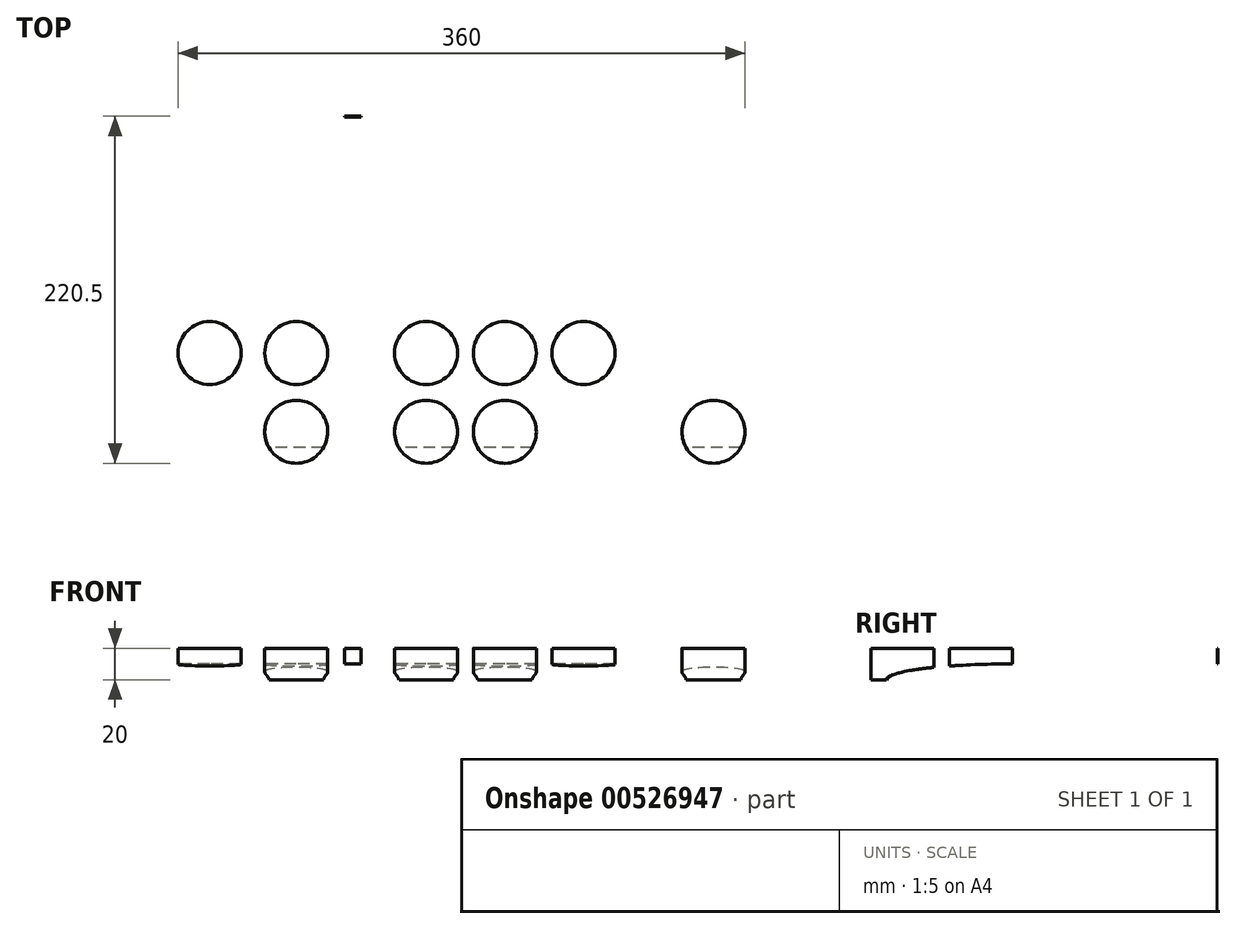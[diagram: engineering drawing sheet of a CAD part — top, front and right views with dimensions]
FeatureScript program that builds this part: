
annotation { "Feature Type Name" : "Feature", "Feature Type Description" : "" }
export const myFeature = defineFeature(function(context is Context, id is Id, definition is map)
    precondition{}
    {
        {
            var Q0;
            Q0=qCreatedBy(makeId("Top.planeOp"),FACE);
            var sketch = newSketch(context, id + "F0", { "sketchPlane" : qUnion([Q0])});
            skLineSegment(sketch, "E0.bottom", {"start": v(-365, 200) * mm, "end": v(365, 200) * mm});
            skLineSegment(sketch, "E0.top", {"start": v(-365, -200) * mm, "end": v(365, -200) * mm});
            skLineSegment(sketch, "E0.left", {"start": v(-365, 200) * mm, "end": v(-365, -200) * mm});
            skLineSegment(sketch, "E0.right", {"start": v(365, 200) * mm, "end": v(365, -200) * mm});
            skPoint(sketch, "E0.middle", {"position": v(0, 0) * mm});
            skEllipticalArc(sketch, "E1", {});
            skEllipticalArc(sketch, "E2.MirrorCS", {});
            skEllipticalArc(sketch, "E3.MirrorCS", {});
            skEllipticalArc(sketch, "E4.MirrorCS", {});
            skLineSegment(sketch, "E5", {"start": v(-365, 200) * mm, "end": v(-105, 200) * mm});
            skLineSegment(sketch, "E6", {"start": v(-365, 200) * mm, "end": v(-365, 50) * mm});
            skLineSegment(sketch, "E7", {"start": v(-365, -200) * mm, "end": v(-365, -50) * mm});
            skLineSegment(sketch, "E8", {"start": v(-365, -200) * mm, "end": v(-182.5, -200) * mm});
            skLineSegment(sketch, "E9", {"start": v(365, 200) * mm, "end": v(105, 200) * mm});
            skLineSegment(sketch, "E10", {"start": v(182.5, -200.11) * mm, "end": v(365, -200) * mm});
            skPoint(sketch, "E11", {"position": v(0, 200) * mm});
            skLineSegment(sketch, "E12", {"start": v(0, 200) * mm, "end": v(-130, 200) * mm});
            skLineSegment(sketch, "E13.MirrorCS", {"start": v(0, -200) * mm, "end": v(-130, -200) * mm});
            skLineSegment(sketch, "E14.MirrorCS", {"start": v(5, 200) * mm, "end": v(130, 200) * mm});
            skLineSegment(sketch, "E15.MirrorCS", {"start": v(-72.5, -200) * mm, "end": v(52.5, -200) * mm});
            skCircle(sketch, "E16", {"center": v(-278.75, 100) * mm, "radius": 20 * mm});
            skCircle(sketch, "E17", {"center": v(-223.75, 150) * mm, "radius": 20 * mm});
            skCircle(sketch, "E18", {"center": v(-223.75, 100) * mm, "radius": 20 * mm});
            skCircle(sketch, "E19", {"center": v(-141.25, 100) * mm, "radius": 20 * mm});
            skCircle(sketch, "E20", {"center": v(-141.25, 150) * mm, "radius": 20 * mm});
            skCircle(sketch, "E21", {"center": v(-91.25, 100) * mm, "radius": 20 * mm});
            skCircle(sketch, "E22", {"center": v(-91.25, 150) * mm, "radius": 20 * mm});
            skCircle(sketch, "E23", {"center": v(-41.25, 100) * mm, "radius": 20 * mm});
            skCircle(sketch, "E24.MirrorC", {"center": v(-41.25, 150) * mm, "radius": 20 * mm});
            skCircle(sketch, "E25.MirrorC", {"center": v(-278.75, -100) * mm, "radius": 20 * mm});
            skCircle(sketch, "E26.MirrorC", {"center": v(-223.75, -150) * mm, "radius": 20 * mm});
            skCircle(sketch, "E27.MirrorC", {"center": v(-223.75, -100) * mm, "radius": 20 * mm});
            skCircle(sketch, "E28.MirrorC", {"center": v(-141.25, -100) * mm, "radius": 20 * mm});
            skCircle(sketch, "E29.MirrorC", {"center": v(-141.25, -150) * mm, "radius": 20 * mm});
            skCircle(sketch, "E30.MirrorC", {"center": v(-91.25, -100) * mm, "radius": 20 * mm});
            skCircle(sketch, "E31.MirrorC", {"center": v(-41.25, -100) * mm, "radius": 20 * mm});
            skCircle(sketch, "E32.MirrorC", {"center": v(-91.25, -150) * mm, "radius": 20 * mm});
            skCircle(sketch, "E33.MirrorC", {"center": v(-41.25, -150) * mm, "radius": 20 * mm});
            skCircle(sketch, "E34.MirrorC", {"center": v(-222.5, -10) * mm, "radius": 20 * mm});
            skLineSegment(sketch, "E35.bottom", {"start": v(210, 15) * mm, "end": v(-210, 15) * mm});
            skLineSegment(sketch, "E35.top", {"start": v(210, -15) * mm, "end": v(-210, -15) * mm});
            skLineSegment(sketch, "E35.left", {"start": v(210, 15) * mm, "end": v(210, -15) * mm});
            skLineSegment(sketch, "E35.right", {"start": v(-210, 15) * mm, "end": v(-210, -15) * mm});
            skLineSegment(sketch, "E36", {"start": v(-365, -50) * mm, "end": v(365, -50) * mm});
            skLineSegment(sketch, "E37", {"start": v(-365, 50) * mm, "end": v(365, 50) * mm});
            skLineSegment(sketch, "E38", {"start": v(-182.5, -200) * mm, "end": v(-182.5, -40.61) * mm});
            skLineSegment(sketch, "E39", {"start": v(0, -200) * mm, "end": v(0, -50) * mm});
            skLineSegment(sketch, "E40", {"start": v(182.5, -200.11) * mm, "end": v(182.4, -40.7) * mm});
            skLineSegment(sketch, "E41.trimOffspring", {"start": v(-182.5, 40.61) * mm, "end": v(-182.5, 200) * mm});
            skLineSegment(sketch, "E42.trimOffspring", {"start": v(-182.5, -15) * mm, "end": v(-182.5, 15) * mm});
            skLineSegment(sketch, "E43.trimOffspring", {"start": v(182.39, -15) * mm, "end": v(182.37, 15) * mm});
            skLineSegment(sketch, "E44.trimOffspring", {"start": v(182.35, 40.73) * mm, "end": v(182.25, 200) * mm});
            skCircle(sketch, "E45", {"center": v(-272.5, 10) * mm, "radius": 20 * mm});
            skCircle(sketch, "E46.MirrorC", {"center": v(-322.5, -8.74) * mm, "radius": 20 * mm});
            skCircle(sketch, "E47.MirrorC", {"center": v(-142.5, -10) * mm, "radius": 20 * mm});
            skCircle(sketch, "E48.MirrorC", {"center": v(-92.5, 10) * mm, "radius": 20 * mm});
            skCircle(sketch, "E49.MirrorC", {"center": v(-42.5, -8.74) * mm, "radius": 20 * mm});
            skCircle(sketch, "E50.MirrorC", {"center": v(42.5, -8.74) * mm, "radius": 20 * mm});
            skCircle(sketch, "E51.MirrorC", {"center": v(142.5, -10) * mm, "radius": 20 * mm});
            skCircle(sketch, "E52.MirrorC", {"center": v(92.5, 10) * mm, "radius": 20 * mm});
            skCircle(sketch, "E53.MirrorC", {"center": v(222.5, -10) * mm, "radius": 20 * mm});
            skCircle(sketch, "E54.MirrorC", {"center": v(272.5, 10) * mm, "radius": 20 * mm});
            skCircle(sketch, "E55.MirrorC", {"center": v(322.5, -8.74) * mm, "radius": 20 * mm});
            skCircle(sketch, "E56.MirrorC", {"center": v(223.75, -100) * mm, "radius": 20 * mm});
            skCircle(sketch, "E57.MirrorC", {"center": v(223.75, -150) * mm, "radius": 20 * mm});
            skCircle(sketch, "E58.MirrorC", {"center": v(278.75, -100) * mm, "radius": 20 * mm});
            skCircle(sketch, "E59.MirrorC", {"center": v(141.25, -100) * mm, "radius": 20 * mm});
            skCircle(sketch, "E60.MirrorC", {"center": v(141.25, -150) * mm, "radius": 20 * mm});
            skCircle(sketch, "E61.MirrorC", {"center": v(91.25, -150) * mm, "radius": 20 * mm});
            skCircle(sketch, "E62.MirrorC", {"center": v(91.25, -100) * mm, "radius": 20 * mm});
            skCircle(sketch, "E63.MirrorC", {"center": v(41.25, -100) * mm, "radius": 20 * mm});
            skCircle(sketch, "E64.MirrorC", {"center": v(41.25, -150) * mm, "radius": 20 * mm});
            skCircle(sketch, "E65.MirrorC", {"center": v(41.25, 100) * mm, "radius": 20 * mm});
            skCircle(sketch, "E66.MirrorC", {"center": v(91.25, 100) * mm, "radius": 20 * mm});
            skCircle(sketch, "E67.MirrorC", {"center": v(141.25, 100) * mm, "radius": 20 * mm});
            skCircle(sketch, "E68.MirrorC", {"center": v(223.75, 100) * mm, "radius": 20 * mm});
            skCircle(sketch, "E69.MirrorC", {"center": v(278.75, 100) * mm, "radius": 20 * mm});
            skCircle(sketch, "E70.MirrorC", {"center": v(223.75, 150) * mm, "radius": 20 * mm});
            skCircle(sketch, "E71.MirrorC", {"center": v(141.25, 150) * mm, "radius": 20 * mm});
            skCircle(sketch, "E72.MirrorC", {"center": v(91.25, 150) * mm, "radius": 20 * mm});
            skCircle(sketch, "E73.MirrorC", {"center": v(41.25, 150) * mm, "radius": 20 * mm});
            const initialGuessF0  = {"E1": [0.215000023161019, -0.00011114199246731203, 0, -1, 0.20000000103052606, 0.15, 6.249845643425636, 1.5707963267948966], "E2.MirrorCS": [-0.215, -0.00011114199246737072, 0, -1, 0.2, 0.15, 4.711833270393751, 0.03333950926130193], "E3.MirrorCS": [-0.215, 0.00011114199246727815, 0, 1, 0.2, 0.15, 6.249845797918284, 1.5707963267948966], "E4.MirrorCS": [0.215, 0.00011114199246735796, 0, 1, 0.2, 0.15, 4.711277560231201, 0.03333950926130226]};
            skSetInitialGuess(sketch, initialGuessF0);
            skSolve(sketch);
        }
        {
            var Q0;
            Q0=qCreatedBy(makeId("Top.planeOp"),FACE);
            cPlane(context, id + "F1", {"entities" : qUnion([Q0]), "cplaneType" : CPlaneType.OFFSET, "offset" : 20 * mm, "width" : 150 * mm, "height" : 150 * mm});
        }
        {
            var Q0;
            Q0=qCreatedBy(id+"F1.planeOp",FACE);
            var sketch = newSketch(context, id + "F2", { "sketchPlane" : qUnion([Q0])});
            skLineSegment(sketch, "E74.bottom", {"start": v(0, 0) * mm, "end": v(365, 0) * mm});
            skLineSegment(sketch, "E74.top", {"start": v(0, -200) * mm, "end": v(210, -200) * mm});
            skLineSegment(sketch, "E74.left", {"start": v(0, 0) * mm, "end": v(0, -200) * mm});
            skLineSegment(sketch, "E75", {"start": v(0, -15) * mm, "end": v(364.58, -15) * mm});
            skLineSegment(sketch, "E76", {"start": v(0, -170) * mm, "end": v(294.02, -170) * mm});
            skLineSegment(sketch, "E77", {"start": v(330, 0) * mm, "end": v(330, -128.4) * mm});
            skLineSegment(sketch, "E78", {"start": v(215, 0) * mm, "end": v(215, -200) * mm});
            skPoint(sketch, "E79", {"position": v(215, -200) * mm});
            skPoint(sketch, "E80", {"position": v(365, 0) * mm});
            skLineSegment(sketch, "E81", {"start": v(275, 0) * mm, "end": v(275, -183.3) * mm});
            skLineSegment(sketch, "E82", {"start": v(275, -140) * mm, "end": v(322.12, -140) * mm});
            skPoint(sketch, "E83", {"position": v(215, -170) * mm});
            skPoint(sketch, "E84", {"position": v(330, 0) * mm});
            skPoint(sketch, "E85", {"position": v(275, -140) * mm});
            skPoint(sketch, "E86", {"position": v(330, -140) * mm});
            skPoint(sketch, "E87", {"position": v(275, -185) * mm});
            skLineSegment(sketch, "E88", {"start": v(315, -149.07) * mm, "end": v(315, 0) * mm});
            skLineSegment(sketch, "E89", {"start": v(210, 0) * mm, "end": v(210, -200) * mm});
            skEllipticalArc(sketch, "E90.trimOffspring", {});
            skEllipticalArc(sketch, "E91", {});
            skPoint(sketch, "E92.orphan", {"position": v(365, -170) * mm});
            skPoint(sketch, "E93.trimOffspring.end.orphan", {"position": v(330, -200) * mm});
            skPoint(sketch, "E94.orphan", {"position": v(365, -200) * mm});
            skPoint(sketch, "E95.orphan", {"position": v(365, -15) * mm});
            skLineSegment(sketch, "E96.MirrorCS", {"start": v(0, 0) * mm, "end": v(-365, 0) * mm});
            skLineSegment(sketch, "E97.MirrorCS", {"start": v(0, -15) * mm, "end": v(-364.58, -15) * mm});
            skLineSegment(sketch, "E98.MirrorCS", {"start": v(0, -170) * mm, "end": v(-294.02, -170) * mm});
            skLineSegment(sketch, "E99.MirrorCS", {"start": v(0, -200) * mm, "end": v(-210, -200) * mm});
            skLineSegment(sketch, "E100.MirrorCS", {"start": v(-210, 0) * mm, "end": v(-210, -200) * mm});
            skLineSegment(sketch, "E101.MirrorCS", {"start": v(-215, 0) * mm, "end": v(-215, -200) * mm});
            skEllipticalArc(sketch, "E102.MirrorCS", {});
            skEllipticalArc(sketch, "E103.MirrorCS", {});
            skLineSegment(sketch, "E104.MirrorCS", {"start": v(-275, 0) * mm, "end": v(-275, -183.3) * mm});
            skLineSegment(sketch, "E105.MirrorCS", {"start": v(-275, -140) * mm, "end": v(-322.12, -140) * mm});
            skLineSegment(sketch, "E106.MirrorCS", {"start": v(-315, -149.07) * mm, "end": v(-315, 0) * mm});
            skLineSegment(sketch, "E107.MirrorCS", {"start": v(-330, 0) * mm, "end": v(-330, -128.4) * mm});
            skLineSegment(sketch, "E108.MirrorCS", {"start": v(0, 15) * mm, "end": v(-364.58, 15) * mm});
            skLineSegment(sketch, "E109.MirrorCS", {"start": v(0, 15) * mm, "end": v(364.58, 15) * mm});
            skEllipticalArc(sketch, "E110.MirrorCS", {});
            skLineSegment(sketch, "E111.MirrorCS", {"start": v(-330, 0) * mm, "end": v(-330, 128.4) * mm});
            skLineSegment(sketch, "E112.MirrorCS", {"start": v(-315, 149.07) * mm, "end": v(-315, 0) * mm});
            skLineSegment(sketch, "E113.MirrorCS", {"start": v(-275, 0) * mm, "end": v(-275, 183.3) * mm});
            skLineSegment(sketch, "E114.MirrorCS", {"start": v(-215, 0) * mm, "end": v(-215, 200) * mm});
            skLineSegment(sketch, "E115.MirrorCS", {"start": v(-210, 0) * mm, "end": v(-210, 200) * mm});
            skLineSegment(sketch, "E116.MirrorCS", {"start": v(0, 0) * mm, "end": v(0, 200) * mm});
            skLineSegment(sketch, "E117.MirrorCS", {"start": v(210, 0) * mm, "end": v(210, 200) * mm});
            skLineSegment(sketch, "E118.MirrorCS", {"start": v(215, 0) * mm, "end": v(215, 200) * mm});
            skLineSegment(sketch, "E119.MirrorCS", {"start": v(275, 0) * mm, "end": v(275, 183.3) * mm});
            skLineSegment(sketch, "E120.MirrorCS", {"start": v(315, 149.07) * mm, "end": v(315, 0) * mm});
            skLineSegment(sketch, "E121.MirrorCS", {"start": v(330, 0) * mm, "end": v(330, 128.4) * mm});
            skEllipticalArc(sketch, "E122.MirrorCS", {});
            skEllipticalArc(sketch, "E123.MirrorCS", {});
            skEllipticalArc(sketch, "E124.MirrorCS", {});
            skLineSegment(sketch, "E125.MirrorCS", {"start": v(-275, 140) * mm, "end": v(-322.12, 140) * mm});
            skLineSegment(sketch, "E126.MirrorCS", {"start": v(0, 170) * mm, "end": v(-294.02, 170) * mm});
            skLineSegment(sketch, "E127.MirrorCS", {"start": v(0, 170) * mm, "end": v(294.02, 170) * mm});
            skLineSegment(sketch, "E128.MirrorCS", {"start": v(0, 200) * mm, "end": v(210, 200) * mm});
            skLineSegment(sketch, "E129.MirrorCS", {"start": v(0, 200) * mm, "end": v(-210, 200) * mm});
            skLineSegment(sketch, "E130.MirrorCS", {"start": v(275, 140) * mm, "end": v(322.12, 140) * mm});
            const initialGuessF2  = {"E90.trimOffspring": [0.215, 0, 1, 0, 0.115, 0.17, 4.71238898038469, 6.283185307179586], "E91": [0.215, 0, 0, -1, 0.2, 0.15, 6.249845797918284, 1.5707963267948966], "E102.MirrorCS": [-0.215, 0, -1, 0, 0.115, 0.17, 6.283185307179586, 1.5707963267948966], "E103.MirrorCS": [-0.215, 0, 0, -1, 0.2, 0.15, 4.71238898038469, 0.03333950926130225], "E110.MirrorCS": [-0.215, 0, 0, 1, 0.2, 0.15, 6.249845797918284, 1.5707963267948966], "E122.MirrorCS": [0.215, 0, 0, 1, 0.2, 0.15, 4.71238898038469, 0.03333950926130225], "E123.MirrorCS": [0.215, 0, 1, 0, 0.115, 0.17, 6.283185307179586, 1.5707963267948966], "E124.MirrorCS": [-0.215, 0, -1, 0, 0.115, 0.17, 4.71238898038469, 6.283185307179586]};
            skSetInitialGuess(sketch, initialGuessF2);
            skSolve(sketch);
        }
        {
            var Q0;
            Q0=qCreatedBy(makeId("Right.planeOp"),FACE);
            var sketch = newSketch(context, id + "F3", { "sketchPlane" : qUnion([Q0])});
            skPoint(sketch, "E131.middle", {"position": v(0, 20) * mm});
            skPoint(sketch, "E132", {"position": v(170, 0) * mm});
            skPoint(sketch, "E133", {"position": v(160, 0) * mm});
            skLineSegment(sketch, "E134.bottom", {"start": v(15, 10.07) * mm, "end": v(80, 10.07) * mm});
            skPoint(sketch, "E135", {"position": v(80, 10.07) * mm});
            skEllipticalArc(sketch, "E136", {});
            skEllipticalArc(sketch, "E137", {});
            skLineSegment(sketch, "E138", {"start": v(0, 20) * mm, "end": v(0, 10.04) * mm});
            skLineSegment(sketch, "E139", {"start": v(0, 20) * mm, "end": v(200, 20) * mm});
            skLineSegment(sketch, "E140", {"start": v(200, 20) * mm, "end": v(0, 20) * mm});
            skLineSegment(sketch, "E141", {"start": v(160, 0) * mm, "end": v(170, 0) * mm});
            skPoint(sketch, "E142.orphan", {"position": v(-200, 20) * mm});
            skLineSegment(sketch, "E143.MirrorCS", {"start": v(-200, 20) * mm, "end": v(0, 20) * mm});
            skLineSegment(sketch, "E144.MirrorCS", {"start": v(-15, 10.07) * mm, "end": v(-80, 10.07) * mm});
            skEllipticalArc(sketch, "E145.MirrorCS", {});
            skLineSegment(sketch, "E146.MirrorCS", {"start": v(-160, 0) * mm, "end": v(-170, 0) * mm});
            skEllipticalArc(sketch, "E147.MirrorCS", {});
            skLineSegment(sketch, "E148.top", {"start": v(-15, 12) * mm, "end": v(15, 12) * mm});
            skLineSegment(sketch, "E148.left", {"start": v(-15, 10.07) * mm, "end": v(-15, 12) * mm});
            skLineSegment(sketch, "E148.right", {"start": v(15, 10.07) * mm, "end": v(15, 12) * mm});
            skLineSegment(sketch, "E149.bottom", {"start": v(15, 18) * mm, "end": v(-15, 18) * mm});
            skLineSegment(sketch, "E149.top", {"start": v(15, 12) * mm, "end": v(-15, 12) * mm});
            skLineSegment(sketch, "E149.left", {"start": v(15, 18) * mm, "end": v(15, 12) * mm});
            skLineSegment(sketch, "E149.right", {"start": v(-15, 18) * mm, "end": v(-15, 12) * mm});
            skLineSegment(sketch, "E150", {"start": v(170, 0) * mm, "end": v(170.12, 20) * mm});
            skLineSegment(sketch, "E151", {"start": v(-170, 0) * mm, "end": v(-170.12, 20) * mm});
            skLineSegment(sketch, "E152", {"start": v(-15, 12) * mm, "end": v(-15, 10.07) * mm});
            skLineSegment(sketch, "E153.bottom", {"start": v(-200, 20) * mm, "end": v(-170, 20) * mm});
            skLineSegment(sketch, "E153.top", {"start": v(-200, 0) * mm, "end": v(-170, 0) * mm});
            skLineSegment(sketch, "E153.left", {"start": v(-200, 20) * mm, "end": v(-200, 0) * mm});
            skLineSegment(sketch, "E153.right", {"start": v(-170, 20) * mm, "end": v(-170, 0) * mm});
            skLineSegment(sketch, "E154.MirrorCS", {"start": v(200, 0) * mm, "end": v(170, 0) * mm});
            skLineSegment(sketch, "E155.MirrorCS", {"start": v(200, 20) * mm, "end": v(200, 0) * mm});
            skLineSegment(sketch, "E156", {"start": v(80, 10.07) * mm, "end": v(80, 20) * mm});
            skLineSegment(sketch, "E157", {"start": v(160, 0) * mm, "end": v(160, 20) * mm});
            skLineSegment(sketch, "E158", {"start": v(149.2, 20) * mm, "end": v(149.2, 5.05) * mm});
            skLineSegment(sketch, "E159", {"start": v(140.08, 20) * mm, "end": v(140.08, 6.65) * mm});
            skLineSegment(sketch, "E160", {"start": v(128.23, 20) * mm, "end": v(128.23, 8.04) * mm});
            skLineSegment(sketch, "E161", {"start": v(102.69, 20) * mm, "end": v(102.69, 9.66) * mm});
            skLineSegment(sketch, "E162.MirrorCS", {"start": v(-80, 10.07) * mm, "end": v(-80, 20) * mm});
            skLineSegment(sketch, "E163.MirrorCS", {"start": v(-102.69, 20) * mm, "end": v(-102.69, 9.66) * mm});
            skLineSegment(sketch, "E164.MirrorCS", {"start": v(-128.23, 20) * mm, "end": v(-128.23, 8.04) * mm});
            skLineSegment(sketch, "E165.MirrorCS", {"start": v(-140.08, 20) * mm, "end": v(-140.08, 6.65) * mm});
            skLineSegment(sketch, "E166.MirrorCS", {"start": v(-149.2, 20) * mm, "end": v(-149.2, 5.05) * mm});
            skLineSegment(sketch, "E167.MirrorCS", {"start": v(-160, 0) * mm, "end": v(-160, 20) * mm});
            skLineSegment(sketch, "E168", {"start": v(45, 20) * mm, "end": v(45, 10.07) * mm});
            skLineSegment(sketch, "E169.MirrorCS", {"start": v(-45, 20) * mm, "end": v(-45, 10.07) * mm});
            const initialGuessF3  = {"E136": [0.17012490332126617, 0.02, -0.006245044279577429, -0.9999804995208388, 0.020000390017188747, 0.02987581400604767, 6.283185307179586, 1.580124845260153], "E137": [0.08, 0, 0, 1, 0.01007139225942586, 0.08, 4.71238898038469, 6.283185307179586], "E145.MirrorCS": [-0.08, 0, 0, 1, 0.01007139225942586, 0.08, 6.283185307179586, 1.5707963267948966], "E147.MirrorCS": [-0.17012490332126617, 0.02, 0.006245044279579518, -0.9999804995208388, 0.020000390017188747, 0.02987581400604767, 4.703060461919433, 6.283185307179586]};
            skSetInitialGuess(sketch, initialGuessF3);
            skSolve(sketch);
        }
        {
            var Q0;
            Q0=qCreatedBy(makeId("Front.planeOp"),FACE);
            var sketch = newSketch(context, id + "F4", { "sketchPlane" : qUnion([Q0])});
            skLineSegment(sketch, "E170", {"start": v(0, 20) * mm, "end": v(365, 20) * mm});
            skPoint(sketch, "E171", {"position": v(210, 20) * mm});
            skLineSegment(sketch, "E172", {"start": v(210, 18) * mm, "end": v(210, 12) * mm});
            skPoint(sketch, "E173", {"position": v(315, 20) * mm});
            skLineSegment(sketch, "E174", {"start": v(315, 18) * mm, "end": v(315, 0) * mm});
            skLineSegment(sketch, "E175", {"start": v(0, 12) * mm, "end": v(0, 20) * mm});
            skLineSegment(sketch, "E176", {"start": v(210, 12) * mm, "end": v(0, 12) * mm});
            skPoint(sketch, "E177", {"position": v(365.07, 0) * mm});
            skPoint(sketch, "E178", {"position": v(365, 20) * mm});
            skEllipticalArc(sketch, "E179", {});
            skLineSegment(sketch, "E180", {"start": v(315, 18) * mm, "end": v(210, 18) * mm});
            skLineSegment(sketch, "E181.MirrorCS", {"start": v(0, 20) * mm, "end": v(-365, 20) * mm});
            skLineSegment(sketch, "E182.MirrorCS", {"start": v(-210, 12) * mm, "end": v(0, 12) * mm});
            skLineSegment(sketch, "E183.MirrorCS", {"start": v(-210, 18) * mm, "end": v(-210, 12) * mm});
            skLineSegment(sketch, "E184.MirrorCS", {"start": v(-315, 18) * mm, "end": v(-210, 18) * mm});
            skLineSegment(sketch, "E185.MirrorCS", {"start": v(-315, 18) * mm, "end": v(-315, 0) * mm});
            skEllipticalArc(sketch, "E186.MirrorCS", {});
            skPoint(sketch, "E187", {"position": v(245, 20) * mm});
            skPoint(sketch, "E188", {"position": v(245, 10.07) * mm});
            skPoint(sketch, "E189", {"position": v(325, 20) * mm});
            skPoint(sketch, "E190", {"position": v(335, 20) * mm});
            skLineSegment(sketch, "E191", {"start": v(335, 20) * mm, "end": v(335, 10.07) * mm});
            skLineSegment(sketch, "E192", {"start": v(335, 10.07) * mm, "end": v(0, 10.07) * mm});
            skLineSegment(sketch, "E193.MirrorCS", {"start": v(-335, 10.07) * mm, "end": v(0, 10.07) * mm});
            skLineSegment(sketch, "E194.MirrorCS", {"start": v(-335, 20) * mm, "end": v(-335, 10.07) * mm});
            skLineSegment(sketch, "E195", {"start": v(365, 20) * mm, "end": v(365.07, 0) * mm});
            skLineSegment(sketch, "E196", {"start": v(315, 0) * mm, "end": v(365.07, 0) * mm});
            skLineSegment(sketch, "E197.MirrorCS", {"start": v(-365, 20) * mm, "end": v(-365.07, 0) * mm});
            skLineSegment(sketch, "E198.MirrorCS", {"start": v(-315, 0) * mm, "end": v(-365.07, 0) * mm});
            skLineSegment(sketch, "E199", {"start": v(335, 10.07) * mm, "end": v(335, 1.67) * mm});
            skLineSegment(sketch, "E200.MirrorCS", {"start": v(-335, 10.07) * mm, "end": v(-335, 1.67) * mm});
            skLineSegment(sketch, "E201", {"start": v(-315, 18) * mm, "end": v(-315, 20) * mm});
            skLineSegment(sketch, "E202", {"start": v(-210, 18) * mm, "end": v(-210, 20) * mm});
            skLineSegment(sketch, "E203.MirrorCS", {"start": v(210, 18) * mm, "end": v(210, 20) * mm});
            skLineSegment(sketch, "E204.MirrorCS", {"start": v(315, 18) * mm, "end": v(315, 20) * mm});
            skPoint(sketch, "E205", {"position": v(275, 20) * mm});
            skPoint(sketch, "E206.MirrorP", {"position": v(-275, 20) * mm});
            skLineSegment(sketch, "E207", {"start": v(275, 20) * mm, "end": v(275, 18) * mm});
            skLineSegment(sketch, "E208.MirrorCS", {"start": v(-275, 20) * mm, "end": v(-275, 18) * mm});
            skPoint(sketch, "E209", {"position": v(-333.25, 14.9) * mm});
            skPoint(sketch, "E210", {"position": v(-218.12, 14.9) * mm});
            skPoint(sketch, "E211", {"position": v(-78.75, 14.9) * mm});
            const initialGuessF4  = {"E179": [0.315, 0.02, 1, 0, 0.05, 0.02, 4.71238898038469, 0], "E186.MirrorCS": [-0.315, 0.02, -1, 0, 0.05, 0.02, 0, 1.5707963267948966]};
            skSetInitialGuess(sketch, initialGuessF4);
            skSolve(sketch);
        }
        {
            var Q0;
            Q0=qSketchRegion(id+"F2",true);
            var Q1;
            {var subQ0=sQuery(id+"F2.wireOp",EDGE,"E125.MirrorCS");var subQ1=sQuery(id+"F2.wireOp",EDGE,"E112.MirrorCS");var subQ2=makeQuery(id+"F2.imprint","INTERSECT",VERTEX,{"derivedFrom":[subQ1,subQ0]});Q1=makeQuery(id+"F2.imprint","IMPRINT",FACE,{"disambiguationData":[TD([[makeQuery(id+"F2.imprint","IMPRINT",EDGE,{"disambiguationData":[TD([[subQ2,-1.0]])],"derivedFrom":subQ1}),1.0]])]});}
            var Q2;
            {var subQ0=sQuery(id+"F2.wireOp",EDGE,"E124.MirrorCS");var subQ1=sQuery(id+"F2.wireOp",EDGE,"E113.MirrorCS");var subQ2=makeQuery(id+"F2.imprint","INTERSECT",VERTEX,{"derivedFrom":[subQ1,subQ0]});Q2=makeQuery(id+"F2.imprint","IMPRINT",FACE,{"disambiguationData":[TD([[makeQuery(id+"F2.imprint","IMPRINT",EDGE,{"disambiguationData":[TD([[subQ2,-1.0]])],"derivedFrom":subQ1}),-1.0]])]});}
            var Q3;
            {var subQ0=sQuery(id+"F2.wireOp",EDGE,"E123.MirrorCS");var subQ1=sQuery(id+"F2.wireOp",EDGE,"E119.MirrorCS");var subQ2=makeQuery(id+"F2.imprint","INTERSECT",VERTEX,{"derivedFrom":[subQ1,subQ0]});Q3=makeQuery(id+"F2.imprint","IMPRINT",FACE,{"disambiguationData":[TD([[makeQuery(id+"F2.imprint","IMPRINT",EDGE,{"disambiguationData":[TD([[subQ2,-1.0]])],"derivedFrom":subQ1}),1.0]])]});}
            var Q4;
            {var subQ0=sQuery(id+"F2.wireOp",EDGE,"E130.MirrorCS");var subQ1=sQuery(id+"F2.wireOp",EDGE,"E120.MirrorCS");var subQ2=makeQuery(id+"F2.imprint","INTERSECT",VERTEX,{"derivedFrom":[subQ1,subQ0]});Q4=makeQuery(id+"F2.imprint","IMPRINT",FACE,{"disambiguationData":[TD([[makeQuery(id+"F2.imprint","IMPRINT",EDGE,{"disambiguationData":[TD([[subQ2,-1.0]])],"derivedFrom":subQ1}),-1.0]])]});}
            var Q5;
            {var subQ0=sQuery(id+"F2.wireOp",EDGE,"E90.trimOffspring");var subQ1=sQuery(id+"F2.wireOp",EDGE,"E82");var subQ2=makeQuery(id+"F2.imprint","INTERSECT",VERTEX,{"derivedFrom":[subQ1,subQ0]});Q5=makeQuery(id+"F2.imprint","IMPRINT",FACE,{"disambiguationData":[TD([[makeQuery(id+"F2.imprint","IMPRINT",EDGE,{"disambiguationData":[TD([[subQ2,-1.0]])],"derivedFrom":subQ1}),1.0]])]});}
            var Q6;
            {var subQ1=sQuery(id+"F2.wireOp",EDGE,"E76");var subQ3=sQuery(id+"F2.wireOp",EDGE,"E81");var subQ4=makeQuery(id+"F2.imprint","INTERSECT",VERTEX,{"derivedFrom":[subQ1,subQ3]});Q6=makeQuery(id+"F2.imprint","IMPRINT",FACE,{"disambiguationData":[TD([[makeQuery(id+"F2.imprint","IMPRINT",EDGE,{"disambiguationData":[TD([[subQ4,1.0]])],"derivedFrom":subQ3}),-1.0]])]});}
            var Q7;
            {var subQ1=sQuery(id+"F2.wireOp",EDGE,"E98.MirrorCS");var subQ3=sQuery(id+"F2.wireOp",EDGE,"E104.MirrorCS");var subQ4=makeQuery(id+"F2.imprint","INTERSECT",VERTEX,{"derivedFrom":[subQ1,subQ3]});Q7=makeQuery(id+"F2.imprint","IMPRINT",FACE,{"disambiguationData":[TD([[makeQuery(id+"F2.imprint","IMPRINT",EDGE,{"disambiguationData":[TD([[subQ4,1.0]])],"derivedFrom":subQ3}),1.0]])]});}
            var Q8;
            {var subQ0=sQuery(id+"F2.wireOp",EDGE,"E106.MirrorCS");var subQ1=sQuery(id+"F2.wireOp",EDGE,"E102.MirrorCS");var subQ2=makeQuery(id+"F2.imprint","INTERSECT",VERTEX,{"derivedFrom":[subQ1,subQ0]});Q8=makeQuery(id+"F2.imprint","IMPRINT",FACE,{"disambiguationData":[TD([[makeQuery(id+"F2.imprint","IMPRINT",EDGE,{"disambiguationData":[TD([[subQ2,-1.0]])],"derivedFrom":subQ1}),-1.0]])]});}
            extrude(context, id + "F5", {"entities" : qUnion([Q0, Q1, Q2, Q3, Q4, Q5, Q6, Q7, Q8]), "oppositeDirection" : true, "depth" : 20 * mm, "offsetDistance" : 25 * mm});
        }
        {
            var Q0;
            {var subQ0=sQuery(id+"F3.wireOp",EDGE,"E149.right");Q0=makeQuery(id+"F3.imprint","IMPRINT",FACE,{"disambiguationData":[TD([[makeQuery(id+"F3.imprint","IMPRINT",EDGE,{"derivedFrom":subQ0}),-1.0]])]});}
            var Q1;
            {var subQ0=sQuery(id+"F3.wireOp",EDGE,"E149.left");Q1=makeQuery(id+"F3.imprint","IMPRINT",FACE,{"disambiguationData":[TD([[makeQuery(id+"F3.imprint","IMPRINT",EDGE,{"derivedFrom":subQ0}),1.0]])]});}
            extrude(context, id + "F6", {"entities" : qUnion([Q0, Q1]), "operationType" : NewBodyOperationType.ADD, "depth" : 420 * mm, "offsetDistance" : 25 * mm, "symmetric" : true});
        }
        {
            var Q0;
            {var subQ0=sQuery(id+"F3.wireOp",EDGE,"E156");Q0=makeQuery(id+"F3.imprint","IMPRINT",FACE,{"disambiguationData":[TD([[makeQuery(id+"F3.imprint","IMPRINT",EDGE,{"derivedFrom":subQ0}),-1.0]])]});}
            var Q1;
            {var subQ0=sQuery(id+"F3.wireOp",EDGE,"E160");Q1=makeQuery(id+"F3.imprint","IMPRINT",FACE,{"disambiguationData":[TD([[makeQuery(id+"F3.imprint","IMPRINT",EDGE,{"derivedFrom":subQ0}),-1.0]])]});}
            var Q2;
            {var subQ0=sQuery(id+"F3.wireOp",EDGE,"E159");Q2=makeQuery(id+"F3.imprint","IMPRINT",FACE,{"disambiguationData":[TD([[makeQuery(id+"F3.imprint","IMPRINT",EDGE,{"derivedFrom":subQ0}),-1.0]])]});}
            var Q3;
            {var subQ0=sQuery(id+"F3.wireOp",EDGE,"E158");Q3=makeQuery(id+"F3.imprint","IMPRINT",FACE,{"disambiguationData":[TD([[makeQuery(id+"F3.imprint","IMPRINT",EDGE,{"derivedFrom":subQ0}),-1.0]])]});}
            var Q4;
            {var subQ0=sQuery(id+"F3.wireOp",EDGE,"E157");Q4=makeQuery(id+"F3.imprint","IMPRINT",FACE,{"disambiguationData":[TD([[makeQuery(id+"F3.imprint","IMPRINT",EDGE,{"derivedFrom":subQ0}),1.0]])]});}
            var Q5;
            Q5=makeQuery(id+"F3.imprint","IMPRINT",FACE,{"disambiguationData":[TD([[makeQuery(id+"F3.imprint","IMPRINT",EDGE,{"derivedFrom":sQuery(id+"F3.wireOp",EDGE,"E141")}),1.0]])]});
            var Q6;
            {var subQ0=sQuery(id+"F3.wireOp",EDGE,"E162.MirrorCS");Q6=makeQuery(id+"F3.imprint","IMPRINT",FACE,{"disambiguationData":[TD([[makeQuery(id+"F3.imprint","IMPRINT",EDGE,{"derivedFrom":subQ0}),1.0]])]});}
            var Q7;
            {var subQ0=sQuery(id+"F3.wireOp",EDGE,"E163.MirrorCS");Q7=makeQuery(id+"F3.imprint","IMPRINT",FACE,{"disambiguationData":[TD([[makeQuery(id+"F3.imprint","IMPRINT",EDGE,{"derivedFrom":subQ0}),-1.0]])]});}
            var Q8;
            {var subQ0=sQuery(id+"F3.wireOp",EDGE,"E164.MirrorCS");Q8=makeQuery(id+"F3.imprint","IMPRINT",FACE,{"disambiguationData":[TD([[makeQuery(id+"F3.imprint","IMPRINT",EDGE,{"derivedFrom":subQ0}),-1.0]])]});}
            var Q9;
            {var subQ0=sQuery(id+"F3.wireOp",EDGE,"E165.MirrorCS");Q9=makeQuery(id+"F3.imprint","IMPRINT",FACE,{"disambiguationData":[TD([[makeQuery(id+"F3.imprint","IMPRINT",EDGE,{"derivedFrom":subQ0}),-1.0]])]});}
            var Q10;
            {var subQ0=sQuery(id+"F3.wireOp",EDGE,"E166.MirrorCS");Q10=makeQuery(id+"F3.imprint","IMPRINT",FACE,{"disambiguationData":[TD([[makeQuery(id+"F3.imprint","IMPRINT",EDGE,{"derivedFrom":subQ0}),-1.0]])]});}
            var Q11;
            Q11=makeQuery(id+"F3.imprint","IMPRINT",FACE,{"disambiguationData":[TD([[makeQuery(id+"F3.imprint","IMPRINT",EDGE,{"derivedFrom":sQuery(id+"F3.wireOp",EDGE,"E146.MirrorCS")}),-1.0]])]});
            var Q12;
            {var subQ0=sQuery(id+"F3.wireOp",EDGE,"E156");Q12=makeQuery(id+"F3.imprint","IMPRINT",FACE,{"disambiguationData":[TD([[makeQuery(id+"F3.imprint","IMPRINT",EDGE,{"derivedFrom":subQ0}),1.0]])]});}
            var Q13;
            {var subQ0=sQuery(id+"F3.wireOp",EDGE,"E162.MirrorCS");Q13=makeQuery(id+"F3.imprint","IMPRINT",FACE,{"disambiguationData":[TD([[makeQuery(id+"F3.imprint","IMPRINT",EDGE,{"derivedFrom":subQ0}),-1.0]])]});}
            extrude(context, id + "F7", {"entities" : qUnion([Q0, Q1, Q2, Q3, Q4, Q5, Q6, Q7, Q8, Q9, Q10, Q11, Q12, Q13]), "operationType" : NewBodyOperationType.ADD, "depth" : 520 * mm, "offsetDistance" : 25 * mm, "symmetric" : true});
        }
        {
            var Q0;
            Q0=makeQuery(id+"F4.imprint","IMPRINT",FACE,{"disambiguationData":[TD([[makeQuery(id+"F4.imprint","IMPRINT",EDGE,{"derivedFrom":sQuery(id+"F4.wireOp",EDGE,"E172")}),-1.0]])]});
            var Q1;
            {var subQ1=sQuery(id+"F4.wireOp",EDGE,"E179");Q1=makeQuery(id+"F4.imprint","IMPRINT",FACE,{"disambiguationData":[TD([[makeQuery(id+"F4.imprint","IMPRINT",EDGE,{"derivedFrom":subQ1}),1.0]])]});}
            var Q2;
            {var subQ2=sQuery(id+"F4.wireOp",EDGE,"E175");Q2=makeQuery(id+"F4.imprint","IMPRINT",FACE,{"disambiguationData":[TD([[makeQuery(id+"F4.imprint","IMPRINT",EDGE,{"derivedFrom":subQ2}),1.0]])]});}
            var Q3;
            {var subQ0=sQuery(id+"F4.wireOp",EDGE,"E186.MirrorCS");Q3=makeQuery(id+"F4.imprint","IMPRINT",FACE,{"disambiguationData":[TD([[makeQuery(id+"F4.imprint","IMPRINT",EDGE,{"derivedFrom":subQ0}),1.0]])]});}
            extrude(context, id + "F8", {"entities" : qUnion([Q0, Q1, Q2, Q3]), "operationType" : NewBodyOperationType.ADD, "depth" : 30 * mm, "offsetDistance" : 25 * mm, "symmetric" : true});
        }
        {
            var Q0;
            {var subQ0=sQuery(id+"F3.wireOp",EDGE,"E153.left");var subQ1=sQuery(id+"F3.wireOp",EDGE,"E147.MirrorCS");var subQ2=makeQuery(id+"F3.imprint","INTERSECT",VERTEX,{"derivedFrom":[subQ1,subQ0]});Q0=makeQuery(id+"F3.imprint","IMPRINT",FACE,{"disambiguationData":[TD([[makeQuery(id+"F3.imprint","IMPRINT",EDGE,{"disambiguationData":[TD([[subQ2,-1.0]])],"derivedFrom":subQ1}),-1.0]])]});}
            var Q1;
            {var subQ0=sQuery(id+"F3.wireOp",EDGE,"E155.MirrorCS");var subQ1=sQuery(id+"F3.wireOp",EDGE,"E136");var subQ2=makeQuery(id+"F3.imprint","INTERSECT",VERTEX,{"derivedFrom":[subQ1,subQ0]});Q1=makeQuery(id+"F3.imprint","IMPRINT",FACE,{"disambiguationData":[TD([[makeQuery(id+"F3.imprint","IMPRINT",EDGE,{"disambiguationData":[TD([[subQ2,1.0]])],"derivedFrom":subQ1}),-1.0]])]});}
            var Q2;
            Q2=sQuery(id+"F3.wireOp",EDGE,"E153.left");
            var Q3;
            Q3=sQuery(id+"F3.wireOp",EDGE,"E153.top");
            var Q4;
            Q4=sQuery(id+"F3.wireOp",EDGE,"E147.MirrorCS");
            extrude(context, id + "F9", {"entities" : qUnion([Q0, Q1]), "operationType" : NewBodyOperationType.REMOVE, "surfaceEntities" : qUnion([Q2, Q3, Q4]), "oppositeDirection" : true, "depth" : 730 * mm, "offsetDistance" : 25 * mm, "symmetric" : true});
        }
        {
            var Q0;
            Q0=makeQuery(id+"F4.imprint","IMPRINT",FACE,{"disambiguationData":[TD([[makeQuery(id+"F4.imprint","IMPRINT",EDGE,{"derivedFrom":sQuery(id+"F4.wireOp",EDGE,"E186.MirrorCS")}),-1.0]])]});
            var Q1;
            Q1=makeQuery(id+"F4.imprint","IMPRINT",FACE,{"disambiguationData":[TD([[makeQuery(id+"F4.imprint","IMPRINT",EDGE,{"derivedFrom":sQuery(id+"F4.wireOp",EDGE,"E179")}),-1.0]])]});
            extrude(context, id + "F10", {"entities" : qUnion([Q0, Q1]), "operationType" : NewBodyOperationType.REMOVE, "oppositeDirection" : true, "depth" : 400 * mm, "offsetDistance" : 25 * mm, "symmetric" : true});
        }
        {
            var Q0;
            Q0=makeQuery(id+"F4.imprint","IMPRINT",FACE,{"disambiguationData":[TD([[makeQuery(id+"F4.imprint","IMPRINT",EDGE,{"derivedFrom":sQuery(id+"F4.wireOp",EDGE,"E172")}),-1.0]])]});
            var Q1;
            {var subQ5=sQuery(id+"F4.wireOp",EDGE,"E199");Q1=makeQuery(id+"F4.imprint","IMPRINT",FACE,{"disambiguationData":[TD([[makeQuery(id+"F4.imprint","IMPRINT",EDGE,{"derivedFrom":subQ5}),-1.0]])]});}
            var Q2;
            {var subQ5=sQuery(id+"F4.wireOp",EDGE,"E200.MirrorCS");Q2=makeQuery(id+"F4.imprint","IMPRINT",FACE,{"disambiguationData":[TD([[makeQuery(id+"F4.imprint","IMPRINT",EDGE,{"derivedFrom":subQ5}),1.0]])]});}
            var Q3;
            {var subQ2=sQuery(id+"F4.wireOp",EDGE,"E175");Q3=makeQuery(id+"F4.imprint","IMPRINT",FACE,{"disambiguationData":[TD([[makeQuery(id+"F4.imprint","IMPRINT",EDGE,{"derivedFrom":subQ2}),1.0]])]});}
            var Q4;
            {var subQ0=sQuery(id+"F4.wireOp",EDGE,"E194.MirrorCS");Q4=makeQuery(id+"F4.imprint","IMPRINT",FACE,{"disambiguationData":[TD([[makeQuery(id+"F4.imprint","IMPRINT",EDGE,{"derivedFrom":subQ0}),1.0]])]});}
            var Q5;
            {var subQ1=sQuery(id+"F4.wireOp",EDGE,"E191");Q5=makeQuery(id+"F4.imprint","IMPRINT",FACE,{"disambiguationData":[TD([[makeQuery(id+"F4.imprint","IMPRINT",EDGE,{"derivedFrom":subQ1}),-1.0]])]});}
            extrude(context, id + "F11", {"entities" : qUnion([Q0, Q1, Q2, Q3, Q4, Q5]), "operationType" : NewBodyOperationType.ADD, "depth" : 169 * mm, "offsetDistance" : 25 * mm, "symmetric" : true});
        }
        {
            var Q0;
            Q0=makeQuery(id+"F4.imprint","IMPRINT",FACE,{"disambiguationData":[TD([[makeQuery(id+"F4.imprint","IMPRINT",EDGE,{"derivedFrom":sQuery(id+"F4.wireOp",EDGE,"E180")}),-1.0]])]});
            var Q1;
            Q1=makeQuery(id+"F4.imprint","IMPRINT",FACE,{"disambiguationData":[TD([[makeQuery(id+"F4.imprint","IMPRINT",EDGE,{"derivedFrom":sQuery(id+"F4.wireOp",EDGE,"E184.MirrorCS")}),1.0]])]});
            extrude(context, id + "F12", {"entities" : qUnion([Q0, Q1]), "operationType" : NewBodyOperationType.ADD, "depth" : 295 * mm, "offsetDistance" : 25 * mm, "symmetric" : true});
        }
        {
            var Q0;
            {var subQ0=sQuery(id+"F4.wireOp",EDGE,"E203.MirrorCS");Q0=makeQuery(id+"F4.imprint","IMPRINT",FACE,{"disambiguationData":[TD([[makeQuery(id+"F4.imprint","IMPRINT",EDGE,{"derivedFrom":subQ0}),-1.0]])]});}
            var Q1;
            {var subQ0=sQuery(id+"F4.wireOp",EDGE,"E202");Q1=makeQuery(id+"F4.imprint","IMPRINT",FACE,{"disambiguationData":[TD([[makeQuery(id+"F4.imprint","IMPRINT",EDGE,{"derivedFrom":subQ0}),1.0]])]});}
            extrude(context, id + "F13", {"entities" : qUnion([Q0, Q1]), "operationType" : NewBodyOperationType.ADD, "depth" : 350 * mm, "offsetDistance" : 25 * mm, "symmetric" : true});
        }
        {
            var Q0;
            {var subQ0=sQuery(id+"F2.wireOp",EDGE,"E122.MirrorCS");var subQ1=sQuery(id+"F2.wireOp",EDGE,"E91");Q0=makeQuery(id+"F10.boolean.opBoolean","SPLIT",EDGE,{"disambiguationData":[TD([makeQuery(id+"F9.boolean.opBoolean","COPY",FACE,{"derivedFrom":makeQuery(id+"F9.opExtrude","SWEPT_FACE",FACE,{"disambiguationData":[OSD([sQuery(id+"F3.wireOp",EDGE,"E136")])]})})])],"derivedFrom":makeQuery(id+"F5.opExtrude","CAP_EDGE",EDGE,{"disambiguationData":[OSD([subQ1,subQ0])],"isStart":false})});}
            var Q1;
            {var subQ0=sQuery(id+"F2.wireOp",EDGE,"E122.MirrorCS");var subQ1=sQuery(id+"F2.wireOp",EDGE,"E91");Q1=makeQuery(id+"F10.boolean.opBoolean","SPLIT",EDGE,{"disambiguationData":[TD([makeQuery(id+"F9.boolean.opBoolean","COPY",FACE,{"derivedFrom":makeQuery(id+"F9.opExtrude","SWEPT_FACE",FACE,{"disambiguationData":[OSD([sQuery(id+"F3.wireOp",EDGE,"E147.MirrorCS")])]})})])],"derivedFrom":makeQuery(id+"F5.opExtrude","CAP_EDGE",EDGE,{"disambiguationData":[OSD([subQ1,subQ0])],"isStart":false})});}
            var Q2;
            {var subQ0=sQuery(id+"F2.wireOp",EDGE,"E110.MirrorCS");var subQ1=sQuery(id+"F2.wireOp",EDGE,"E103.MirrorCS");Q2=makeQuery(id+"F10.boolean.opBoolean","SPLIT",EDGE,{"disambiguationData":[TD([makeQuery(id+"F9.boolean.opBoolean","COPY",FACE,{"derivedFrom":makeQuery(id+"F9.opExtrude","SWEPT_FACE",FACE,{"disambiguationData":[OSD([sQuery(id+"F3.wireOp",EDGE,"E147.MirrorCS")])]})})])],"derivedFrom":makeQuery(id+"F5.opExtrude","CAP_EDGE",EDGE,{"disambiguationData":[OSD([subQ1,subQ0])],"isStart":false})});}
            var Q3;
            {var subQ0=sQuery(id+"F2.wireOp",EDGE,"E110.MirrorCS");var subQ1=sQuery(id+"F2.wireOp",EDGE,"E103.MirrorCS");Q3=makeQuery(id+"F10.boolean.opBoolean","SPLIT",EDGE,{"disambiguationData":[TD([makeQuery(id+"F9.boolean.opBoolean","COPY",FACE,{"derivedFrom":makeQuery(id+"F9.opExtrude","SWEPT_FACE",FACE,{"disambiguationData":[OSD([sQuery(id+"F3.wireOp",EDGE,"E136")])]})})])],"derivedFrom":makeQuery(id+"F5.opExtrude","CAP_EDGE",EDGE,{"disambiguationData":[OSD([subQ1,subQ0])],"isStart":false})});}
            fillet(context, id + "F14", {"entities" : qUnion([Q0, Q1, Q2, Q3]), "radius" : 18 * mm, "tangentPropagation" : true, "allowEdgeOverflow" : false});
        }
        {
            var Q0;
            {var subQ0=sQuery(id+"F3.wireOp",EDGE,"E162.MirrorCS");Q0=makeQuery(id+"F3.imprint","IMPRINT",FACE,{"disambiguationData":[TD([[makeQuery(id+"F3.imprint","IMPRINT",EDGE,{"derivedFrom":subQ0}),-1.0]])]});}
            var Q1;
            {var subQ0=sQuery(id+"F3.wireOp",EDGE,"E156");Q1=makeQuery(id+"F3.imprint","IMPRINT",FACE,{"disambiguationData":[TD([[makeQuery(id+"F3.imprint","IMPRINT",EDGE,{"derivedFrom":subQ0}),1.0]])]});}
            extrude(context, id + "F15", {"entities" : qUnion([Q0, Q1]), "operationType" : NewBodyOperationType.ADD, "depth" : 670 * mm, "offsetDistance" : 25 * mm, "symmetric" : true});
        }
        {
            var Q0;
            {var subQ0=sQuery(id+"F3.wireOp",EDGE,"E156");Q0=makeQuery(id+"F3.imprint","IMPRINT",FACE,{"disambiguationData":[TD([[makeQuery(id+"F3.imprint","IMPRINT",EDGE,{"derivedFrom":subQ0}),-1.0]])]});}
            var Q1;
            {var subQ0=sQuery(id+"F3.wireOp",EDGE,"E162.MirrorCS");Q1=makeQuery(id+"F3.imprint","IMPRINT",FACE,{"disambiguationData":[TD([[makeQuery(id+"F3.imprint","IMPRINT",EDGE,{"derivedFrom":subQ0}),1.0]])]});}
            extrude(context, id + "F16", {"entities" : qUnion([Q0, Q1]), "operationType" : NewBodyOperationType.ADD, "depth" : 630 * mm, "offsetDistance" : 25 * mm, "symmetric" : true});
        }
        {
            var Q0;
            {var subQ0=sQuery(id+"F3.wireOp",EDGE,"E166.MirrorCS");Q0=makeQuery(id+"F3.imprint","IMPRINT",FACE,{"disambiguationData":[TD([[makeQuery(id+"F3.imprint","IMPRINT",EDGE,{"derivedFrom":subQ0}),-1.0]])]});}
            var Q1;
            {var subQ0=sQuery(id+"F3.wireOp",EDGE,"E157");Q1=makeQuery(id+"F3.imprint","IMPRINT",FACE,{"disambiguationData":[TD([[makeQuery(id+"F3.imprint","IMPRINT",EDGE,{"derivedFrom":subQ0}),1.0]])]});}
            extrude(context, id + "F17", {"entities" : qUnion([Q0, Q1]), "operationType" : NewBodyOperationType.ADD, "depth" : 550 * mm, "offsetDistance" : 25 * mm, "symmetric" : true});
        }
        {
            var Q0;
            {var subQ0=sQuery(id+"F3.wireOp",EDGE,"E158");Q0=makeQuery(id+"F3.imprint","IMPRINT",FACE,{"disambiguationData":[TD([[makeQuery(id+"F3.imprint","IMPRINT",EDGE,{"derivedFrom":subQ0}),-1.0]])]});}
            var Q1;
            {var subQ0=sQuery(id+"F3.wireOp",EDGE,"E165.MirrorCS");Q1=makeQuery(id+"F3.imprint","IMPRINT",FACE,{"disambiguationData":[TD([[makeQuery(id+"F3.imprint","IMPRINT",EDGE,{"derivedFrom":subQ0}),-1.0]])]});}
            extrude(context, id + "F18", {"entities" : qUnion([Q0, Q1]), "operationType" : NewBodyOperationType.ADD, "depth" : 600 * mm, "offsetDistance" : 25 * mm, "symmetric" : true});
        }
        {
            var Q0;
            {var subQ0=sQuery(id+"F3.wireOp",EDGE,"E159");Q0=makeQuery(id+"F3.imprint","IMPRINT",FACE,{"disambiguationData":[TD([[makeQuery(id+"F3.imprint","IMPRINT",EDGE,{"derivedFrom":subQ0}),-1.0]])]});}
            var Q1;
            {var subQ0=sQuery(id+"F3.wireOp",EDGE,"E164.MirrorCS");Q1=makeQuery(id+"F3.imprint","IMPRINT",FACE,{"disambiguationData":[TD([[makeQuery(id+"F3.imprint","IMPRINT",EDGE,{"derivedFrom":subQ0}),-1.0]])]});}
            extrude(context, id + "F19", {"entities" : qUnion([Q0, Q1]), "operationType" : NewBodyOperationType.ADD, "depth" : 620 * mm, "offsetDistance" : 25 * mm, "symmetric" : true});
        }
        {
            var Q0;
            {var subQ0=sQuery(id+"F3.wireOp",EDGE,"E163.MirrorCS");Q0=makeQuery(id+"F3.imprint","IMPRINT",FACE,{"disambiguationData":[TD([[makeQuery(id+"F3.imprint","IMPRINT",EDGE,{"derivedFrom":subQ0}),-1.0]])]});}
            var Q1;
            {var subQ0=sQuery(id+"F3.wireOp",EDGE,"E160");Q1=makeQuery(id+"F3.imprint","IMPRINT",FACE,{"disambiguationData":[TD([[makeQuery(id+"F3.imprint","IMPRINT",EDGE,{"derivedFrom":subQ0}),-1.0]])]});}
            extrude(context, id + "F20", {"entities" : qUnion([Q0, Q1]), "operationType" : NewBodyOperationType.ADD, "depth" : 620 * mm, "offsetDistance" : 25 * mm, "symmetric" : true});
        }
        {
            var Q0;
            Q0=makeQuery(id+"F5.opExtrude","CAP_EDGE",EDGE,{"disambiguationData":[OSD([sQuery(id+"F2.wireOp",EDGE,"E124.MirrorCS")])],"isStart":false});
            var Q1;
            Q1=makeQuery(id+"F5.opExtrude","CAP_EDGE",EDGE,{"disambiguationData":[OSD([sQuery(id+"F2.wireOp",EDGE,"E123.MirrorCS")])],"isStart":false});
            var Q2;
            Q2=makeQuery(id+"F5.opExtrude","CAP_EDGE",EDGE,{"disambiguationData":[OSD([sQuery(id+"F2.wireOp",EDGE,"E90.trimOffspring")])],"isStart":false});
            var Q3;
            Q3=makeQuery(id+"F5.opExtrude","CAP_EDGE",EDGE,{"disambiguationData":[OSD([sQuery(id+"F2.wireOp",EDGE,"E102.MirrorCS")])],"isStart":false});
            chamfer(context, id + "F21", {"entities" : qUnion([Q0, Q1, Q2, Q3]), "chamferType" : ChamferType.OFFSET_ANGLE, "width" : 15 * mm, "oppositeDirection" : false, "angle" : 35 * degree, "tangentPropagation" : true});
        }
        {
            var Q0;
            {var subQ0=sQuery(id+"F4.wireOp",EDGE,"E198.MirrorCS");var subQ1=sQuery(id+"F4.wireOp",EDGE,"E186.MirrorCS");var subQ2=sQuery(id+"F4.wireOp",EDGE,"E185.MirrorCS");Q0=makeQuery(id+"F11.boolean.opBoolean","MERGE",EDGE,{"derivedFrom":[makeQuery(id+"F8.opExtrude","SWEPT_EDGE",EDGE,{"disambiguationData":[OSD([subQ2,subQ1,subQ0])]}),makeQuery(id+"F11.opExtrude","SWEPT_EDGE",EDGE,{"disambiguationData":[OSD([subQ2,subQ1,subQ0])]})]});}
            chamfer(context, id + "F22", {"entities" : qUnion([Q0]), "chamferType" : ChamferType.OFFSET_ANGLE, "width" : 10 * mm, "oppositeDirection" : false, "angle" : 42 * degree, "tangentPropagation" : true});
        }
        {
            var Q0;
            {var subQ0=sQuery(id+"F4.wireOp",EDGE,"E196");var subQ1=sQuery(id+"F4.wireOp",EDGE,"E179");var subQ2=sQuery(id+"F4.wireOp",EDGE,"E174");Q0=makeQuery(id+"F11.boolean.opBoolean","MERGE",EDGE,{"derivedFrom":[makeQuery(id+"F8.opExtrude","SWEPT_EDGE",EDGE,{"disambiguationData":[OSD([subQ2,subQ1,subQ0])]}),makeQuery(id+"F11.opExtrude","SWEPT_EDGE",EDGE,{"disambiguationData":[OSD([subQ2,subQ1,subQ0])]})]});}
            chamfer(context, id + "F23", {"entities" : qUnion([Q0]), "chamferType" : ChamferType.OFFSET_ANGLE, "width" : 10 * mm, "oppositeDirection" : false, "angle" : 42 * degree, "tangentPropagation" : true});
        }
        {
            var Q0;
            {var subQ0=sQuery(id+"F0.wireOp",EDGE,"E35.top");var subQ1=sQuery(id+"F0.wireOp",EDGE,"E34.MirrorC");var subQ2=makeQuery(id+"F0.imprint","INTERSECT",VERTEX,{"derivedFrom":[subQ1,subQ0]});Q0=makeQuery(id+"F0.imprint","IMPRINT",FACE,{"disambiguationData":[TD([[makeQuery(id+"F0.imprint","IMPRINT",EDGE,{"disambiguationData":[TD([[subQ2,1.0]])],"derivedFrom":subQ1}),1.0]])]});}
            var Q1;
            {var subQ0=sQuery(id+"F0.wireOp",EDGE,"E10");var subQ3=sQuery(id+"F0.wireOp",EDGE,"E1");var subQ5=makeQuery(id+"F0.imprint","INTERSECT",VERTEX,{"disambiguationData":[OD(0.0)],"derivedFrom":[subQ3,subQ0]});Q1=makeQuery(id+"F0.imprint","IMPRINT",FACE,{"disambiguationData":[TD([[makeQuery(id+"F0.imprint","IMPRINT",EDGE,{"disambiguationData":[TD([[subQ5,-1.0]])],"derivedFrom":subQ3}),-1.0]])]});}
            var Q2;
            {var subQ0=sQuery(id+"F0.wireOp",EDGE,"E36");var subQ1=sQuery(id+"F0.wireOp",EDGE,"E0.right");var subQ2=makeQuery(id+"F0.imprint","INTERSECT",VERTEX,{"derivedFrom":[subQ1,subQ0]});Q2=makeQuery(id+"F0.imprint","IMPRINT",FACE,{"disambiguationData":[TD([[makeQuery(id+"F0.imprint","IMPRINT",EDGE,{"disambiguationData":[TD([[subQ2,1.0]])],"derivedFrom":subQ1}),-1.0]])]});}
            var Q3;
            {var subQ1=sQuery(id+"F0.wireOp",EDGE,"E0.left");var subQ3=sQuery(id+"F0.wireOp",EDGE,"E2.MirrorCS");var subQ4=makeQuery(id+"F0.imprint","INTERSECT",VERTEX,{"disambiguationData":[OD(1.0)],"derivedFrom":[subQ1,subQ3]});Q3=makeQuery(id+"F0.imprint","IMPRINT",FACE,{"disambiguationData":[TD([[makeQuery(id+"F0.imprint","IMPRINT",EDGE,{"disambiguationData":[TD([[subQ4,-1.0]])],"derivedFrom":subQ3}),-1.0]])]});}
            var Q4;
            {var subQ1=sQuery(id+"F0.wireOp",EDGE,"E0.left");var subQ3=sQuery(id+"F0.wireOp",EDGE,"E3.MirrorCS");var subQ4=makeQuery(id+"F0.imprint","INTERSECT",VERTEX,{"derivedFrom":[subQ1,subQ3]});Q4=makeQuery(id+"F0.imprint","IMPRINT",FACE,{"disambiguationData":[TD([[makeQuery(id+"F0.imprint","IMPRINT",EDGE,{"disambiguationData":[TD([[subQ4,1.0]])],"derivedFrom":subQ3}),-1.0]])]});}
            var Q5;
            {var subQ0=sQuery(id+"F0.wireOp",EDGE,"E9");var subQ1=sQuery(id+"F0.wireOp",EDGE,"E0.right");var subQ2=makeQuery(id+"F0.imprint","INTERSECT",VERTEX,{"derivedFrom":[subQ1,subQ0]});Q5=makeQuery(id+"F0.imprint","IMPRINT",FACE,{"disambiguationData":[TD([[makeQuery(id+"F0.imprint","IMPRINT",EDGE,{"disambiguationData":[TD([[subQ2,-1.0]])],"derivedFrom":subQ1}),-1.0]])]});}
            var Q6;
            Q6=makeQuery(id+"F0.imprint","IMPRINT",FACE,{"disambiguationData":[TD([[makeQuery(id+"F0.imprint","IMPRINT",EDGE,{"derivedFrom":sQuery(id+"F0.wireOp",EDGE,"E23")}),1.0]])]});
            var Q7;
            Q7=makeQuery(id+"F0.imprint","IMPRINT",FACE,{"disambiguationData":[TD([[makeQuery(id+"F0.imprint","IMPRINT",EDGE,{"derivedFrom":sQuery(id+"F0.wireOp",EDGE,"E21")}),1.0]])]});
            var Q8;
            Q8=makeQuery(id+"F0.imprint","IMPRINT",FACE,{"disambiguationData":[TD([[makeQuery(id+"F0.imprint","IMPRINT",EDGE,{"derivedFrom":sQuery(id+"F0.wireOp",EDGE,"E22")}),1.0]])]});
            var Q9;
            Q9=makeQuery(id+"F0.imprint","IMPRINT",FACE,{"disambiguationData":[TD([[makeQuery(id+"F0.imprint","IMPRINT",EDGE,{"derivedFrom":sQuery(id+"F0.wireOp",EDGE,"E24.MirrorC")}),-1.0]])]});
            var Q10;
            Q10=makeQuery(id+"F0.imprint","IMPRINT",FACE,{"disambiguationData":[TD([[makeQuery(id+"F0.imprint","IMPRINT",EDGE,{"derivedFrom":sQuery(id+"F0.wireOp",EDGE,"E30.MirrorC")}),-1.0]])]});
            var Q11;
            Q11=makeQuery(id+"F0.imprint","IMPRINT",FACE,{"disambiguationData":[TD([[makeQuery(id+"F0.imprint","IMPRINT",EDGE,{"derivedFrom":sQuery(id+"F0.wireOp",EDGE,"E31.MirrorC")}),-1.0]])]});
            var Q12;
            Q12=makeQuery(id+"F0.imprint","IMPRINT",FACE,{"disambiguationData":[TD([[makeQuery(id+"F0.imprint","IMPRINT",EDGE,{"derivedFrom":sQuery(id+"F0.wireOp",EDGE,"E33.MirrorC")}),1.0]])]});
            var Q13;
            Q13=makeQuery(id+"F0.imprint","IMPRINT",FACE,{"disambiguationData":[TD([[makeQuery(id+"F0.imprint","IMPRINT",EDGE,{"derivedFrom":sQuery(id+"F0.wireOp",EDGE,"E32.MirrorC")}),-1.0]])]});
            var Q14;
            Q14=makeQuery(id+"F0.imprint","IMPRINT",FACE,{"disambiguationData":[TD([[makeQuery(id+"F0.imprint","IMPRINT",EDGE,{"derivedFrom":sQuery(id+"F0.wireOp",EDGE,"E19")}),1.0]])]});
            var Q15;
            Q15=makeQuery(id+"F0.imprint","IMPRINT",FACE,{"disambiguationData":[TD([[makeQuery(id+"F0.imprint","IMPRINT",EDGE,{"derivedFrom":sQuery(id+"F0.wireOp",EDGE,"E20")}),1.0]])]});
            var Q16;
            Q16=makeQuery(id+"F0.imprint","IMPRINT",FACE,{"disambiguationData":[TD([[makeQuery(id+"F0.imprint","IMPRINT",EDGE,{"derivedFrom":sQuery(id+"F0.wireOp",EDGE,"E17")}),1.0]])]});
            var Q17;
            Q17=makeQuery(id+"F0.imprint","IMPRINT",FACE,{"disambiguationData":[TD([[makeQuery(id+"F0.imprint","IMPRINT",EDGE,{"derivedFrom":sQuery(id+"F0.wireOp",EDGE,"E18")}),1.0]])]});
            var Q18;
            Q18=makeQuery(id+"F0.imprint","IMPRINT",FACE,{"disambiguationData":[TD([[makeQuery(id+"F0.imprint","IMPRINT",EDGE,{"derivedFrom":sQuery(id+"F0.wireOp",EDGE,"E16")}),1.0]])]});
            var Q19;
            Q19=makeQuery(id+"F0.imprint","IMPRINT",FACE,{"disambiguationData":[TD([[makeQuery(id+"F0.imprint","IMPRINT",EDGE,{"derivedFrom":sQuery(id+"F0.wireOp",EDGE,"E28.MirrorC")}),-1.0]])]});
            var Q20;
            Q20=makeQuery(id+"F0.imprint","IMPRINT",FACE,{"disambiguationData":[TD([[makeQuery(id+"F0.imprint","IMPRINT",EDGE,{"derivedFrom":sQuery(id+"F0.wireOp",EDGE,"E27.MirrorC")}),-1.0]])]});
            var Q21;
            Q21=makeQuery(id+"F0.imprint","IMPRINT",FACE,{"disambiguationData":[TD([[makeQuery(id+"F0.imprint","IMPRINT",EDGE,{"derivedFrom":sQuery(id+"F0.wireOp",EDGE,"E25.MirrorC")}),-1.0]])]});
            var Q22;
            Q22=makeQuery(id+"F0.imprint","IMPRINT",FACE,{"disambiguationData":[TD([[makeQuery(id+"F0.imprint","IMPRINT",EDGE,{"derivedFrom":sQuery(id+"F0.wireOp",EDGE,"E26.MirrorC")}),-1.0]])]});
            var Q23;
            Q23=makeQuery(id+"F0.imprint","IMPRINT",FACE,{"disambiguationData":[TD([[makeQuery(id+"F0.imprint","IMPRINT",EDGE,{"derivedFrom":sQuery(id+"F0.wireOp",EDGE,"E29.MirrorC")}),-1.0]])]});
            var Q24;
            {var subQ5=sQuery(id+"F0.wireOp",EDGE,"E7");Q24=makeQuery(id+"F0.imprint","IMPRINT",FACE,{"disambiguationData":[TD([[makeQuery(id+"F0.imprint","IMPRINT",EDGE,{"derivedFrom":subQ5}),-1.0]])]});}
            var Q25;
            {var subQ0=sQuery(id+"F0.wireOp",EDGE,"E37");var subQ1=sQuery(id+"F0.wireOp",EDGE,"E0.right");var subQ2=makeQuery(id+"F0.imprint","INTERSECT",VERTEX,{"derivedFrom":[subQ1,subQ0]});Q25=makeQuery(id+"F0.imprint","IMPRINT",FACE,{"disambiguationData":[TD([[makeQuery(id+"F0.imprint","IMPRINT",EDGE,{"disambiguationData":[TD([[subQ2,-1.0]])],"derivedFrom":subQ1}),-1.0]])]});}
            var Q26;
            {var subQ5=sQuery(id+"F0.wireOp",EDGE,"E6");Q26=makeQuery(id+"F0.imprint","IMPRINT",FACE,{"disambiguationData":[TD([[makeQuery(id+"F0.imprint","IMPRINT",EDGE,{"derivedFrom":subQ5}),1.0]])]});}
            var Q27;
            Q27=makeQuery(id+"F0.imprint","IMPRINT",FACE,{"disambiguationData":[TD([[makeQuery(id+"F0.imprint","IMPRINT",EDGE,{"derivedFrom":sQuery(id+"F0.wireOp",EDGE,"E46.MirrorC")}),-1.0]])]});
            var Q28;
            Q28=makeQuery(id+"F0.imprint","IMPRINT",FACE,{"disambiguationData":[TD([[makeQuery(id+"F0.imprint","IMPRINT",EDGE,{"derivedFrom":sQuery(id+"F0.wireOp",EDGE,"E45")}),1.0]])]});
            var Q29;
            {var subQ0=sQuery(id+"F0.wireOp",EDGE,"E47.MirrorC");var subQ1=sQuery(id+"F0.wireOp",EDGE,"E35.top");var subQ2=makeQuery(id+"F0.imprint","INTERSECT",VERTEX,{"disambiguationData":[OD(0.0)],"derivedFrom":[subQ1,subQ0]});Q29=makeQuery(id+"F0.imprint","IMPRINT",FACE,{"disambiguationData":[TD([[makeQuery(id+"F0.imprint","IMPRINT",EDGE,{"disambiguationData":[TD([[subQ2,-1.0]])],"derivedFrom":subQ1}),1.0]])]});}
            var Q30;
            {var subQ0=sQuery(id+"F0.wireOp",EDGE,"E48.MirrorC");var subQ1=sQuery(id+"F0.wireOp",EDGE,"E35.bottom");var subQ2=makeQuery(id+"F0.imprint","INTERSECT",VERTEX,{"disambiguationData":[OD(0.0)],"derivedFrom":[subQ1,subQ0]});Q30=makeQuery(id+"F0.imprint","IMPRINT",FACE,{"disambiguationData":[TD([[makeQuery(id+"F0.imprint","IMPRINT",EDGE,{"disambiguationData":[TD([[subQ2,-1.0]])],"derivedFrom":subQ1}),-1.0]])]});}
            var Q31;
            {var subQ0=sQuery(id+"F0.wireOp",EDGE,"E49.MirrorC");var subQ1=sQuery(id+"F0.wireOp",EDGE,"E35.top");var subQ2=makeQuery(id+"F0.imprint","INTERSECT",VERTEX,{"disambiguationData":[OD(0.0)],"derivedFrom":[subQ1,subQ0]});Q31=makeQuery(id+"F0.imprint","IMPRINT",FACE,{"disambiguationData":[TD([[makeQuery(id+"F0.imprint","IMPRINT",EDGE,{"disambiguationData":[TD([[subQ2,-1.0]])],"derivedFrom":subQ1}),1.0]])]});}
            var Q32;
            {var subQ0=sQuery(id+"F0.wireOp",EDGE,"E50.MirrorC");var subQ1=sQuery(id+"F0.wireOp",EDGE,"E35.top");var subQ2=makeQuery(id+"F0.imprint","INTERSECT",VERTEX,{"disambiguationData":[OD(0.0)],"derivedFrom":[subQ1,subQ0]});Q32=makeQuery(id+"F0.imprint","IMPRINT",FACE,{"disambiguationData":[TD([[makeQuery(id+"F0.imprint","IMPRINT",EDGE,{"disambiguationData":[TD([[subQ2,-1.0]])],"derivedFrom":subQ1}),1.0]])]});}
            var Q33;
            {var subQ0=sQuery(id+"F0.wireOp",EDGE,"E52.MirrorC");var subQ1=sQuery(id+"F0.wireOp",EDGE,"E35.bottom");var subQ2=makeQuery(id+"F0.imprint","INTERSECT",VERTEX,{"disambiguationData":[OD(0.0)],"derivedFrom":[subQ1,subQ0]});Q33=makeQuery(id+"F0.imprint","IMPRINT",FACE,{"disambiguationData":[TD([[makeQuery(id+"F0.imprint","IMPRINT",EDGE,{"disambiguationData":[TD([[subQ2,-1.0]])],"derivedFrom":subQ1}),-1.0]])]});}
            var Q34;
            {var subQ0=sQuery(id+"F0.wireOp",EDGE,"E51.MirrorC");var subQ1=sQuery(id+"F0.wireOp",EDGE,"E35.top");var subQ2=makeQuery(id+"F0.imprint","INTERSECT",VERTEX,{"disambiguationData":[OD(0.0)],"derivedFrom":[subQ1,subQ0]});Q34=makeQuery(id+"F0.imprint","IMPRINT",FACE,{"disambiguationData":[TD([[makeQuery(id+"F0.imprint","IMPRINT",EDGE,{"disambiguationData":[TD([[subQ2,-1.0]])],"derivedFrom":subQ1}),1.0]])]});}
            var Q35;
            {var subQ0=sQuery(id+"F0.wireOp",EDGE,"E35.left");var subQ1=sQuery(id+"F0.wireOp",EDGE,"E35.top");var subQ2=makeQuery(id+"F0.imprint","INTERSECT",VERTEX,{"derivedFrom":[subQ1,subQ0]});Q35=makeQuery(id+"F0.imprint","IMPRINT",FACE,{"disambiguationData":[TD([[makeQuery(id+"F0.imprint","IMPRINT",EDGE,{"disambiguationData":[TD([[subQ2,-1.0]])],"derivedFrom":subQ1}),1.0]])]});}
            var Q36;
            Q36=makeQuery(id+"F0.imprint","IMPRINT",FACE,{"disambiguationData":[TD([[makeQuery(id+"F0.imprint","IMPRINT",EDGE,{"derivedFrom":sQuery(id+"F0.wireOp",EDGE,"E54.MirrorC")}),-1.0]])]});
            var Q37;
            Q37=makeQuery(id+"F0.imprint","IMPRINT",FACE,{"disambiguationData":[TD([[makeQuery(id+"F0.imprint","IMPRINT",EDGE,{"derivedFrom":sQuery(id+"F0.wireOp",EDGE,"E55.MirrorC")}),1.0]])]});
            var Q38;
            Q38=makeQuery(id+"F0.imprint","IMPRINT",FACE,{"disambiguationData":[TD([[makeQuery(id+"F0.imprint","IMPRINT",EDGE,{"derivedFrom":sQuery(id+"F0.wireOp",EDGE,"E64.MirrorC")}),-1.0]])]});
            var Q39;
            Q39=makeQuery(id+"F0.imprint","IMPRINT",FACE,{"disambiguationData":[TD([[makeQuery(id+"F0.imprint","IMPRINT",EDGE,{"derivedFrom":sQuery(id+"F0.wireOp",EDGE,"E63.MirrorC")}),1.0]])]});
            var Q40;
            Q40=makeQuery(id+"F0.imprint","IMPRINT",FACE,{"disambiguationData":[TD([[makeQuery(id+"F0.imprint","IMPRINT",EDGE,{"derivedFrom":sQuery(id+"F0.wireOp",EDGE,"E62.MirrorC")}),1.0]])]});
            var Q41;
            Q41=makeQuery(id+"F0.imprint","IMPRINT",FACE,{"disambiguationData":[TD([[makeQuery(id+"F0.imprint","IMPRINT",EDGE,{"derivedFrom":sQuery(id+"F0.wireOp",EDGE,"E61.MirrorC")}),1.0]])]});
            var Q42;
            Q42=makeQuery(id+"F0.imprint","IMPRINT",FACE,{"disambiguationData":[TD([[makeQuery(id+"F0.imprint","IMPRINT",EDGE,{"derivedFrom":sQuery(id+"F0.wireOp",EDGE,"E60.MirrorC")}),1.0]])]});
            var Q43;
            Q43=makeQuery(id+"F0.imprint","IMPRINT",FACE,{"disambiguationData":[TD([[makeQuery(id+"F0.imprint","IMPRINT",EDGE,{"derivedFrom":sQuery(id+"F0.wireOp",EDGE,"E59.MirrorC")}),1.0]])]});
            var Q44;
            Q44=makeQuery(id+"F0.imprint","IMPRINT",FACE,{"disambiguationData":[TD([[makeQuery(id+"F0.imprint","IMPRINT",EDGE,{"derivedFrom":sQuery(id+"F0.wireOp",EDGE,"E57.MirrorC")}),1.0]])]});
            var Q45;
            Q45=makeQuery(id+"F0.imprint","IMPRINT",FACE,{"disambiguationData":[TD([[makeQuery(id+"F0.imprint","IMPRINT",EDGE,{"derivedFrom":sQuery(id+"F0.wireOp",EDGE,"E56.MirrorC")}),1.0]])]});
            var Q46;
            Q46=makeQuery(id+"F0.imprint","IMPRINT",FACE,{"disambiguationData":[TD([[makeQuery(id+"F0.imprint","IMPRINT",EDGE,{"derivedFrom":sQuery(id+"F0.wireOp",EDGE,"E58.MirrorC")}),1.0]])]});
            var Q47;
            Q47=makeQuery(id+"F0.imprint","IMPRINT",FACE,{"disambiguationData":[TD([[makeQuery(id+"F0.imprint","IMPRINT",EDGE,{"derivedFrom":sQuery(id+"F0.wireOp",EDGE,"E69.MirrorC")}),-1.0]])]});
            var Q48;
            Q48=makeQuery(id+"F0.imprint","IMPRINT",FACE,{"disambiguationData":[TD([[makeQuery(id+"F0.imprint","IMPRINT",EDGE,{"derivedFrom":sQuery(id+"F0.wireOp",EDGE,"E68.MirrorC")}),-1.0]])]});
            var Q49;
            Q49=makeQuery(id+"F0.imprint","IMPRINT",FACE,{"disambiguationData":[TD([[makeQuery(id+"F0.imprint","IMPRINT",EDGE,{"derivedFrom":sQuery(id+"F0.wireOp",EDGE,"E70.MirrorC")}),-1.0]])]});
            var Q50;
            Q50=makeQuery(id+"F0.imprint","IMPRINT",FACE,{"disambiguationData":[TD([[makeQuery(id+"F0.imprint","IMPRINT",EDGE,{"derivedFrom":sQuery(id+"F0.wireOp",EDGE,"E67.MirrorC")}),-1.0]])]});
            var Q51;
            Q51=makeQuery(id+"F0.imprint","IMPRINT",FACE,{"disambiguationData":[TD([[makeQuery(id+"F0.imprint","IMPRINT",EDGE,{"derivedFrom":sQuery(id+"F0.wireOp",EDGE,"E71.MirrorC")}),-1.0]])]});
            var Q52;
            Q52=makeQuery(id+"F0.imprint","IMPRINT",FACE,{"disambiguationData":[TD([[makeQuery(id+"F0.imprint","IMPRINT",EDGE,{"derivedFrom":sQuery(id+"F0.wireOp",EDGE,"E72.MirrorC")}),-1.0]])]});
            var Q53;
            Q53=makeQuery(id+"F0.imprint","IMPRINT",FACE,{"disambiguationData":[TD([[makeQuery(id+"F0.imprint","IMPRINT",EDGE,{"derivedFrom":sQuery(id+"F0.wireOp",EDGE,"E66.MirrorC")}),-1.0]])]});
            var Q54;
            Q54=makeQuery(id+"F0.imprint","IMPRINT",FACE,{"disambiguationData":[TD([[makeQuery(id+"F0.imprint","IMPRINT",EDGE,{"derivedFrom":sQuery(id+"F0.wireOp",EDGE,"E65.MirrorC")}),-1.0]])]});
            var Q55;
            Q55=makeQuery(id+"F0.imprint","IMPRINT",FACE,{"disambiguationData":[TD([[makeQuery(id+"F0.imprint","IMPRINT",EDGE,{"derivedFrom":sQuery(id+"F0.wireOp",EDGE,"E73.MirrorC")}),1.0]])]});
            extrude(context, id + "F24", {"entities" : qUnion([Q0, Q1, Q2, Q3, Q4, Q5, Q6, Q7, Q8, Q9, Q10, Q11, Q12, Q13, Q14, Q15, Q16, Q17, Q18, Q19, Q20, Q21, Q22, Q23, Q24, Q25, Q26, Q27, Q28, Q29, Q30, Q31, Q32, Q33, Q34, Q35, Q36, Q37, Q38, Q39, Q40, Q41, Q42, Q43, Q44, Q45, Q46, Q47, Q48, Q49, Q50, Q51, Q52, Q53, Q54, Q55]), "operationType" : NewBodyOperationType.REMOVE, "depth" : 25 * mm, "offsetDistance" : 25 * mm});
        }
        {
            var Q0;
            Q0=qCreatedBy(makeId("Top.planeOp"),FACE);
            var sketch = newSketch(context, id + "F25", { "sketchPlane" : qUnion([Q0])});
            skLineSegment(sketch, "E212.bottom", {"start": v(-365, -200) * mm, "end": v(365, -200) * mm});
            skLineSegment(sketch, "E212.top", {"start": v(-365, 200) * mm, "end": v(365, 200) * mm});
            skLineSegment(sketch, "E212.left", {"start": v(-365, -200) * mm, "end": v(-365, 200) * mm});
            skLineSegment(sketch, "E212.right", {"start": v(365, -200) * mm, "end": v(365, 200) * mm});
            skPoint(sketch, "E213", {"position": v(0, -200) * mm});
            skPoint(sketch, "E214", {"position": v(-182.5, -200) * mm});
            skPoint(sketch, "E215", {"position": v(182.5, -200) * mm});
            skPoint(sketch, "E216", {"position": v(-365, -50) * mm});
            skPoint(sketch, "E217", {"position": v(-365, 50) * mm});
            skPoint(sketch, "E218", {"position": v(-365, 0) * mm});
            skPoint(sketch, "E219", {"position": v(-365, -125) * mm});
            skPoint(sketch, "E220", {"position": v(-365, -162.5) * mm});
            skPoint(sketch, "E221", {"position": v(-365, -87.5) * mm});
            skLineSegment(sketch, "E222.bottom", {"start": v(-193, 0) * mm, "end": v(-172, 0) * mm});
            skLineSegment(sketch, "E222.right", {"start": v(0, 0) * mm, "end": v(0, -0.5) * mm});
            skLineSegment(sketch, "E223.right", {"start": v(0, -20) * mm, "end": v(0, -20.5) * mm});
            skLineSegment(sketch, "E224.right", {"start": v(0, -20) * mm, "end": v(0, -19.5) * mm});
            skPoint(sketch, "E225", {"position": v(-192.5, -200) * mm});
            skPoint(sketch, "E226", {"position": v(-172.5, -200) * mm});
            skPoint(sketch, "E227", {"position": v(-10, -200) * mm});
            skPoint(sketch, "E228", {"position": v(-365, -60) * mm});
            skPoint(sketch, "E229", {"position": v(-365, -40) * mm});
            skPoint(sketch, "E230", {"position": v(-365, 40) * mm});
            skPoint(sketch, "E231", {"position": v(-365, 60) * mm});
            skLineSegment(sketch, "E232.bottom", {"start": v(-365, -40) * mm, "end": v(-274.25, -40) * mm});
            skLineSegment(sketch, "E232.top", {"start": v(-365, -39.5) * mm, "end": v(-318.88, -39.5) * mm});
            skLineSegment(sketch, "E232.left", {"start": v(-365, -40) * mm, "end": v(-365, -39.5) * mm});
            skLineSegment(sketch, "E232.right", {"start": v(0, -40) * mm, "end": v(0, -39.5) * mm});
            skLineSegment(sketch, "E233.bottom", {"start": v(-193, 0) * mm, "end": v(0, 0) * mm});
            skLineSegment(sketch, "E233.right", {"start": v(0, 0) * mm, "end": v(0, 0.5) * mm});
            skLineSegment(sketch, "E234.bottom", {"start": v(-365, -40) * mm, "end": v(-318.88, -40) * mm});
            skLineSegment(sketch, "E234.top", {"start": v(-365, -40.5) * mm, "end": v(-318.88, -40.5) * mm});
            skLineSegment(sketch, "E234.left", {"start": v(-365, -40) * mm, "end": v(-365, -40.5) * mm});
            skLineSegment(sketch, "E234.right", {"start": v(0, -40) * mm, "end": v(0, -40.5) * mm});
            skLineSegment(sketch, "E235.bottom", {"start": v(-319.87, -60) * mm, "end": v(-273.25, -60) * mm});
            skLineSegment(sketch, "E235.top", {"start": v(-319.87, -59.5) * mm, "end": v(-228.62, -59.5) * mm});
            skLineSegment(sketch, "E235.left", {"start": v(-365, -60) * mm, "end": v(-365, -59.5) * mm});
            skLineSegment(sketch, "E235.right", {"start": v(0, -60) * mm, "end": v(0, -59.5) * mm});
            skLineSegment(sketch, "E236.bottom", {"start": v(-319.87, -60) * mm, "end": v(-228.62, -60) * mm});
            skLineSegment(sketch, "E236.top", {"start": v(-319.87, -60.5) * mm, "end": v(-228.62, -60.5) * mm});
            skLineSegment(sketch, "E236.left", {"start": v(-365, -60) * mm, "end": v(-365, -60.5) * mm});
            skLineSegment(sketch, "E236.right", {"start": v(0, -60) * mm, "end": v(0, -60.5) * mm});
            skLineSegment(sketch, "E237.left", {"start": v(-365, -87.5) * mm, "end": v(-365, -87) * mm});
            skLineSegment(sketch, "E237.right", {"start": v(0, -87.5) * mm, "end": v(0, -87) * mm});
            skLineSegment(sketch, "E238.left", {"start": v(-365, -87.5) * mm, "end": v(-365, -88) * mm});
            skLineSegment(sketch, "E238.right", {"start": v(0, -87.5) * mm, "end": v(0, -88) * mm});
            skLineSegment(sketch, "E239.left", {"start": v(-365, -125) * mm, "end": v(-365, -124.5) * mm});
            skLineSegment(sketch, "E239.right", {"start": v(0, -125) * mm, "end": v(0, -124.5) * mm});
            skLineSegment(sketch, "E240.left", {"start": v(-365, -125) * mm, "end": v(-365, -125.5) * mm});
            skLineSegment(sketch, "E240.right", {"start": v(0, -125) * mm, "end": v(0, -125.5) * mm});
            skLineSegment(sketch, "E241.left", {"start": v(-365, -162.5) * mm, "end": v(-365, -162) * mm});
            skLineSegment(sketch, "E241.right", {"start": v(0, -162.5) * mm, "end": v(0, -162) * mm});
            skLineSegment(sketch, "E242.left", {"start": v(-365, -162.5) * mm, "end": v(-365, -163) * mm});
            skLineSegment(sketch, "E242.right", {"start": v(0, -162.5) * mm, "end": v(0, -163) * mm});
            skLineSegment(sketch, "E243.bottom", {"start": v(-192.5, -200) * mm, "end": v(-193, -200) * mm});
            skLineSegment(sketch, "E243.top", {"start": v(-192.5, 0) * mm, "end": v(-193, 0) * mm});
            skLineSegment(sketch, "E243.left", {"start": v(-192.5, -200) * mm, "end": v(-192.5, -87) * mm});
            skLineSegment(sketch, "E243.right", {"start": v(-193, -200) * mm, "end": v(-193, -87) * mm});
            skLineSegment(sketch, "E244.bottom", {"start": v(-192.5, -200) * mm, "end": v(-192, -200) * mm});
            skLineSegment(sketch, "E244.top", {"start": v(-192.5, 0) * mm, "end": v(-192, 0) * mm});
            skLineSegment(sketch, "E244.right", {"start": v(-192, -200) * mm, "end": v(-192, -87) * mm});
            skLineSegment(sketch, "E245.bottom", {"start": v(-182.5, -200) * mm, "end": v(-183, -200) * mm});
            skLineSegment(sketch, "E245.top", {"start": v(-182.5, 0) * mm, "end": v(-183, 0) * mm});
            skLineSegment(sketch, "E245.left", {"start": v(-182.5, -200) * mm, "end": v(-182.5, -87) * mm});
            skLineSegment(sketch, "E245.right", {"start": v(-183, -200) * mm, "end": v(-183, -87.5) * mm});
            skLineSegment(sketch, "E246.bottom", {"start": v(-182.5, -200) * mm, "end": v(-182, -200) * mm});
            skLineSegment(sketch, "E246.top", {"start": v(-182.5, 0) * mm, "end": v(-182, 0) * mm});
            skLineSegment(sketch, "E246.right", {"start": v(-182, -200) * mm, "end": v(-182, -87) * mm});
            skLineSegment(sketch, "E247.bottom", {"start": v(-172.5, -200) * mm, "end": v(-173, -200) * mm});
            skLineSegment(sketch, "E247.top", {"start": v(-172.5, 0) * mm, "end": v(-173, 0) * mm});
            skLineSegment(sketch, "E247.left", {"start": v(-172.5, -200) * mm, "end": v(-172.5, -59.5) * mm});
            skLineSegment(sketch, "E248.bottom", {"start": v(-172.5, -200) * mm, "end": v(-172, -200) * mm});
            skLineSegment(sketch, "E248.top", {"start": v(-172.5, 0) * mm, "end": v(-172, 0) * mm});
            skLineSegment(sketch, "E248.left", {"start": v(-172.5, -163.05) * mm, "end": v(-172.5, -60) * mm});
            skLineSegment(sketch, "E248.right", {"start": v(-172, -200) * mm, "end": v(-172, -59.5) * mm});
            skLineSegment(sketch, "E249.bottom", {"start": v(0, -200) * mm, "end": v(-0.5, -200) * mm});
            skLineSegment(sketch, "E249.top", {"start": v(0, 0) * mm, "end": v(-0.5, 0) * mm});
            skLineSegment(sketch, "E249.left", {"start": v(0, -200) * mm, "end": v(0, 0) * mm});
            skLineSegment(sketch, "E249.right", {"start": v(-0.5, -200) * mm, "end": v(-0.5, 0) * mm});
            skLineSegment(sketch, "E250.bottom", {"start": v(-10, -200) * mm, "end": v(-9.5, -200) * mm});
            skLineSegment(sketch, "E250.top", {"start": v(-10, 0) * mm, "end": v(-9.5, 0) * mm});
            skLineSegment(sketch, "E250.left", {"start": v(-10, -200) * mm, "end": v(-10, 0) * mm});
            skLineSegment(sketch, "E250.right", {"start": v(-9.5, -200) * mm, "end": v(-9.5, 0) * mm});
            skLineSegment(sketch, "E251.bottom", {"start": v(-10, -200) * mm, "end": v(-10.5, -200) * mm});
            skLineSegment(sketch, "E251.top", {"start": v(-10, 0) * mm, "end": v(-10.5, 0) * mm});
            skLineSegment(sketch, "E251.right", {"start": v(-10.5, -200) * mm, "end": v(-10.5, 0) * mm});
            skLineSegment(sketch, "E252.top", {"start": v(-319.87, -50.5) * mm, "end": v(-318.87, -50.5) * mm});
            skLineSegment(sketch, "E252.left", {"start": v(-365, -50) * mm, "end": v(-365, -50.5) * mm});
            skLineSegment(sketch, "E252.right", {"start": v(0, -50) * mm, "end": v(0, -50.5) * mm});
            skLineSegment(sketch, "E253.bottom", {"start": v(-319.87, -50) * mm, "end": v(-318.87, -50) * mm});
            skLineSegment(sketch, "E253.top", {"start": v(-319.87, -49.5) * mm, "end": v(-318.87, -49.5) * mm});
            skLineSegment(sketch, "E253.left", {"start": v(-365, -50) * mm, "end": v(-365, -49.5) * mm});
            skLineSegment(sketch, "E253.right", {"start": v(0, -50) * mm, "end": v(0, -49.5) * mm});
            skLineSegment(sketch, "E254.trimOffspring", {"start": v(-318.87, -60.5) * mm, "end": v(-318.88, -39.5) * mm});
            skLineSegment(sketch, "E255.trimOffspring", {"start": v(-319.87, -60.5) * mm, "end": v(-319.88, -39.5) * mm});
            skLineSegment(sketch, "E256.trimOffspring", {"start": v(-319.37, -60.5) * mm, "end": v(-319.37, -39.5) * mm});
            skLineSegment(sketch, "E257.trimOffspring", {"start": v(-274.25, -60.5) * mm, "end": v(-274.25, -39.5) * mm});
            skLineSegment(sketch, "E258.trimOffspring", {"start": v(-273.25, -60.5) * mm, "end": v(-273.25, -39.5) * mm});
            skLineSegment(sketch, "E259.trimOffspring", {"start": v(-273.75, -60.5) * mm, "end": v(-273.75, -39.5) * mm});
            skLineSegment(sketch, "E260.trimOffspring", {"start": v(-227.62, -60.5) * mm, "end": v(-227.62, -39.5) * mm});
            skLineSegment(sketch, "E261.trimOffspring", {"start": v(-228.12, -60.5) * mm, "end": v(-228.12, -39.5) * mm});
            skLineSegment(sketch, "E262.trimOffspring", {"start": v(-228.62, -60.5) * mm, "end": v(-228.62, -39.5) * mm});
            skLineSegment(sketch, "E263.trimOffspring", {"start": v(-193, -20.5) * mm, "end": v(-172.5, -20.5) * mm});
            skLineSegment(sketch, "E264.trimOffspring", {"start": v(-193, -19.5) * mm, "end": v(-172, -19.5) * mm});
            skLineSegment(sketch, "E265.trimOffspring", {"start": v(-193, -0.5) * mm, "end": v(-172, -0.5) * mm});
            skLineSegment(sketch, "E266.trimOffspring", {"start": v(-193, -20) * mm, "end": v(-172, -20) * mm});
            skLineSegment(sketch, "E267.trimOffspring", {"start": v(-193, -163) * mm, "end": v(-172, -163) * mm});
            skLineSegment(sketch, "E268.trimOffspring", {"start": v(-193, -162.5) * mm, "end": v(-172, -162.5) * mm});
            skLineSegment(sketch, "E269.trimOffspring", {"start": v(-193, -162) * mm, "end": v(-172, -162) * mm});
            skLineSegment(sketch, "E270.trimOffspring", {"start": v(-193, -125) * mm, "end": v(-172, -125) * mm});
            skLineSegment(sketch, "E271.trimOffspring", {"start": v(-193, -124.5) * mm, "end": v(-172, -124.5) * mm});
            skLineSegment(sketch, "E272.trimOffspring", {"start": v(-193, -88) * mm, "end": v(-172, -88) * mm});
            skLineSegment(sketch, "E273.trimOffspring", {"start": v(-193, -87.5) * mm, "end": v(-172, -87.5) * mm});
            skLineSegment(sketch, "E274.trimOffspring", {"start": v(-193, -125.5) * mm, "end": v(-172, -125.5) * mm});
            skLineSegment(sketch, "E275.trimOffspring", {"start": v(-193, -87) * mm, "end": v(-172, -87) * mm});
            skLineSegment(sketch, "E276.trimOffspring", {"start": v(-137.37, -60.5) * mm, "end": v(-137.37, -39.5) * mm});
            skLineSegment(sketch, "E277.trimOffspring", {"start": v(-136.87, -60.5) * mm, "end": v(-136.87, -39.5) * mm});
            skLineSegment(sketch, "E278.trimOffspring", {"start": v(-91.25, -60.5) * mm, "end": v(-91.25, -40) * mm});
            skLineSegment(sketch, "E279.trimOffspring", {"start": v(-90.75, -60.5) * mm, "end": v(-90.75, -39.5) * mm});
            skLineSegment(sketch, "E280.trimOffspring", {"start": v(-91.75, -60.5) * mm, "end": v(-91.75, -39.5) * mm});
            skLineSegment(sketch, "E281.trimOffspring", {"start": v(-136.38, -60.5) * mm, "end": v(-136.38, -39.5) * mm});
            skLineSegment(sketch, "E282.trimOffspring", {"start": v(-91.25, -60.5) * mm, "end": v(-91.25, -39.5) * mm});
            skLineSegment(sketch, "E283.trimOffspring", {"start": v(-10.5, -19.5) * mm, "end": v(0, -19.5) * mm});
            skLineSegment(sketch, "E284.trimOffspring", {"start": v(-10.5, -0.5) * mm, "end": v(0, -0.5) * mm});
            skLineSegment(sketch, "E285.trimOffspring", {"start": v(-10.5, -20.5) * mm, "end": v(0, -20.5) * mm});
            skLineSegment(sketch, "E286.trimOffspring", {"start": v(-10.5, -20) * mm, "end": v(0, -20) * mm});
            skLineSegment(sketch, "E287.trimOffspring", {"start": v(-46.12, -60.5) * mm, "end": v(-46.12, -39.5) * mm});
            skLineSegment(sketch, "E288.trimOffspring", {"start": v(-10.5, -163) * mm, "end": v(0, -163) * mm});
            skLineSegment(sketch, "E289.trimOffspring", {"start": v(-10.5, -162) * mm, "end": v(0, -162) * mm});
            skLineSegment(sketch, "E290.trimOffspring", {"start": v(-45.62, -60.5) * mm, "end": v(-45.62, -39.5) * mm});
            skLineSegment(sketch, "E291.trimOffspring", {"start": v(-45.13, -60.5) * mm, "end": v(-45.13, -39.5) * mm});
            skLineSegment(sketch, "E292.trimOffspring", {"start": v(-10.5, -162.5) * mm, "end": v(0, -162.5) * mm});
            skLineSegment(sketch, "E293.trimOffspring", {"start": v(-10.5, -125.5) * mm, "end": v(0, -125.5) * mm});
            skLineSegment(sketch, "E294.trimOffspring", {"start": v(-10.5, -124.5) * mm, "end": v(0, -124.5) * mm});
            skLineSegment(sketch, "E295.trimOffspring", {"start": v(-10.5, -88) * mm, "end": v(0, -88) * mm});
            skLineSegment(sketch, "E296.trimOffspring", {"start": v(-10.5, -87.5) * mm, "end": v(0, -87.5) * mm});
            skLineSegment(sketch, "E297.trimOffspring", {"start": v(-10.5, -125) * mm, "end": v(0, -125) * mm});
            skLineSegment(sketch, "E298.trimOffspring", {"start": v(-10.5, -87) * mm, "end": v(0, -87) * mm});
            skLineSegment(sketch, "E299.MirrorCS", {"start": v(172.5, -200) * mm, "end": v(173, -200) * mm});
            skLineSegment(sketch, "E300.MirrorCS", {"start": v(182.5, -200) * mm, "end": v(183, -200) * mm});
            skLineSegment(sketch, "E301.MirrorCS", {"start": v(365, -40) * mm, "end": v(365, -39.5) * mm});
            skLineSegment(sketch, "E302.MirrorCS", {"start": v(182.5, -200) * mm, "end": v(182, -200) * mm});
            skLineSegment(sketch, "E303.MirrorCS", {"start": v(192.5, -200) * mm, "end": v(192, -200) * mm});
            skLineSegment(sketch, "E304.MirrorCS", {"start": v(172.5, -200) * mm, "end": v(172, -200) * mm});
            skLineSegment(sketch, "E305.MirrorCS", {"start": v(192.5, -200) * mm, "end": v(193, -200) * mm});
            skLineSegment(sketch, "E306.MirrorCS", {"start": v(365, -40) * mm, "end": v(365, -40.5) * mm});
            skLineSegment(sketch, "E307.MirrorCS", {"start": v(365, -50) * mm, "end": v(365, -49.5) * mm});
            skLineSegment(sketch, "E308.MirrorCS", {"start": v(365, -50) * mm, "end": v(365, -50.5) * mm});
            skLineSegment(sketch, "E309.MirrorCS", {"start": v(10, -200) * mm, "end": v(10.5, -200) * mm});
            skLineSegment(sketch, "E310.MirrorCS", {"start": v(365, -60) * mm, "end": v(365, -60.5) * mm});
            skLineSegment(sketch, "E311.MirrorCS", {"start": v(0, 0) * mm, "end": v(0.5, 0) * mm});
            skLineSegment(sketch, "E312.MirrorCS", {"start": v(10, -200) * mm, "end": v(9.5, -200) * mm});
            skLineSegment(sketch, "E313.MirrorCS", {"start": v(365, -60) * mm, "end": v(365, -59.5) * mm});
            skLineSegment(sketch, "E314.MirrorCS", {"start": v(10.5, -0.5) * mm, "end": v(0, -0.5) * mm});
            skLineSegment(sketch, "E315.MirrorCS", {"start": v(10, 0) * mm, "end": v(9.5, 0) * mm});
            skLineSegment(sketch, "E316.MirrorCS", {"start": v(10, 0) * mm, "end": v(10.5, 0) * mm});
            skLineSegment(sketch, "E317.MirrorCS", {"start": v(365, -125) * mm, "end": v(365, -125.5) * mm});
            skLineSegment(sketch, "E318.MirrorCS", {"start": v(0, -200) * mm, "end": v(0.5, -200) * mm});
            skLineSegment(sketch, "E319.MirrorCS", {"start": v(365, -87.5) * mm, "end": v(365, -87) * mm});
            skLineSegment(sketch, "E320.MirrorCS", {"start": v(365, -162.5) * mm, "end": v(365, -162) * mm});
            skLineSegment(sketch, "E321.MirrorCS", {"start": v(365, -87.5) * mm, "end": v(365, -88) * mm});
            skLineSegment(sketch, "E322.MirrorCS", {"start": v(365, -125) * mm, "end": v(365, -124.5) * mm});
            skLineSegment(sketch, "E323.MirrorCS", {"start": v(365, -162.5) * mm, "end": v(365, -163) * mm});
            skLineSegment(sketch, "E324.MirrorCS", {"start": v(10.5, -19.5) * mm, "end": v(0, -19.5) * mm});
            skLineSegment(sketch, "E325.MirrorCS", {"start": v(365, -40) * mm, "end": v(0, -40) * mm});
            skLineSegment(sketch, "E326.MirrorCS", {"start": v(318.87, -60.5) * mm, "end": v(318.87, -39.5) * mm});
            skLineSegment(sketch, "E327.MirrorCS", {"start": v(172, -200) * mm, "end": v(172, -39.5) * mm});
            skLineSegment(sketch, "E328.MirrorCS", {"start": v(192, -200) * mm, "end": v(192, -39.5) * mm});
            skLineSegment(sketch, "E329.MirrorCS", {"start": v(193, -88) * mm, "end": v(172, -88) * mm});
            skLineSegment(sketch, "E330.MirrorCS", {"start": v(45.62, -60.5) * mm, "end": v(45.62, -39.5) * mm});
            skLineSegment(sketch, "E331.MirrorCS", {"start": v(193, -125) * mm, "end": v(172, -125) * mm});
            skLineSegment(sketch, "E332.MirrorCS", {"start": v(193, -163) * mm, "end": v(172, -163) * mm});
            skLineSegment(sketch, "E333.MirrorCS", {"start": v(182.5, -200) * mm, "end": v(182.5, -40.5) * mm});
            skLineSegment(sketch, "E334.MirrorCS", {"start": v(10, -200) * mm, "end": v(10, 0) * mm});
            skLineSegment(sketch, "E335.MirrorCS", {"start": v(365, -40.5) * mm, "end": v(0, -40.5) * mm});
            skLineSegment(sketch, "E336.MirrorCS", {"start": v(273.25, -60.5) * mm, "end": v(273.25, -39.5) * mm});
            skLineSegment(sketch, "E337.MirrorCS", {"start": v(192.5, -200) * mm, "end": v(192.5, -40) * mm});
            skLineSegment(sketch, "E338.MirrorCS", {"start": v(172.5, -200) * mm, "end": v(172.5, -40.5) * mm});
            skLineSegment(sketch, "E339.MirrorCS", {"start": v(10.5, -125.5) * mm, "end": v(0, -125.5) * mm});
            skLineSegment(sketch, "E340.MirrorCS", {"start": v(193, -162.5) * mm, "end": v(172, -162.5) * mm});
            skLineSegment(sketch, "E341.MirrorCS", {"start": v(10.5, -163) * mm, "end": v(0, -163) * mm});
            skLineSegment(sketch, "E342.MirrorCS", {"start": v(183, -200) * mm, "end": v(183, -39.5) * mm});
            skLineSegment(sketch, "E343.MirrorCS", {"start": v(136.87, -60.5) * mm, "end": v(136.87, -39.5) * mm});
            skLineSegment(sketch, "E344.MirrorCS", {"start": v(365, -60) * mm, "end": v(0, -60) * mm});
            skLineSegment(sketch, "E345.MirrorCS", {"start": v(193, -87.5) * mm, "end": v(172, -87.5) * mm});
            skLineSegment(sketch, "E346.MirrorCS", {"start": v(45.12, -60.5) * mm, "end": v(45.12, -39.5) * mm});
            skLineSegment(sketch, "E347.MirrorCS", {"start": v(10.5, -88) * mm, "end": v(0, -88) * mm});
            skLineSegment(sketch, "E348.MirrorCS", {"start": v(365, -50) * mm, "end": v(0, -50) * mm});
            skLineSegment(sketch, "E349.MirrorCS", {"start": v(10.5, -20.5) * mm, "end": v(0, -20.5) * mm});
            skLineSegment(sketch, "E350.MirrorCS", {"start": v(228.12, -60.5) * mm, "end": v(228.12, -39.5) * mm});
            skLineSegment(sketch, "E351.MirrorCS", {"start": v(319.87, -60.5) * mm, "end": v(319.87, -39.5) * mm});
            skLineSegment(sketch, "E352.MirrorCS", {"start": v(91.25, -60.5) * mm, "end": v(91.25, -40) * mm});
            skLineSegment(sketch, "E353.MirrorCS", {"start": v(91.75, -60.5) * mm, "end": v(91.75, -39.5) * mm});
            skLineSegment(sketch, "E354.MirrorCS", {"start": v(193, -87) * mm, "end": v(172, -87) * mm});
            skLineSegment(sketch, "E355.MirrorCS", {"start": v(193, -124.5) * mm, "end": v(172, -124.5) * mm});
            skLineSegment(sketch, "E356.MirrorCS", {"start": v(10.5, -162.5) * mm, "end": v(0, -162.5) * mm});
            skLineSegment(sketch, "E357.MirrorCS", {"start": v(319.37, -60.5) * mm, "end": v(319.37, -39.5) * mm});
            skLineSegment(sketch, "E358.MirrorCS", {"start": v(193, -200) * mm, "end": v(193, -39.5) * mm});
            skLineSegment(sketch, "E359.MirrorCS", {"start": v(182.5, -200) * mm, "end": v(182.5, -39.5) * mm});
            skLineSegment(sketch, "E360.MirrorCS", {"start": v(273.75, -60.5) * mm, "end": v(273.75, -39.5) * mm});
            skLineSegment(sketch, "E361.MirrorCS", {"start": v(10.5, -125) * mm, "end": v(0, -125) * mm});
            skLineSegment(sketch, "E362.MirrorCS", {"start": v(10.5, -20) * mm, "end": v(0, -20) * mm});
            skLineSegment(sketch, "E363.MirrorCS", {"start": v(193, -125.5) * mm, "end": v(172, -125.5) * mm});
            skLineSegment(sketch, "E364.MirrorCS", {"start": v(173, -200) * mm, "end": v(173, -39.5) * mm});
            skLineSegment(sketch, "E365.MirrorCS", {"start": v(9.5, -200) * mm, "end": v(9.5, 0) * mm});
            skLineSegment(sketch, "E366.MirrorCS", {"start": v(10.5, -87.5) * mm, "end": v(0, -87.5) * mm});
            skLineSegment(sketch, "E367.MirrorCS", {"start": v(193, -162) * mm, "end": v(172, -162) * mm});
            skLineSegment(sketch, "E368.MirrorCS", {"start": v(365, -39.5) * mm, "end": v(0, -39.5) * mm});
            skLineSegment(sketch, "E369.MirrorCS", {"start": v(365, -49.5) * mm, "end": v(0, -49.5) * mm});
            skLineSegment(sketch, "E370.MirrorCS", {"start": v(90.75, -60.5) * mm, "end": v(90.75, -39.5) * mm});
            skPoint(sketch, "E371.MirrorP", {"position": v(365, 0) * mm});
            skLineSegment(sketch, "E372.MirrorCS", {"start": v(10.5, -124.5) * mm, "end": v(0, -124.5) * mm});
            skLineSegment(sketch, "E373.MirrorCS", {"start": v(365, -59.5) * mm, "end": v(0, -59.5) * mm});
            skLineSegment(sketch, "E374.MirrorCS", {"start": v(10.5, -162) * mm, "end": v(0, -162) * mm});
            skPoint(sketch, "E375.MirrorP", {"position": v(365, -60) * mm});
            skPoint(sketch, "E376.MirrorP", {"position": v(172.5, -200) * mm});
            skPoint(sketch, "E377.MirrorP", {"position": v(365, -50) * mm});
            skLineSegment(sketch, "E378.MirrorCS", {"start": v(365, -50.5) * mm, "end": v(0, -50.5) * mm});
            skPoint(sketch, "E379.MirrorP", {"position": v(365, -40) * mm});
            skLineSegment(sketch, "E380.MirrorCS", {"start": v(137.37, -60.5) * mm, "end": v(137.37, -39.5) * mm});
            skPoint(sketch, "E381.MirrorP", {"position": v(192.5, -200) * mm});
            skPoint(sketch, "E382.MirrorP", {"position": v(365, -87.5) * mm});
            skLineSegment(sketch, "E383.MirrorCS", {"start": v(228.62, -60.5) * mm, "end": v(228.62, -39.5) * mm});
            skLineSegment(sketch, "E384.MirrorCS", {"start": v(365, -60.5) * mm, "end": v(0, -60.5) * mm});
            skLineSegment(sketch, "E385.MirrorCS", {"start": v(46.12, -60.5) * mm, "end": v(46.12, -39.5) * mm});
            skLineSegment(sketch, "E386.MirrorCS", {"start": v(10.5, -200) * mm, "end": v(10.5, 0) * mm});
            skLineSegment(sketch, "E387.MirrorCS", {"start": v(0.5, -200) * mm, "end": v(0.5, 0) * mm});
            skLineSegment(sketch, "E388.MirrorCS", {"start": v(182, -200) * mm, "end": v(182, -39.5) * mm});
            skLineSegment(sketch, "E389.MirrorCS", {"start": v(91.25, -60.5) * mm, "end": v(91.25, -39.5) * mm});
            skLineSegment(sketch, "E390.MirrorCS", {"start": v(136.38, -60.5) * mm, "end": v(136.38, -39.5) * mm});
            skLineSegment(sketch, "E391.MirrorCS", {"start": v(192.5, -200) * mm, "end": v(192.5, -39.5) * mm});
            skLineSegment(sketch, "E392.MirrorCS", {"start": v(172.5, -200) * mm, "end": v(172.5, -39.5) * mm});
            skLineSegment(sketch, "E393.MirrorCS", {"start": v(227.62, -60.5) * mm, "end": v(227.62, -39.5) * mm});
            skLineSegment(sketch, "E394.MirrorCS", {"start": v(274.25, -60.5) * mm, "end": v(274.25, -39.5) * mm});
            skPoint(sketch, "E395.MirrorP", {"position": v(365, -162.5) * mm});
            skPoint(sketch, "E396.MirrorP", {"position": v(365, -125) * mm});
            skPoint(sketch, "E397.MirrorP", {"position": v(10, -200) * mm});
            skLineSegment(sketch, "E398.MirrorCS", {"start": v(10.5, -87) * mm, "end": v(0, -87) * mm});
            skLineSegment(sketch, "E399.MirrorCS", {"start": v(0, 50) * mm, "end": v(0, 50.5) * mm});
            skLineSegment(sketch, "E400.MirrorCS", {"start": v(0, 50) * mm, "end": v(0, 49.5) * mm});
            skLineSegment(sketch, "E401.MirrorCS", {"start": v(0, 40) * mm, "end": v(0, 40.5) * mm});
            skLineSegment(sketch, "E402.MirrorCS", {"start": v(0, 60) * mm, "end": v(0, 59.5) * mm});
            skLineSegment(sketch, "E403.MirrorCS", {"start": v(0, 20) * mm, "end": v(0, 20.5) * mm});
            skLineSegment(sketch, "E404.MirrorCS", {"start": v(0, 20) * mm, "end": v(0, 19.5) * mm});
            skLineSegment(sketch, "E405.MirrorCS", {"start": v(0, 40) * mm, "end": v(0, 39.5) * mm});
            skLineSegment(sketch, "E406.MirrorCS", {"start": v(0, 60) * mm, "end": v(0, 60.5) * mm});
            skLineSegment(sketch, "E407.MirrorCS", {"start": v(-365, 40) * mm, "end": v(-365, 40.5) * mm});
            skLineSegment(sketch, "E408.MirrorCS", {"start": v(-365, 50) * mm, "end": v(-365, 49.5) * mm});
            skLineSegment(sketch, "E409.MirrorCS", {"start": v(10.5, 0.5) * mm, "end": v(0, 0.5) * mm});
            skLineSegment(sketch, "E410.MirrorCS", {"start": v(-365, 60) * mm, "end": v(-365, 59.5) * mm});
            skLineSegment(sketch, "E411.MirrorCS", {"start": v(-365, 50) * mm, "end": v(-365, 50.5) * mm});
            skLineSegment(sketch, "E412.MirrorCS", {"start": v(-365, 60) * mm, "end": v(-365, 60.5) * mm});
            skLineSegment(sketch, "E413.MirrorCS", {"start": v(-365, 40) * mm, "end": v(-365, 39.5) * mm});
            skLineSegment(sketch, "E414.MirrorCS", {"start": v(-193, 0.5) * mm, "end": v(-172, 0.5) * mm});
            skLineSegment(sketch, "E415.MirrorCS", {"start": v(-10.5, 0.5) * mm, "end": v(0, 0.5) * mm});
            skLineSegment(sketch, "E416.MirrorCS", {"start": v(-10.5, 20.5) * mm, "end": v(0, 20.5) * mm});
            skLineSegment(sketch, "E417.MirrorCS", {"start": v(10.5, 20) * mm, "end": v(0, 20) * mm});
            skLineSegment(sketch, "E418.MirrorCS", {"start": v(-10.5, 20) * mm, "end": v(0, 20) * mm});
            skLineSegment(sketch, "E419.MirrorCS", {"start": v(10.5, 20.5) * mm, "end": v(0, 20.5) * mm});
            skLineSegment(sketch, "E420.MirrorCS", {"start": v(10.5, 19.5) * mm, "end": v(0, 19.5) * mm});
            skLineSegment(sketch, "E421.MirrorCS", {"start": v(-10.5, 19.5) * mm, "end": v(0, 19.5) * mm});
            skLineSegment(sketch, "E422.MirrorCS", {"start": v(-91.25, 60.5) * mm, "end": v(-91.25, 40) * mm});
            skLineSegment(sketch, "E423.MirrorCS", {"start": v(-137.37, 60.5) * mm, "end": v(-137.37, 39.5) * mm});
            skLineSegment(sketch, "E424.MirrorCS", {"start": v(-274.25, 60.5) * mm, "end": v(-274.25, 39.5) * mm});
            skLineSegment(sketch, "E425.MirrorCS", {"start": v(-318.87, 60.5) * mm, "end": v(-318.88, 39.5) * mm});
            skLineSegment(sketch, "E426.MirrorCS", {"start": v(-319.88, 40) * mm, "end": v(-228.62, 40) * mm});
            skLineSegment(sketch, "E427.MirrorCS", {"start": v(-136.87, 60.5) * mm, "end": v(-136.87, 39.5) * mm});
            skLineSegment(sketch, "E428.MirrorCS", {"start": v(-319.87, 60.5) * mm, "end": v(-319.88, 39.5) * mm});
            skLineSegment(sketch, "E429.MirrorCS", {"start": v(-273.25, 60.5) * mm, "end": v(-273.25, 39.5) * mm});
            skLineSegment(sketch, "E430.MirrorCS", {"start": v(-319.87, 50) * mm, "end": v(-318.87, 50) * mm});
            skLineSegment(sketch, "E431.MirrorCS", {"start": v(-90.75, 60.5) * mm, "end": v(-90.75, 39.5) * mm});
            skLineSegment(sketch, "E432.MirrorCS", {"start": v(-365, 60) * mm, "end": v(-318.87, 60) * mm});
            skLineSegment(sketch, "E433.MirrorCS", {"start": v(-193, 20.5) * mm, "end": v(-172, 20.5) * mm});
            skLineSegment(sketch, "E434.MirrorCS", {"start": v(-228.12, 60.5) * mm, "end": v(-228.12, 39.5) * mm});
            skLineSegment(sketch, "E435.MirrorCS", {"start": v(-45.62, 60.5) * mm, "end": v(-45.62, 39.5) * mm});
            skLineSegment(sketch, "E436.MirrorCS", {"start": v(-319.37, 40.5) * mm, "end": v(-228.62, 40.5) * mm});
            skLineSegment(sketch, "E437.MirrorCS", {"start": v(-319.37, 60.5) * mm, "end": v(-319.37, 39.5) * mm});
            skLineSegment(sketch, "E438.MirrorCS", {"start": v(-365, 59.5) * mm, "end": v(-318.87, 59.5) * mm});
            skLineSegment(sketch, "E439.MirrorCS", {"start": v(-273.75, 60.5) * mm, "end": v(-273.75, 39.5) * mm});
            skLineSegment(sketch, "E440.MirrorCS", {"start": v(-91.75, 60.5) * mm, "end": v(-91.75, 39.5) * mm});
            skLineSegment(sketch, "E441.MirrorCS", {"start": v(-193, 20) * mm, "end": v(-172, 20) * mm});
            skLineSegment(sketch, "E442.MirrorCS", {"start": v(-319.87, 49.5) * mm, "end": v(-318.87, 49.5) * mm});
            skLineSegment(sketch, "E443.MirrorCS", {"start": v(-227.62, 60.5) * mm, "end": v(-227.62, 39.5) * mm});
            skLineSegment(sketch, "E444.MirrorCS", {"start": v(-45.13, 60.5) * mm, "end": v(-45.13, 39.5) * mm});
            skLineSegment(sketch, "E445.MirrorCS", {"start": v(-228.62, 60.5) * mm, "end": v(-228.62, 39.5) * mm});
            skLineSegment(sketch, "E446.MirrorCS", {"start": v(-46.12, 60.5) * mm, "end": v(-46.12, 39.5) * mm});
            skLineSegment(sketch, "E447.MirrorCS", {"start": v(-365, 60.5) * mm, "end": v(-318.87, 60.5) * mm});
            skLineSegment(sketch, "E448.MirrorCS", {"start": v(-91.25, 60.5) * mm, "end": v(-91.25, 39.5) * mm});
            skLineSegment(sketch, "E449.MirrorCS", {"start": v(-319.88, 39.5) * mm, "end": v(-273.25, 39.5) * mm});
            skLineSegment(sketch, "E450.MirrorCS", {"start": v(-319.37, 40) * mm, "end": v(-273.25, 40) * mm});
            skLineSegment(sketch, "E451.MirrorCS", {"start": v(-136.38, 60.5) * mm, "end": v(-136.38, 39.5) * mm});
            skLineSegment(sketch, "E452.MirrorCS", {"start": v(-319.87, 50.5) * mm, "end": v(-318.87, 50.5) * mm});
            skLineSegment(sketch, "E453.MirrorCS", {"start": v(-365, 60) * mm, "end": v(-274.25, 60) * mm});
            skLineSegment(sketch, "E454.MirrorCS", {"start": v(-193, 19.5) * mm, "end": v(-172, 19.5) * mm});
            skLineSegment(sketch, "E455.MirrorCS", {"start": v(0, 60.5) * mm, "end": v(0, 0) * mm});
            skLineSegment(sketch, "E456.MirrorCS", {"start": v(-193, 20.5) * mm, "end": v(-172.5, 20.5) * mm});
            skLineSegment(sketch, "E457.MirrorCS", {"start": v(-319.88, 40) * mm, "end": v(-273.25, 40) * mm});
            skLineSegment(sketch, "E458.MirrorCS", {"start": v(10.5, 40) * mm, "end": v(0, 40) * mm});
            skLineSegment(sketch, "E459.MirrorCS", {"start": v(10.5, 60) * mm, "end": v(0, 60) * mm});
            skLineSegment(sketch, "E460.MirrorCS", {"start": v(-319.88, 40.5) * mm, "end": v(-273.25, 40.5) * mm});
            skLineSegment(sketch, "E461.MirrorCS", {"start": v(10.5, 50) * mm, "end": v(0, 50) * mm});
            skLineSegment(sketch, "E462.MirrorCS", {"start": v(-365, 59.5) * mm, "end": v(-274.25, 59.5) * mm});
            skLineSegment(sketch, "E463.MirrorCS", {"start": v(-365, 60.5) * mm, "end": v(-274.25, 60.5) * mm});
            skLineSegment(sketch, "E464.MirrorCS", {"start": v(-319.88, 39.5) * mm, "end": v(-228.62, 39.5) * mm});
            skLineSegment(sketch, "E465.MirrorCS", {"start": v(10.5, 49.5) * mm, "end": v(0, 49.5) * mm});
            skLineSegment(sketch, "E466.MirrorCS", {"start": v(10.5, 50.5) * mm, "end": v(0, 50.5) * mm});
            skLineSegment(sketch, "E467.MirrorCS", {"start": v(10.5, 59.5) * mm, "end": v(0, 59.5) * mm});
            skLineSegment(sketch, "E468.MirrorCS", {"start": v(10.5, 39.5) * mm, "end": v(0, 39.5) * mm});
            skLineSegment(sketch, "E469.MirrorCS", {"start": v(10.5, 60.5) * mm, "end": v(0, 60.5) * mm});
            skLineSegment(sketch, "E470.MirrorCS", {"start": v(-365, 60) * mm, "end": v(-319.37, 60) * mm});
            skLineSegment(sketch, "E471.MirrorCS", {"start": v(-319.87, 50) * mm, "end": v(-319.37, 50) * mm});
            skLineSegment(sketch, "E472.MirrorCS", {"start": v(10.5, 40.5) * mm, "end": v(0, 40.5) * mm});
            skLineSegment(sketch, "E473.trimOffspring", {"start": v(-10.5, 60.5) * mm, "end": v(-10.5, 0) * mm});
            skLineSegment(sketch, "E474.trimOffspring", {"start": v(-10, 60.5) * mm, "end": v(-10, 0) * mm});
            skLineSegment(sketch, "E475.trimOffspring", {"start": v(-0.5, 60.5) * mm, "end": v(-0.5, 0) * mm});
            skLineSegment(sketch, "E476.trimOffspring", {"start": v(-9.5, 60.5) * mm, "end": v(-9.5, 0) * mm});
            skLineSegment(sketch, "E477.trimOffspring", {"start": v(0.5, 60.5) * mm, "end": v(0.5, 0) * mm});
            skLineSegment(sketch, "E478.trimOffspring", {"start": v(10.5, 60.5) * mm, "end": v(10.5, 49.5) * mm});
            skLineSegment(sketch, "E479.trimOffspring", {"start": v(10, 60.5) * mm, "end": v(10, 49.5) * mm});
            skLineSegment(sketch, "E480.trimOffspring", {"start": v(9.5, 60.5) * mm, "end": v(9.5, 49.5) * mm});
            skLineSegment(sketch, "E481.trimOffspring", {"start": v(-173, 60.5) * mm, "end": v(-173, 49.5) * mm});
            skLineSegment(sketch, "E482.trimOffspring", {"start": v(-172.5, 60.5) * mm, "end": v(-172.5, 50) * mm});
            skLineSegment(sketch, "E483.trimOffspring", {"start": v(-172, 60.5) * mm, "end": v(-172, 49.5) * mm});
            skLineSegment(sketch, "E484.trimOffspring", {"start": v(-172.5, 60.5) * mm, "end": v(-172.5, 49.5) * mm});
            skPoint(sketch, "E485.orphan", {"position": v(365, 60.5) * mm});
            skPoint(sketch, "E486.orphan", {"position": v(365, 59.5) * mm});
            skPoint(sketch, "E487.orphan", {"position": v(365, 60) * mm});
            skPoint(sketch, "E488.orphan", {"position": v(365, 40) * mm});
            skPoint(sketch, "E489.orphan", {"position": v(365, 39.5) * mm});
            skPoint(sketch, "E490.orphan", {"position": v(365, 49.5) * mm});
            skPoint(sketch, "E491.orphan", {"position": v(365, 50) * mm});
            skPoint(sketch, "E492.orphan", {"position": v(365, 50.5) * mm});
            skPoint(sketch, "E493.orphan", {"position": v(365, 40.5) * mm});
            skPoint(sketch, "E494.orphan", {"position": v(0, 200) * mm});
            skLineSegment(sketch, "E495.trimOffspring", {"start": v(-10.5, 0) * mm, "end": v(0, 0) * mm});
            skLineSegment(sketch, "E496.trimOffspring", {"start": v(-318.88, -39.5) * mm, "end": v(-227.62, -39.5) * mm});
            skLineSegment(sketch, "E497.trimOffspring", {"start": v(-318.88, -40.5) * mm, "end": v(-227.62, -40.5) * mm});
            skLineSegment(sketch, "E498.trimOffspring", {"start": v(-274.25, -40) * mm, "end": v(-227.62, -40) * mm});
            skLineSegment(sketch, "E499.trimOffspring", {"start": v(-274.25, -49.5) * mm, "end": v(-273.25, -49.5) * mm});
            skLineSegment(sketch, "E500.trimOffspring", {"start": v(-274.25, -50) * mm, "end": v(-273.25, -50) * mm});
            skLineSegment(sketch, "E501.trimOffspring", {"start": v(-228.62, -60.5) * mm, "end": v(-192, -60.5) * mm});
            skLineSegment(sketch, "E502.trimOffspring", {"start": v(-228.62, -60) * mm, "end": v(-192, -60) * mm});
            skLineSegment(sketch, "E503.trimOffspring", {"start": v(-228.62, -59.5) * mm, "end": v(-192, -59.5) * mm});
            skLineSegment(sketch, "E504.trimOffspring", {"start": v(-228.62, -60) * mm, "end": v(-192.5, -60) * mm});
            skLineSegment(sketch, "E505.trimOffspring", {"start": v(-228.62, -50.5) * mm, "end": v(-227.62, -50.5) * mm});
            skLineSegment(sketch, "E506.trimOffspring", {"start": v(-228.62, -50) * mm, "end": v(-227.62, -50) * mm});
            skLineSegment(sketch, "E507.trimOffspring", {"start": v(-193, -50.5) * mm, "end": v(0, -50.5) * mm});
            skLineSegment(sketch, "E508.trimOffspring", {"start": v(-193, -39.5) * mm, "end": v(-182, -39.5) * mm});
            skLineSegment(sketch, "E509.trimOffspring", {"start": v(-193, -40) * mm, "end": v(-182, -40) * mm});
            skLineSegment(sketch, "E510.trimOffspring", {"start": v(-193, -49.5) * mm, "end": v(0, -49.5) * mm});
            skLineSegment(sketch, "E511.trimOffspring", {"start": v(-228.62, -49.5) * mm, "end": v(-227.62, -49.5) * mm});
            skLineSegment(sketch, "E512.trimOffspring", {"start": v(-193, -50) * mm, "end": v(0, -50) * mm});
            skLineSegment(sketch, "E513.trimOffspring", {"start": v(-193, -40.5) * mm, "end": v(-182, -40.5) * mm});
            skLineSegment(sketch, "E514.trimOffspring", {"start": v(-193, -40.5) * mm, "end": v(-193, 0) * mm});
            skLineSegment(sketch, "E515.trimOffspring", {"start": v(-192.5, -40.5) * mm, "end": v(-192.5, 0) * mm});
            skLineSegment(sketch, "E516.trimOffspring", {"start": v(-192, -40.5) * mm, "end": v(-192, 0) * mm});
            skLineSegment(sketch, "E517.trimOffspring", {"start": v(-183, -60.5) * mm, "end": v(0, -60.5) * mm});
            skLineSegment(sketch, "E518.trimOffspring", {"start": v(-183, -59.5) * mm, "end": v(0, -59.5) * mm});
            skLineSegment(sketch, "E519.trimOffspring", {"start": v(-183, -60) * mm, "end": v(0, -60) * mm});
            skLineSegment(sketch, "E520.trimOffspring", {"start": v(-172.5, -50.5) * mm, "end": v(-172.5, -39.5) * mm});
            skLineSegment(sketch, "E521.trimOffspring", {"start": v(-172.5, -40) * mm, "end": v(0, -40) * mm});
            skLineSegment(sketch, "E522.trimOffspring", {"start": v(-173, -40.5) * mm, "end": v(0, -40.5) * mm});
            skLineSegment(sketch, "E523.trimOffspring", {"start": v(-172, -50.5) * mm, "end": v(-172, -39.5) * mm});
            skLineSegment(sketch, "E524.trimOffspring", {"start": v(-173, -40) * mm, "end": v(0, -40) * mm});
            skLineSegment(sketch, "E525.trimOffspring", {"start": v(-172.5, -39.5) * mm, "end": v(0, -39.5) * mm});
            skLineSegment(sketch, "E526.trimOffspring", {"start": v(-192.5, -60.5) * mm, "end": v(-192.5, -50) * mm});
            skLineSegment(sketch, "E527.trimOffspring", {"start": v(-182.5, -60.5) * mm, "end": v(-182.5, 0) * mm});
            skLineSegment(sketch, "E528.trimOffspring", {"start": v(-172.5, -20.5) * mm, "end": v(-172.5, 0) * mm});
            skLineSegment(sketch, "E529.trimOffspring", {"start": v(-193, -60.5) * mm, "end": v(-193, -49.5) * mm});
            skLineSegment(sketch, "E530.trimOffspring", {"start": v(-192.5, -60.5) * mm, "end": v(-192.5, -49.5) * mm});
            skLineSegment(sketch, "E531.trimOffspring", {"start": v(-192, -60.5) * mm, "end": v(-192, -49.5) * mm});
            skLineSegment(sketch, "E532.trimOffspring", {"start": v(-183, -60.5) * mm, "end": v(-183, 0) * mm});
            skLineSegment(sketch, "E533.trimOffspring", {"start": v(-182, -60.5) * mm, "end": v(-182, 0) * mm});
            skLineSegment(sketch, "E534.MirrorCS", {"start": v(-173, -200) * mm, "end": v(-173, -59.5) * mm});
            skLineSegment(sketch, "E535.trimOffspring", {"start": v(-173, -50.5) * mm, "end": v(-173, -39.5) * mm});
            skLineSegment(sketch, "E536.trimOffspring", {"start": v(-172, -20) * mm, "end": v(-172, 0) * mm});
            skLineSegment(sketch, "E537.MirrorCS", {"start": v(-172, -39.5) * mm, "end": v(-173, -39.5) * mm});
            skLineSegment(sketch, "E538.trimOffspring", {"start": v(-173, -20.5) * mm, "end": v(-173, 0) * mm});
            skLineSegment(sketch, "E539.MirrorCS", {"start": v(-172, -40.5) * mm, "end": v(-172, -39.5) * mm});
            skLineSegment(sketch, "E540.MirrorCS", {"start": v(-172, -20.5) * mm, "end": v(-192.5, -20.5) * mm});
            skLineSegment(sketch, "E541.trimOffspring", {"start": v(-182, -39.5) * mm, "end": v(-183, -39.5) * mm});
            skLineSegment(sketch, "E542.trimOffspring", {"start": v(-172, -20.5) * mm, "end": v(-172, 0) * mm});
            skPoint(sketch, "E543.orphan", {"position": v(-365, 39.5) * mm});
            skLineSegment(sketch, "E544.trimOffspring", {"start": v(-274.25, 60) * mm, "end": v(-228.12, 60) * mm});
            skLineSegment(sketch, "E545.trimOffspring", {"start": v(-274.25, 50) * mm, "end": v(-273.25, 50) * mm});
            skPoint(sketch, "E546.orphan", {"position": v(-365, 40.5) * mm});
            skLineSegment(sketch, "E547.trimOffspring", {"start": v(-228.62, 50) * mm, "end": v(-227.62, 50) * mm});
            skLineSegment(sketch, "E548.trimOffspring", {"start": v(-228.62, 40) * mm, "end": v(-193, 40) * mm});
            skLineSegment(sketch, "E549.trimOffspring", {"start": v(-228.62, 50) * mm, "end": v(-228.12, 50) * mm});
            skPoint(sketch, "E550.orphan", {"position": v(-365, 49.5) * mm});
            skPoint(sketch, "E551.orphan", {"position": v(-365, 50.5) * mm});
            skLineSegment(sketch, "E552.trimOffspring", {"start": v(-274.25, 59.5) * mm, "end": v(-227.62, 59.5) * mm});
            skLineSegment(sketch, "E553.trimOffspring", {"start": v(-274.25, 49.5) * mm, "end": v(-273.25, 49.5) * mm});
            skLineSegment(sketch, "E554.trimOffspring", {"start": v(-274.25, 50.5) * mm, "end": v(-273.25, 50.5) * mm});
            skLineSegment(sketch, "E555.trimOffspring", {"start": v(-274.25, 60) * mm, "end": v(-227.62, 60) * mm});
            skLineSegment(sketch, "E556.trimOffspring", {"start": v(-274.25, 60.5) * mm, "end": v(-228.12, 60.5) * mm});
            skLineSegment(sketch, "E557.trimOffspring", {"start": v(-228.62, 49.5) * mm, "end": v(-227.62, 49.5) * mm});
            skLineSegment(sketch, "E558.trimOffspring", {"start": v(-228.62, 40) * mm, "end": v(-192, 40) * mm});
            skLineSegment(sketch, "E559.trimOffspring", {"start": v(-228.62, 39.5) * mm, "end": v(-192, 39.5) * mm});
            skLineSegment(sketch, "E560.trimOffspring", {"start": v(-228.62, 40.5) * mm, "end": v(-192, 40.5) * mm});
            skLineSegment(sketch, "E561.trimOffspring", {"start": v(-228.62, 50.5) * mm, "end": v(-228.12, 50.5) * mm});
            skLineSegment(sketch, "E562.trimOffspring", {"start": v(-274.25, 60.5) * mm, "end": v(-227.62, 60.5) * mm});
            skLineSegment(sketch, "E563.trimOffspring", {"start": v(-228.62, 49.5) * mm, "end": v(-228.12, 49.5) * mm});
            skLineSegment(sketch, "E564.trimOffspring", {"start": v(-228.62, 50.5) * mm, "end": v(-227.62, 50.5) * mm});
            skLineSegment(sketch, "E565.trimOffspring", {"start": v(-193, 49.5) * mm, "end": v(0, 49.5) * mm});
            skLineSegment(sketch, "E566.trimOffspring", {"start": v(-193, 50.5) * mm, "end": v(0, 50.5) * mm});
            skLineSegment(sketch, "E567.trimOffspring", {"start": v(-193, 50) * mm, "end": v(0, 50) * mm});
            skLineSegment(sketch, "E568.trimOffspring", {"start": v(-193, 49.5) * mm, "end": v(-173, 49.5) * mm});
            skLineSegment(sketch, "E569.trimOffspring", {"start": v(-193, 50) * mm, "end": v(-172, 50) * mm});
            skLineSegment(sketch, "E570.trimOffspring", {"start": v(-193, 50.5) * mm, "end": v(-172, 50.5) * mm});
            skLineSegment(sketch, "E571.trimOffspring", {"start": v(-193, 50.5) * mm, "end": v(-193, 39.5) * mm});
            skLineSegment(sketch, "E572.trimOffspring", {"start": v(-192.5, 50.5) * mm, "end": v(-192.5, 39.5) * mm});
            skLineSegment(sketch, "E573.trimOffspring", {"start": v(-183, 39.5) * mm, "end": v(-172.5, 39.5) * mm});
            skLineSegment(sketch, "E574.trimOffspring", {"start": v(-192, 20.5) * mm, "end": v(-192, 0) * mm});
            skLineSegment(sketch, "E575.trimOffspring", {"start": v(-183, 40) * mm, "end": v(-172, 40) * mm});
            skLineSegment(sketch, "E576.trimOffspring", {"start": v(-183, 39.5) * mm, "end": v(-172, 39.5) * mm});
            skLineSegment(sketch, "E577.trimOffspring", {"start": v(-193, 20.5) * mm, "end": v(-193, 0) * mm});
            skLineSegment(sketch, "E578.trimOffspring", {"start": v(-192.5, 20.5) * mm, "end": v(-192.5, 0) * mm});
            skLineSegment(sketch, "E579.trimOffspring", {"start": v(-182.5, 20.5) * mm, "end": v(-182.5, 0) * mm});
            skLineSegment(sketch, "E580.trimOffspring", {"start": v(-183, 20.5) * mm, "end": v(-183, 0) * mm});
            skLineSegment(sketch, "E581.trimOffspring", {"start": v(-182, 20.5) * mm, "end": v(-182, 0) * mm});
            skLineSegment(sketch, "E582.trimOffspring", {"start": v(-183, 40.5) * mm, "end": v(-172, 40.5) * mm});
            skLineSegment(sketch, "E583.trimOffspring", {"start": v(-192, 50.5) * mm, "end": v(-192, 39.5) * mm});
            skLineSegment(sketch, "E584.trimOffspring", {"start": v(-173, 59.5) * mm, "end": v(-9.5, 59.5) * mm});
            skLineSegment(sketch, "E585.trimOffspring", {"start": v(-173, 40.5) * mm, "end": v(-173, 0) * mm});
            skLineSegment(sketch, "E586.trimOffspring", {"start": v(-172.5, 40.5) * mm, "end": v(-172.5, 0) * mm});
            skLineSegment(sketch, "E587.trimOffspring", {"start": v(-173, 60) * mm, "end": v(-10, 60) * mm});
            skLineSegment(sketch, "E588.trimOffspring", {"start": v(-183, 40) * mm, "end": v(0, 40) * mm});
            skLineSegment(sketch, "E589.trimOffspring", {"start": v(-172, 40.5) * mm, "end": v(-172, 0.5) * mm});
            skLineSegment(sketch, "E590.trimOffspring", {"start": v(-137.37, 49.5) * mm, "end": v(0, 49.5) * mm});
            skLineSegment(sketch, "E591.trimOffspring", {"start": v(-137.37, 39.5) * mm, "end": v(0, 39.5) * mm});
            skLineSegment(sketch, "E592.trimOffspring", {"start": v(-183, 40) * mm, "end": v(-172.5, 40) * mm});
            skLineSegment(sketch, "E593.trimOffspring", {"start": v(-137.37, 40.5) * mm, "end": v(0, 40.5) * mm});
            skLineSegment(sketch, "E594.trimOffspring", {"start": v(-137.37, 50.5) * mm, "end": v(-136.38, 50.5) * mm});
            skLineSegment(sketch, "E595.trimOffspring", {"start": v(-137.37, 40) * mm, "end": v(0, 40) * mm});
            skLineSegment(sketch, "E596.trimOffspring", {"start": v(-183, 50.5) * mm, "end": v(-183, 39.5) * mm});
            skLineSegment(sketch, "E597.trimOffspring", {"start": v(-182, 50.5) * mm, "end": v(-182, 39.5) * mm});
            skLineSegment(sketch, "E598.trimOffspring", {"start": v(-182.5, 50.5) * mm, "end": v(-182.5, 39.5) * mm});
            skLineSegment(sketch, "E599.trimOffspring", {"start": v(-173, 59.5) * mm, "end": v(-136.38, 59.5) * mm});
            skLineSegment(sketch, "E600.trimOffspring", {"start": v(-173, 60.5) * mm, "end": v(-9.5, 60.5) * mm});
            skLineSegment(sketch, "E601.trimOffspring", {"start": v(-91.75, 50) * mm, "end": v(0, 50) * mm});
            skLineSegment(sketch, "E602.trimOffspring", {"start": v(-91.75, 50.5) * mm, "end": v(0, 50.5) * mm});
            skLineSegment(sketch, "E603.trimOffspring", {"start": v(-91.75, 59.5) * mm, "end": v(-9.5, 59.5) * mm});
            skLineSegment(sketch, "E604.trimOffspring", {"start": v(-91.75, 60) * mm, "end": v(-9.5, 60) * mm});
            skLineSegment(sketch, "E605.trimOffspring", {"start": v(-91.75, 60.5) * mm, "end": v(-9.5, 60.5) * mm});
            skLineSegment(sketch, "E606.trimOffspring", {"start": v(-173, 60) * mm, "end": v(-136.38, 60) * mm});
            skLineSegment(sketch, "E607.trimOffspring", {"start": v(-173, 60.5) * mm, "end": v(-136.38, 60.5) * mm});
            skLineSegment(sketch, "E608.trimOffspring", {"start": v(-173, 60) * mm, "end": v(-9.5, 60) * mm});
            skPoint(sketch, "E609.orphan", {"position": v(-172.5, -163) * mm});
            skPoint(sketch, "E610.orphan", {"position": v(-172.5, -125.5) * mm});
            skPoint(sketch, "E611.orphan", {"position": v(-172.5, -124.5) * mm});
            skPoint(sketch, "E612.orphan", {"position": v(-172.5, 20.5) * mm});
            skPoint(sketch, "E613.orphan", {"position": v(172.5, -125.5) * mm});
            skPoint(sketch, "E614.orphan", {"position": v(172.5, -124.5) * mm});
            skPoint(sketch, "E615.orphan", {"position": v(172.5, -163) * mm});
            skLineSegment(sketch, "E616.trimOffspring", {"start": v(9.5, 40.5) * mm, "end": v(9.5, 0) * mm});
            skLineSegment(sketch, "E617.trimOffspring", {"start": v(10, 40.5) * mm, "end": v(10, 0) * mm});
            skLineSegment(sketch, "E618.trimOffspring", {"start": v(10.5, 40.5) * mm, "end": v(10.5, 0) * mm});
            skLineSegment(sketch, "E619.trimOffspring", {"start": v(-0.5, 59.5) * mm, "end": v(0, 59.5) * mm});
            skLineSegment(sketch, "E620.trimOffspring", {"start": v(-0.5, 60) * mm, "end": v(0, 60) * mm});
            skLineSegment(sketch, "E621.trimOffspring", {"start": v(-0.5, 60.5) * mm, "end": v(0, 60.5) * mm});
            skLineSegment(sketch, "E622", {"start": v(-172, 0.5) * mm, "end": v(-172, 0) * mm});
            skSolve(sketch);
        }
        {
            var Q0;
            Q0=qCreatedBy(makeId("Right.planeOp"),FACE);
            cPlane(context, id + "F26", {"entities" : qUnion([Q0]), "cplaneType" : CPlaneType.OFFSET, "offset" : 182.5 * mm, "width" : 150 * mm, "height" : 150 * mm});
        }
        {
            var Q0;
            Q0=qCreatedBy(makeId("Front.planeOp"),FACE);
            cPlane(context, id + "F27", {"entities" : qUnion([Q0]), "cplaneType" : CPlaneType.OFFSET, "offset" : 50 * mm, "width" : 150 * mm, "height" : 150 * mm});
        }
        {
            var Q0;
            Q0=qCreatedBy(makeId("Right.planeOp"),FACE);
            cPlane(context, id + "F28", {"entities" : qUnion([Q0]), "cplaneType" : CPlaneType.OFFSET, "offset" : 172.5 * mm, "oppositeDirection" : true, "width" : 150 * mm, "height" : 150 * mm});
        }
        {
            var Q0;
            Q0=qCreatedBy(makeId("Front.planeOp"),FACE);
            cPlane(context, id + "F29", {"entities" : qUnion([Q0]), "cplaneType" : CPlaneType.OFFSET, "offset" : 50 * mm, "oppositeDirection" : true, "width" : 150 * mm, "height" : 150 * mm});
        }
        {
            var Q0;
            Q0=qCreatedBy(makeId("Right.planeOp"),FACE);
            var sketch = newSketch(context, id + "F30", { "sketchPlane" : qUnion([Q0])});
            skLineSegment(sketch, "E623", {"start": v(0, 20) * mm, "end": v(-200, 20) * mm});
            skPoint(sketch, "E624", {"position": v(-20, 20) * mm});
            skPoint(sketch, "E625", {"position": v(-40, 20) * mm});
            skPoint(sketch, "E626", {"position": v(-165, 20) * mm});
            skPoint(sketch, "E627", {"position": v(-60, 20) * mm});
            skPoint(sketch, "E628", {"position": v(-95, 20) * mm});
            skPoint(sketch, "E629", {"position": v(-130, 20) * mm});
            skPoint(sketch, "E630", {"position": v(-100, 20) * mm});
            skPoint(sketch, "E631.MirrorP", {"position": v(20, 20) * mm});
            skPoint(sketch, "E632.MirrorP", {"position": v(40, 20) * mm});
            skLineSegment(sketch, "E633", {"start": v(40, 20) * mm, "end": v(0, 20) * mm});
            skLineSegment(sketch, "E634.bottom", {"start": v(40, 20) * mm, "end": v(-200, 20) * mm});
            skLineSegment(sketch, "E634.top", {"start": v(40, 10) * mm, "end": v(-200, 10) * mm});
            skLineSegment(sketch, "E634.left", {"start": v(40, 20) * mm, "end": v(40, 10) * mm});
            skLineSegment(sketch, "E634.right", {"start": v(-200, 20) * mm, "end": v(-200, 10) * mm});
            skLineSegment(sketch, "E635", {"start": v(20, 20) * mm, "end": v(20, 10) * mm});
            skLineSegment(sketch, "E636", {"start": v(40, 15) * mm, "end": v(-200, 15) * mm});
            skLineSegment(sketch, "E637", {"start": v(-20, 20) * mm, "end": v(-20, 10) * mm});
            skLineSegment(sketch, "E638", {"start": v(0, 20) * mm, "end": v(0, 10) * mm});
            skLineSegment(sketch, "E639", {"start": v(-40, 20) * mm, "end": v(-40, 10) * mm});
            skLineSegment(sketch, "E640", {"start": v(-60, 20) * mm, "end": v(-60, 10) * mm});
            skLineSegment(sketch, "E641", {"start": v(-95, 20) * mm, "end": v(-95, 10) * mm});
            skLineSegment(sketch, "E642", {"start": v(-130, 20) * mm, "end": v(-130, 10) * mm});
            skLineSegment(sketch, "E643", {"start": v(-165, 20) * mm, "end": v(-165, 10) * mm});
            skLineSegment(sketch, "E644.bottom", {"start": v(-200, 10) * mm, "end": v(40, 10) * mm});
            skLineSegment(sketch, "E644.top", {"start": v(-200, 0) * mm, "end": v(40, 0) * mm});
            skLineSegment(sketch, "E644.left", {"start": v(-200, 10) * mm, "end": v(-200, 0) * mm});
            skLineSegment(sketch, "E644.right", {"start": v(40, 10) * mm, "end": v(40, 0) * mm});
            skLineSegment(sketch, "E645.bottom", {"start": v(200, 10.5) * mm, "end": v(-200, 10.5) * mm});
            skLineSegment(sketch, "E645.top", {"start": v(200, 9.5) * mm, "end": v(-200, 9.5) * mm});
            skLineSegment(sketch, "E645.left", {"start": v(200, 10.5) * mm, "end": v(200, 9.5) * mm});
            skLineSegment(sketch, "E645.right", {"start": v(-200, 10.5) * mm, "end": v(-200, 9.5) * mm});
            skPoint(sketch, "E645.middle", {"position": v(0, 10) * mm});
            skLineSegment(sketch, "E646.bottom", {"start": v(200, 14.5) * mm, "end": v(-200, 14.5) * mm});
            skLineSegment(sketch, "E646.top", {"start": v(200, 15.5) * mm, "end": v(-200, 15.5) * mm});
            skLineSegment(sketch, "E646.left", {"start": v(200, 14.5) * mm, "end": v(200, 15.5) * mm});
            skLineSegment(sketch, "E646.right", {"start": v(-200, 14.5) * mm, "end": v(-200, 15.5) * mm});
            skPoint(sketch, "E646.middle", {"position": v(0, 15) * mm});
            skLineSegment(sketch, "E647.bottom", {"start": v(-200, 19.5) * mm, "end": v(200, 19.5) * mm});
            skLineSegment(sketch, "E647.top", {"start": v(-200, 20.5) * mm, "end": v(200, 20.5) * mm});
            skLineSegment(sketch, "E647.left", {"start": v(-200, 19.5) * mm, "end": v(-200, 20.5) * mm});
            skLineSegment(sketch, "E647.right", {"start": v(200, 19.5) * mm, "end": v(200, 20.5) * mm});
            skPoint(sketch, "E647.middle", {"position": v(0, 20) * mm});
            skLineSegment(sketch, "E648.bottom", {"start": v(40.5, 20) * mm, "end": v(39.5, 20) * mm});
            skLineSegment(sketch, "E648.top", {"start": v(40.5, 10) * mm, "end": v(39.5, 10) * mm});
            skLineSegment(sketch, "E648.left", {"start": v(40.5, 20) * mm, "end": v(40.5, 10) * mm});
            skLineSegment(sketch, "E648.right", {"start": v(39.5, 20) * mm, "end": v(39.5, 10) * mm});
            skPoint(sketch, "E648.middle", {"position": v(40, 15) * mm});
            skLineSegment(sketch, "E649.bottom", {"start": v(20.5, 20) * mm, "end": v(19.5, 20) * mm});
            skLineSegment(sketch, "E649.top", {"start": v(20.5, 10) * mm, "end": v(19.5, 10) * mm});
            skLineSegment(sketch, "E649.left", {"start": v(20.5, 20) * mm, "end": v(20.5, 10) * mm});
            skLineSegment(sketch, "E649.right", {"start": v(19.5, 20) * mm, "end": v(19.5, 10) * mm});
            skPoint(sketch, "E649.middle", {"position": v(20, 15) * mm});
            skLineSegment(sketch, "E650.bottom", {"start": v(0.5, 20) * mm, "end": v(-0.5, 20) * mm});
            skLineSegment(sketch, "E650.top", {"start": v(0.5, 10) * mm, "end": v(-0.5, 10) * mm});
            skLineSegment(sketch, "E650.left", {"start": v(0.5, 20) * mm, "end": v(0.5, 10) * mm});
            skLineSegment(sketch, "E650.right", {"start": v(-0.5, 20) * mm, "end": v(-0.5, 10) * mm});
            skLineSegment(sketch, "E651.bottom", {"start": v(-19.5, 20) * mm, "end": v(-20.5, 20) * mm});
            skLineSegment(sketch, "E651.top", {"start": v(-19.5, 10) * mm, "end": v(-20.5, 10) * mm});
            skLineSegment(sketch, "E651.left", {"start": v(-19.5, 20) * mm, "end": v(-19.5, 10) * mm});
            skLineSegment(sketch, "E651.right", {"start": v(-20.5, 20) * mm, "end": v(-20.5, 10) * mm});
            skPoint(sketch, "E651.middle", {"position": v(-20, 15) * mm});
            skLineSegment(sketch, "E652.bottom", {"start": v(-39.5, 20) * mm, "end": v(-40.5, 20) * mm});
            skLineSegment(sketch, "E652.top", {"start": v(-39.5, 10) * mm, "end": v(-40.5, 10) * mm});
            skLineSegment(sketch, "E652.left", {"start": v(-39.5, 20) * mm, "end": v(-39.5, 10) * mm});
            skLineSegment(sketch, "E652.right", {"start": v(-40.5, 20) * mm, "end": v(-40.5, 10) * mm});
            skPoint(sketch, "E652.middle", {"position": v(-40, 15) * mm});
            skLineSegment(sketch, "E653.bottom", {"start": v(-59.5, 20) * mm, "end": v(-60.5, 20) * mm});
            skLineSegment(sketch, "E653.top", {"start": v(-59.5, 10) * mm, "end": v(-60.5, 10) * mm});
            skLineSegment(sketch, "E653.left", {"start": v(-59.5, 20) * mm, "end": v(-59.5, 10) * mm});
            skLineSegment(sketch, "E653.right", {"start": v(-60.5, 20) * mm, "end": v(-60.5, 10) * mm});
            skPoint(sketch, "E653.middle", {"position": v(-60, 15) * mm});
            skLineSegment(sketch, "E654.bottom", {"start": v(-95.5, 20) * mm, "end": v(-94.5, 20) * mm});
            skLineSegment(sketch, "E654.top", {"start": v(-95.5, 10) * mm, "end": v(-94.5, 10) * mm});
            skLineSegment(sketch, "E654.left", {"start": v(-95.5, 20) * mm, "end": v(-95.5, 10) * mm});
            skLineSegment(sketch, "E654.right", {"start": v(-94.5, 20) * mm, "end": v(-94.5, 10) * mm});
            skPoint(sketch, "E654.middle", {"position": v(-95, 15) * mm});
            skLineSegment(sketch, "E655.bottom", {"start": v(-129.5, 20) * mm, "end": v(-130.5, 20) * mm});
            skLineSegment(sketch, "E655.top", {"start": v(-129.5, 10) * mm, "end": v(-130.5, 10) * mm});
            skLineSegment(sketch, "E655.left", {"start": v(-129.5, 20) * mm, "end": v(-129.5, 10) * mm});
            skLineSegment(sketch, "E655.right", {"start": v(-130.5, 20) * mm, "end": v(-130.5, 10) * mm});
            skPoint(sketch, "E655.middle", {"position": v(-130, 15) * mm});
            skLineSegment(sketch, "E656.bottom", {"start": v(-164.5, 20) * mm, "end": v(-165.5, 20) * mm});
            skLineSegment(sketch, "E656.top", {"start": v(-164.5, 10) * mm, "end": v(-165.5, 10) * mm});
            skLineSegment(sketch, "E656.left", {"start": v(-164.5, 20) * mm, "end": v(-164.5, 10) * mm});
            skLineSegment(sketch, "E656.right", {"start": v(-165.5, 20) * mm, "end": v(-165.5, 10) * mm});
            skPoint(sketch, "E656.middle", {"position": v(-165, 15) * mm});
            skSolve(sketch);
        }
        {
            var Q0;
            Q0=qCreatedBy(id+"F27.planeOp",FACE);
            var sketch = newSketch(context, id + "F31", { "sketchPlane" : qUnion([Q0])});
            skLineSegment(sketch, "E657.bottom", {"start": v(-365, 20) * mm, "end": v(365, 20) * mm});
            skLineSegment(sketch, "E657.top", {"start": v(-365, 0) * mm, "end": v(365, 0) * mm});
            skLineSegment(sketch, "E657.left", {"start": v(-365, 20) * mm, "end": v(-365, 0) * mm});
            skLineSegment(sketch, "E657.right", {"start": v(365, 20) * mm, "end": v(365, 0) * mm});
            skLineSegment(sketch, "E658", {"start": v(-365, 10) * mm, "end": v(365, 10) * mm});
            skLineSegment(sketch, "E659", {"start": v(-365, 15) * mm, "end": v(365, 15) * mm});
            skPoint(sketch, "E660", {"position": v(10, 20) * mm});
            skPoint(sketch, "E661", {"position": v(50.63, 20) * mm});
            skPoint(sketch, "E662", {"position": v(91.25, 20) * mm});
            skPoint(sketch, "E663", {"position": v(131.88, 20) * mm});
            skPoint(sketch, "E664", {"position": v(172.5, 20) * mm});
            skPoint(sketch, "E665", {"position": v(321.88, 20) * mm});
            skPoint(sketch, "E666", {"position": v(192.5, 20) * mm});
            skPoint(sketch, "E667", {"position": v(235.63, 20) * mm});
            skPoint(sketch, "E668", {"position": v(278.75, 20) * mm});
            skLineSegment(sketch, "E669", {"start": v(10, 20) * mm, "end": v(10, 10) * mm});
            skLineSegment(sketch, "E670", {"start": v(50.63, 20) * mm, "end": v(50.63, 10) * mm});
            skLineSegment(sketch, "E671", {"start": v(91.25, 20) * mm, "end": v(91.25, 10) * mm});
            skLineSegment(sketch, "E672", {"start": v(131.88, 20) * mm, "end": v(131.88, 10) * mm});
            skLineSegment(sketch, "E673", {"start": v(172.5, 20) * mm, "end": v(172.5, 10) * mm});
            skLineSegment(sketch, "E674", {"start": v(192.5, 20) * mm, "end": v(192.5, 10) * mm});
            skLineSegment(sketch, "E675", {"start": v(235.63, 20) * mm, "end": v(235.63, 10) * mm});
            skLineSegment(sketch, "E676", {"start": v(278.75, 20) * mm, "end": v(278.75, 10) * mm});
            skLineSegment(sketch, "E677", {"start": v(321.88, 20) * mm, "end": v(321.88, 10) * mm});
            skLineSegment(sketch, "E678.MirrorCS", {"start": v(-10, 20) * mm, "end": v(-10, 10) * mm});
            skLineSegment(sketch, "E679.MirrorCS", {"start": v(-50.63, 20) * mm, "end": v(-50.63, 10) * mm});
            skLineSegment(sketch, "E680.MirrorCS", {"start": v(-91.25, 20) * mm, "end": v(-91.25, 10) * mm});
            skLineSegment(sketch, "E681.MirrorCS", {"start": v(-131.88, 20) * mm, "end": v(-131.88, 10) * mm});
            skLineSegment(sketch, "E682.MirrorCS", {"start": v(-172.5, 20) * mm, "end": v(-172.5, 10) * mm});
            skLineSegment(sketch, "E683.MirrorCS", {"start": v(-192.5, 20) * mm, "end": v(-192.5, 10) * mm});
            skLineSegment(sketch, "E684.MirrorCS", {"start": v(-235.63, 20) * mm, "end": v(-235.63, 10) * mm});
            skLineSegment(sketch, "E685.MirrorCS", {"start": v(-278.75, 20) * mm, "end": v(-278.75, 10) * mm});
            skLineSegment(sketch, "E686.MirrorCS", {"start": v(-321.88, 20) * mm, "end": v(-321.88, 10) * mm});
            skLineSegment(sketch, "E687.bottom", {"start": v(-365, 10.5) * mm, "end": v(365, 10.5) * mm});
            skLineSegment(sketch, "E687.top", {"start": v(-365, 9.5) * mm, "end": v(365, 9.5) * mm});
            skLineSegment(sketch, "E687.left", {"start": v(-365, 10.5) * mm, "end": v(-365, 9.5) * mm});
            skLineSegment(sketch, "E687.right", {"start": v(365, 10.5) * mm, "end": v(365, 9.5) * mm});
            skPoint(sketch, "E687.middle", {"position": v(0, 10) * mm});
            skLineSegment(sketch, "E688.bottom", {"start": v(-365, 15.5) * mm, "end": v(365, 15.5) * mm});
            skLineSegment(sketch, "E688.top", {"start": v(-365, 14.5) * mm, "end": v(365, 14.5) * mm});
            skLineSegment(sketch, "E688.left", {"start": v(-365, 15.5) * mm, "end": v(-365, 14.5) * mm});
            skLineSegment(sketch, "E688.right", {"start": v(365, 15.5) * mm, "end": v(365, 14.5) * mm});
            skPoint(sketch, "E688.middle", {"position": v(0, 15) * mm});
            skLineSegment(sketch, "E689.bottom", {"start": v(-365, 20.5) * mm, "end": v(365, 20.5) * mm});
            skLineSegment(sketch, "E689.top", {"start": v(-365, 19.5) * mm, "end": v(365, 19.5) * mm});
            skLineSegment(sketch, "E689.left", {"start": v(-365, 20.5) * mm, "end": v(-365, 19.5) * mm});
            skLineSegment(sketch, "E689.right", {"start": v(365, 20.5) * mm, "end": v(365, 19.5) * mm});
            skPoint(sketch, "E689.middle", {"position": v(0, 20) * mm});
            skLineSegment(sketch, "E690.bottom", {"start": v(-10.5, 20) * mm, "end": v(-9.5, 20) * mm});
            skLineSegment(sketch, "E690.top", {"start": v(-10.5, 10) * mm, "end": v(-9.5, 10) * mm});
            skLineSegment(sketch, "E690.left", {"start": v(-10.5, 20) * mm, "end": v(-10.5, 10) * mm});
            skLineSegment(sketch, "E690.right", {"start": v(-9.5, 20) * mm, "end": v(-9.5, 10) * mm});
            skPoint(sketch, "E690.middle", {"position": v(-10, 15) * mm});
            skLineSegment(sketch, "E691.bottom", {"start": v(-0.5, 20) * mm, "end": v(0.5, 20) * mm});
            skLineSegment(sketch, "E691.top", {"start": v(-0.5, 10) * mm, "end": v(0.5, 10) * mm});
            skLineSegment(sketch, "E691.left", {"start": v(-0.5, 20) * mm, "end": v(-0.5, 10) * mm});
            skLineSegment(sketch, "E691.right", {"start": v(0.5, 20) * mm, "end": v(0.5, 10) * mm});
            skLineSegment(sketch, "E692.bottom", {"start": v(-51.13, 20) * mm, "end": v(-50.13, 20) * mm});
            skLineSegment(sketch, "E692.top", {"start": v(-51.13, 10) * mm, "end": v(-50.13, 10) * mm});
            skLineSegment(sketch, "E692.left", {"start": v(-51.13, 20) * mm, "end": v(-51.13, 10) * mm});
            skLineSegment(sketch, "E692.right", {"start": v(-50.13, 20) * mm, "end": v(-50.13, 10) * mm});
            skPoint(sketch, "E692.middle", {"position": v(-50.63, 15) * mm});
            skLineSegment(sketch, "E693.bottom", {"start": v(-91.75, 20) * mm, "end": v(-90.75, 20) * mm});
            skLineSegment(sketch, "E693.top", {"start": v(-91.75, 10) * mm, "end": v(-90.75, 10) * mm});
            skLineSegment(sketch, "E693.left", {"start": v(-91.75, 20) * mm, "end": v(-91.75, 10) * mm});
            skLineSegment(sketch, "E693.right", {"start": v(-90.75, 20) * mm, "end": v(-90.75, 10) * mm});
            skPoint(sketch, "E693.middle", {"position": v(-91.25, 15) * mm});
            skLineSegment(sketch, "E694.bottom", {"start": v(-131.38, 20) * mm, "end": v(-132.38, 20) * mm});
            skLineSegment(sketch, "E694.top", {"start": v(-131.38, 10) * mm, "end": v(-132.38, 10) * mm});
            skLineSegment(sketch, "E694.left", {"start": v(-131.38, 20) * mm, "end": v(-131.38, 10) * mm});
            skLineSegment(sketch, "E694.right", {"start": v(-132.38, 20) * mm, "end": v(-132.38, 10) * mm});
            skPoint(sketch, "E694.middle", {"position": v(-131.88, 15) * mm});
            skLineSegment(sketch, "E695.bottom", {"start": v(-173, 20) * mm, "end": v(-172, 20) * mm});
            skLineSegment(sketch, "E695.top", {"start": v(-173, 10) * mm, "end": v(-172, 10) * mm});
            skLineSegment(sketch, "E695.left", {"start": v(-173, 20) * mm, "end": v(-173, 10) * mm});
            skLineSegment(sketch, "E695.right", {"start": v(-172, 20) * mm, "end": v(-172, 10) * mm});
            skPoint(sketch, "E695.middle", {"position": v(-172.5, 15) * mm});
            skLineSegment(sketch, "E696.bottom", {"start": v(-192, 20) * mm, "end": v(-193, 20) * mm});
            skLineSegment(sketch, "E696.top", {"start": v(-192, 10) * mm, "end": v(-193, 10) * mm});
            skLineSegment(sketch, "E696.left", {"start": v(-192, 20) * mm, "end": v(-192, 10) * mm});
            skLineSegment(sketch, "E696.right", {"start": v(-193, 20) * mm, "end": v(-193, 10) * mm});
            skPoint(sketch, "E696.middle", {"position": v(-192.5, 15) * mm});
            skLineSegment(sketch, "E697.bottom", {"start": v(-235.13, 20) * mm, "end": v(-236.13, 20) * mm});
            skLineSegment(sketch, "E697.top", {"start": v(-235.13, 10) * mm, "end": v(-236.13, 10) * mm});
            skLineSegment(sketch, "E697.left", {"start": v(-235.13, 20) * mm, "end": v(-235.13, 10) * mm});
            skLineSegment(sketch, "E697.right", {"start": v(-236.13, 20) * mm, "end": v(-236.13, 10) * mm});
            skPoint(sketch, "E697.middle", {"position": v(-235.63, 15) * mm});
            skLineSegment(sketch, "E698.bottom", {"start": v(-278.25, 20) * mm, "end": v(-279.25, 20) * mm});
            skLineSegment(sketch, "E698.top", {"start": v(-278.25, 10) * mm, "end": v(-279.25, 10) * mm});
            skLineSegment(sketch, "E698.left", {"start": v(-278.25, 20) * mm, "end": v(-278.25, 10) * mm});
            skLineSegment(sketch, "E698.right", {"start": v(-279.25, 20) * mm, "end": v(-279.25, 10) * mm});
            skPoint(sketch, "E698.middle", {"position": v(-278.75, 15) * mm});
            skLineSegment(sketch, "E699.bottom", {"start": v(-321.38, 20) * mm, "end": v(-322.38, 20) * mm});
            skLineSegment(sketch, "E699.top", {"start": v(-321.38, 10) * mm, "end": v(-322.38, 10) * mm});
            skLineSegment(sketch, "E699.left", {"start": v(-321.38, 20) * mm, "end": v(-321.38, 10) * mm});
            skLineSegment(sketch, "E699.right", {"start": v(-322.38, 20) * mm, "end": v(-322.38, 10) * mm});
            skPoint(sketch, "E699.middle", {"position": v(-321.88, 15) * mm});
            skLineSegment(sketch, "E700.MirrorCS", {"start": v(9.5, 20) * mm, "end": v(9.5, 10) * mm});
            skLineSegment(sketch, "E701.MirrorCS", {"start": v(10.5, 20) * mm, "end": v(10.5, 10) * mm});
            skLineSegment(sketch, "E702.MirrorCS", {"start": v(50.13, 20) * mm, "end": v(50.13, 10) * mm});
            skLineSegment(sketch, "E703.MirrorCS", {"start": v(51.13, 20) * mm, "end": v(51.13, 10) * mm});
            skLineSegment(sketch, "E704.MirrorCS", {"start": v(90.75, 20) * mm, "end": v(90.75, 10) * mm});
            skLineSegment(sketch, "E705.MirrorCS", {"start": v(91.75, 20) * mm, "end": v(91.75, 10) * mm});
            skLineSegment(sketch, "E706.MirrorCS", {"start": v(132.38, 20) * mm, "end": v(132.38, 10) * mm});
            skLineSegment(sketch, "E707.MirrorCS", {"start": v(131.38, 20) * mm, "end": v(131.38, 10) * mm});
            skLineSegment(sketch, "E708.MirrorCS", {"start": v(172, 20) * mm, "end": v(172, 10) * mm});
            skLineSegment(sketch, "E709.MirrorCS", {"start": v(173, 20) * mm, "end": v(173, 10) * mm});
            skLineSegment(sketch, "E710.MirrorCS", {"start": v(192, 20) * mm, "end": v(192, 10) * mm});
            skLineSegment(sketch, "E711.MirrorCS", {"start": v(193, 20) * mm, "end": v(193, 10) * mm});
            skLineSegment(sketch, "E712.MirrorCS", {"start": v(235.13, 20) * mm, "end": v(235.13, 10) * mm});
            skLineSegment(sketch, "E713.MirrorCS", {"start": v(236.13, 20) * mm, "end": v(236.13, 10) * mm});
            skLineSegment(sketch, "E714.MirrorCS", {"start": v(321.38, 20) * mm, "end": v(321.38, 10) * mm});
            skLineSegment(sketch, "E715.MirrorCS", {"start": v(322.38, 20) * mm, "end": v(322.38, 10) * mm});
            skSolve(sketch);
        }
        {
            var Q0;
            {var subQ76=sQuery(id+"F25.wireOp",EDGE,"E212.top");Q0=makeQuery(id+"F25.imprint","IMPRINT",FACE,{"disambiguationData":[TD([[makeQuery(id+"F25.imprint","IMPRINT",EDGE,{"derivedFrom":subQ76}),-1.0]])]});}
            extrude(context, id + "F32", {"entities" : qUnion([Q0]), "operationType" : NewBodyOperationType.REMOVE, "depth" : 25 * mm, "offsetDistance" : 25 * mm});
        }
        {
            var Q0;
            {var subQ0=sQuery(id+"F25.wireOp",EDGE,"E533.trimOffspring");var subQ1=sQuery(id+"F25.wireOp",EDGE,"E517.trimOffspring");var subQ2=makeQuery(id+"F25.imprint","INTERSECT",VERTEX,{"derivedFrom":[subQ1,subQ0]});Q0=makeQuery(id+"F25.imprint","IMPRINT",FACE,{"disambiguationData":[TD([[makeQuery(id+"F25.imprint","IMPRINT",EDGE,{"disambiguationData":[TD([[subQ2,-1.0]])],"derivedFrom":subQ1}),1.0]])]});}
            var Q1;
            {var subQ1=sQuery(id+"F25.wireOp",EDGE,"E248.left");var subQ3=sQuery(id+"F25.wireOp",EDGE,"E517.trimOffspring");var subQ4=makeQuery(id+"F25.imprint","INTERSECT",VERTEX,{"derivedFrom":[subQ1,subQ3]});Q1=makeQuery(id+"F25.imprint","IMPRINT",FACE,{"disambiguationData":[TD([[makeQuery(id+"F25.imprint","IMPRINT",EDGE,{"disambiguationData":[TD([[subQ4,1.0]])],"derivedFrom":subQ3}),1.0]])]});}
            var Q2;
            {var subQ0=sQuery(id+"F25.wireOp",EDGE,"E275.trimOffspring");var subQ1=sQuery(id+"F25.wireOp",EDGE,"E248.left");var subQ2=makeQuery(id+"F25.imprint","INTERSECT",VERTEX,{"derivedFrom":[subQ1,subQ0]});Q2=makeQuery(id+"F25.imprint","IMPRINT",FACE,{"disambiguationData":[TD([[makeQuery(id+"F25.imprint","IMPRINT",EDGE,{"disambiguationData":[TD([[subQ2,-1.0]])],"derivedFrom":subQ1}),1.0]])]});}
            var Q3;
            {var subQ0=sQuery(id+"F25.wireOp",EDGE,"E273.trimOffspring");var subQ1=sQuery(id+"F25.wireOp",EDGE,"E248.left");var subQ2=makeQuery(id+"F25.imprint","INTERSECT",VERTEX,{"derivedFrom":[subQ1,subQ0]});Q3=makeQuery(id+"F25.imprint","IMPRINT",FACE,{"disambiguationData":[TD([[makeQuery(id+"F25.imprint","IMPRINT",EDGE,{"disambiguationData":[TD([[subQ2,-1.0]])],"derivedFrom":subQ1}),1.0]])]});}
            var Q4;
            {var subQ0=sQuery(id+"F25.wireOp",EDGE,"E272.trimOffspring");var subQ1=sQuery(id+"F25.wireOp",EDGE,"E248.left");var subQ2=makeQuery(id+"F25.imprint","INTERSECT",VERTEX,{"derivedFrom":[subQ1,subQ0]});Q4=makeQuery(id+"F25.imprint","IMPRINT",FACE,{"disambiguationData":[TD([[makeQuery(id+"F25.imprint","IMPRINT",EDGE,{"disambiguationData":[TD([[subQ2,-1.0]])],"derivedFrom":subQ1}),1.0]])]});}
            var Q5;
            {var subQ0=sQuery(id+"F25.wireOp",EDGE,"E274.trimOffspring");var subQ1=sQuery(id+"F25.wireOp",EDGE,"E248.left");var subQ2=makeQuery(id+"F25.imprint","INTERSECT",VERTEX,{"derivedFrom":[subQ1,subQ0]});Q5=makeQuery(id+"F25.imprint","IMPRINT",FACE,{"disambiguationData":[TD([[makeQuery(id+"F25.imprint","IMPRINT",EDGE,{"disambiguationData":[TD([[subQ2,-1.0]])],"derivedFrom":subQ1}),1.0]])]});}
            var Q6;
            {var subQ0=sQuery(id+"F25.wireOp",EDGE,"E270.trimOffspring");var subQ1=sQuery(id+"F25.wireOp",EDGE,"E248.left");var subQ2=makeQuery(id+"F25.imprint","INTERSECT",VERTEX,{"derivedFrom":[subQ1,subQ0]});Q6=makeQuery(id+"F25.imprint","IMPRINT",FACE,{"disambiguationData":[TD([[makeQuery(id+"F25.imprint","IMPRINT",EDGE,{"disambiguationData":[TD([[subQ2,-1.0]])],"derivedFrom":subQ1}),1.0]])]});}
            var Q7;
            {var subQ0=sQuery(id+"F25.wireOp",EDGE,"E268.trimOffspring");var subQ1=sQuery(id+"F25.wireOp",EDGE,"E248.left");var subQ2=makeQuery(id+"F25.imprint","INTERSECT",VERTEX,{"derivedFrom":[subQ1,subQ0]});Q7=makeQuery(id+"F25.imprint","IMPRINT",FACE,{"disambiguationData":[TD([[makeQuery(id+"F25.imprint","IMPRINT",EDGE,{"disambiguationData":[TD([[subQ2,-1.0]])],"derivedFrom":subQ1}),1.0]])]});}
            var Q8;
            {var subQ0=sQuery(id+"F25.wireOp",EDGE,"E268.trimOffspring");var subQ1=sQuery(id+"F25.wireOp",EDGE,"E246.right");var subQ2=makeQuery(id+"F25.imprint","INTERSECT",VERTEX,{"derivedFrom":[subQ1,subQ0]});Q8=makeQuery(id+"F25.imprint","IMPRINT",FACE,{"disambiguationData":[TD([[makeQuery(id+"F25.imprint","IMPRINT",EDGE,{"disambiguationData":[TD([[subQ2,-1.0]])],"derivedFrom":subQ1}),-1.0]])]});}
            var Q9;
            {var subQ0=sQuery(id+"F25.wireOp",EDGE,"E268.trimOffspring");var subQ1=sQuery(id+"F25.wireOp",EDGE,"E245.right");var subQ2=makeQuery(id+"F25.imprint","INTERSECT",VERTEX,{"derivedFrom":[subQ1,subQ0]});Q9=makeQuery(id+"F25.imprint","IMPRINT",FACE,{"disambiguationData":[TD([[makeQuery(id+"F25.imprint","IMPRINT",EDGE,{"disambiguationData":[TD([[subQ2,-1.0]])],"derivedFrom":subQ1}),-1.0]])]});}
            var Q10;
            {var subQ0=sQuery(id+"F25.wireOp",EDGE,"E268.trimOffspring");var subQ1=sQuery(id+"F25.wireOp",EDGE,"E245.left");var subQ2=makeQuery(id+"F25.imprint","INTERSECT",VERTEX,{"derivedFrom":[subQ1,subQ0]});Q10=makeQuery(id+"F25.imprint","IMPRINT",FACE,{"disambiguationData":[TD([[makeQuery(id+"F25.imprint","IMPRINT",EDGE,{"disambiguationData":[TD([[subQ2,-1.0]])],"derivedFrom":subQ1}),-1.0]])]});}
            var Q11;
            {var subQ0=sQuery(id+"F25.wireOp",EDGE,"E268.trimOffspring");var subQ1=sQuery(id+"F25.wireOp",EDGE,"E244.right");var subQ2=makeQuery(id+"F25.imprint","INTERSECT",VERTEX,{"derivedFrom":[subQ1,subQ0]});Q11=makeQuery(id+"F25.imprint","IMPRINT",FACE,{"disambiguationData":[TD([[makeQuery(id+"F25.imprint","IMPRINT",EDGE,{"disambiguationData":[TD([[subQ2,-1.0]])],"derivedFrom":subQ1}),-1.0]])]});}
            var Q12;
            {var subQ0=sQuery(id+"F25.wireOp",EDGE,"E268.trimOffspring");var subQ1=sQuery(id+"F25.wireOp",EDGE,"E243.left");var subQ2=makeQuery(id+"F25.imprint","INTERSECT",VERTEX,{"derivedFrom":[subQ1,subQ0]});Q12=makeQuery(id+"F25.imprint","IMPRINT",FACE,{"disambiguationData":[TD([[makeQuery(id+"F25.imprint","IMPRINT",EDGE,{"disambiguationData":[TD([[subQ2,-1.0]])],"derivedFrom":subQ1}),-1.0]])]});}
            var Q13;
            {var subQ0=sQuery(id+"F25.wireOp",EDGE,"E269.trimOffspring");var subQ1=sQuery(id+"F25.wireOp",EDGE,"E243.right");var subQ2=makeQuery(id+"F25.imprint","INTERSECT",VERTEX,{"derivedFrom":[subQ1,subQ0]});Q13=makeQuery(id+"F25.imprint","IMPRINT",FACE,{"disambiguationData":[TD([[makeQuery(id+"F25.imprint","IMPRINT",EDGE,{"disambiguationData":[TD([[subQ2,1.0]])],"derivedFrom":subQ1}),-1.0]])]});}
            var Q14;
            {var subQ0=sQuery(id+"F25.wireOp",EDGE,"E267.trimOffspring");var subQ1=sQuery(id+"F25.wireOp",EDGE,"E243.right");var subQ2=makeQuery(id+"F25.imprint","INTERSECT",VERTEX,{"derivedFrom":[subQ1,subQ0]});Q14=makeQuery(id+"F25.imprint","IMPRINT",FACE,{"disambiguationData":[TD([[makeQuery(id+"F25.imprint","IMPRINT",EDGE,{"disambiguationData":[TD([[subQ2,-1.0]])],"derivedFrom":subQ1}),-1.0]])]});}
            var Q15;
            {var subQ0=sQuery(id+"F25.wireOp",EDGE,"E243.bottom");Q15=makeQuery(id+"F25.imprint","IMPRINT",FACE,{"disambiguationData":[TD([[makeQuery(id+"F25.imprint","IMPRINT",EDGE,{"derivedFrom":subQ0}),-1.0]])]});}
            var Q16;
            {var subQ0=sQuery(id+"F25.wireOp",EDGE,"E533.trimOffspring");var subQ1=sQuery(id+"F25.wireOp",EDGE,"E517.trimOffspring");var subQ2=makeQuery(id+"F25.imprint","INTERSECT",VERTEX,{"derivedFrom":[subQ1,subQ0]});Q16=makeQuery(id+"F25.imprint","IMPRINT",FACE,{"disambiguationData":[TD([[makeQuery(id+"F25.imprint","IMPRINT",EDGE,{"disambiguationData":[TD([[subQ2,1.0]])],"derivedFrom":subQ1}),1.0]])]});}
            var Q17;
            {var subQ0=sQuery(id+"F25.wireOp",EDGE,"E532.trimOffspring");var subQ1=sQuery(id+"F25.wireOp",EDGE,"E517.trimOffspring");var subQ2=makeQuery(id+"F25.imprint","INTERSECT",VERTEX,{"derivedFrom":[subQ1,subQ0]});Q17=makeQuery(id+"F25.imprint","IMPRINT",FACE,{"disambiguationData":[TD([[makeQuery(id+"F25.imprint","IMPRINT",EDGE,{"disambiguationData":[TD([[subQ2,-1.0]])],"derivedFrom":subQ1}),1.0]])]});}
            var Q18;
            {var subQ0=sQuery(id+"F25.wireOp",EDGE,"E532.trimOffspring");var subQ1=sQuery(id+"F25.wireOp",EDGE,"E518.trimOffspring");var subQ2=makeQuery(id+"F25.imprint","INTERSECT",VERTEX,{"derivedFrom":[subQ1,subQ0]});Q18=makeQuery(id+"F25.imprint","IMPRINT",FACE,{"disambiguationData":[TD([[makeQuery(id+"F25.imprint","IMPRINT",EDGE,{"disambiguationData":[TD([[subQ2,-1.0]])],"derivedFrom":subQ1}),-1.0]])]});}
            var Q19;
            {var subQ0=sQuery(id+"F25.wireOp",EDGE,"E532.trimOffspring");var subQ1=sQuery(id+"F25.wireOp",EDGE,"E507.trimOffspring");var subQ2=makeQuery(id+"F25.imprint","INTERSECT",VERTEX,{"derivedFrom":[subQ1,subQ0]});Q19=makeQuery(id+"F25.imprint","IMPRINT",FACE,{"disambiguationData":[TD([[makeQuery(id+"F25.imprint","IMPRINT",EDGE,{"disambiguationData":[TD([[subQ2,-1.0]])],"derivedFrom":subQ1}),-1.0]])]});}
            var Q20;
            {var subQ0=sQuery(id+"F25.wireOp",EDGE,"E532.trimOffspring");var subQ1=sQuery(id+"F25.wireOp",EDGE,"E517.trimOffspring");var subQ2=makeQuery(id+"F25.imprint","INTERSECT",VERTEX,{"derivedFrom":[subQ1,subQ0]});Q20=makeQuery(id+"F25.imprint","IMPRINT",FACE,{"disambiguationData":[TD([[makeQuery(id+"F25.imprint","IMPRINT",EDGE,{"disambiguationData":[TD([[subQ2,-1.0]])],"derivedFrom":subQ1}),1.0]])]});}
            var Q21;
            {var subQ0=sQuery(id+"F25.wireOp",EDGE,"E518.trimOffspring");var subQ1=sQuery(id+"F25.wireOp",EDGE,"E247.left");var subQ2=makeQuery(id+"F25.imprint","INTERSECT",VERTEX,{"derivedFrom":[subQ1,subQ0]});Q21=makeQuery(id+"F25.imprint","IMPRINT",FACE,{"disambiguationData":[TD([[makeQuery(id+"F25.imprint","IMPRINT",EDGE,{"disambiguationData":[TD([[subQ2,1.0]])],"derivedFrom":subQ0}),-1.0]])]});}
            var Q22;
            {var subQ0=sQuery(id+"F25.wireOp",EDGE,"E534.MirrorCS");var subQ1=sQuery(id+"F25.wireOp",EDGE,"E518.trimOffspring");var subQ2=makeQuery(id+"F25.imprint","INTERSECT",VERTEX,{"derivedFrom":[subQ1,subQ0]});Q22=makeQuery(id+"F25.imprint","IMPRINT",FACE,{"disambiguationData":[TD([[makeQuery(id+"F25.imprint","IMPRINT",EDGE,{"disambiguationData":[TD([[subQ2,1.0]])],"derivedFrom":subQ1}),-1.0]])]});}
            var Q23;
            {var subQ0=sQuery(id+"F25.wireOp",EDGE,"E527.trimOffspring");var subQ1=sQuery(id+"F25.wireOp",EDGE,"E518.trimOffspring");var subQ2=makeQuery(id+"F25.imprint","INTERSECT",VERTEX,{"derivedFrom":[subQ1,subQ0]});Q23=makeQuery(id+"F25.imprint","IMPRINT",FACE,{"disambiguationData":[TD([[makeQuery(id+"F25.imprint","IMPRINT",EDGE,{"disambiguationData":[TD([[subQ2,-1.0]])],"derivedFrom":subQ1}),-1.0]])]});}
            var Q24;
            {var subQ0=sQuery(id+"F25.wireOp",EDGE,"E532.trimOffspring");var subQ1=sQuery(id+"F25.wireOp",EDGE,"E507.trimOffspring");var subQ2=makeQuery(id+"F25.imprint","INTERSECT",VERTEX,{"derivedFrom":[subQ1,subQ0]});Q24=makeQuery(id+"F25.imprint","IMPRINT",FACE,{"disambiguationData":[TD([[makeQuery(id+"F25.imprint","IMPRINT",EDGE,{"disambiguationData":[TD([[subQ2,-1.0]])],"derivedFrom":subQ1}),1.0]])]});}
            var Q25;
            {var subQ0=sQuery(id+"F25.wireOp",EDGE,"E527.trimOffspring");var subQ1=sQuery(id+"F25.wireOp",EDGE,"E507.trimOffspring");var subQ2=makeQuery(id+"F25.imprint","INTERSECT",VERTEX,{"derivedFrom":[subQ1,subQ0]});Q25=makeQuery(id+"F25.imprint","IMPRINT",FACE,{"disambiguationData":[TD([[makeQuery(id+"F25.imprint","IMPRINT",EDGE,{"disambiguationData":[TD([[subQ2,-1.0]])],"derivedFrom":subQ1}),1.0]])]});}
            var Q26;
            {var subQ0=sQuery(id+"F25.wireOp",EDGE,"E535.trimOffspring");var subQ1=sQuery(id+"F25.wireOp",EDGE,"E507.trimOffspring");var subQ2=makeQuery(id+"F25.imprint","INTERSECT",VERTEX,{"derivedFrom":[subQ1,subQ0]});Q26=makeQuery(id+"F25.imprint","IMPRINT",FACE,{"disambiguationData":[TD([[makeQuery(id+"F25.imprint","IMPRINT",EDGE,{"disambiguationData":[TD([[subQ2,1.0]])],"derivedFrom":subQ1}),1.0]])]});}
            var Q27;
            {var subQ0=sQuery(id+"F25.wireOp",EDGE,"E527.trimOffspring");var subQ1=sQuery(id+"F25.wireOp",EDGE,"E507.trimOffspring");var subQ2=makeQuery(id+"F25.imprint","INTERSECT",VERTEX,{"derivedFrom":[subQ1,subQ0]});Q27=makeQuery(id+"F25.imprint","IMPRINT",FACE,{"disambiguationData":[TD([[makeQuery(id+"F25.imprint","IMPRINT",EDGE,{"disambiguationData":[TD([[subQ2,-1.0]])],"derivedFrom":subQ1}),-1.0]])]});}
            var Q28;
            {var subQ0=sQuery(id+"F25.wireOp",EDGE,"E520.trimOffspring");var subQ1=sQuery(id+"F25.wireOp",EDGE,"E507.trimOffspring");var subQ2=makeQuery(id+"F25.imprint","INTERSECT",VERTEX,{"derivedFrom":[subQ1,subQ0]});Q28=makeQuery(id+"F25.imprint","IMPRINT",FACE,{"disambiguationData":[TD([[makeQuery(id+"F25.imprint","IMPRINT",EDGE,{"disambiguationData":[TD([[subQ2,1.0]])],"derivedFrom":subQ1}),1.0]])]});}
            var Q29;
            {var subQ0=sQuery(id+"F25.wireOp",EDGE,"E523.trimOffspring");var subQ1=sQuery(id+"F25.wireOp",EDGE,"E507.trimOffspring");var subQ2=makeQuery(id+"F25.imprint","INTERSECT",VERTEX,{"derivedFrom":[subQ1,subQ0]});Q29=makeQuery(id+"F25.imprint","IMPRINT",FACE,{"disambiguationData":[TD([[makeQuery(id+"F25.imprint","IMPRINT",EDGE,{"disambiguationData":[TD([[subQ2,1.0]])],"derivedFrom":subQ1}),1.0]])]});}
            var Q30;
            {var subQ0=sQuery(id+"F25.wireOp",EDGE,"E532.trimOffspring");var subQ1=sQuery(id+"F25.wireOp",EDGE,"E510.trimOffspring");var subQ2=makeQuery(id+"F25.imprint","INTERSECT",VERTEX,{"derivedFrom":[subQ1,subQ0]});Q30=makeQuery(id+"F25.imprint","IMPRINT",FACE,{"disambiguationData":[TD([[makeQuery(id+"F25.imprint","IMPRINT",EDGE,{"disambiguationData":[TD([[subQ2,-1.0]])],"derivedFrom":subQ1}),-1.0]])]});}
            var Q31;
            {var subQ0=sQuery(id+"F25.wireOp",EDGE,"E527.trimOffspring");var subQ1=sQuery(id+"F25.wireOp",EDGE,"E510.trimOffspring");var subQ2=makeQuery(id+"F25.imprint","INTERSECT",VERTEX,{"derivedFrom":[subQ1,subQ0]});Q31=makeQuery(id+"F25.imprint","IMPRINT",FACE,{"disambiguationData":[TD([[makeQuery(id+"F25.imprint","IMPRINT",EDGE,{"disambiguationData":[TD([[subQ2,-1.0]])],"derivedFrom":subQ1}),-1.0]])]});}
            var Q32;
            {var subQ0=sQuery(id+"F25.wireOp",EDGE,"E533.trimOffspring");var subQ1=sQuery(id+"F25.wireOp",EDGE,"E510.trimOffspring");var subQ2=makeQuery(id+"F25.imprint","INTERSECT",VERTEX,{"derivedFrom":[subQ1,subQ0]});Q32=makeQuery(id+"F25.imprint","IMPRINT",FACE,{"disambiguationData":[TD([[makeQuery(id+"F25.imprint","IMPRINT",EDGE,{"disambiguationData":[TD([[subQ2,-1.0]])],"derivedFrom":subQ1}),-1.0]])]});}
            var Q33;
            {var subQ0=sQuery(id+"F25.wireOp",EDGE,"E532.trimOffspring");var subQ1=sQuery(id+"F25.wireOp",EDGE,"E510.trimOffspring");var subQ2=makeQuery(id+"F25.imprint","INTERSECT",VERTEX,{"derivedFrom":[subQ1,subQ0]});Q33=makeQuery(id+"F25.imprint","IMPRINT",FACE,{"disambiguationData":[TD([[makeQuery(id+"F25.imprint","IMPRINT",EDGE,{"disambiguationData":[TD([[subQ2,-1.0]])],"derivedFrom":subQ1}),-1.0]])]});}
            var Q34;
            {var subQ0=sQuery(id+"F25.wireOp",EDGE,"E535.trimOffspring");var subQ1=sQuery(id+"F25.wireOp",EDGE,"E510.trimOffspring");var subQ2=makeQuery(id+"F25.imprint","INTERSECT",VERTEX,{"derivedFrom":[subQ1,subQ0]});Q34=makeQuery(id+"F25.imprint","IMPRINT",FACE,{"disambiguationData":[TD([[makeQuery(id+"F25.imprint","IMPRINT",EDGE,{"disambiguationData":[TD([[subQ2,-1.0]])],"derivedFrom":subQ1}),-1.0]])]});}
            var Q35;
            {var subQ0=sQuery(id+"F25.wireOp",EDGE,"E520.trimOffspring");var subQ1=sQuery(id+"F25.wireOp",EDGE,"E510.trimOffspring");var subQ2=makeQuery(id+"F25.imprint","INTERSECT",VERTEX,{"derivedFrom":[subQ1,subQ0]});Q35=makeQuery(id+"F25.imprint","IMPRINT",FACE,{"disambiguationData":[TD([[makeQuery(id+"F25.imprint","IMPRINT",EDGE,{"disambiguationData":[TD([[subQ2,-1.0]])],"derivedFrom":subQ1}),-1.0]])]});}
            var Q36;
            {var subQ0=sQuery(id+"F25.wireOp",EDGE,"E518.trimOffspring");var subQ5=sQuery(id+"F25.wireOp",EDGE,"E248.right");var subQ7=makeQuery(id+"F25.imprint","INTERSECT",VERTEX,{"derivedFrom":[subQ5,subQ0]});Q36=makeQuery(id+"F25.imprint","IMPRINT",FACE,{"disambiguationData":[TD([[makeQuery(id+"F25.imprint","IMPRINT",EDGE,{"disambiguationData":[TD([[subQ7,1.0]])],"derivedFrom":subQ5}),1.0]])]});}
            var Q37;
            {var subQ3=sQuery(id+"F25.wireOp",EDGE,"E517.trimOffspring");var subQ5=sQuery(id+"F25.wireOp",EDGE,"E248.right");var subQ6=makeQuery(id+"F25.imprint","INTERSECT",VERTEX,{"derivedFrom":[subQ5,subQ3]});Q37=makeQuery(id+"F25.imprint","IMPRINT",FACE,{"disambiguationData":[TD([[makeQuery(id+"F25.imprint","IMPRINT",EDGE,{"disambiguationData":[TD([[subQ6,-1.0]])],"derivedFrom":subQ5}),1.0]])]});}
            var Q38;
            {var subQ0=sQuery(id+"F25.wireOp",EDGE,"E275.trimOffspring");var subQ1=sQuery(id+"F25.wireOp",EDGE,"E248.left");var subQ2=makeQuery(id+"F25.imprint","INTERSECT",VERTEX,{"derivedFrom":[subQ1,subQ0]});Q38=makeQuery(id+"F25.imprint","IMPRINT",FACE,{"disambiguationData":[TD([[makeQuery(id+"F25.imprint","IMPRINT",EDGE,{"disambiguationData":[TD([[subQ2,-1.0]])],"derivedFrom":subQ1}),-1.0]])]});}
            var Q39;
            {var subQ0=sQuery(id+"F25.wireOp",EDGE,"E273.trimOffspring");var subQ1=sQuery(id+"F25.wireOp",EDGE,"E248.left");var subQ2=makeQuery(id+"F25.imprint","INTERSECT",VERTEX,{"derivedFrom":[subQ1,subQ0]});Q39=makeQuery(id+"F25.imprint","IMPRINT",FACE,{"disambiguationData":[TD([[makeQuery(id+"F25.imprint","IMPRINT",EDGE,{"disambiguationData":[TD([[subQ2,-1.0]])],"derivedFrom":subQ1}),-1.0]])]});}
            var Q40;
            {var subQ0=sQuery(id+"F25.wireOp",EDGE,"E272.trimOffspring");var subQ1=sQuery(id+"F25.wireOp",EDGE,"E248.left");var subQ2=makeQuery(id+"F25.imprint","INTERSECT",VERTEX,{"derivedFrom":[subQ1,subQ0]});Q40=makeQuery(id+"F25.imprint","IMPRINT",FACE,{"disambiguationData":[TD([[makeQuery(id+"F25.imprint","IMPRINT",EDGE,{"disambiguationData":[TD([[subQ2,-1.0]])],"derivedFrom":subQ1}),-1.0]])]});}
            var Q41;
            {var subQ0=sQuery(id+"F25.wireOp",EDGE,"E272.trimOffspring");var subQ1=sQuery(id+"F25.wireOp",EDGE,"E246.right");var subQ2=makeQuery(id+"F25.imprint","INTERSECT",VERTEX,{"derivedFrom":[subQ1,subQ0]});Q41=makeQuery(id+"F25.imprint","IMPRINT",FACE,{"disambiguationData":[TD([[makeQuery(id+"F25.imprint","IMPRINT",EDGE,{"disambiguationData":[TD([[subQ2,-1.0]])],"derivedFrom":subQ1}),-1.0]])]});}
            var Q42;
            {var subQ0=sQuery(id+"F25.wireOp",EDGE,"E272.trimOffspring");var subQ1=sQuery(id+"F25.wireOp",EDGE,"E245.left");var subQ2=makeQuery(id+"F25.imprint","INTERSECT",VERTEX,{"derivedFrom":[subQ1,subQ0]});Q42=makeQuery(id+"F25.imprint","IMPRINT",FACE,{"disambiguationData":[TD([[makeQuery(id+"F25.imprint","IMPRINT",EDGE,{"disambiguationData":[TD([[subQ2,-1.0]])],"derivedFrom":subQ1}),-1.0]])]});}
            var Q43;
            {var subQ0=sQuery(id+"F25.wireOp",EDGE,"E273.trimOffspring");var subQ1=sQuery(id+"F25.wireOp",EDGE,"E245.right");var subQ2=makeQuery(id+"F25.imprint","INTERSECT",VERTEX,{"derivedFrom":[subQ1,subQ0]});Q43=makeQuery(id+"F25.imprint","IMPRINT",FACE,{"disambiguationData":[TD([[makeQuery(id+"F25.imprint","IMPRINT",EDGE,{"disambiguationData":[TD([[subQ2,1.0]])],"derivedFrom":subQ1}),-1.0]])]});}
            var Q44;
            {var subQ0=sQuery(id+"F25.wireOp",EDGE,"E272.trimOffspring");var subQ1=sQuery(id+"F25.wireOp",EDGE,"E244.right");var subQ2=makeQuery(id+"F25.imprint","INTERSECT",VERTEX,{"derivedFrom":[subQ1,subQ0]});Q44=makeQuery(id+"F25.imprint","IMPRINT",FACE,{"disambiguationData":[TD([[makeQuery(id+"F25.imprint","IMPRINT",EDGE,{"disambiguationData":[TD([[subQ2,-1.0]])],"derivedFrom":subQ1}),-1.0]])]});}
            var Q45;
            {var subQ0=sQuery(id+"F25.wireOp",EDGE,"E272.trimOffspring");var subQ1=sQuery(id+"F25.wireOp",EDGE,"E243.left");var subQ2=makeQuery(id+"F25.imprint","INTERSECT",VERTEX,{"derivedFrom":[subQ1,subQ0]});Q45=makeQuery(id+"F25.imprint","IMPRINT",FACE,{"disambiguationData":[TD([[makeQuery(id+"F25.imprint","IMPRINT",EDGE,{"disambiguationData":[TD([[subQ2,-1.0]])],"derivedFrom":subQ1}),-1.0]])]});}
            var Q46;
            {var subQ0=sQuery(id+"F25.wireOp",EDGE,"E271.trimOffspring");var subQ1=sQuery(id+"F25.wireOp",EDGE,"E243.left");var subQ2=makeQuery(id+"F25.imprint","INTERSECT",VERTEX,{"derivedFrom":[subQ1,subQ0]});Q46=makeQuery(id+"F25.imprint","IMPRINT",FACE,{"disambiguationData":[TD([[makeQuery(id+"F25.imprint","IMPRINT",EDGE,{"disambiguationData":[TD([[subQ2,-1.0]])],"derivedFrom":subQ1}),-1.0]])]});}
            var Q47;
            {var subQ0=sQuery(id+"F25.wireOp",EDGE,"E270.trimOffspring");var subQ1=sQuery(id+"F25.wireOp",EDGE,"E243.left");var subQ2=makeQuery(id+"F25.imprint","INTERSECT",VERTEX,{"derivedFrom":[subQ1,subQ0]});Q47=makeQuery(id+"F25.imprint","IMPRINT",FACE,{"disambiguationData":[TD([[makeQuery(id+"F25.imprint","IMPRINT",EDGE,{"disambiguationData":[TD([[subQ2,-1.0]])],"derivedFrom":subQ1}),-1.0]])]});}
            var Q48;
            {var subQ0=sQuery(id+"F25.wireOp",EDGE,"E274.trimOffspring");var subQ1=sQuery(id+"F25.wireOp",EDGE,"E243.left");var subQ2=makeQuery(id+"F25.imprint","INTERSECT",VERTEX,{"derivedFrom":[subQ1,subQ0]});Q48=makeQuery(id+"F25.imprint","IMPRINT",FACE,{"disambiguationData":[TD([[makeQuery(id+"F25.imprint","IMPRINT",EDGE,{"disambiguationData":[TD([[subQ2,-1.0]])],"derivedFrom":subQ1}),-1.0]])]});}
            var Q49;
            {var subQ0=sQuery(id+"F25.wireOp",EDGE,"E269.trimOffspring");var subQ1=sQuery(id+"F25.wireOp",EDGE,"E243.left");var subQ2=makeQuery(id+"F25.imprint","INTERSECT",VERTEX,{"derivedFrom":[subQ1,subQ0]});Q49=makeQuery(id+"F25.imprint","IMPRINT",FACE,{"disambiguationData":[TD([[makeQuery(id+"F25.imprint","IMPRINT",EDGE,{"disambiguationData":[TD([[subQ2,-1.0]])],"derivedFrom":subQ1}),-1.0]])]});}
            var Q50;
            {var subQ0=sQuery(id+"F25.wireOp",EDGE,"E274.trimOffspring");var subQ1=sQuery(id+"F25.wireOp",EDGE,"E244.right");var subQ2=makeQuery(id+"F25.imprint","INTERSECT",VERTEX,{"derivedFrom":[subQ1,subQ0]});Q50=makeQuery(id+"F25.imprint","IMPRINT",FACE,{"disambiguationData":[TD([[makeQuery(id+"F25.imprint","IMPRINT",EDGE,{"disambiguationData":[TD([[subQ2,-1.0]])],"derivedFrom":subQ1}),-1.0]])]});}
            var Q51;
            {var subQ0=sQuery(id+"F25.wireOp",EDGE,"E270.trimOffspring");var subQ1=sQuery(id+"F25.wireOp",EDGE,"E244.right");var subQ2=makeQuery(id+"F25.imprint","INTERSECT",VERTEX,{"derivedFrom":[subQ1,subQ0]});Q51=makeQuery(id+"F25.imprint","IMPRINT",FACE,{"disambiguationData":[TD([[makeQuery(id+"F25.imprint","IMPRINT",EDGE,{"disambiguationData":[TD([[subQ2,-1.0]])],"derivedFrom":subQ1}),-1.0]])]});}
            var Q52;
            {var subQ0=sQuery(id+"F25.wireOp",EDGE,"E274.trimOffspring");var subQ1=sQuery(id+"F25.wireOp",EDGE,"E245.right");var subQ2=makeQuery(id+"F25.imprint","INTERSECT",VERTEX,{"derivedFrom":[subQ1,subQ0]});Q52=makeQuery(id+"F25.imprint","IMPRINT",FACE,{"disambiguationData":[TD([[makeQuery(id+"F25.imprint","IMPRINT",EDGE,{"disambiguationData":[TD([[subQ2,-1.0]])],"derivedFrom":subQ1}),-1.0]])]});}
            var Q53;
            {var subQ0=sQuery(id+"F25.wireOp",EDGE,"E270.trimOffspring");var subQ1=sQuery(id+"F25.wireOp",EDGE,"E245.right");var subQ2=makeQuery(id+"F25.imprint","INTERSECT",VERTEX,{"derivedFrom":[subQ1,subQ0]});Q53=makeQuery(id+"F25.imprint","IMPRINT",FACE,{"disambiguationData":[TD([[makeQuery(id+"F25.imprint","IMPRINT",EDGE,{"disambiguationData":[TD([[subQ2,-1.0]])],"derivedFrom":subQ1}),-1.0]])]});}
            var Q54;
            {var subQ0=sQuery(id+"F25.wireOp",EDGE,"E274.trimOffspring");var subQ1=sQuery(id+"F25.wireOp",EDGE,"E245.left");var subQ2=makeQuery(id+"F25.imprint","INTERSECT",VERTEX,{"derivedFrom":[subQ1,subQ0]});Q54=makeQuery(id+"F25.imprint","IMPRINT",FACE,{"disambiguationData":[TD([[makeQuery(id+"F25.imprint","IMPRINT",EDGE,{"disambiguationData":[TD([[subQ2,-1.0]])],"derivedFrom":subQ1}),-1.0]])]});}
            var Q55;
            {var subQ0=sQuery(id+"F25.wireOp",EDGE,"E270.trimOffspring");var subQ1=sQuery(id+"F25.wireOp",EDGE,"E245.left");var subQ2=makeQuery(id+"F25.imprint","INTERSECT",VERTEX,{"derivedFrom":[subQ1,subQ0]});Q55=makeQuery(id+"F25.imprint","IMPRINT",FACE,{"disambiguationData":[TD([[makeQuery(id+"F25.imprint","IMPRINT",EDGE,{"disambiguationData":[TD([[subQ2,-1.0]])],"derivedFrom":subQ1}),-1.0]])]});}
            var Q56;
            {var subQ0=sQuery(id+"F25.wireOp",EDGE,"E274.trimOffspring");var subQ1=sQuery(id+"F25.wireOp",EDGE,"E246.right");var subQ2=makeQuery(id+"F25.imprint","INTERSECT",VERTEX,{"derivedFrom":[subQ1,subQ0]});Q56=makeQuery(id+"F25.imprint","IMPRINT",FACE,{"disambiguationData":[TD([[makeQuery(id+"F25.imprint","IMPRINT",EDGE,{"disambiguationData":[TD([[subQ2,-1.0]])],"derivedFrom":subQ1}),-1.0]])]});}
            var Q57;
            {var subQ0=sQuery(id+"F25.wireOp",EDGE,"E270.trimOffspring");var subQ1=sQuery(id+"F25.wireOp",EDGE,"E246.right");var subQ2=makeQuery(id+"F25.imprint","INTERSECT",VERTEX,{"derivedFrom":[subQ1,subQ0]});Q57=makeQuery(id+"F25.imprint","IMPRINT",FACE,{"disambiguationData":[TD([[makeQuery(id+"F25.imprint","IMPRINT",EDGE,{"disambiguationData":[TD([[subQ2,-1.0]])],"derivedFrom":subQ1}),-1.0]])]});}
            var Q58;
            {var subQ0=sQuery(id+"F25.wireOp",EDGE,"E270.trimOffspring");var subQ1=sQuery(id+"F25.wireOp",EDGE,"E248.left");var subQ2=makeQuery(id+"F25.imprint","INTERSECT",VERTEX,{"derivedFrom":[subQ1,subQ0]});Q58=makeQuery(id+"F25.imprint","IMPRINT",FACE,{"disambiguationData":[TD([[makeQuery(id+"F25.imprint","IMPRINT",EDGE,{"disambiguationData":[TD([[subQ2,-1.0]])],"derivedFrom":subQ1}),-1.0]])]});}
            var Q59;
            {var subQ0=sQuery(id+"F25.wireOp",EDGE,"E274.trimOffspring");var subQ1=sQuery(id+"F25.wireOp",EDGE,"E248.left");var subQ2=makeQuery(id+"F25.imprint","INTERSECT",VERTEX,{"derivedFrom":[subQ1,subQ0]});Q59=makeQuery(id+"F25.imprint","IMPRINT",FACE,{"disambiguationData":[TD([[makeQuery(id+"F25.imprint","IMPRINT",EDGE,{"disambiguationData":[TD([[subQ2,-1.0]])],"derivedFrom":subQ1}),-1.0]])]});}
            var Q60;
            {var subQ0=sQuery(id+"F25.wireOp",EDGE,"E244.bottom");Q60=makeQuery(id+"F25.imprint","IMPRINT",FACE,{"disambiguationData":[TD([[makeQuery(id+"F25.imprint","IMPRINT",EDGE,{"derivedFrom":subQ0}),1.0]])]});}
            var Q61;
            {var subQ0=sQuery(id+"F25.wireOp",EDGE,"E267.trimOffspring");var subQ1=sQuery(id+"F25.wireOp",EDGE,"E243.left");var subQ2=makeQuery(id+"F25.imprint","INTERSECT",VERTEX,{"derivedFrom":[subQ1,subQ0]});Q61=makeQuery(id+"F25.imprint","IMPRINT",FACE,{"disambiguationData":[TD([[makeQuery(id+"F25.imprint","IMPRINT",EDGE,{"disambiguationData":[TD([[subQ2,-1.0]])],"derivedFrom":subQ1}),-1.0]])]});}
            var Q62;
            {var subQ0=sQuery(id+"F25.wireOp",EDGE,"E267.trimOffspring");var subQ1=sQuery(id+"F25.wireOp",EDGE,"E244.right");var subQ2=makeQuery(id+"F25.imprint","INTERSECT",VERTEX,{"derivedFrom":[subQ1,subQ0]});Q62=makeQuery(id+"F25.imprint","IMPRINT",FACE,{"disambiguationData":[TD([[makeQuery(id+"F25.imprint","IMPRINT",EDGE,{"disambiguationData":[TD([[subQ2,-1.0]])],"derivedFrom":subQ1}),-1.0]])]});}
            var Q63;
            {var subQ0=sQuery(id+"F25.wireOp",EDGE,"E267.trimOffspring");var subQ1=sQuery(id+"F25.wireOp",EDGE,"E245.right");var subQ2=makeQuery(id+"F25.imprint","INTERSECT",VERTEX,{"derivedFrom":[subQ1,subQ0]});Q63=makeQuery(id+"F25.imprint","IMPRINT",FACE,{"disambiguationData":[TD([[makeQuery(id+"F25.imprint","IMPRINT",EDGE,{"disambiguationData":[TD([[subQ2,-1.0]])],"derivedFrom":subQ1}),-1.0]])]});}
            var Q64;
            {var subQ0=sQuery(id+"F25.wireOp",EDGE,"E267.trimOffspring");var subQ1=sQuery(id+"F25.wireOp",EDGE,"E245.left");var subQ2=makeQuery(id+"F25.imprint","INTERSECT",VERTEX,{"derivedFrom":[subQ1,subQ0]});Q64=makeQuery(id+"F25.imprint","IMPRINT",FACE,{"disambiguationData":[TD([[makeQuery(id+"F25.imprint","IMPRINT",EDGE,{"disambiguationData":[TD([[subQ2,-1.0]])],"derivedFrom":subQ1}),-1.0]])]});}
            var Q65;
            {var subQ0=sQuery(id+"F25.wireOp",EDGE,"E267.trimOffspring");var subQ1=sQuery(id+"F25.wireOp",EDGE,"E246.right");var subQ2=makeQuery(id+"F25.imprint","INTERSECT",VERTEX,{"derivedFrom":[subQ1,subQ0]});Q65=makeQuery(id+"F25.imprint","IMPRINT",FACE,{"disambiguationData":[TD([[makeQuery(id+"F25.imprint","IMPRINT",EDGE,{"disambiguationData":[TD([[subQ2,-1.0]])],"derivedFrom":subQ1}),-1.0]])]});}
            var Q66;
            {var subQ0=sQuery(id+"F25.wireOp",EDGE,"E267.trimOffspring");var subQ1=sQuery(id+"F25.wireOp",EDGE,"E248.left");var subQ2=makeQuery(id+"F25.imprint","INTERSECT",VERTEX,{"derivedFrom":[subQ1,subQ0]});Q66=makeQuery(id+"F25.imprint","IMPRINT",FACE,{"disambiguationData":[TD([[makeQuery(id+"F25.imprint","IMPRINT",EDGE,{"disambiguationData":[TD([[subQ2,-1.0]])],"derivedFrom":subQ1}),1.0]])]});}
            var Q67;
            {var subQ0=sQuery(id+"F25.wireOp",EDGE,"E267.trimOffspring");var subQ1=sQuery(id+"F25.wireOp",EDGE,"E248.left");var subQ2=makeQuery(id+"F25.imprint","INTERSECT",VERTEX,{"derivedFrom":[subQ1,subQ0]});Q67=makeQuery(id+"F25.imprint","IMPRINT",FACE,{"disambiguationData":[TD([[makeQuery(id+"F25.imprint","IMPRINT",EDGE,{"disambiguationData":[TD([[subQ2,-1.0]])],"derivedFrom":subQ1}),-1.0]])]});}
            var Q68;
            {var subQ0=sQuery(id+"F25.wireOp",EDGE,"E268.trimOffspring");var subQ1=sQuery(id+"F25.wireOp",EDGE,"E248.left");var subQ2=makeQuery(id+"F25.imprint","INTERSECT",VERTEX,{"derivedFrom":[subQ1,subQ0]});Q68=makeQuery(id+"F25.imprint","IMPRINT",FACE,{"disambiguationData":[TD([[makeQuery(id+"F25.imprint","IMPRINT",EDGE,{"disambiguationData":[TD([[subQ2,-1.0]])],"derivedFrom":subQ1}),-1.0]])]});}
            var Q69;
            {var subQ0=sQuery(id+"F25.wireOp",EDGE,"E535.trimOffspring");var subQ1=sQuery(id+"F25.wireOp",EDGE,"E510.trimOffspring");var subQ2=makeQuery(id+"F25.imprint","INTERSECT",VERTEX,{"derivedFrom":[subQ1,subQ0]});Q69=makeQuery(id+"F25.imprint","IMPRINT",FACE,{"disambiguationData":[TD([[makeQuery(id+"F25.imprint","IMPRINT",EDGE,{"disambiguationData":[TD([[subQ2,-1.0]])],"derivedFrom":subQ1}),1.0]])]});}
            var Q70;
            {var subQ0=sQuery(id+"F25.wireOp",EDGE,"E520.trimOffspring");var subQ1=sQuery(id+"F25.wireOp",EDGE,"E510.trimOffspring");var subQ2=makeQuery(id+"F25.imprint","INTERSECT",VERTEX,{"derivedFrom":[subQ1,subQ0]});Q70=makeQuery(id+"F25.imprint","IMPRINT",FACE,{"disambiguationData":[TD([[makeQuery(id+"F25.imprint","IMPRINT",EDGE,{"disambiguationData":[TD([[subQ2,-1.0]])],"derivedFrom":subQ1}),1.0]])]});}
            var Q71;
            {var subQ0=sQuery(id+"F25.wireOp",EDGE,"E535.trimOffspring");var subQ1=sQuery(id+"F25.wireOp",EDGE,"E522.trimOffspring");var subQ2=makeQuery(id+"F25.imprint","INTERSECT",VERTEX,{"derivedFrom":[subQ1,subQ0]});Q71=makeQuery(id+"F25.imprint","IMPRINT",FACE,{"disambiguationData":[TD([[makeQuery(id+"F25.imprint","IMPRINT",EDGE,{"disambiguationData":[TD([[subQ2,-1.0]])],"derivedFrom":subQ1}),1.0]])]});}
            var Q72;
            {var subQ1=sQuery(id+"F25.wireOp",EDGE,"E522.trimOffspring");var subQ3=sQuery(id+"F25.wireOp",EDGE,"E520.trimOffspring");var subQ4=makeQuery(id+"F25.imprint","INTERSECT",VERTEX,{"derivedFrom":[subQ1,subQ3]});Q72=makeQuery(id+"F25.imprint","IMPRINT",FACE,{"disambiguationData":[TD([[makeQuery(id+"F25.imprint","IMPRINT",EDGE,{"disambiguationData":[TD([[subQ4,-1.0]])],"derivedFrom":subQ3}),-1.0]])]});}
            var Q73;
            {var subQ0=sQuery(id+"F25.wireOp",EDGE,"E537.MirrorCS");var subQ1=sQuery(id+"F25.wireOp",EDGE,"E520.trimOffspring");var subQ2=makeQuery(id+"F25.imprint","INTERSECT",VERTEX,{"derivedFrom":[subQ1,subQ0]});Q73=makeQuery(id+"F25.imprint","IMPRINT",FACE,{"disambiguationData":[TD([[makeQuery(id+"F25.imprint","IMPRINT",EDGE,{"disambiguationData":[TD([[subQ2,1.0]])],"derivedFrom":subQ1}),1.0]])]});}
            var Q74;
            {var subQ0=sQuery(id+"F25.wireOp",EDGE,"E537.MirrorCS");var subQ1=sQuery(id+"F25.wireOp",EDGE,"E520.trimOffspring");var subQ2=makeQuery(id+"F25.imprint","INTERSECT",VERTEX,{"derivedFrom":[subQ1,subQ0]});Q74=makeQuery(id+"F25.imprint","IMPRINT",FACE,{"disambiguationData":[TD([[makeQuery(id+"F25.imprint","IMPRINT",EDGE,{"disambiguationData":[TD([[subQ2,1.0]])],"derivedFrom":subQ1}),-1.0]])]});}
            var Q75;
            {var subQ0=sQuery(id+"F25.wireOp",EDGE,"E522.trimOffspring");var subQ1=sQuery(id+"F25.wireOp",EDGE,"E276.trimOffspring");var subQ2=makeQuery(id+"F25.imprint","INTERSECT",VERTEX,{"derivedFrom":[subQ1,subQ0]});Q75=makeQuery(id+"F25.imprint","IMPRINT",FACE,{"disambiguationData":[TD([[makeQuery(id+"F25.imprint","IMPRINT",EDGE,{"disambiguationData":[TD([[subQ2,-1.0]])],"derivedFrom":subQ1}),1.0]])]});}
            var Q76;
            {var subQ0=sQuery(id+"F25.wireOp",EDGE,"E525.trimOffspring");var subQ1=sQuery(id+"F25.wireOp",EDGE,"E276.trimOffspring");var subQ2=makeQuery(id+"F25.imprint","INTERSECT",VERTEX,{"derivedFrom":[subQ1,subQ0]});Q76=makeQuery(id+"F25.imprint","IMPRINT",FACE,{"disambiguationData":[TD([[makeQuery(id+"F25.imprint","IMPRINT",EDGE,{"disambiguationData":[TD([[subQ2,1.0]])],"derivedFrom":subQ1}),1.0]])]});}
            var Q77;
            {var subQ0=sQuery(id+"F25.wireOp",EDGE,"E517.trimOffspring");var subQ1=sQuery(id+"F25.wireOp",EDGE,"E276.trimOffspring");var subQ2=makeQuery(id+"F25.imprint","INTERSECT",VERTEX,{"derivedFrom":[subQ1,subQ0]});Q77=makeQuery(id+"F25.imprint","IMPRINT",FACE,{"disambiguationData":[TD([[makeQuery(id+"F25.imprint","IMPRINT",EDGE,{"disambiguationData":[TD([[subQ2,-1.0]])],"derivedFrom":subQ1}),-1.0]])]});}
            var Q78;
            {var subQ0=sQuery(id+"F25.wireOp",EDGE,"E517.trimOffspring");var subQ1=sQuery(id+"F25.wireOp",EDGE,"E277.trimOffspring");var subQ2=makeQuery(id+"F25.imprint","INTERSECT",VERTEX,{"derivedFrom":[subQ1,subQ0]});Q78=makeQuery(id+"F25.imprint","IMPRINT",FACE,{"disambiguationData":[TD([[makeQuery(id+"F25.imprint","IMPRINT",EDGE,{"disambiguationData":[TD([[subQ2,-1.0]])],"derivedFrom":subQ1}),-1.0]])]});}
            var Q79;
            {var subQ0=sQuery(id+"F25.wireOp",EDGE,"E519.trimOffspring");var subQ1=sQuery(id+"F25.wireOp",EDGE,"E277.trimOffspring");var subQ2=makeQuery(id+"F25.imprint","INTERSECT",VERTEX,{"derivedFrom":[subQ1,subQ0]});Q79=makeQuery(id+"F25.imprint","IMPRINT",FACE,{"disambiguationData":[TD([[makeQuery(id+"F25.imprint","IMPRINT",EDGE,{"disambiguationData":[TD([[subQ2,-1.0]])],"derivedFrom":subQ1}),-1.0]])]});}
            var Q80;
            {var subQ0=sQuery(id+"F25.wireOp",EDGE,"E519.trimOffspring");var subQ1=sQuery(id+"F25.wireOp",EDGE,"E276.trimOffspring");var subQ2=makeQuery(id+"F25.imprint","INTERSECT",VERTEX,{"derivedFrom":[subQ1,subQ0]});Q80=makeQuery(id+"F25.imprint","IMPRINT",FACE,{"disambiguationData":[TD([[makeQuery(id+"F25.imprint","IMPRINT",EDGE,{"disambiguationData":[TD([[subQ2,-1.0]])],"derivedFrom":subQ1}),-1.0]])]});}
            var Q81;
            {var subQ0=sQuery(id+"F25.wireOp",EDGE,"E518.trimOffspring");var subQ1=sQuery(id+"F25.wireOp",EDGE,"E276.trimOffspring");var subQ2=makeQuery(id+"F25.imprint","INTERSECT",VERTEX,{"derivedFrom":[subQ1,subQ0]});Q81=makeQuery(id+"F25.imprint","IMPRINT",FACE,{"disambiguationData":[TD([[makeQuery(id+"F25.imprint","IMPRINT",EDGE,{"disambiguationData":[TD([[subQ2,-1.0]])],"derivedFrom":subQ1}),-1.0]])]});}
            var Q82;
            {var subQ0=sQuery(id+"F25.wireOp",EDGE,"E518.trimOffspring");var subQ1=sQuery(id+"F25.wireOp",EDGE,"E277.trimOffspring");var subQ2=makeQuery(id+"F25.imprint","INTERSECT",VERTEX,{"derivedFrom":[subQ1,subQ0]});Q82=makeQuery(id+"F25.imprint","IMPRINT",FACE,{"disambiguationData":[TD([[makeQuery(id+"F25.imprint","IMPRINT",EDGE,{"disambiguationData":[TD([[subQ2,-1.0]])],"derivedFrom":subQ1}),-1.0]])]});}
            var Q83;
            {var subQ0=sQuery(id+"F25.wireOp",EDGE,"E507.trimOffspring");var subQ1=sQuery(id+"F25.wireOp",EDGE,"E276.trimOffspring");var subQ2=makeQuery(id+"F25.imprint","INTERSECT",VERTEX,{"derivedFrom":[subQ1,subQ0]});Q83=makeQuery(id+"F25.imprint","IMPRINT",FACE,{"disambiguationData":[TD([[makeQuery(id+"F25.imprint","IMPRINT",EDGE,{"disambiguationData":[TD([[subQ2,-1.0]])],"derivedFrom":subQ1}),-1.0]])]});}
            var Q84;
            {var subQ0=sQuery(id+"F25.wireOp",EDGE,"E507.trimOffspring");var subQ1=sQuery(id+"F25.wireOp",EDGE,"E277.trimOffspring");var subQ2=makeQuery(id+"F25.imprint","INTERSECT",VERTEX,{"derivedFrom":[subQ1,subQ0]});Q84=makeQuery(id+"F25.imprint","IMPRINT",FACE,{"disambiguationData":[TD([[makeQuery(id+"F25.imprint","IMPRINT",EDGE,{"disambiguationData":[TD([[subQ2,-1.0]])],"derivedFrom":subQ1}),-1.0]])]});}
            var Q85;
            {var subQ0=sQuery(id+"F25.wireOp",EDGE,"E512.trimOffspring");var subQ1=sQuery(id+"F25.wireOp",EDGE,"E276.trimOffspring");var subQ2=makeQuery(id+"F25.imprint","INTERSECT",VERTEX,{"derivedFrom":[subQ1,subQ0]});Q85=makeQuery(id+"F25.imprint","IMPRINT",FACE,{"disambiguationData":[TD([[makeQuery(id+"F25.imprint","IMPRINT",EDGE,{"disambiguationData":[TD([[subQ2,-1.0]])],"derivedFrom":subQ1}),-1.0]])]});}
            var Q86;
            {var subQ0=sQuery(id+"F25.wireOp",EDGE,"E512.trimOffspring");var subQ1=sQuery(id+"F25.wireOp",EDGE,"E277.trimOffspring");var subQ2=makeQuery(id+"F25.imprint","INTERSECT",VERTEX,{"derivedFrom":[subQ1,subQ0]});Q86=makeQuery(id+"F25.imprint","IMPRINT",FACE,{"disambiguationData":[TD([[makeQuery(id+"F25.imprint","IMPRINT",EDGE,{"disambiguationData":[TD([[subQ2,-1.0]])],"derivedFrom":subQ1}),-1.0]])]});}
            var Q87;
            {var subQ0=sQuery(id+"F25.wireOp",EDGE,"E510.trimOffspring");var subQ1=sQuery(id+"F25.wireOp",EDGE,"E277.trimOffspring");var subQ2=makeQuery(id+"F25.imprint","INTERSECT",VERTEX,{"derivedFrom":[subQ1,subQ0]});Q87=makeQuery(id+"F25.imprint","IMPRINT",FACE,{"disambiguationData":[TD([[makeQuery(id+"F25.imprint","IMPRINT",EDGE,{"disambiguationData":[TD([[subQ2,-1.0]])],"derivedFrom":subQ1}),-1.0]])]});}
            var Q88;
            {var subQ0=sQuery(id+"F25.wireOp",EDGE,"E510.trimOffspring");var subQ1=sQuery(id+"F25.wireOp",EDGE,"E276.trimOffspring");var subQ2=makeQuery(id+"F25.imprint","INTERSECT",VERTEX,{"derivedFrom":[subQ1,subQ0]});Q88=makeQuery(id+"F25.imprint","IMPRINT",FACE,{"disambiguationData":[TD([[makeQuery(id+"F25.imprint","IMPRINT",EDGE,{"disambiguationData":[TD([[subQ2,-1.0]])],"derivedFrom":subQ1}),-1.0]])]});}
            var Q89;
            {var subQ0=sQuery(id+"F25.wireOp",EDGE,"E522.trimOffspring");var subQ1=sQuery(id+"F25.wireOp",EDGE,"E276.trimOffspring");var subQ2=makeQuery(id+"F25.imprint","INTERSECT",VERTEX,{"derivedFrom":[subQ1,subQ0]});Q89=makeQuery(id+"F25.imprint","IMPRINT",FACE,{"disambiguationData":[TD([[makeQuery(id+"F25.imprint","IMPRINT",EDGE,{"disambiguationData":[TD([[subQ2,-1.0]])],"derivedFrom":subQ1}),-1.0]])]});}
            var Q90;
            {var subQ0=sQuery(id+"F25.wireOp",EDGE,"E522.trimOffspring");var subQ1=sQuery(id+"F25.wireOp",EDGE,"E277.trimOffspring");var subQ2=makeQuery(id+"F25.imprint","INTERSECT",VERTEX,{"derivedFrom":[subQ1,subQ0]});Q90=makeQuery(id+"F25.imprint","IMPRINT",FACE,{"disambiguationData":[TD([[makeQuery(id+"F25.imprint","IMPRINT",EDGE,{"disambiguationData":[TD([[subQ2,-1.0]])],"derivedFrom":subQ1}),-1.0]])]});}
            var Q91;
            {var subQ0=sQuery(id+"F25.wireOp",EDGE,"E525.trimOffspring");var subQ1=sQuery(id+"F25.wireOp",EDGE,"E277.trimOffspring");var subQ2=makeQuery(id+"F25.imprint","INTERSECT",VERTEX,{"derivedFrom":[subQ1,subQ0]});Q91=makeQuery(id+"F25.imprint","IMPRINT",FACE,{"disambiguationData":[TD([[makeQuery(id+"F25.imprint","IMPRINT",EDGE,{"disambiguationData":[TD([[subQ2,1.0]])],"derivedFrom":subQ1}),-1.0]])]});}
            var Q92;
            {var subQ0=sQuery(id+"F25.wireOp",EDGE,"E525.trimOffspring");var subQ1=sQuery(id+"F25.wireOp",EDGE,"E276.trimOffspring");var subQ2=makeQuery(id+"F25.imprint","INTERSECT",VERTEX,{"derivedFrom":[subQ1,subQ0]});Q92=makeQuery(id+"F25.imprint","IMPRINT",FACE,{"disambiguationData":[TD([[makeQuery(id+"F25.imprint","IMPRINT",EDGE,{"disambiguationData":[TD([[subQ2,1.0]])],"derivedFrom":subQ1}),-1.0]])]});}
            var Q93;
            {var subQ0=sQuery(id+"F25.wireOp",EDGE,"E525.trimOffspring");var subQ1=sQuery(id+"F25.wireOp",EDGE,"E280.trimOffspring");var subQ2=makeQuery(id+"F25.imprint","INTERSECT",VERTEX,{"derivedFrom":[subQ1,subQ0]});Q93=makeQuery(id+"F25.imprint","IMPRINT",FACE,{"disambiguationData":[TD([[makeQuery(id+"F25.imprint","IMPRINT",EDGE,{"disambiguationData":[TD([[subQ2,1.0]])],"derivedFrom":subQ1}),-1.0]])]});}
            var Q94;
            {var subQ0=sQuery(id+"F25.wireOp",EDGE,"E525.trimOffspring");var subQ1=sQuery(id+"F25.wireOp",EDGE,"E279.trimOffspring");var subQ2=makeQuery(id+"F25.imprint","INTERSECT",VERTEX,{"derivedFrom":[subQ1,subQ0]});Q94=makeQuery(id+"F25.imprint","IMPRINT",FACE,{"disambiguationData":[TD([[makeQuery(id+"F25.imprint","IMPRINT",EDGE,{"disambiguationData":[TD([[subQ2,1.0]])],"derivedFrom":subQ1}),1.0]])]});}
            var Q95;
            {var subQ0=sQuery(id+"F25.wireOp",EDGE,"E522.trimOffspring");var subQ1=sQuery(id+"F25.wireOp",EDGE,"E280.trimOffspring");var subQ2=makeQuery(id+"F25.imprint","INTERSECT",VERTEX,{"derivedFrom":[subQ1,subQ0]});Q95=makeQuery(id+"F25.imprint","IMPRINT",FACE,{"disambiguationData":[TD([[makeQuery(id+"F25.imprint","IMPRINT",EDGE,{"disambiguationData":[TD([[subQ2,-1.0]])],"derivedFrom":subQ1}),-1.0]])]});}
            var Q96;
            {var subQ0=sQuery(id+"F25.wireOp",EDGE,"E510.trimOffspring");var subQ1=sQuery(id+"F25.wireOp",EDGE,"E280.trimOffspring");var subQ2=makeQuery(id+"F25.imprint","INTERSECT",VERTEX,{"derivedFrom":[subQ1,subQ0]});Q96=makeQuery(id+"F25.imprint","IMPRINT",FACE,{"disambiguationData":[TD([[makeQuery(id+"F25.imprint","IMPRINT",EDGE,{"disambiguationData":[TD([[subQ2,-1.0]])],"derivedFrom":subQ1}),-1.0]])]});}
            var Q97;
            {var subQ0=sQuery(id+"F25.wireOp",EDGE,"E510.trimOffspring");var subQ1=sQuery(id+"F25.wireOp",EDGE,"E279.trimOffspring");var subQ2=makeQuery(id+"F25.imprint","INTERSECT",VERTEX,{"derivedFrom":[subQ1,subQ0]});Q97=makeQuery(id+"F25.imprint","IMPRINT",FACE,{"disambiguationData":[TD([[makeQuery(id+"F25.imprint","IMPRINT",EDGE,{"disambiguationData":[TD([[subQ2,-1.0]])],"derivedFrom":subQ1}),1.0]])]});}
            var Q98;
            {var subQ0=sQuery(id+"F25.wireOp",EDGE,"E517.trimOffspring");var subQ1=sQuery(id+"F25.wireOp",EDGE,"E280.trimOffspring");var subQ2=makeQuery(id+"F25.imprint","INTERSECT",VERTEX,{"derivedFrom":[subQ1,subQ0]});Q98=makeQuery(id+"F25.imprint","IMPRINT",FACE,{"disambiguationData":[TD([[makeQuery(id+"F25.imprint","IMPRINT",EDGE,{"disambiguationData":[TD([[subQ2,-1.0]])],"derivedFrom":subQ1}),-1.0]])]});}
            var Q99;
            {var subQ0=sQuery(id+"F25.wireOp",EDGE,"E517.trimOffspring");var subQ1=sQuery(id+"F25.wireOp",EDGE,"E279.trimOffspring");var subQ2=makeQuery(id+"F25.imprint","INTERSECT",VERTEX,{"derivedFrom":[subQ1,subQ0]});Q99=makeQuery(id+"F25.imprint","IMPRINT",FACE,{"disambiguationData":[TD([[makeQuery(id+"F25.imprint","IMPRINT",EDGE,{"disambiguationData":[TD([[subQ2,-1.0]])],"derivedFrom":subQ1}),1.0]])]});}
            var Q100;
            {var subQ0=sQuery(id+"F25.wireOp",EDGE,"E519.trimOffspring");var subQ1=sQuery(id+"F25.wireOp",EDGE,"E279.trimOffspring");var subQ2=makeQuery(id+"F25.imprint","INTERSECT",VERTEX,{"derivedFrom":[subQ1,subQ0]});Q100=makeQuery(id+"F25.imprint","IMPRINT",FACE,{"disambiguationData":[TD([[makeQuery(id+"F25.imprint","IMPRINT",EDGE,{"disambiguationData":[TD([[subQ2,-1.0]])],"derivedFrom":subQ1}),1.0]])]});}
            var Q101;
            {var subQ0=sQuery(id+"F25.wireOp",EDGE,"E519.trimOffspring");var subQ1=sQuery(id+"F25.wireOp",EDGE,"E280.trimOffspring");var subQ2=makeQuery(id+"F25.imprint","INTERSECT",VERTEX,{"derivedFrom":[subQ1,subQ0]});Q101=makeQuery(id+"F25.imprint","IMPRINT",FACE,{"disambiguationData":[TD([[makeQuery(id+"F25.imprint","IMPRINT",EDGE,{"disambiguationData":[TD([[subQ2,-1.0]])],"derivedFrom":subQ1}),-1.0]])]});}
            var Q102;
            {var subQ0=sQuery(id+"F25.wireOp",EDGE,"E518.trimOffspring");var subQ1=sQuery(id+"F25.wireOp",EDGE,"E280.trimOffspring");var subQ2=makeQuery(id+"F25.imprint","INTERSECT",VERTEX,{"derivedFrom":[subQ1,subQ0]});Q102=makeQuery(id+"F25.imprint","IMPRINT",FACE,{"disambiguationData":[TD([[makeQuery(id+"F25.imprint","IMPRINT",EDGE,{"disambiguationData":[TD([[subQ2,-1.0]])],"derivedFrom":subQ1}),-1.0]])]});}
            var Q103;
            {var subQ0=sQuery(id+"F25.wireOp",EDGE,"E518.trimOffspring");var subQ1=sQuery(id+"F25.wireOp",EDGE,"E279.trimOffspring");var subQ2=makeQuery(id+"F25.imprint","INTERSECT",VERTEX,{"derivedFrom":[subQ1,subQ0]});Q103=makeQuery(id+"F25.imprint","IMPRINT",FACE,{"disambiguationData":[TD([[makeQuery(id+"F25.imprint","IMPRINT",EDGE,{"disambiguationData":[TD([[subQ2,-1.0]])],"derivedFrom":subQ1}),1.0]])]});}
            var Q104;
            {var subQ0=sQuery(id+"F25.wireOp",EDGE,"E507.trimOffspring");var subQ1=sQuery(id+"F25.wireOp",EDGE,"E280.trimOffspring");var subQ2=makeQuery(id+"F25.imprint","INTERSECT",VERTEX,{"derivedFrom":[subQ1,subQ0]});Q104=makeQuery(id+"F25.imprint","IMPRINT",FACE,{"disambiguationData":[TD([[makeQuery(id+"F25.imprint","IMPRINT",EDGE,{"disambiguationData":[TD([[subQ2,-1.0]])],"derivedFrom":subQ1}),-1.0]])]});}
            var Q105;
            {var subQ0=sQuery(id+"F25.wireOp",EDGE,"E507.trimOffspring");var subQ1=sQuery(id+"F25.wireOp",EDGE,"E279.trimOffspring");var subQ2=makeQuery(id+"F25.imprint","INTERSECT",VERTEX,{"derivedFrom":[subQ1,subQ0]});Q105=makeQuery(id+"F25.imprint","IMPRINT",FACE,{"disambiguationData":[TD([[makeQuery(id+"F25.imprint","IMPRINT",EDGE,{"disambiguationData":[TD([[subQ2,-1.0]])],"derivedFrom":subQ1}),1.0]])]});}
            var Q106;
            {var subQ0=sQuery(id+"F25.wireOp",EDGE,"E512.trimOffspring");var subQ1=sQuery(id+"F25.wireOp",EDGE,"E280.trimOffspring");var subQ2=makeQuery(id+"F25.imprint","INTERSECT",VERTEX,{"derivedFrom":[subQ1,subQ0]});Q106=makeQuery(id+"F25.imprint","IMPRINT",FACE,{"disambiguationData":[TD([[makeQuery(id+"F25.imprint","IMPRINT",EDGE,{"disambiguationData":[TD([[subQ2,-1.0]])],"derivedFrom":subQ1}),-1.0]])]});}
            var Q107;
            {var subQ0=sQuery(id+"F25.wireOp",EDGE,"E512.trimOffspring");var subQ1=sQuery(id+"F25.wireOp",EDGE,"E279.trimOffspring");var subQ2=makeQuery(id+"F25.imprint","INTERSECT",VERTEX,{"derivedFrom":[subQ1,subQ0]});Q107=makeQuery(id+"F25.imprint","IMPRINT",FACE,{"disambiguationData":[TD([[makeQuery(id+"F25.imprint","IMPRINT",EDGE,{"disambiguationData":[TD([[subQ2,-1.0]])],"derivedFrom":subQ1}),1.0]])]});}
            var Q108;
            {var subQ0=sQuery(id+"F25.wireOp",EDGE,"E522.trimOffspring");var subQ1=sQuery(id+"F25.wireOp",EDGE,"E279.trimOffspring");var subQ2=makeQuery(id+"F25.imprint","INTERSECT",VERTEX,{"derivedFrom":[subQ1,subQ0]});Q108=makeQuery(id+"F25.imprint","IMPRINT",FACE,{"disambiguationData":[TD([[makeQuery(id+"F25.imprint","IMPRINT",EDGE,{"disambiguationData":[TD([[subQ2,-1.0]])],"derivedFrom":subQ1}),1.0]])]});}
            var Q109;
            {var subQ0=sQuery(id+"F25.wireOp",EDGE,"E525.trimOffspring");var subQ1=sQuery(id+"F25.wireOp",EDGE,"E287.trimOffspring");var subQ2=makeQuery(id+"F25.imprint","INTERSECT",VERTEX,{"derivedFrom":[subQ1,subQ0]});Q109=makeQuery(id+"F25.imprint","IMPRINT",FACE,{"disambiguationData":[TD([[makeQuery(id+"F25.imprint","IMPRINT",EDGE,{"disambiguationData":[TD([[subQ2,1.0]])],"derivedFrom":subQ1}),-1.0]])]});}
            var Q110;
            {var subQ0=sQuery(id+"F25.wireOp",EDGE,"E525.trimOffspring");var subQ1=sQuery(id+"F25.wireOp",EDGE,"E291.trimOffspring");var subQ2=makeQuery(id+"F25.imprint","INTERSECT",VERTEX,{"derivedFrom":[subQ1,subQ0]});Q110=makeQuery(id+"F25.imprint","IMPRINT",FACE,{"disambiguationData":[TD([[makeQuery(id+"F25.imprint","IMPRINT",EDGE,{"disambiguationData":[TD([[subQ2,1.0]])],"derivedFrom":subQ1}),1.0]])]});}
            var Q111;
            {var subQ0=sQuery(id+"F25.wireOp",EDGE,"E522.trimOffspring");var subQ1=sQuery(id+"F25.wireOp",EDGE,"E287.trimOffspring");var subQ2=makeQuery(id+"F25.imprint","INTERSECT",VERTEX,{"derivedFrom":[subQ1,subQ0]});Q111=makeQuery(id+"F25.imprint","IMPRINT",FACE,{"disambiguationData":[TD([[makeQuery(id+"F25.imprint","IMPRINT",EDGE,{"disambiguationData":[TD([[subQ2,-1.0]])],"derivedFrom":subQ1}),-1.0]])]});}
            var Q112;
            {var subQ0=sQuery(id+"F25.wireOp",EDGE,"E522.trimOffspring");var subQ1=sQuery(id+"F25.wireOp",EDGE,"E291.trimOffspring");var subQ2=makeQuery(id+"F25.imprint","INTERSECT",VERTEX,{"derivedFrom":[subQ1,subQ0]});Q112=makeQuery(id+"F25.imprint","IMPRINT",FACE,{"disambiguationData":[TD([[makeQuery(id+"F25.imprint","IMPRINT",EDGE,{"disambiguationData":[TD([[subQ2,-1.0]])],"derivedFrom":subQ1}),1.0]])]});}
            var Q113;
            {var subQ0=sQuery(id+"F25.wireOp",EDGE,"E510.trimOffspring");var subQ1=sQuery(id+"F25.wireOp",EDGE,"E287.trimOffspring");var subQ2=makeQuery(id+"F25.imprint","INTERSECT",VERTEX,{"derivedFrom":[subQ1,subQ0]});Q113=makeQuery(id+"F25.imprint","IMPRINT",FACE,{"disambiguationData":[TD([[makeQuery(id+"F25.imprint","IMPRINT",EDGE,{"disambiguationData":[TD([[subQ2,-1.0]])],"derivedFrom":subQ1}),-1.0]])]});}
            var Q114;
            {var subQ0=sQuery(id+"F25.wireOp",EDGE,"E510.trimOffspring");var subQ1=sQuery(id+"F25.wireOp",EDGE,"E291.trimOffspring");var subQ2=makeQuery(id+"F25.imprint","INTERSECT",VERTEX,{"derivedFrom":[subQ1,subQ0]});Q114=makeQuery(id+"F25.imprint","IMPRINT",FACE,{"disambiguationData":[TD([[makeQuery(id+"F25.imprint","IMPRINT",EDGE,{"disambiguationData":[TD([[subQ2,-1.0]])],"derivedFrom":subQ1}),1.0]])]});}
            var Q115;
            {var subQ0=sQuery(id+"F25.wireOp",EDGE,"E512.trimOffspring");var subQ1=sQuery(id+"F25.wireOp",EDGE,"E287.trimOffspring");var subQ2=makeQuery(id+"F25.imprint","INTERSECT",VERTEX,{"derivedFrom":[subQ1,subQ0]});Q115=makeQuery(id+"F25.imprint","IMPRINT",FACE,{"disambiguationData":[TD([[makeQuery(id+"F25.imprint","IMPRINT",EDGE,{"disambiguationData":[TD([[subQ2,-1.0]])],"derivedFrom":subQ1}),-1.0]])]});}
            var Q116;
            {var subQ0=sQuery(id+"F25.wireOp",EDGE,"E512.trimOffspring");var subQ1=sQuery(id+"F25.wireOp",EDGE,"E291.trimOffspring");var subQ2=makeQuery(id+"F25.imprint","INTERSECT",VERTEX,{"derivedFrom":[subQ1,subQ0]});Q116=makeQuery(id+"F25.imprint","IMPRINT",FACE,{"disambiguationData":[TD([[makeQuery(id+"F25.imprint","IMPRINT",EDGE,{"disambiguationData":[TD([[subQ2,-1.0]])],"derivedFrom":subQ1}),1.0]])]});}
            var Q117;
            {var subQ0=sQuery(id+"F25.wireOp",EDGE,"E507.trimOffspring");var subQ1=sQuery(id+"F25.wireOp",EDGE,"E291.trimOffspring");var subQ2=makeQuery(id+"F25.imprint","INTERSECT",VERTEX,{"derivedFrom":[subQ1,subQ0]});Q117=makeQuery(id+"F25.imprint","IMPRINT",FACE,{"disambiguationData":[TD([[makeQuery(id+"F25.imprint","IMPRINT",EDGE,{"disambiguationData":[TD([[subQ2,-1.0]])],"derivedFrom":subQ1}),1.0]])]});}
            var Q118;
            {var subQ0=sQuery(id+"F25.wireOp",EDGE,"E507.trimOffspring");var subQ1=sQuery(id+"F25.wireOp",EDGE,"E287.trimOffspring");var subQ2=makeQuery(id+"F25.imprint","INTERSECT",VERTEX,{"derivedFrom":[subQ1,subQ0]});Q118=makeQuery(id+"F25.imprint","IMPRINT",FACE,{"disambiguationData":[TD([[makeQuery(id+"F25.imprint","IMPRINT",EDGE,{"disambiguationData":[TD([[subQ2,-1.0]])],"derivedFrom":subQ1}),-1.0]])]});}
            var Q119;
            {var subQ0=sQuery(id+"F25.wireOp",EDGE,"E518.trimOffspring");var subQ1=sQuery(id+"F25.wireOp",EDGE,"E287.trimOffspring");var subQ2=makeQuery(id+"F25.imprint","INTERSECT",VERTEX,{"derivedFrom":[subQ1,subQ0]});Q119=makeQuery(id+"F25.imprint","IMPRINT",FACE,{"disambiguationData":[TD([[makeQuery(id+"F25.imprint","IMPRINT",EDGE,{"disambiguationData":[TD([[subQ2,-1.0]])],"derivedFrom":subQ1}),-1.0]])]});}
            var Q120;
            {var subQ0=sQuery(id+"F25.wireOp",EDGE,"E518.trimOffspring");var subQ1=sQuery(id+"F25.wireOp",EDGE,"E291.trimOffspring");var subQ2=makeQuery(id+"F25.imprint","INTERSECT",VERTEX,{"derivedFrom":[subQ1,subQ0]});Q120=makeQuery(id+"F25.imprint","IMPRINT",FACE,{"disambiguationData":[TD([[makeQuery(id+"F25.imprint","IMPRINT",EDGE,{"disambiguationData":[TD([[subQ2,-1.0]])],"derivedFrom":subQ1}),1.0]])]});}
            var Q121;
            {var subQ0=sQuery(id+"F25.wireOp",EDGE,"E519.trimOffspring");var subQ1=sQuery(id+"F25.wireOp",EDGE,"E287.trimOffspring");var subQ2=makeQuery(id+"F25.imprint","INTERSECT",VERTEX,{"derivedFrom":[subQ1,subQ0]});Q121=makeQuery(id+"F25.imprint","IMPRINT",FACE,{"disambiguationData":[TD([[makeQuery(id+"F25.imprint","IMPRINT",EDGE,{"disambiguationData":[TD([[subQ2,-1.0]])],"derivedFrom":subQ1}),-1.0]])]});}
            var Q122;
            {var subQ0=sQuery(id+"F25.wireOp",EDGE,"E517.trimOffspring");var subQ1=sQuery(id+"F25.wireOp",EDGE,"E287.trimOffspring");var subQ2=makeQuery(id+"F25.imprint","INTERSECT",VERTEX,{"derivedFrom":[subQ1,subQ0]});Q122=makeQuery(id+"F25.imprint","IMPRINT",FACE,{"disambiguationData":[TD([[makeQuery(id+"F25.imprint","IMPRINT",EDGE,{"disambiguationData":[TD([[subQ2,-1.0]])],"derivedFrom":subQ1}),-1.0]])]});}
            var Q123;
            {var subQ0=sQuery(id+"F25.wireOp",EDGE,"E517.trimOffspring");var subQ1=sQuery(id+"F25.wireOp",EDGE,"E291.trimOffspring");var subQ2=makeQuery(id+"F25.imprint","INTERSECT",VERTEX,{"derivedFrom":[subQ1,subQ0]});Q123=makeQuery(id+"F25.imprint","IMPRINT",FACE,{"disambiguationData":[TD([[makeQuery(id+"F25.imprint","IMPRINT",EDGE,{"disambiguationData":[TD([[subQ2,-1.0]])],"derivedFrom":subQ1}),1.0]])]});}
            var Q124;
            {var subQ0=sQuery(id+"F25.wireOp",EDGE,"E519.trimOffspring");var subQ1=sQuery(id+"F25.wireOp",EDGE,"E291.trimOffspring");var subQ2=makeQuery(id+"F25.imprint","INTERSECT",VERTEX,{"derivedFrom":[subQ1,subQ0]});Q124=makeQuery(id+"F25.imprint","IMPRINT",FACE,{"disambiguationData":[TD([[makeQuery(id+"F25.imprint","IMPRINT",EDGE,{"disambiguationData":[TD([[subQ2,-1.0]])],"derivedFrom":subQ1}),1.0]])]});}
            var Q125;
            {var subQ0=sQuery(id+"F25.wireOp",EDGE,"E517.trimOffspring");var subQ1=sQuery(id+"F25.wireOp",EDGE,"E251.right");var subQ2=makeQuery(id+"F25.imprint","INTERSECT",VERTEX,{"derivedFrom":[subQ1,subQ0]});Q125=makeQuery(id+"F25.imprint","IMPRINT",FACE,{"disambiguationData":[TD([[makeQuery(id+"F25.imprint","IMPRINT",EDGE,{"disambiguationData":[TD([[subQ2,-1.0]])],"derivedFrom":subQ1}),1.0]])]});}
            var Q126;
            {var subQ0=sQuery(id+"F25.wireOp",EDGE,"E519.trimOffspring");var subQ1=sQuery(id+"F25.wireOp",EDGE,"E251.right");var subQ2=makeQuery(id+"F25.imprint","INTERSECT",VERTEX,{"derivedFrom":[subQ1,subQ0]});Q126=makeQuery(id+"F25.imprint","IMPRINT",FACE,{"disambiguationData":[TD([[makeQuery(id+"F25.imprint","IMPRINT",EDGE,{"disambiguationData":[TD([[subQ2,-1.0]])],"derivedFrom":subQ1}),1.0]])]});}
            var Q127;
            {var subQ0=sQuery(id+"F25.wireOp",EDGE,"E519.trimOffspring");var subQ1=sQuery(id+"F25.wireOp",EDGE,"E250.left");var subQ2=makeQuery(id+"F25.imprint","INTERSECT",VERTEX,{"derivedFrom":[subQ1,subQ0]});Q127=makeQuery(id+"F25.imprint","IMPRINT",FACE,{"disambiguationData":[TD([[makeQuery(id+"F25.imprint","IMPRINT",EDGE,{"disambiguationData":[TD([[subQ2,-1.0]])],"derivedFrom":subQ1}),1.0]])]});}
            var Q128;
            {var subQ0=sQuery(id+"F25.wireOp",EDGE,"E517.trimOffspring");var subQ1=sQuery(id+"F25.wireOp",EDGE,"E250.left");var subQ2=makeQuery(id+"F25.imprint","INTERSECT",VERTEX,{"derivedFrom":[subQ1,subQ0]});Q128=makeQuery(id+"F25.imprint","IMPRINT",FACE,{"disambiguationData":[TD([[makeQuery(id+"F25.imprint","IMPRINT",EDGE,{"disambiguationData":[TD([[subQ2,-1.0]])],"derivedFrom":subQ1}),1.0]])]});}
            var Q129;
            {var subQ0=sQuery(id+"F25.wireOp",EDGE,"E517.trimOffspring");var subQ1=sQuery(id+"F25.wireOp",EDGE,"E250.right");var subQ2=makeQuery(id+"F25.imprint","INTERSECT",VERTEX,{"derivedFrom":[subQ1,subQ0]});Q129=makeQuery(id+"F25.imprint","IMPRINT",FACE,{"disambiguationData":[TD([[makeQuery(id+"F25.imprint","IMPRINT",EDGE,{"disambiguationData":[TD([[subQ2,-1.0]])],"derivedFrom":subQ1}),1.0]])]});}
            var Q130;
            {var subQ0=sQuery(id+"F25.wireOp",EDGE,"E519.trimOffspring");var subQ1=sQuery(id+"F25.wireOp",EDGE,"E250.right");var subQ2=makeQuery(id+"F25.imprint","INTERSECT",VERTEX,{"derivedFrom":[subQ1,subQ0]});Q130=makeQuery(id+"F25.imprint","IMPRINT",FACE,{"disambiguationData":[TD([[makeQuery(id+"F25.imprint","IMPRINT",EDGE,{"disambiguationData":[TD([[subQ2,-1.0]])],"derivedFrom":subQ1}),1.0]])]});}
            var Q131;
            {var subQ0=sQuery(id+"F25.wireOp",EDGE,"E518.trimOffspring");var subQ1=sQuery(id+"F25.wireOp",EDGE,"E250.right");var subQ2=makeQuery(id+"F25.imprint","INTERSECT",VERTEX,{"derivedFrom":[subQ1,subQ0]});Q131=makeQuery(id+"F25.imprint","IMPRINT",FACE,{"disambiguationData":[TD([[makeQuery(id+"F25.imprint","IMPRINT",EDGE,{"disambiguationData":[TD([[subQ2,-1.0]])],"derivedFrom":subQ1}),1.0]])]});}
            var Q132;
            {var subQ0=sQuery(id+"F25.wireOp",EDGE,"E518.trimOffspring");var subQ1=sQuery(id+"F25.wireOp",EDGE,"E250.left");var subQ2=makeQuery(id+"F25.imprint","INTERSECT",VERTEX,{"derivedFrom":[subQ1,subQ0]});Q132=makeQuery(id+"F25.imprint","IMPRINT",FACE,{"disambiguationData":[TD([[makeQuery(id+"F25.imprint","IMPRINT",EDGE,{"disambiguationData":[TD([[subQ2,-1.0]])],"derivedFrom":subQ1}),1.0]])]});}
            var Q133;
            {var subQ0=sQuery(id+"F25.wireOp",EDGE,"E507.trimOffspring");var subQ1=sQuery(id+"F25.wireOp",EDGE,"E250.left");var subQ2=makeQuery(id+"F25.imprint","INTERSECT",VERTEX,{"derivedFrom":[subQ1,subQ0]});Q133=makeQuery(id+"F25.imprint","IMPRINT",FACE,{"disambiguationData":[TD([[makeQuery(id+"F25.imprint","IMPRINT",EDGE,{"disambiguationData":[TD([[subQ2,-1.0]])],"derivedFrom":subQ1}),1.0]])]});}
            var Q134;
            {var subQ0=sQuery(id+"F25.wireOp",EDGE,"E507.trimOffspring");var subQ1=sQuery(id+"F25.wireOp",EDGE,"E250.right");var subQ2=makeQuery(id+"F25.imprint","INTERSECT",VERTEX,{"derivedFrom":[subQ1,subQ0]});Q134=makeQuery(id+"F25.imprint","IMPRINT",FACE,{"disambiguationData":[TD([[makeQuery(id+"F25.imprint","IMPRINT",EDGE,{"disambiguationData":[TD([[subQ2,-1.0]])],"derivedFrom":subQ1}),1.0]])]});}
            var Q135;
            {var subQ0=sQuery(id+"F25.wireOp",EDGE,"E512.trimOffspring");var subQ1=sQuery(id+"F25.wireOp",EDGE,"E250.left");var subQ2=makeQuery(id+"F25.imprint","INTERSECT",VERTEX,{"derivedFrom":[subQ1,subQ0]});Q135=makeQuery(id+"F25.imprint","IMPRINT",FACE,{"disambiguationData":[TD([[makeQuery(id+"F25.imprint","IMPRINT",EDGE,{"disambiguationData":[TD([[subQ2,-1.0]])],"derivedFrom":subQ1}),1.0]])]});}
            var Q136;
            {var subQ0=sQuery(id+"F25.wireOp",EDGE,"E512.trimOffspring");var subQ1=sQuery(id+"F25.wireOp",EDGE,"E250.right");var subQ2=makeQuery(id+"F25.imprint","INTERSECT",VERTEX,{"derivedFrom":[subQ1,subQ0]});Q136=makeQuery(id+"F25.imprint","IMPRINT",FACE,{"disambiguationData":[TD([[makeQuery(id+"F25.imprint","IMPRINT",EDGE,{"disambiguationData":[TD([[subQ2,-1.0]])],"derivedFrom":subQ1}),1.0]])]});}
            var Q137;
            {var subQ0=sQuery(id+"F25.wireOp",EDGE,"E512.trimOffspring");var subQ1=sQuery(id+"F25.wireOp",EDGE,"E249.right");var subQ2=makeQuery(id+"F25.imprint","INTERSECT",VERTEX,{"derivedFrom":[subQ1,subQ0]});Q137=makeQuery(id+"F25.imprint","IMPRINT",FACE,{"disambiguationData":[TD([[makeQuery(id+"F25.imprint","IMPRINT",EDGE,{"disambiguationData":[TD([[subQ2,-1.0]])],"derivedFrom":subQ1}),1.0]])]});}
            var Q138;
            {var subQ0=sQuery(id+"F25.wireOp",EDGE,"E507.trimOffspring");var subQ1=sQuery(id+"F25.wireOp",EDGE,"E249.right");var subQ2=makeQuery(id+"F25.imprint","INTERSECT",VERTEX,{"derivedFrom":[subQ1,subQ0]});Q138=makeQuery(id+"F25.imprint","IMPRINT",FACE,{"disambiguationData":[TD([[makeQuery(id+"F25.imprint","IMPRINT",EDGE,{"disambiguationData":[TD([[subQ2,-1.0]])],"derivedFrom":subQ1}),1.0]])]});}
            var Q139;
            {var subQ5=sQuery(id+"F25.wireOp",EDGE,"E253.right");Q139=makeQuery(id+"F25.imprint","IMPRINT",FACE,{"disambiguationData":[TD([[makeQuery(id+"F25.imprint","IMPRINT",EDGE,{"derivedFrom":subQ5}),1.0]])]});}
            var Q140;
            {var subQ5=sQuery(id+"F25.wireOp",EDGE,"E252.right");Q140=makeQuery(id+"F25.imprint","IMPRINT",FACE,{"disambiguationData":[TD([[makeQuery(id+"F25.imprint","IMPRINT",EDGE,{"derivedFrom":subQ5}),-1.0]])]});}
            var Q141;
            {var subQ0=sQuery(id+"F25.wireOp",EDGE,"E253.right");Q141=makeQuery(id+"F25.imprint","IMPRINT",FACE,{"disambiguationData":[TD([[makeQuery(id+"F25.imprint","IMPRINT",EDGE,{"derivedFrom":subQ0}),-1.0]])]});}
            var Q142;
            {var subQ0=sQuery(id+"F25.wireOp",EDGE,"E252.right");Q142=makeQuery(id+"F25.imprint","IMPRINT",FACE,{"disambiguationData":[TD([[makeQuery(id+"F25.imprint","IMPRINT",EDGE,{"derivedFrom":subQ0}),1.0]])]});}
            var Q143;
            {var subQ0=sQuery(id+"F25.wireOp",EDGE,"E518.trimOffspring");var subQ5=sQuery(id+"F25.wireOp",EDGE,"E249.right");var subQ7=makeQuery(id+"F25.imprint","INTERSECT",VERTEX,{"derivedFrom":[subQ5,subQ0]});Q143=makeQuery(id+"F25.imprint","IMPRINT",FACE,{"disambiguationData":[TD([[makeQuery(id+"F25.imprint","IMPRINT",EDGE,{"disambiguationData":[TD([[subQ7,-1.0]])],"derivedFrom":subQ5}),-1.0]])]});}
            var Q144;
            {var subQ0=sQuery(id+"F25.wireOp",EDGE,"E373.MirrorCS");var subQ5=sQuery(id+"F25.wireOp",EDGE,"E387.MirrorCS");var subQ6=makeQuery(id+"F25.imprint","INTERSECT",VERTEX,{"derivedFrom":[subQ0,subQ5]});Q144=makeQuery(id+"F25.imprint","IMPRINT",FACE,{"disambiguationData":[TD([[makeQuery(id+"F25.imprint","IMPRINT",EDGE,{"disambiguationData":[TD([[subQ6,-1.0]])],"derivedFrom":subQ5}),1.0]])]});}
            var Q145;
            {var subQ5=sQuery(id+"F25.wireOp",EDGE,"E236.right");Q145=makeQuery(id+"F25.imprint","IMPRINT",FACE,{"disambiguationData":[TD([[makeQuery(id+"F25.imprint","IMPRINT",EDGE,{"derivedFrom":subQ5}),-1.0]])]});}
            var Q146;
            {var subQ5=sQuery(id+"F25.wireOp",EDGE,"E235.right");Q146=makeQuery(id+"F25.imprint","IMPRINT",FACE,{"disambiguationData":[TD([[makeQuery(id+"F25.imprint","IMPRINT",EDGE,{"derivedFrom":subQ5}),1.0]])]});}
            var Q147;
            {var subQ0=sQuery(id+"F25.wireOp",EDGE,"E365.MirrorCS");var subQ1=sQuery(id+"F25.wireOp",EDGE,"E344.MirrorCS");var subQ2=makeQuery(id+"F25.imprint","INTERSECT",VERTEX,{"derivedFrom":[subQ1,subQ0]});Q147=makeQuery(id+"F25.imprint","IMPRINT",FACE,{"disambiguationData":[TD([[makeQuery(id+"F25.imprint","IMPRINT",EDGE,{"disambiguationData":[TD([[subQ2,-1.0]])],"derivedFrom":subQ1}),-1.0]])]});}
            var Q148;
            {var subQ0=sQuery(id+"F25.wireOp",EDGE,"E334.MirrorCS");var subQ1=sQuery(id+"F25.wireOp",EDGE,"E344.MirrorCS");var subQ2=makeQuery(id+"F25.imprint","INTERSECT",VERTEX,{"derivedFrom":[subQ1,subQ0]});Q148=makeQuery(id+"F25.imprint","IMPRINT",FACE,{"disambiguationData":[TD([[makeQuery(id+"F25.imprint","IMPRINT",EDGE,{"disambiguationData":[TD([[subQ2,-1.0]])],"derivedFrom":subQ1}),1.0]])]});}
            var Q149;
            {var subQ0=sQuery(id+"F25.wireOp",EDGE,"E334.MirrorCS");var subQ1=sQuery(id+"F25.wireOp",EDGE,"E344.MirrorCS");var subQ2=makeQuery(id+"F25.imprint","INTERSECT",VERTEX,{"derivedFrom":[subQ1,subQ0]});Q149=makeQuery(id+"F25.imprint","IMPRINT",FACE,{"disambiguationData":[TD([[makeQuery(id+"F25.imprint","IMPRINT",EDGE,{"disambiguationData":[TD([[subQ2,-1.0]])],"derivedFrom":subQ1}),-1.0]])]});}
            var Q150;
            {var subQ0=sQuery(id+"F25.wireOp",EDGE,"E386.MirrorCS");var subQ1=sQuery(id+"F25.wireOp",EDGE,"E344.MirrorCS");var subQ2=makeQuery(id+"F25.imprint","INTERSECT",VERTEX,{"derivedFrom":[subQ1,subQ0]});Q150=makeQuery(id+"F25.imprint","IMPRINT",FACE,{"disambiguationData":[TD([[makeQuery(id+"F25.imprint","IMPRINT",EDGE,{"disambiguationData":[TD([[subQ2,-1.0]])],"derivedFrom":subQ1}),-1.0]])]});}
            var Q151;
            {var subQ0=sQuery(id+"F25.wireOp",EDGE,"E386.MirrorCS");var subQ1=sQuery(id+"F25.wireOp",EDGE,"E344.MirrorCS");var subQ2=makeQuery(id+"F25.imprint","INTERSECT",VERTEX,{"derivedFrom":[subQ1,subQ0]});Q151=makeQuery(id+"F25.imprint","IMPRINT",FACE,{"disambiguationData":[TD([[makeQuery(id+"F25.imprint","IMPRINT",EDGE,{"disambiguationData":[TD([[subQ2,-1.0]])],"derivedFrom":subQ1}),1.0]])]});}
            var Q152;
            {var subQ0=sQuery(id+"F25.wireOp",EDGE,"E398.MirrorCS");var subQ1=sQuery(id+"F25.wireOp",EDGE,"E334.MirrorCS");var subQ2=makeQuery(id+"F25.imprint","INTERSECT",VERTEX,{"derivedFrom":[subQ1,subQ0]});Q152=makeQuery(id+"F25.imprint","IMPRINT",FACE,{"disambiguationData":[TD([[makeQuery(id+"F25.imprint","IMPRINT",EDGE,{"disambiguationData":[TD([[subQ2,-1.0]])],"derivedFrom":subQ1}),-1.0]])]});}
            var Q153;
            {var subQ0=sQuery(id+"F25.wireOp",EDGE,"E398.MirrorCS");var subQ1=sQuery(id+"F25.wireOp",EDGE,"E365.MirrorCS");var subQ2=makeQuery(id+"F25.imprint","INTERSECT",VERTEX,{"derivedFrom":[subQ1,subQ0]});Q153=makeQuery(id+"F25.imprint","IMPRINT",FACE,{"disambiguationData":[TD([[makeQuery(id+"F25.imprint","IMPRINT",EDGE,{"disambiguationData":[TD([[subQ2,-1.0]])],"derivedFrom":subQ1}),-1.0]])]});}
            var Q154;
            {var subQ0=sQuery(id+"F25.wireOp",EDGE,"E366.MirrorCS");var subQ1=sQuery(id+"F25.wireOp",EDGE,"E334.MirrorCS");var subQ2=makeQuery(id+"F25.imprint","INTERSECT",VERTEX,{"derivedFrom":[subQ1,subQ0]});Q154=makeQuery(id+"F25.imprint","IMPRINT",FACE,{"disambiguationData":[TD([[makeQuery(id+"F25.imprint","IMPRINT",EDGE,{"disambiguationData":[TD([[subQ2,-1.0]])],"derivedFrom":subQ1}),-1.0]])]});}
            var Q155;
            {var subQ0=sQuery(id+"F25.wireOp",EDGE,"E366.MirrorCS");var subQ1=sQuery(id+"F25.wireOp",EDGE,"E365.MirrorCS");var subQ2=makeQuery(id+"F25.imprint","INTERSECT",VERTEX,{"derivedFrom":[subQ1,subQ0]});Q155=makeQuery(id+"F25.imprint","IMPRINT",FACE,{"disambiguationData":[TD([[makeQuery(id+"F25.imprint","IMPRINT",EDGE,{"disambiguationData":[TD([[subQ2,-1.0]])],"derivedFrom":subQ1}),-1.0]])]});}
            var Q156;
            {var subQ0=sQuery(id+"F25.wireOp",EDGE,"E366.MirrorCS");var subQ1=sQuery(id+"F25.wireOp",EDGE,"E365.MirrorCS");var subQ2=makeQuery(id+"F25.imprint","INTERSECT",VERTEX,{"derivedFrom":[subQ1,subQ0]});Q156=makeQuery(id+"F25.imprint","IMPRINT",FACE,{"disambiguationData":[TD([[makeQuery(id+"F25.imprint","IMPRINT",EDGE,{"disambiguationData":[TD([[subQ2,-1.0]])],"derivedFrom":subQ1}),1.0]])]});}
            var Q157;
            {var subQ0=sQuery(id+"F25.wireOp",EDGE,"E365.MirrorCS");var subQ1=sQuery(id+"F25.wireOp",EDGE,"E347.MirrorCS");var subQ2=makeQuery(id+"F25.imprint","INTERSECT",VERTEX,{"derivedFrom":[subQ1,subQ0]});Q157=makeQuery(id+"F25.imprint","IMPRINT",FACE,{"disambiguationData":[TD([[makeQuery(id+"F25.imprint","IMPRINT",EDGE,{"disambiguationData":[TD([[subQ2,-1.0]])],"derivedFrom":subQ1}),-1.0]])]});}
            var Q158;
            {var subQ0=sQuery(id+"F25.wireOp",EDGE,"E334.MirrorCS");var subQ1=sQuery(id+"F25.wireOp",EDGE,"E347.MirrorCS");var subQ2=makeQuery(id+"F25.imprint","INTERSECT",VERTEX,{"derivedFrom":[subQ1,subQ0]});Q158=makeQuery(id+"F25.imprint","IMPRINT",FACE,{"disambiguationData":[TD([[makeQuery(id+"F25.imprint","IMPRINT",EDGE,{"disambiguationData":[TD([[subQ2,-1.0]])],"derivedFrom":subQ1}),-1.0]])]});}
            var Q159;
            {var subQ0=sQuery(id+"F25.wireOp",EDGE,"E386.MirrorCS");var subQ1=sQuery(id+"F25.wireOp",EDGE,"E347.MirrorCS");var subQ2=makeQuery(id+"F25.imprint","INTERSECT",VERTEX,{"derivedFrom":[subQ1,subQ0]});Q159=makeQuery(id+"F25.imprint","IMPRINT",FACE,{"disambiguationData":[TD([[makeQuery(id+"F25.imprint","IMPRINT",EDGE,{"disambiguationData":[TD([[subQ2,-1.0]])],"derivedFrom":subQ1}),-1.0]])]});}
            var Q160;
            {var subQ0=sQuery(id+"F25.wireOp",EDGE,"E386.MirrorCS");var subQ1=sQuery(id+"F25.wireOp",EDGE,"E347.MirrorCS");var subQ2=makeQuery(id+"F25.imprint","INTERSECT",VERTEX,{"derivedFrom":[subQ1,subQ0]});Q160=makeQuery(id+"F25.imprint","IMPRINT",FACE,{"disambiguationData":[TD([[makeQuery(id+"F25.imprint","IMPRINT",EDGE,{"disambiguationData":[TD([[subQ2,-1.0]])],"derivedFrom":subQ1}),1.0]])]});}
            var Q161;
            {var subQ0=sQuery(id+"F25.wireOp",EDGE,"E334.MirrorCS");var subQ1=sQuery(id+"F25.wireOp",EDGE,"E347.MirrorCS");var subQ2=makeQuery(id+"F25.imprint","INTERSECT",VERTEX,{"derivedFrom":[subQ1,subQ0]});Q161=makeQuery(id+"F25.imprint","IMPRINT",FACE,{"disambiguationData":[TD([[makeQuery(id+"F25.imprint","IMPRINT",EDGE,{"disambiguationData":[TD([[subQ2,-1.0]])],"derivedFrom":subQ1}),1.0]])]});}
            var Q162;
            {var subQ0=sQuery(id+"F25.wireOp",EDGE,"E237.right");Q162=makeQuery(id+"F25.imprint","IMPRINT",FACE,{"disambiguationData":[TD([[makeQuery(id+"F25.imprint","IMPRINT",EDGE,{"derivedFrom":subQ0}),-1.0]])]});}
            var Q163;
            {var subQ0=sQuery(id+"F25.wireOp",EDGE,"E238.right");Q163=makeQuery(id+"F25.imprint","IMPRINT",FACE,{"disambiguationData":[TD([[makeQuery(id+"F25.imprint","IMPRINT",EDGE,{"derivedFrom":subQ0}),1.0]])]});}
            var Q164;
            {var subQ0=sQuery(id+"F25.wireOp",EDGE,"E236.right");Q164=makeQuery(id+"F25.imprint","IMPRINT",FACE,{"disambiguationData":[TD([[makeQuery(id+"F25.imprint","IMPRINT",EDGE,{"derivedFrom":subQ0}),1.0]])]});}
            var Q165;
            {var subQ0=sQuery(id+"F25.wireOp",EDGE,"E365.MirrorCS");var subQ1=sQuery(id+"F25.wireOp",EDGE,"E344.MirrorCS");var subQ2=makeQuery(id+"F25.imprint","INTERSECT",VERTEX,{"derivedFrom":[subQ1,subQ0]});Q165=makeQuery(id+"F25.imprint","IMPRINT",FACE,{"disambiguationData":[TD([[makeQuery(id+"F25.imprint","IMPRINT",EDGE,{"disambiguationData":[TD([[subQ2,-1.0]])],"derivedFrom":subQ1}),1.0]])]});}
            var Q166;
            {var subQ5=sQuery(id+"F25.wireOp",EDGE,"E237.right");Q166=makeQuery(id+"F25.imprint","IMPRINT",FACE,{"disambiguationData":[TD([[makeQuery(id+"F25.imprint","IMPRINT",EDGE,{"derivedFrom":subQ5}),1.0]])]});}
            var Q167;
            {var subQ5=sQuery(id+"F25.wireOp",EDGE,"E238.right");Q167=makeQuery(id+"F25.imprint","IMPRINT",FACE,{"disambiguationData":[TD([[makeQuery(id+"F25.imprint","IMPRINT",EDGE,{"derivedFrom":subQ5}),-1.0]])]});}
            var Q168;
            {var subQ0=sQuery(id+"F25.wireOp",EDGE,"E295.trimOffspring");var subQ1=sQuery(id+"F25.wireOp",EDGE,"E249.right");var subQ2=makeQuery(id+"F25.imprint","INTERSECT",VERTEX,{"derivedFrom":[subQ1,subQ0]});Q168=makeQuery(id+"F25.imprint","IMPRINT",FACE,{"disambiguationData":[TD([[makeQuery(id+"F25.imprint","IMPRINT",EDGE,{"disambiguationData":[TD([[subQ2,-1.0]])],"derivedFrom":subQ1}),1.0]])]});}
            var Q169;
            {var subQ0=sQuery(id+"F25.wireOp",EDGE,"E296.trimOffspring");var subQ1=sQuery(id+"F25.wireOp",EDGE,"E249.right");var subQ2=makeQuery(id+"F25.imprint","INTERSECT",VERTEX,{"derivedFrom":[subQ1,subQ0]});Q169=makeQuery(id+"F25.imprint","IMPRINT",FACE,{"disambiguationData":[TD([[makeQuery(id+"F25.imprint","IMPRINT",EDGE,{"disambiguationData":[TD([[subQ2,-1.0]])],"derivedFrom":subQ1}),1.0]])]});}
            var Q170;
            {var subQ0=sQuery(id+"F25.wireOp",EDGE,"E296.trimOffspring");var subQ1=sQuery(id+"F25.wireOp",EDGE,"E250.right");var subQ2=makeQuery(id+"F25.imprint","INTERSECT",VERTEX,{"derivedFrom":[subQ1,subQ0]});Q170=makeQuery(id+"F25.imprint","IMPRINT",FACE,{"disambiguationData":[TD([[makeQuery(id+"F25.imprint","IMPRINT",EDGE,{"disambiguationData":[TD([[subQ2,-1.0]])],"derivedFrom":subQ1}),1.0]])]});}
            var Q171;
            {var subQ0=sQuery(id+"F25.wireOp",EDGE,"E296.trimOffspring");var subQ1=sQuery(id+"F25.wireOp",EDGE,"E250.left");var subQ2=makeQuery(id+"F25.imprint","INTERSECT",VERTEX,{"derivedFrom":[subQ1,subQ0]});Q171=makeQuery(id+"F25.imprint","IMPRINT",FACE,{"disambiguationData":[TD([[makeQuery(id+"F25.imprint","IMPRINT",EDGE,{"disambiguationData":[TD([[subQ2,-1.0]])],"derivedFrom":subQ1}),1.0]])]});}
            var Q172;
            {var subQ0=sQuery(id+"F25.wireOp",EDGE,"E295.trimOffspring");var subQ1=sQuery(id+"F25.wireOp",EDGE,"E250.left");var subQ2=makeQuery(id+"F25.imprint","INTERSECT",VERTEX,{"derivedFrom":[subQ1,subQ0]});Q172=makeQuery(id+"F25.imprint","IMPRINT",FACE,{"disambiguationData":[TD([[makeQuery(id+"F25.imprint","IMPRINT",EDGE,{"disambiguationData":[TD([[subQ2,-1.0]])],"derivedFrom":subQ1}),1.0]])]});}
            var Q173;
            {var subQ0=sQuery(id+"F25.wireOp",EDGE,"E295.trimOffspring");var subQ1=sQuery(id+"F25.wireOp",EDGE,"E250.right");var subQ2=makeQuery(id+"F25.imprint","INTERSECT",VERTEX,{"derivedFrom":[subQ1,subQ0]});Q173=makeQuery(id+"F25.imprint","IMPRINT",FACE,{"disambiguationData":[TD([[makeQuery(id+"F25.imprint","IMPRINT",EDGE,{"disambiguationData":[TD([[subQ2,-1.0]])],"derivedFrom":subQ1}),1.0]])]});}
            var Q174;
            {var subQ0=sQuery(id+"F25.wireOp",EDGE,"E251.bottom");Q174=makeQuery(id+"F25.imprint","IMPRINT",FACE,{"disambiguationData":[TD([[makeQuery(id+"F25.imprint","IMPRINT",EDGE,{"derivedFrom":subQ0}),-1.0]])]});}
            var Q175;
            {var subQ0=sQuery(id+"F25.wireOp",EDGE,"E250.bottom");Q175=makeQuery(id+"F25.imprint","IMPRINT",FACE,{"disambiguationData":[TD([[makeQuery(id+"F25.imprint","IMPRINT",EDGE,{"derivedFrom":subQ0}),1.0]])]});}
            var Q176;
            {var subQ0=sQuery(id+"F25.wireOp",EDGE,"E288.trimOffspring");var subQ1=sQuery(id+"F25.wireOp",EDGE,"E250.left");var subQ2=makeQuery(id+"F25.imprint","INTERSECT",VERTEX,{"derivedFrom":[subQ1,subQ0]});Q176=makeQuery(id+"F25.imprint","IMPRINT",FACE,{"disambiguationData":[TD([[makeQuery(id+"F25.imprint","IMPRINT",EDGE,{"disambiguationData":[TD([[subQ2,-1.0]])],"derivedFrom":subQ1}),1.0]])]});}
            var Q177;
            {var subQ0=sQuery(id+"F25.wireOp",EDGE,"E292.trimOffspring");var subQ1=sQuery(id+"F25.wireOp",EDGE,"E250.left");var subQ2=makeQuery(id+"F25.imprint","INTERSECT",VERTEX,{"derivedFrom":[subQ1,subQ0]});Q177=makeQuery(id+"F25.imprint","IMPRINT",FACE,{"disambiguationData":[TD([[makeQuery(id+"F25.imprint","IMPRINT",EDGE,{"disambiguationData":[TD([[subQ2,-1.0]])],"derivedFrom":subQ1}),1.0]])]});}
            var Q178;
            {var subQ0=sQuery(id+"F25.wireOp",EDGE,"E288.trimOffspring");var subQ1=sQuery(id+"F25.wireOp",EDGE,"E250.right");var subQ2=makeQuery(id+"F25.imprint","INTERSECT",VERTEX,{"derivedFrom":[subQ1,subQ0]});Q178=makeQuery(id+"F25.imprint","IMPRINT",FACE,{"disambiguationData":[TD([[makeQuery(id+"F25.imprint","IMPRINT",EDGE,{"disambiguationData":[TD([[subQ2,-1.0]])],"derivedFrom":subQ1}),1.0]])]});}
            var Q179;
            {var subQ0=sQuery(id+"F25.wireOp",EDGE,"E292.trimOffspring");var subQ1=sQuery(id+"F25.wireOp",EDGE,"E250.right");var subQ2=makeQuery(id+"F25.imprint","INTERSECT",VERTEX,{"derivedFrom":[subQ1,subQ0]});Q179=makeQuery(id+"F25.imprint","IMPRINT",FACE,{"disambiguationData":[TD([[makeQuery(id+"F25.imprint","IMPRINT",EDGE,{"disambiguationData":[TD([[subQ2,-1.0]])],"derivedFrom":subQ1}),1.0]])]});}
            var Q180;
            {var subQ0=sQuery(id+"F25.wireOp",EDGE,"E288.trimOffspring");var subQ1=sQuery(id+"F25.wireOp",EDGE,"E249.right");var subQ2=makeQuery(id+"F25.imprint","INTERSECT",VERTEX,{"derivedFrom":[subQ1,subQ0]});Q180=makeQuery(id+"F25.imprint","IMPRINT",FACE,{"disambiguationData":[TD([[makeQuery(id+"F25.imprint","IMPRINT",EDGE,{"disambiguationData":[TD([[subQ2,-1.0]])],"derivedFrom":subQ1}),1.0]])]});}
            var Q181;
            {var subQ0=sQuery(id+"F25.wireOp",EDGE,"E292.trimOffspring");var subQ1=sQuery(id+"F25.wireOp",EDGE,"E249.right");var subQ2=makeQuery(id+"F25.imprint","INTERSECT",VERTEX,{"derivedFrom":[subQ1,subQ0]});Q181=makeQuery(id+"F25.imprint","IMPRINT",FACE,{"disambiguationData":[TD([[makeQuery(id+"F25.imprint","IMPRINT",EDGE,{"disambiguationData":[TD([[subQ2,-1.0]])],"derivedFrom":subQ1}),1.0]])]});}
            var Q182;
            {var subQ5=sQuery(id+"F25.wireOp",EDGE,"E242.right");Q182=makeQuery(id+"F25.imprint","IMPRINT",FACE,{"disambiguationData":[TD([[makeQuery(id+"F25.imprint","IMPRINT",EDGE,{"derivedFrom":subQ5}),-1.0]])]});}
            var Q183;
            {var subQ0=sQuery(id+"F25.wireOp",EDGE,"E242.right");Q183=makeQuery(id+"F25.imprint","IMPRINT",FACE,{"disambiguationData":[TD([[makeQuery(id+"F25.imprint","IMPRINT",EDGE,{"derivedFrom":subQ0}),1.0]])]});}
            var Q184;
            {var subQ5=sQuery(id+"F25.wireOp",EDGE,"E241.right");Q184=makeQuery(id+"F25.imprint","IMPRINT",FACE,{"disambiguationData":[TD([[makeQuery(id+"F25.imprint","IMPRINT",EDGE,{"derivedFrom":subQ5}),1.0]])]});}
            var Q185;
            {var subQ0=sQuery(id+"F25.wireOp",EDGE,"E241.right");Q185=makeQuery(id+"F25.imprint","IMPRINT",FACE,{"disambiguationData":[TD([[makeQuery(id+"F25.imprint","IMPRINT",EDGE,{"derivedFrom":subQ0}),-1.0]])]});}
            var Q186;
            {var subQ0=sQuery(id+"F25.wireOp",EDGE,"E365.MirrorCS");var subQ1=sQuery(id+"F25.wireOp",EDGE,"E341.MirrorCS");var subQ2=makeQuery(id+"F25.imprint","INTERSECT",VERTEX,{"derivedFrom":[subQ1,subQ0]});Q186=makeQuery(id+"F25.imprint","IMPRINT",FACE,{"disambiguationData":[TD([[makeQuery(id+"F25.imprint","IMPRINT",EDGE,{"disambiguationData":[TD([[subQ2,-1.0]])],"derivedFrom":subQ1}),-1.0]])]});}
            var Q187;
            {var subQ0=sQuery(id+"F25.wireOp",EDGE,"E356.MirrorCS");var subQ1=sQuery(id+"F25.wireOp",EDGE,"E365.MirrorCS");var subQ2=makeQuery(id+"F25.imprint","INTERSECT",VERTEX,{"derivedFrom":[subQ1,subQ0]});Q187=makeQuery(id+"F25.imprint","IMPRINT",FACE,{"disambiguationData":[TD([[makeQuery(id+"F25.imprint","IMPRINT",EDGE,{"disambiguationData":[TD([[subQ2,-1.0]])],"derivedFrom":subQ1}),1.0]])]});}
            var Q188;
            {var subQ0=sQuery(id+"F25.wireOp",EDGE,"E334.MirrorCS");var subQ1=sQuery(id+"F25.wireOp",EDGE,"E341.MirrorCS");var subQ2=makeQuery(id+"F25.imprint","INTERSECT",VERTEX,{"derivedFrom":[subQ1,subQ0]});Q188=makeQuery(id+"F25.imprint","IMPRINT",FACE,{"disambiguationData":[TD([[makeQuery(id+"F25.imprint","IMPRINT",EDGE,{"disambiguationData":[TD([[subQ2,-1.0]])],"derivedFrom":subQ1}),-1.0]])]});}
            var Q189;
            {var subQ0=sQuery(id+"F25.wireOp",EDGE,"E356.MirrorCS");var subQ1=sQuery(id+"F25.wireOp",EDGE,"E365.MirrorCS");var subQ2=makeQuery(id+"F25.imprint","INTERSECT",VERTEX,{"derivedFrom":[subQ1,subQ0]});Q189=makeQuery(id+"F25.imprint","IMPRINT",FACE,{"disambiguationData":[TD([[makeQuery(id+"F25.imprint","IMPRINT",EDGE,{"disambiguationData":[TD([[subQ2,-1.0]])],"derivedFrom":subQ1}),-1.0]])]});}
            var Q190;
            {var subQ0=sQuery(id+"F25.wireOp",EDGE,"E386.MirrorCS");var subQ1=sQuery(id+"F25.wireOp",EDGE,"E341.MirrorCS");var subQ2=makeQuery(id+"F25.imprint","INTERSECT",VERTEX,{"derivedFrom":[subQ1,subQ0]});Q190=makeQuery(id+"F25.imprint","IMPRINT",FACE,{"disambiguationData":[TD([[makeQuery(id+"F25.imprint","IMPRINT",EDGE,{"disambiguationData":[TD([[subQ2,-1.0]])],"derivedFrom":subQ1}),-1.0]])]});}
            var Q191;
            {var subQ0=sQuery(id+"F25.wireOp",EDGE,"E356.MirrorCS");var subQ1=sQuery(id+"F25.wireOp",EDGE,"E334.MirrorCS");var subQ2=makeQuery(id+"F25.imprint","INTERSECT",VERTEX,{"derivedFrom":[subQ1,subQ0]});Q191=makeQuery(id+"F25.imprint","IMPRINT",FACE,{"disambiguationData":[TD([[makeQuery(id+"F25.imprint","IMPRINT",EDGE,{"disambiguationData":[TD([[subQ2,-1.0]])],"derivedFrom":subQ1}),-1.0]])]});}
            var Q192;
            {var subQ0=sQuery(id+"F25.wireOp",EDGE,"E386.MirrorCS");var subQ1=sQuery(id+"F25.wireOp",EDGE,"E339.MirrorCS");var subQ2=makeQuery(id+"F25.imprint","INTERSECT",VERTEX,{"derivedFrom":[subQ1,subQ0]});Q192=makeQuery(id+"F25.imprint","IMPRINT",FACE,{"disambiguationData":[TD([[makeQuery(id+"F25.imprint","IMPRINT",EDGE,{"disambiguationData":[TD([[subQ2,-1.0]])],"derivedFrom":subQ1}),1.0]])]});}
            var Q193;
            {var subQ0=sQuery(id+"F25.wireOp",EDGE,"E334.MirrorCS");var subQ1=sQuery(id+"F25.wireOp",EDGE,"E339.MirrorCS");var subQ2=makeQuery(id+"F25.imprint","INTERSECT",VERTEX,{"derivedFrom":[subQ1,subQ0]});Q193=makeQuery(id+"F25.imprint","IMPRINT",FACE,{"disambiguationData":[TD([[makeQuery(id+"F25.imprint","IMPRINT",EDGE,{"disambiguationData":[TD([[subQ2,-1.0]])],"derivedFrom":subQ1}),1.0]])]});}
            var Q194;
            {var subQ0=sQuery(id+"F25.wireOp",EDGE,"E334.MirrorCS");var subQ1=sQuery(id+"F25.wireOp",EDGE,"E339.MirrorCS");var subQ2=makeQuery(id+"F25.imprint","INTERSECT",VERTEX,{"derivedFrom":[subQ1,subQ0]});Q194=makeQuery(id+"F25.imprint","IMPRINT",FACE,{"disambiguationData":[TD([[makeQuery(id+"F25.imprint","IMPRINT",EDGE,{"disambiguationData":[TD([[subQ2,-1.0]])],"derivedFrom":subQ1}),-1.0]])]});}
            var Q195;
            {var subQ0=sQuery(id+"F25.wireOp",EDGE,"E361.MirrorCS");var subQ1=sQuery(id+"F25.wireOp",EDGE,"E365.MirrorCS");var subQ2=makeQuery(id+"F25.imprint","INTERSECT",VERTEX,{"derivedFrom":[subQ1,subQ0]});Q195=makeQuery(id+"F25.imprint","IMPRINT",FACE,{"disambiguationData":[TD([[makeQuery(id+"F25.imprint","IMPRINT",EDGE,{"disambiguationData":[TD([[subQ2,-1.0]])],"derivedFrom":subQ1}),-1.0]])]});}
            var Q196;
            {var subQ0=sQuery(id+"F25.wireOp",EDGE,"E361.MirrorCS");var subQ1=sQuery(id+"F25.wireOp",EDGE,"E334.MirrorCS");var subQ2=makeQuery(id+"F25.imprint","INTERSECT",VERTEX,{"derivedFrom":[subQ1,subQ0]});Q196=makeQuery(id+"F25.imprint","IMPRINT",FACE,{"disambiguationData":[TD([[makeQuery(id+"F25.imprint","IMPRINT",EDGE,{"disambiguationData":[TD([[subQ2,-1.0]])],"derivedFrom":subQ1}),-1.0]])]});}
            var Q197;
            {var subQ0=sQuery(id+"F25.wireOp",EDGE,"E386.MirrorCS");var subQ1=sQuery(id+"F25.wireOp",EDGE,"E339.MirrorCS");var subQ2=makeQuery(id+"F25.imprint","INTERSECT",VERTEX,{"derivedFrom":[subQ1,subQ0]});Q197=makeQuery(id+"F25.imprint","IMPRINT",FACE,{"disambiguationData":[TD([[makeQuery(id+"F25.imprint","IMPRINT",EDGE,{"disambiguationData":[TD([[subQ2,-1.0]])],"derivedFrom":subQ1}),-1.0]])]});}
            var Q198;
            {var subQ0=sQuery(id+"F25.wireOp",EDGE,"E361.MirrorCS");var subQ1=sQuery(id+"F25.wireOp",EDGE,"E365.MirrorCS");var subQ2=makeQuery(id+"F25.imprint","INTERSECT",VERTEX,{"derivedFrom":[subQ1,subQ0]});Q198=makeQuery(id+"F25.imprint","IMPRINT",FACE,{"disambiguationData":[TD([[makeQuery(id+"F25.imprint","IMPRINT",EDGE,{"disambiguationData":[TD([[subQ2,-1.0]])],"derivedFrom":subQ1}),1.0]])]});}
            var Q199;
            {var subQ0=sQuery(id+"F25.wireOp",EDGE,"E365.MirrorCS");var subQ1=sQuery(id+"F25.wireOp",EDGE,"E339.MirrorCS");var subQ2=makeQuery(id+"F25.imprint","INTERSECT",VERTEX,{"derivedFrom":[subQ1,subQ0]});Q199=makeQuery(id+"F25.imprint","IMPRINT",FACE,{"disambiguationData":[TD([[makeQuery(id+"F25.imprint","IMPRINT",EDGE,{"disambiguationData":[TD([[subQ2,-1.0]])],"derivedFrom":subQ1}),-1.0]])]});}
            var Q200;
            {var subQ0=sQuery(id+"F25.wireOp",EDGE,"E386.MirrorCS");var subQ1=sQuery(id+"F25.wireOp",EDGE,"E339.MirrorCS");var subQ2=makeQuery(id+"F25.imprint","INTERSECT",VERTEX,{"derivedFrom":[subQ1,subQ0]});Q200=makeQuery(id+"F25.imprint","IMPRINT",FACE,{"disambiguationData":[TD([[makeQuery(id+"F25.imprint","IMPRINT",EDGE,{"disambiguationData":[TD([[subQ2,-1.0]])],"derivedFrom":subQ1}),-1.0]])]});}
            var Q201;
            {var subQ0=sQuery(id+"F25.wireOp",EDGE,"E240.right");Q201=makeQuery(id+"F25.imprint","IMPRINT",FACE,{"disambiguationData":[TD([[makeQuery(id+"F25.imprint","IMPRINT",EDGE,{"derivedFrom":subQ0}),1.0]])]});}
            var Q202;
            {var subQ0=sQuery(id+"F25.wireOp",EDGE,"E239.right");Q202=makeQuery(id+"F25.imprint","IMPRINT",FACE,{"disambiguationData":[TD([[makeQuery(id+"F25.imprint","IMPRINT",EDGE,{"derivedFrom":subQ0}),-1.0]])]});}
            var Q203;
            {var subQ5=sQuery(id+"F25.wireOp",EDGE,"E239.right");Q203=makeQuery(id+"F25.imprint","IMPRINT",FACE,{"disambiguationData":[TD([[makeQuery(id+"F25.imprint","IMPRINT",EDGE,{"derivedFrom":subQ5}),1.0]])]});}
            var Q204;
            {var subQ5=sQuery(id+"F25.wireOp",EDGE,"E240.right");Q204=makeQuery(id+"F25.imprint","IMPRINT",FACE,{"disambiguationData":[TD([[makeQuery(id+"F25.imprint","IMPRINT",EDGE,{"derivedFrom":subQ5}),-1.0]])]});}
            var Q205;
            {var subQ0=sQuery(id+"F25.wireOp",EDGE,"E293.trimOffspring");var subQ1=sQuery(id+"F25.wireOp",EDGE,"E249.right");var subQ2=makeQuery(id+"F25.imprint","INTERSECT",VERTEX,{"derivedFrom":[subQ1,subQ0]});Q205=makeQuery(id+"F25.imprint","IMPRINT",FACE,{"disambiguationData":[TD([[makeQuery(id+"F25.imprint","IMPRINT",EDGE,{"disambiguationData":[TD([[subQ2,-1.0]])],"derivedFrom":subQ1}),1.0]])]});}
            var Q206;
            {var subQ0=sQuery(id+"F25.wireOp",EDGE,"E297.trimOffspring");var subQ1=sQuery(id+"F25.wireOp",EDGE,"E249.right");var subQ2=makeQuery(id+"F25.imprint","INTERSECT",VERTEX,{"derivedFrom":[subQ1,subQ0]});Q206=makeQuery(id+"F25.imprint","IMPRINT",FACE,{"disambiguationData":[TD([[makeQuery(id+"F25.imprint","IMPRINT",EDGE,{"disambiguationData":[TD([[subQ2,-1.0]])],"derivedFrom":subQ1}),1.0]])]});}
            var Q207;
            {var subQ0=sQuery(id+"F25.wireOp",EDGE,"E297.trimOffspring");var subQ1=sQuery(id+"F25.wireOp",EDGE,"E250.right");var subQ2=makeQuery(id+"F25.imprint","INTERSECT",VERTEX,{"derivedFrom":[subQ1,subQ0]});Q207=makeQuery(id+"F25.imprint","IMPRINT",FACE,{"disambiguationData":[TD([[makeQuery(id+"F25.imprint","IMPRINT",EDGE,{"disambiguationData":[TD([[subQ2,-1.0]])],"derivedFrom":subQ1}),1.0]])]});}
            var Q208;
            {var subQ0=sQuery(id+"F25.wireOp",EDGE,"E297.trimOffspring");var subQ1=sQuery(id+"F25.wireOp",EDGE,"E250.left");var subQ2=makeQuery(id+"F25.imprint","INTERSECT",VERTEX,{"derivedFrom":[subQ1,subQ0]});Q208=makeQuery(id+"F25.imprint","IMPRINT",FACE,{"disambiguationData":[TD([[makeQuery(id+"F25.imprint","IMPRINT",EDGE,{"disambiguationData":[TD([[subQ2,-1.0]])],"derivedFrom":subQ1}),1.0]])]});}
            var Q209;
            {var subQ0=sQuery(id+"F25.wireOp",EDGE,"E293.trimOffspring");var subQ1=sQuery(id+"F25.wireOp",EDGE,"E250.left");var subQ2=makeQuery(id+"F25.imprint","INTERSECT",VERTEX,{"derivedFrom":[subQ1,subQ0]});Q209=makeQuery(id+"F25.imprint","IMPRINT",FACE,{"disambiguationData":[TD([[makeQuery(id+"F25.imprint","IMPRINT",EDGE,{"disambiguationData":[TD([[subQ2,-1.0]])],"derivedFrom":subQ1}),1.0]])]});}
            var Q210;
            {var subQ0=sQuery(id+"F25.wireOp",EDGE,"E293.trimOffspring");var subQ1=sQuery(id+"F25.wireOp",EDGE,"E250.right");var subQ2=makeQuery(id+"F25.imprint","INTERSECT",VERTEX,{"derivedFrom":[subQ1,subQ0]});Q210=makeQuery(id+"F25.imprint","IMPRINT",FACE,{"disambiguationData":[TD([[makeQuery(id+"F25.imprint","IMPRINT",EDGE,{"disambiguationData":[TD([[subQ2,-1.0]])],"derivedFrom":subQ1}),1.0]])]});}
            var Q211;
            {var subQ0=sQuery(id+"F25.wireOp",EDGE,"E232.left");Q211=makeQuery(id+"F25.imprint","IMPRINT",FACE,{"disambiguationData":[TD([[makeQuery(id+"F25.imprint","IMPRINT",EDGE,{"derivedFrom":subQ0}),-1.0]])]});}
            var Q212;
            {var subQ0=sQuery(id+"F25.wireOp",EDGE,"E255.trimOffspring");var subQ1=sQuery(id+"F25.wireOp",EDGE,"E232.top");var subQ2=makeQuery(id+"F25.imprint","INTERSECT",VERTEX,{"derivedFrom":[subQ1,subQ0]});Q212=makeQuery(id+"F25.imprint","IMPRINT",FACE,{"disambiguationData":[TD([[makeQuery(id+"F25.imprint","IMPRINT",EDGE,{"disambiguationData":[TD([[subQ2,-1.0]])],"derivedFrom":subQ1}),-1.0]])]});}
            var Q213;
            {var subQ1=sQuery(id+"F25.wireOp",EDGE,"E232.top");var subQ3=sQuery(id+"F25.wireOp",EDGE,"E256.trimOffspring");var subQ4=makeQuery(id+"F25.imprint","INTERSECT",VERTEX,{"derivedFrom":[subQ1,subQ3]});Q213=makeQuery(id+"F25.imprint","IMPRINT",FACE,{"disambiguationData":[TD([[makeQuery(id+"F25.imprint","IMPRINT",EDGE,{"disambiguationData":[TD([[subQ4,1.0]])],"derivedFrom":subQ3}),-1.0]])]});}
            var Q214;
            {var subQ1=sQuery(id+"F25.wireOp",EDGE,"E234.bottom");var subQ3=sQuery(id+"F25.wireOp",EDGE,"E256.trimOffspring");var subQ4=makeQuery(id+"F25.imprint","INTERSECT",VERTEX,{"derivedFrom":[subQ1,subQ3]});Q214=makeQuery(id+"F25.imprint","IMPRINT",FACE,{"disambiguationData":[TD([[makeQuery(id+"F25.imprint","IMPRINT",EDGE,{"disambiguationData":[TD([[subQ4,1.0]])],"derivedFrom":subQ3}),-1.0]])]});}
            var Q215;
            {var subQ0=sQuery(id+"F25.wireOp",EDGE,"E254.trimOffspring");var subQ5=sQuery(id+"F25.wireOp",EDGE,"E253.top");var subQ6=makeQuery(id+"F25.imprint","INTERSECT",VERTEX,{"derivedFrom":[subQ5,subQ0]});Q215=makeQuery(id+"F25.imprint","IMPRINT",FACE,{"disambiguationData":[TD([[makeQuery(id+"F25.imprint","IMPRINT",EDGE,{"disambiguationData":[TD([[subQ6,1.0]])],"derivedFrom":subQ5}),1.0]])]});}
            var Q216;
            {var subQ0=sQuery(id+"F25.wireOp",EDGE,"E254.trimOffspring");var subQ1=sQuery(id+"F25.wireOp",EDGE,"E253.bottom");var subQ2=makeQuery(id+"F25.imprint","INTERSECT",VERTEX,{"derivedFrom":[subQ1,subQ0]});Q216=makeQuery(id+"F25.imprint","IMPRINT",FACE,{"disambiguationData":[TD([[makeQuery(id+"F25.imprint","IMPRINT",EDGE,{"disambiguationData":[TD([[subQ2,1.0]])],"derivedFrom":subQ1}),1.0]])]});}
            var Q217;
            {var subQ0=sQuery(id+"F25.wireOp",EDGE,"E254.trimOffspring");var subQ1=sQuery(id+"F25.wireOp",EDGE,"E252.top");var subQ2=makeQuery(id+"F25.imprint","INTERSECT",VERTEX,{"derivedFrom":[subQ1,subQ0]});Q217=makeQuery(id+"F25.imprint","IMPRINT",FACE,{"disambiguationData":[TD([[makeQuery(id+"F25.imprint","IMPRINT",EDGE,{"disambiguationData":[TD([[subQ2,1.0]])],"derivedFrom":subQ1}),1.0]])]});}
            var Q218;
            {var subQ0=sQuery(id+"F25.wireOp",EDGE,"E256.trimOffspring");var subQ1=sQuery(id+"F25.wireOp",EDGE,"E235.top");var subQ2=makeQuery(id+"F25.imprint","INTERSECT",VERTEX,{"derivedFrom":[subQ1,subQ0]});Q218=makeQuery(id+"F25.imprint","IMPRINT",FACE,{"disambiguationData":[TD([[makeQuery(id+"F25.imprint","IMPRINT",EDGE,{"disambiguationData":[TD([[subQ2,-1.0]])],"derivedFrom":subQ1}),1.0]])]});}
            var Q219;
            {var subQ0=sQuery(id+"F25.wireOp",EDGE,"E256.trimOffspring");var subQ1=sQuery(id+"F25.wireOp",EDGE,"E235.top");var subQ2=makeQuery(id+"F25.imprint","INTERSECT",VERTEX,{"derivedFrom":[subQ1,subQ0]});Q219=makeQuery(id+"F25.imprint","IMPRINT",FACE,{"disambiguationData":[TD([[makeQuery(id+"F25.imprint","IMPRINT",EDGE,{"disambiguationData":[TD([[subQ2,-1.0]])],"derivedFrom":subQ1}),-1.0]])]});}
            var Q220;
            {var subQ0=sQuery(id+"F25.wireOp",EDGE,"E254.trimOffspring");var subQ1=sQuery(id+"F25.wireOp",EDGE,"E235.top");var subQ2=makeQuery(id+"F25.imprint","INTERSECT",VERTEX,{"derivedFrom":[subQ1,subQ0]});Q220=makeQuery(id+"F25.imprint","IMPRINT",FACE,{"disambiguationData":[TD([[makeQuery(id+"F25.imprint","IMPRINT",EDGE,{"disambiguationData":[TD([[subQ2,-1.0]])],"derivedFrom":subQ1}),-1.0]])]});}
            var Q221;
            {var subQ0=sQuery(id+"F25.wireOp",EDGE,"E257.trimOffspring");var subQ1=sQuery(id+"F25.wireOp",EDGE,"E235.top");var subQ2=makeQuery(id+"F25.imprint","INTERSECT",VERTEX,{"derivedFrom":[subQ1,subQ0]});Q221=makeQuery(id+"F25.imprint","IMPRINT",FACE,{"disambiguationData":[TD([[makeQuery(id+"F25.imprint","IMPRINT",EDGE,{"disambiguationData":[TD([[subQ2,-1.0]])],"derivedFrom":subQ1}),-1.0]])]});}
            var Q222;
            {var subQ0=sQuery(id+"F25.wireOp",EDGE,"E259.trimOffspring");var subQ1=sQuery(id+"F25.wireOp",EDGE,"E235.top");var subQ2=makeQuery(id+"F25.imprint","INTERSECT",VERTEX,{"derivedFrom":[subQ1,subQ0]});Q222=makeQuery(id+"F25.imprint","IMPRINT",FACE,{"disambiguationData":[TD([[makeQuery(id+"F25.imprint","IMPRINT",EDGE,{"disambiguationData":[TD([[subQ2,-1.0]])],"derivedFrom":subQ1}),-1.0]])]});}
            var Q223;
            {var subQ1=sQuery(id+"F25.wireOp",EDGE,"E235.top");var subQ3=sQuery(id+"F25.wireOp",EDGE,"E258.trimOffspring");var subQ4=makeQuery(id+"F25.imprint","INTERSECT",VERTEX,{"derivedFrom":[subQ1,subQ3]});Q223=makeQuery(id+"F25.imprint","IMPRINT",FACE,{"disambiguationData":[TD([[makeQuery(id+"F25.imprint","IMPRINT",EDGE,{"disambiguationData":[TD([[subQ4,1.0]])],"derivedFrom":subQ3}),-1.0]])]});}
            var Q224;
            {var subQ0=sQuery(id+"F25.wireOp",EDGE,"E257.trimOffspring");var subQ1=sQuery(id+"F25.wireOp",EDGE,"E235.top");var subQ2=makeQuery(id+"F25.imprint","INTERSECT",VERTEX,{"derivedFrom":[subQ1,subQ0]});Q224=makeQuery(id+"F25.imprint","IMPRINT",FACE,{"disambiguationData":[TD([[makeQuery(id+"F25.imprint","IMPRINT",EDGE,{"disambiguationData":[TD([[subQ2,-1.0]])],"derivedFrom":subQ1}),1.0]])]});}
            var Q225;
            {var subQ0=sQuery(id+"F25.wireOp",EDGE,"E259.trimOffspring");var subQ1=sQuery(id+"F25.wireOp",EDGE,"E235.top");var subQ2=makeQuery(id+"F25.imprint","INTERSECT",VERTEX,{"derivedFrom":[subQ1,subQ0]});Q225=makeQuery(id+"F25.imprint","IMPRINT",FACE,{"disambiguationData":[TD([[makeQuery(id+"F25.imprint","IMPRINT",EDGE,{"disambiguationData":[TD([[subQ2,-1.0]])],"derivedFrom":subQ1}),1.0]])]});}
            var Q226;
            {var subQ0=sQuery(id+"F25.wireOp",EDGE,"E499.trimOffspring");var subQ1=sQuery(id+"F25.wireOp",EDGE,"E257.trimOffspring");var subQ2=makeQuery(id+"F25.imprint","INTERSECT",VERTEX,{"derivedFrom":[subQ1,subQ0]});Q226=makeQuery(id+"F25.imprint","IMPRINT",FACE,{"disambiguationData":[TD([[makeQuery(id+"F25.imprint","IMPRINT",EDGE,{"disambiguationData":[TD([[subQ2,1.0]])],"derivedFrom":subQ1}),-1.0]])]});}
            var Q227;
            {var subQ0=sQuery(id+"F25.wireOp",EDGE,"E499.trimOffspring");var subQ1=sQuery(id+"F25.wireOp",EDGE,"E258.trimOffspring");var subQ2=makeQuery(id+"F25.imprint","INTERSECT",VERTEX,{"derivedFrom":[subQ1,subQ0]});Q227=makeQuery(id+"F25.imprint","IMPRINT",FACE,{"disambiguationData":[TD([[makeQuery(id+"F25.imprint","IMPRINT",EDGE,{"disambiguationData":[TD([[subQ2,1.0]])],"derivedFrom":subQ1}),1.0]])]});}
            var Q228;
            {var subQ0=sQuery(id+"F25.wireOp",EDGE,"E499.trimOffspring");var subQ1=sQuery(id+"F25.wireOp",EDGE,"E257.trimOffspring");var subQ2=makeQuery(id+"F25.imprint","INTERSECT",VERTEX,{"derivedFrom":[subQ1,subQ0]});Q228=makeQuery(id+"F25.imprint","IMPRINT",FACE,{"disambiguationData":[TD([[makeQuery(id+"F25.imprint","IMPRINT",EDGE,{"disambiguationData":[TD([[subQ2,-1.0]])],"derivedFrom":subQ1}),-1.0]])]});}
            var Q229;
            {var subQ0=sQuery(id+"F25.wireOp",EDGE,"E499.trimOffspring");var subQ1=sQuery(id+"F25.wireOp",EDGE,"E258.trimOffspring");var subQ2=makeQuery(id+"F25.imprint","INTERSECT",VERTEX,{"derivedFrom":[subQ1,subQ0]});Q229=makeQuery(id+"F25.imprint","IMPRINT",FACE,{"disambiguationData":[TD([[makeQuery(id+"F25.imprint","IMPRINT",EDGE,{"disambiguationData":[TD([[subQ2,-1.0]])],"derivedFrom":subQ1}),1.0]])]});}
            var Q230;
            {var subQ3=sQuery(id+"F25.wireOp",EDGE,"E497.trimOffspring");var subQ5=sQuery(id+"F25.wireOp",EDGE,"E259.trimOffspring");var subQ6=makeQuery(id+"F25.imprint","INTERSECT",VERTEX,{"derivedFrom":[subQ5,subQ3]});Q230=makeQuery(id+"F25.imprint","IMPRINT",FACE,{"disambiguationData":[TD([[makeQuery(id+"F25.imprint","IMPRINT",EDGE,{"disambiguationData":[TD([[subQ6,-1.0]])],"derivedFrom":subQ5}),1.0]])]});}
            var Q231;
            {var subQ0=sQuery(id+"F25.wireOp",EDGE,"E497.trimOffspring");var subQ1=sQuery(id+"F25.wireOp",EDGE,"E258.trimOffspring");var subQ2=makeQuery(id+"F25.imprint","INTERSECT",VERTEX,{"derivedFrom":[subQ1,subQ0]});Q231=makeQuery(id+"F25.imprint","IMPRINT",FACE,{"disambiguationData":[TD([[makeQuery(id+"F25.imprint","IMPRINT",EDGE,{"disambiguationData":[TD([[subQ2,-1.0]])],"derivedFrom":subQ1}),1.0]])]});}
            var Q232;
            {var subQ3=sQuery(id+"F25.wireOp",EDGE,"E496.trimOffspring");var subQ5=sQuery(id+"F25.wireOp",EDGE,"E259.trimOffspring");var subQ6=makeQuery(id+"F25.imprint","INTERSECT",VERTEX,{"derivedFrom":[subQ5,subQ3]});Q232=makeQuery(id+"F25.imprint","IMPRINT",FACE,{"disambiguationData":[TD([[makeQuery(id+"F25.imprint","IMPRINT",EDGE,{"disambiguationData":[TD([[subQ6,1.0]])],"derivedFrom":subQ5}),1.0]])]});}
            var Q233;
            {var subQ0=sQuery(id+"F25.wireOp",EDGE,"E496.trimOffspring");var subQ1=sQuery(id+"F25.wireOp",EDGE,"E258.trimOffspring");var subQ2=makeQuery(id+"F25.imprint","INTERSECT",VERTEX,{"derivedFrom":[subQ1,subQ0]});Q233=makeQuery(id+"F25.imprint","IMPRINT",FACE,{"disambiguationData":[TD([[makeQuery(id+"F25.imprint","IMPRINT",EDGE,{"disambiguationData":[TD([[subQ2,1.0]])],"derivedFrom":subQ1}),1.0]])]});}
            var Q234;
            {var subQ3=sQuery(id+"F25.wireOp",EDGE,"E504.trimOffspring");var subQ5=sQuery(id+"F25.wireOp",EDGE,"E261.trimOffspring");var subQ6=makeQuery(id+"F25.imprint","INTERSECT",VERTEX,{"derivedFrom":[subQ5,subQ3]});Q234=makeQuery(id+"F25.imprint","IMPRINT",FACE,{"disambiguationData":[TD([[makeQuery(id+"F25.imprint","IMPRINT",EDGE,{"disambiguationData":[TD([[subQ6,-1.0]])],"derivedFrom":subQ5}),1.0]])]});}
            var Q235;
            {var subQ0=sQuery(id+"F25.wireOp",EDGE,"E504.trimOffspring");var subQ1=sQuery(id+"F25.wireOp",EDGE,"E260.trimOffspring");var subQ2=makeQuery(id+"F25.imprint","INTERSECT",VERTEX,{"derivedFrom":[subQ1,subQ0]});Q235=makeQuery(id+"F25.imprint","IMPRINT",FACE,{"disambiguationData":[TD([[makeQuery(id+"F25.imprint","IMPRINT",EDGE,{"disambiguationData":[TD([[subQ2,-1.0]])],"derivedFrom":subQ1}),1.0]])]});}
            var Q236;
            {var subQ0=sQuery(id+"F25.wireOp",EDGE,"E504.trimOffspring");var subQ1=sQuery(id+"F25.wireOp",EDGE,"E260.trimOffspring");var subQ2=makeQuery(id+"F25.imprint","INTERSECT",VERTEX,{"derivedFrom":[subQ1,subQ0]});Q236=makeQuery(id+"F25.imprint","IMPRINT",FACE,{"disambiguationData":[TD([[makeQuery(id+"F25.imprint","IMPRINT",EDGE,{"disambiguationData":[TD([[subQ2,-1.0]])],"derivedFrom":subQ1}),-1.0]])]});}
            var Q237;
            {var subQ0=sQuery(id+"F25.wireOp",EDGE,"E503.trimOffspring");var subQ5=sQuery(id+"F25.wireOp",EDGE,"E261.trimOffspring");var subQ6=makeQuery(id+"F25.imprint","INTERSECT",VERTEX,{"derivedFrom":[subQ5,subQ0]});Q237=makeQuery(id+"F25.imprint","IMPRINT",FACE,{"disambiguationData":[TD([[makeQuery(id+"F25.imprint","IMPRINT",EDGE,{"disambiguationData":[TD([[subQ6,-1.0]])],"derivedFrom":subQ5}),1.0]])]});}
            var Q238;
            {var subQ0=sQuery(id+"F25.wireOp",EDGE,"E505.trimOffspring");var subQ1=sQuery(id+"F25.wireOp",EDGE,"E260.trimOffspring");var subQ2=makeQuery(id+"F25.imprint","INTERSECT",VERTEX,{"derivedFrom":[subQ1,subQ0]});Q238=makeQuery(id+"F25.imprint","IMPRINT",FACE,{"disambiguationData":[TD([[makeQuery(id+"F25.imprint","IMPRINT",EDGE,{"disambiguationData":[TD([[subQ2,1.0]])],"derivedFrom":subQ1}),1.0]])]});}
            var Q239;
            {var subQ0=sQuery(id+"F25.wireOp",EDGE,"E505.trimOffspring");var subQ1=sQuery(id+"F25.wireOp",EDGE,"E262.trimOffspring");var subQ2=makeQuery(id+"F25.imprint","INTERSECT",VERTEX,{"derivedFrom":[subQ1,subQ0]});Q239=makeQuery(id+"F25.imprint","IMPRINT",FACE,{"disambiguationData":[TD([[makeQuery(id+"F25.imprint","IMPRINT",EDGE,{"disambiguationData":[TD([[subQ2,-1.0]])],"derivedFrom":subQ1}),-1.0]])]});}
            var Q240;
            {var subQ0=sQuery(id+"F25.wireOp",EDGE,"E505.trimOffspring");var subQ1=sQuery(id+"F25.wireOp",EDGE,"E260.trimOffspring");var subQ2=makeQuery(id+"F25.imprint","INTERSECT",VERTEX,{"derivedFrom":[subQ1,subQ0]});Q240=makeQuery(id+"F25.imprint","IMPRINT",FACE,{"disambiguationData":[TD([[makeQuery(id+"F25.imprint","IMPRINT",EDGE,{"disambiguationData":[TD([[subQ2,-1.0]])],"derivedFrom":subQ1}),1.0]])]});}
            var Q241;
            {var subQ0=sQuery(id+"F25.wireOp",EDGE,"E511.trimOffspring");var subQ1=sQuery(id+"F25.wireOp",EDGE,"E262.trimOffspring");var subQ2=makeQuery(id+"F25.imprint","INTERSECT",VERTEX,{"derivedFrom":[subQ1,subQ0]});Q241=makeQuery(id+"F25.imprint","IMPRINT",FACE,{"disambiguationData":[TD([[makeQuery(id+"F25.imprint","IMPRINT",EDGE,{"disambiguationData":[TD([[subQ2,1.0]])],"derivedFrom":subQ1}),-1.0]])]});}
            var Q242;
            {var subQ0=sQuery(id+"F25.wireOp",EDGE,"E511.trimOffspring");var subQ1=sQuery(id+"F25.wireOp",EDGE,"E260.trimOffspring");var subQ2=makeQuery(id+"F25.imprint","INTERSECT",VERTEX,{"derivedFrom":[subQ1,subQ0]});Q242=makeQuery(id+"F25.imprint","IMPRINT",FACE,{"disambiguationData":[TD([[makeQuery(id+"F25.imprint","IMPRINT",EDGE,{"disambiguationData":[TD([[subQ2,1.0]])],"derivedFrom":subQ1}),1.0]])]});}
            var Q243;
            {var subQ0=sQuery(id+"F25.wireOp",EDGE,"E511.trimOffspring");var subQ1=sQuery(id+"F25.wireOp",EDGE,"E262.trimOffspring");var subQ2=makeQuery(id+"F25.imprint","INTERSECT",VERTEX,{"derivedFrom":[subQ1,subQ0]});Q243=makeQuery(id+"F25.imprint","IMPRINT",FACE,{"disambiguationData":[TD([[makeQuery(id+"F25.imprint","IMPRINT",EDGE,{"disambiguationData":[TD([[subQ2,-1.0]])],"derivedFrom":subQ1}),-1.0]])]});}
            var Q244;
            {var subQ0=sQuery(id+"F25.wireOp",EDGE,"E497.trimOffspring");var subQ1=sQuery(id+"F25.wireOp",EDGE,"E260.trimOffspring");var subQ2=makeQuery(id+"F25.imprint","INTERSECT",VERTEX,{"derivedFrom":[subQ1,subQ0]});Q244=makeQuery(id+"F25.imprint","IMPRINT",FACE,{"disambiguationData":[TD([[makeQuery(id+"F25.imprint","IMPRINT",EDGE,{"disambiguationData":[TD([[subQ2,1.0]])],"derivedFrom":subQ1}),1.0]])]});}
            var Q245;
            {var subQ0=sQuery(id+"F25.wireOp",EDGE,"E497.trimOffspring");var subQ1=sQuery(id+"F25.wireOp",EDGE,"E262.trimOffspring");var subQ2=makeQuery(id+"F25.imprint","INTERSECT",VERTEX,{"derivedFrom":[subQ1,subQ0]});Q245=makeQuery(id+"F25.imprint","IMPRINT",FACE,{"disambiguationData":[TD([[makeQuery(id+"F25.imprint","IMPRINT",EDGE,{"disambiguationData":[TD([[subQ2,-1.0]])],"derivedFrom":subQ1}),-1.0]])]});}
            var Q246;
            {var subQ0=sQuery(id+"F25.wireOp",EDGE,"E497.trimOffspring");var subQ1=sQuery(id+"F25.wireOp",EDGE,"E260.trimOffspring");var subQ2=makeQuery(id+"F25.imprint","INTERSECT",VERTEX,{"derivedFrom":[subQ1,subQ0]});Q246=makeQuery(id+"F25.imprint","IMPRINT",FACE,{"disambiguationData":[TD([[makeQuery(id+"F25.imprint","IMPRINT",EDGE,{"disambiguationData":[TD([[subQ2,-1.0]])],"derivedFrom":subQ1}),1.0]])]});}
            var Q247;
            {var subQ0=sQuery(id+"F25.wireOp",EDGE,"E496.trimOffspring");var subQ1=sQuery(id+"F25.wireOp",EDGE,"E262.trimOffspring");var subQ2=makeQuery(id+"F25.imprint","INTERSECT",VERTEX,{"derivedFrom":[subQ1,subQ0]});Q247=makeQuery(id+"F25.imprint","IMPRINT",FACE,{"disambiguationData":[TD([[makeQuery(id+"F25.imprint","IMPRINT",EDGE,{"disambiguationData":[TD([[subQ2,1.0]])],"derivedFrom":subQ1}),-1.0]])]});}
            var Q248;
            {var subQ0=sQuery(id+"F25.wireOp",EDGE,"E496.trimOffspring");var subQ1=sQuery(id+"F25.wireOp",EDGE,"E260.trimOffspring");var subQ2=makeQuery(id+"F25.imprint","INTERSECT",VERTEX,{"derivedFrom":[subQ1,subQ0]});Q248=makeQuery(id+"F25.imprint","IMPRINT",FACE,{"disambiguationData":[TD([[makeQuery(id+"F25.imprint","IMPRINT",EDGE,{"disambiguationData":[TD([[subQ2,1.0]])],"derivedFrom":subQ1}),1.0]])]});}
            var Q249;
            {var subQ0=sQuery(id+"F25.wireOp",EDGE,"E529.trimOffspring");var subQ1=sQuery(id+"F25.wireOp",EDGE,"E503.trimOffspring");var subQ2=makeQuery(id+"F25.imprint","INTERSECT",VERTEX,{"derivedFrom":[subQ1,subQ0]});Q249=makeQuery(id+"F25.imprint","IMPRINT",FACE,{"disambiguationData":[TD([[makeQuery(id+"F25.imprint","IMPRINT",EDGE,{"disambiguationData":[TD([[subQ2,-1.0]])],"derivedFrom":subQ1}),-1.0]])]});}
            var Q250;
            {var subQ0=sQuery(id+"F25.wireOp",EDGE,"E529.trimOffspring");var subQ1=sQuery(id+"F25.wireOp",EDGE,"E503.trimOffspring");var subQ2=makeQuery(id+"F25.imprint","INTERSECT",VERTEX,{"derivedFrom":[subQ1,subQ0]});Q250=makeQuery(id+"F25.imprint","IMPRINT",FACE,{"disambiguationData":[TD([[makeQuery(id+"F25.imprint","IMPRINT",EDGE,{"disambiguationData":[TD([[subQ2,-1.0]])],"derivedFrom":subQ1}),1.0]])]});}
            var Q251;
            {var subQ0=sQuery(id+"F25.wireOp",EDGE,"E529.trimOffspring");var subQ1=sQuery(id+"F25.wireOp",EDGE,"E507.trimOffspring");var subQ2=makeQuery(id+"F25.imprint","INTERSECT",VERTEX,{"derivedFrom":[subQ1,subQ0]});Q251=makeQuery(id+"F25.imprint","IMPRINT",FACE,{"disambiguationData":[TD([[makeQuery(id+"F25.imprint","IMPRINT",EDGE,{"disambiguationData":[TD([[subQ2,-1.0]])],"derivedFrom":subQ1}),1.0]])]});}
            var Q252;
            {var subQ0=sQuery(id+"F25.wireOp",EDGE,"E529.trimOffspring");var subQ1=sQuery(id+"F25.wireOp",EDGE,"E510.trimOffspring");var subQ2=makeQuery(id+"F25.imprint","INTERSECT",VERTEX,{"derivedFrom":[subQ1,subQ0]});Q252=makeQuery(id+"F25.imprint","IMPRINT",FACE,{"disambiguationData":[TD([[makeQuery(id+"F25.imprint","IMPRINT",EDGE,{"disambiguationData":[TD([[subQ2,-1.0]])],"derivedFrom":subQ1}),-1.0]])]});}
            var Q253;
            {var subQ0=sQuery(id+"F25.wireOp",EDGE,"E530.trimOffspring");var subQ1=sQuery(id+"F25.wireOp",EDGE,"E510.trimOffspring");var subQ2=makeQuery(id+"F25.imprint","INTERSECT",VERTEX,{"derivedFrom":[subQ1,subQ0]});Q253=makeQuery(id+"F25.imprint","IMPRINT",FACE,{"disambiguationData":[TD([[makeQuery(id+"F25.imprint","IMPRINT",EDGE,{"disambiguationData":[TD([[subQ2,-1.0]])],"derivedFrom":subQ1}),-1.0]])]});}
            var Q254;
            {var subQ0=sQuery(id+"F25.wireOp",EDGE,"E531.trimOffspring");var subQ1=sQuery(id+"F25.wireOp",EDGE,"E510.trimOffspring");var subQ2=makeQuery(id+"F25.imprint","INTERSECT",VERTEX,{"derivedFrom":[subQ1,subQ0]});Q254=makeQuery(id+"F25.imprint","IMPRINT",FACE,{"disambiguationData":[TD([[makeQuery(id+"F25.imprint","IMPRINT",EDGE,{"disambiguationData":[TD([[subQ2,-1.0]])],"derivedFrom":subQ1}),-1.0]])]});}
            var Q255;
            {var subQ0=sQuery(id+"F25.wireOp",EDGE,"E532.trimOffspring");var subQ1=sQuery(id+"F25.wireOp",EDGE,"E510.trimOffspring");var subQ2=makeQuery(id+"F25.imprint","INTERSECT",VERTEX,{"derivedFrom":[subQ1,subQ0]});Q255=makeQuery(id+"F25.imprint","IMPRINT",FACE,{"disambiguationData":[TD([[makeQuery(id+"F25.imprint","IMPRINT",EDGE,{"disambiguationData":[TD([[subQ2,-1.0]])],"derivedFrom":subQ1}),1.0]])]});}
            var Q256;
            {var subQ0=sQuery(id+"F25.wireOp",EDGE,"E527.trimOffspring");var subQ1=sQuery(id+"F25.wireOp",EDGE,"E510.trimOffspring");var subQ2=makeQuery(id+"F25.imprint","INTERSECT",VERTEX,{"derivedFrom":[subQ1,subQ0]});Q256=makeQuery(id+"F25.imprint","IMPRINT",FACE,{"disambiguationData":[TD([[makeQuery(id+"F25.imprint","IMPRINT",EDGE,{"disambiguationData":[TD([[subQ2,-1.0]])],"derivedFrom":subQ1}),1.0]])]});}
            var Q257;
            {var subQ0=sQuery(id+"F25.wireOp",EDGE,"E532.trimOffspring");var subQ1=sQuery(id+"F25.wireOp",EDGE,"E509.trimOffspring");var subQ2=makeQuery(id+"F25.imprint","INTERSECT",VERTEX,{"derivedFrom":[subQ1,subQ0]});Q257=makeQuery(id+"F25.imprint","IMPRINT",FACE,{"disambiguationData":[TD([[makeQuery(id+"F25.imprint","IMPRINT",EDGE,{"disambiguationData":[TD([[subQ2,-1.0]])],"derivedFrom":subQ1}),-1.0]])]});}
            var Q258;
            {var subQ0=sQuery(id+"F25.wireOp",EDGE,"E533.trimOffspring");var subQ1=sQuery(id+"F25.wireOp",EDGE,"E509.trimOffspring");var subQ2=makeQuery(id+"F25.imprint","INTERSECT",VERTEX,{"derivedFrom":[subQ1,subQ0]});Q258=makeQuery(id+"F25.imprint","IMPRINT",FACE,{"disambiguationData":[TD([[makeQuery(id+"F25.imprint","IMPRINT",EDGE,{"disambiguationData":[TD([[subQ2,1.0]])],"derivedFrom":subQ1}),-1.0]])]});}
            var Q259;
            {var subQ0=sQuery(id+"F25.wireOp",EDGE,"E533.trimOffspring");var subQ1=sQuery(id+"F25.wireOp",EDGE,"E509.trimOffspring");var subQ2=makeQuery(id+"F25.imprint","INTERSECT",VERTEX,{"derivedFrom":[subQ1,subQ0]});Q259=makeQuery(id+"F25.imprint","IMPRINT",FACE,{"disambiguationData":[TD([[makeQuery(id+"F25.imprint","IMPRINT",EDGE,{"disambiguationData":[TD([[subQ2,1.0]])],"derivedFrom":subQ1}),1.0]])]});}
            var Q260;
            {var subQ0=sQuery(id+"F25.wireOp",EDGE,"E532.trimOffspring");var subQ1=sQuery(id+"F25.wireOp",EDGE,"E509.trimOffspring");var subQ2=makeQuery(id+"F25.imprint","INTERSECT",VERTEX,{"derivedFrom":[subQ1,subQ0]});Q260=makeQuery(id+"F25.imprint","IMPRINT",FACE,{"disambiguationData":[TD([[makeQuery(id+"F25.imprint","IMPRINT",EDGE,{"disambiguationData":[TD([[subQ2,-1.0]])],"derivedFrom":subQ1}),1.0]])]});}
            var Q261;
            {var subQ0=sQuery(id+"F25.wireOp",EDGE,"E516.trimOffspring");var subQ1=sQuery(id+"F25.wireOp",EDGE,"E509.trimOffspring");var subQ2=makeQuery(id+"F25.imprint","INTERSECT",VERTEX,{"derivedFrom":[subQ1,subQ0]});Q261=makeQuery(id+"F25.imprint","IMPRINT",FACE,{"disambiguationData":[TD([[makeQuery(id+"F25.imprint","IMPRINT",EDGE,{"disambiguationData":[TD([[subQ2,-1.0]])],"derivedFrom":subQ1}),-1.0]])]});}
            var Q262;
            {var subQ3=sQuery(id+"F25.wireOp",EDGE,"E516.trimOffspring");var subQ5=sQuery(id+"F25.wireOp",EDGE,"E509.trimOffspring");var subQ6=makeQuery(id+"F25.imprint","INTERSECT",VERTEX,{"derivedFrom":[subQ5,subQ3]});Q262=makeQuery(id+"F25.imprint","IMPRINT",FACE,{"disambiguationData":[TD([[makeQuery(id+"F25.imprint","IMPRINT",EDGE,{"disambiguationData":[TD([[subQ6,-1.0]])],"derivedFrom":subQ5}),1.0]])]});}
            var Q263;
            {var subQ0=sQuery(id+"F25.wireOp",EDGE,"E514.trimOffspring");var subQ1=sQuery(id+"F25.wireOp",EDGE,"E508.trimOffspring");var subQ2=makeQuery(id+"F25.imprint","INTERSECT",VERTEX,{"derivedFrom":[subQ1,subQ0]});Q263=makeQuery(id+"F25.imprint","IMPRINT",FACE,{"disambiguationData":[TD([[makeQuery(id+"F25.imprint","IMPRINT",EDGE,{"disambiguationData":[TD([[subQ2,-1.0]])],"derivedFrom":subQ1}),-1.0]])]});}
            var Q264;
            {var subQ0=sQuery(id+"F25.wireOp",EDGE,"E514.trimOffspring");var subQ1=sQuery(id+"F25.wireOp",EDGE,"E509.trimOffspring");var subQ2=makeQuery(id+"F25.imprint","INTERSECT",VERTEX,{"derivedFrom":[subQ1,subQ0]});Q264=makeQuery(id+"F25.imprint","IMPRINT",FACE,{"disambiguationData":[TD([[makeQuery(id+"F25.imprint","IMPRINT",EDGE,{"disambiguationData":[TD([[subQ2,-1.0]])],"derivedFrom":subQ1}),-1.0]])]});}
            var Q265;
            {var subQ0=sQuery(id+"F25.wireOp",EDGE,"E515.trimOffspring");var subQ1=sQuery(id+"F25.wireOp",EDGE,"E509.trimOffspring");var subQ2=makeQuery(id+"F25.imprint","INTERSECT",VERTEX,{"derivedFrom":[subQ1,subQ0]});Q265=makeQuery(id+"F25.imprint","IMPRINT",FACE,{"disambiguationData":[TD([[makeQuery(id+"F25.imprint","IMPRINT",EDGE,{"disambiguationData":[TD([[subQ2,-1.0]])],"derivedFrom":subQ1}),-1.0]])]});}
            var Q266;
            {var subQ0=sQuery(id+"F25.wireOp",EDGE,"E515.trimOffspring");var subQ1=sQuery(id+"F25.wireOp",EDGE,"E508.trimOffspring");var subQ2=makeQuery(id+"F25.imprint","INTERSECT",VERTEX,{"derivedFrom":[subQ1,subQ0]});Q266=makeQuery(id+"F25.imprint","IMPRINT",FACE,{"disambiguationData":[TD([[makeQuery(id+"F25.imprint","IMPRINT",EDGE,{"disambiguationData":[TD([[subQ2,-1.0]])],"derivedFrom":subQ1}),-1.0]])]});}
            var Q267;
            {var subQ0=sQuery(id+"F25.wireOp",EDGE,"E263.trimOffspring");Q267=makeQuery(id+"F25.imprint","IMPRINT",FACE,{"disambiguationData":[TD([[makeQuery(id+"F25.imprint","IMPRINT",EDGE,{"derivedFrom":subQ0}),-1.0]])]});}
            var Q268;
            {var subQ0=sQuery(id+"F25.wireOp",EDGE,"E515.trimOffspring");var subQ1=sQuery(id+"F25.wireOp",EDGE,"E508.trimOffspring");var subQ2=makeQuery(id+"F25.imprint","INTERSECT",VERTEX,{"derivedFrom":[subQ1,subQ0]});Q268=makeQuery(id+"F25.imprint","IMPRINT",FACE,{"disambiguationData":[TD([[makeQuery(id+"F25.imprint","IMPRINT",EDGE,{"disambiguationData":[TD([[subQ2,-1.0]])],"derivedFrom":subQ1}),1.0]])]});}
            var Q269;
            {var subQ0=sQuery(id+"F25.wireOp",EDGE,"E263.trimOffspring");Q269=makeQuery(id+"F25.imprint","IMPRINT",FACE,{"disambiguationData":[TD([[makeQuery(id+"F25.imprint","IMPRINT",EDGE,{"derivedFrom":subQ0}),1.0]])]});}
            var Q270;
            {var subQ0=sQuery(id+"F25.wireOp",EDGE,"E514.trimOffspring");var subQ1=sQuery(id+"F25.wireOp",EDGE,"E264.trimOffspring");var subQ2=makeQuery(id+"F25.imprint","INTERSECT",VERTEX,{"derivedFrom":[subQ1,subQ0]});Q270=makeQuery(id+"F25.imprint","IMPRINT",FACE,{"disambiguationData":[TD([[makeQuery(id+"F25.imprint","IMPRINT",EDGE,{"disambiguationData":[TD([[subQ2,-1.0]])],"derivedFrom":subQ1}),-1.0]])]});}
            var Q271;
            {var subQ0=sQuery(id+"F25.wireOp",EDGE,"E515.trimOffspring");var subQ1=sQuery(id+"F25.wireOp",EDGE,"E266.trimOffspring");var subQ2=makeQuery(id+"F25.imprint","INTERSECT",VERTEX,{"derivedFrom":[subQ1,subQ0]});Q271=makeQuery(id+"F25.imprint","IMPRINT",FACE,{"disambiguationData":[TD([[makeQuery(id+"F25.imprint","IMPRINT",EDGE,{"disambiguationData":[TD([[subQ2,-1.0]])],"derivedFrom":subQ1}),-1.0]])]});}
            var Q272;
            {var subQ0=sQuery(id+"F25.wireOp",EDGE,"E515.trimOffspring");var subQ1=sQuery(id+"F25.wireOp",EDGE,"E264.trimOffspring");var subQ2=makeQuery(id+"F25.imprint","INTERSECT",VERTEX,{"derivedFrom":[subQ1,subQ0]});Q272=makeQuery(id+"F25.imprint","IMPRINT",FACE,{"disambiguationData":[TD([[makeQuery(id+"F25.imprint","IMPRINT",EDGE,{"disambiguationData":[TD([[subQ2,-1.0]])],"derivedFrom":subQ1}),-1.0]])]});}
            var Q273;
            {var subQ0=sQuery(id+"F25.wireOp",EDGE,"E516.trimOffspring");var subQ1=sQuery(id+"F25.wireOp",EDGE,"E266.trimOffspring");var subQ2=makeQuery(id+"F25.imprint","INTERSECT",VERTEX,{"derivedFrom":[subQ1,subQ0]});Q273=makeQuery(id+"F25.imprint","IMPRINT",FACE,{"disambiguationData":[TD([[makeQuery(id+"F25.imprint","IMPRINT",EDGE,{"disambiguationData":[TD([[subQ2,-1.0]])],"derivedFrom":subQ1}),-1.0]])]});}
            var Q274;
            {var subQ0=sQuery(id+"F25.wireOp",EDGE,"E516.trimOffspring");var subQ1=sQuery(id+"F25.wireOp",EDGE,"E264.trimOffspring");var subQ2=makeQuery(id+"F25.imprint","INTERSECT",VERTEX,{"derivedFrom":[subQ1,subQ0]});Q274=makeQuery(id+"F25.imprint","IMPRINT",FACE,{"disambiguationData":[TD([[makeQuery(id+"F25.imprint","IMPRINT",EDGE,{"disambiguationData":[TD([[subQ2,-1.0]])],"derivedFrom":subQ1}),-1.0]])]});}
            var Q275;
            {var subQ0=sQuery(id+"F25.wireOp",EDGE,"E532.trimOffspring");var subQ1=sQuery(id+"F25.wireOp",EDGE,"E266.trimOffspring");var subQ2=makeQuery(id+"F25.imprint","INTERSECT",VERTEX,{"derivedFrom":[subQ1,subQ0]});Q275=makeQuery(id+"F25.imprint","IMPRINT",FACE,{"disambiguationData":[TD([[makeQuery(id+"F25.imprint","IMPRINT",EDGE,{"disambiguationData":[TD([[subQ2,-1.0]])],"derivedFrom":subQ1}),-1.0]])]});}
            var Q276;
            {var subQ0=sQuery(id+"F25.wireOp",EDGE,"E532.trimOffspring");var subQ1=sQuery(id+"F25.wireOp",EDGE,"E264.trimOffspring");var subQ2=makeQuery(id+"F25.imprint","INTERSECT",VERTEX,{"derivedFrom":[subQ1,subQ0]});Q276=makeQuery(id+"F25.imprint","IMPRINT",FACE,{"disambiguationData":[TD([[makeQuery(id+"F25.imprint","IMPRINT",EDGE,{"disambiguationData":[TD([[subQ2,-1.0]])],"derivedFrom":subQ1}),-1.0]])]});}
            var Q277;
            {var subQ0=sQuery(id+"F25.wireOp",EDGE,"E527.trimOffspring");var subQ1=sQuery(id+"F25.wireOp",EDGE,"E266.trimOffspring");var subQ2=makeQuery(id+"F25.imprint","INTERSECT",VERTEX,{"derivedFrom":[subQ1,subQ0]});Q277=makeQuery(id+"F25.imprint","IMPRINT",FACE,{"disambiguationData":[TD([[makeQuery(id+"F25.imprint","IMPRINT",EDGE,{"disambiguationData":[TD([[subQ2,-1.0]])],"derivedFrom":subQ1}),-1.0]])]});}
            var Q278;
            {var subQ0=sQuery(id+"F25.wireOp",EDGE,"E527.trimOffspring");var subQ1=sQuery(id+"F25.wireOp",EDGE,"E264.trimOffspring");var subQ2=makeQuery(id+"F25.imprint","INTERSECT",VERTEX,{"derivedFrom":[subQ1,subQ0]});Q278=makeQuery(id+"F25.imprint","IMPRINT",FACE,{"disambiguationData":[TD([[makeQuery(id+"F25.imprint","IMPRINT",EDGE,{"disambiguationData":[TD([[subQ2,-1.0]])],"derivedFrom":subQ1}),-1.0]])]});}
            var Q279;
            {var subQ0=sQuery(id+"F25.wireOp",EDGE,"E533.trimOffspring");var subQ1=sQuery(id+"F25.wireOp",EDGE,"E266.trimOffspring");var subQ2=makeQuery(id+"F25.imprint","INTERSECT",VERTEX,{"derivedFrom":[subQ1,subQ0]});Q279=makeQuery(id+"F25.imprint","IMPRINT",FACE,{"disambiguationData":[TD([[makeQuery(id+"F25.imprint","IMPRINT",EDGE,{"disambiguationData":[TD([[subQ2,-1.0]])],"derivedFrom":subQ1}),-1.0]])]});}
            var Q280;
            {var subQ0=sQuery(id+"F25.wireOp",EDGE,"E533.trimOffspring");var subQ1=sQuery(id+"F25.wireOp",EDGE,"E264.trimOffspring");var subQ2=makeQuery(id+"F25.imprint","INTERSECT",VERTEX,{"derivedFrom":[subQ1,subQ0]});Q280=makeQuery(id+"F25.imprint","IMPRINT",FACE,{"disambiguationData":[TD([[makeQuery(id+"F25.imprint","IMPRINT",EDGE,{"disambiguationData":[TD([[subQ2,-1.0]])],"derivedFrom":subQ1}),-1.0]])]});}
            var Q281;
            {var subQ0=sQuery(id+"F25.wireOp",EDGE,"E538.trimOffspring");var subQ1=sQuery(id+"F25.wireOp",EDGE,"E266.trimOffspring");var subQ2=makeQuery(id+"F25.imprint","INTERSECT",VERTEX,{"derivedFrom":[subQ1,subQ0]});Q281=makeQuery(id+"F25.imprint","IMPRINT",FACE,{"disambiguationData":[TD([[makeQuery(id+"F25.imprint","IMPRINT",EDGE,{"disambiguationData":[TD([[subQ2,-1.0]])],"derivedFrom":subQ1}),-1.0]])]});}
            var Q282;
            {var subQ0=sQuery(id+"F25.wireOp",EDGE,"E542.trimOffspring");var subQ1=sQuery(id+"F25.wireOp",EDGE,"E266.trimOffspring");var subQ2=makeQuery(id+"F25.imprint","INTERSECT",VERTEX,{"derivedFrom":[subQ1,subQ0]});Q282=makeQuery(id+"F25.imprint","IMPRINT",FACE,{"disambiguationData":[TD([[makeQuery(id+"F25.imprint","IMPRINT",EDGE,{"disambiguationData":[TD([[subQ2,1.0]])],"derivedFrom":subQ1}),-1.0]])]});}
            var Q283;
            {var subQ0=sQuery(id+"F25.wireOp",EDGE,"E538.trimOffspring");var subQ1=sQuery(id+"F25.wireOp",EDGE,"E264.trimOffspring");var subQ2=makeQuery(id+"F25.imprint","INTERSECT",VERTEX,{"derivedFrom":[subQ1,subQ0]});Q283=makeQuery(id+"F25.imprint","IMPRINT",FACE,{"disambiguationData":[TD([[makeQuery(id+"F25.imprint","IMPRINT",EDGE,{"disambiguationData":[TD([[subQ2,-1.0]])],"derivedFrom":subQ1}),-1.0]])]});}
            var Q284;
            {var subQ0=sQuery(id+"F25.wireOp",EDGE,"E542.trimOffspring");var subQ1=sQuery(id+"F25.wireOp",EDGE,"E264.trimOffspring");var subQ2=makeQuery(id+"F25.imprint","INTERSECT",VERTEX,{"derivedFrom":[subQ1,subQ0]});Q284=makeQuery(id+"F25.imprint","IMPRINT",FACE,{"disambiguationData":[TD([[makeQuery(id+"F25.imprint","IMPRINT",EDGE,{"disambiguationData":[TD([[subQ2,1.0]])],"derivedFrom":subQ1}),-1.0]])]});}
            var Q285;
            {var subQ0=sQuery(id+"F25.wireOp",EDGE,"E243.top");Q285=makeQuery(id+"F25.imprint","IMPRINT",FACE,{"disambiguationData":[TD([[makeQuery(id+"F25.imprint","IMPRINT",EDGE,{"derivedFrom":subQ0}),1.0]])]});}
            var Q286;
            {var subQ0=sQuery(id+"F25.wireOp",EDGE,"E244.top");Q286=makeQuery(id+"F25.imprint","IMPRINT",FACE,{"disambiguationData":[TD([[makeQuery(id+"F25.imprint","IMPRINT",EDGE,{"derivedFrom":subQ0}),-1.0]])]});}
            var Q287;
            {var subQ0=sQuery(id+"F25.wireOp",EDGE,"E516.trimOffspring");var subQ5=sQuery(id+"F25.wireOp",EDGE,"E265.trimOffspring");var subQ6=makeQuery(id+"F25.imprint","INTERSECT",VERTEX,{"derivedFrom":[subQ5,subQ0]});Q287=makeQuery(id+"F25.imprint","IMPRINT",FACE,{"disambiguationData":[TD([[makeQuery(id+"F25.imprint","IMPRINT",EDGE,{"disambiguationData":[TD([[subQ6,-1.0]])],"derivedFrom":subQ5}),1.0]])]});}
            var Q288;
            {var subQ0=sQuery(id+"F25.wireOp",EDGE,"E243.top");Q288=makeQuery(id+"F25.imprint","IMPRINT",FACE,{"disambiguationData":[TD([[makeQuery(id+"F25.imprint","IMPRINT",EDGE,{"derivedFrom":subQ0}),-1.0]])]});}
            var Q289;
            {var subQ0=sQuery(id+"F25.wireOp",EDGE,"E244.top");Q289=makeQuery(id+"F25.imprint","IMPRINT",FACE,{"disambiguationData":[TD([[makeQuery(id+"F25.imprint","IMPRINT",EDGE,{"derivedFrom":subQ0}),1.0]])]});}
            var Q290;
            {var subQ0=sQuery(id+"F25.wireOp",EDGE,"E574.trimOffspring");var subQ5=sQuery(id+"F25.wireOp",EDGE,"E414.MirrorCS");var subQ6=makeQuery(id+"F25.imprint","INTERSECT",VERTEX,{"derivedFrom":[subQ5,subQ0]});Q290=makeQuery(id+"F25.imprint","IMPRINT",FACE,{"disambiguationData":[TD([[makeQuery(id+"F25.imprint","IMPRINT",EDGE,{"disambiguationData":[TD([[subQ6,-1.0]])],"derivedFrom":subQ5}),-1.0]])]});}
            var Q291;
            {var subQ0=sQuery(id+"F25.wireOp",EDGE,"E245.top");Q291=makeQuery(id+"F25.imprint","IMPRINT",FACE,{"disambiguationData":[TD([[makeQuery(id+"F25.imprint","IMPRINT",EDGE,{"derivedFrom":subQ0}),1.0]])]});}
            var Q292;
            {var subQ0=sQuery(id+"F25.wireOp",EDGE,"E245.top");Q292=makeQuery(id+"F25.imprint","IMPRINT",FACE,{"disambiguationData":[TD([[makeQuery(id+"F25.imprint","IMPRINT",EDGE,{"derivedFrom":subQ0}),-1.0]])]});}
            var Q293;
            {var subQ0=sQuery(id+"F25.wireOp",EDGE,"E246.top");Q293=makeQuery(id+"F25.imprint","IMPRINT",FACE,{"disambiguationData":[TD([[makeQuery(id+"F25.imprint","IMPRINT",EDGE,{"derivedFrom":subQ0}),-1.0]])]});}
            var Q294;
            {var subQ0=sQuery(id+"F25.wireOp",EDGE,"E246.top");Q294=makeQuery(id+"F25.imprint","IMPRINT",FACE,{"disambiguationData":[TD([[makeQuery(id+"F25.imprint","IMPRINT",EDGE,{"derivedFrom":subQ0}),1.0]])]});}
            var Q295;
            {var subQ0=sQuery(id+"F25.wireOp",EDGE,"E533.trimOffspring");var subQ5=sQuery(id+"F25.wireOp",EDGE,"E265.trimOffspring");var subQ6=makeQuery(id+"F25.imprint","INTERSECT",VERTEX,{"derivedFrom":[subQ5,subQ0]});Q295=makeQuery(id+"F25.imprint","IMPRINT",FACE,{"disambiguationData":[TD([[makeQuery(id+"F25.imprint","IMPRINT",EDGE,{"disambiguationData":[TD([[subQ6,-1.0]])],"derivedFrom":subQ5}),1.0]])]});}
            var Q296;
            {var subQ0=sQuery(id+"F25.wireOp",EDGE,"E581.trimOffspring");var subQ5=sQuery(id+"F25.wireOp",EDGE,"E414.MirrorCS");var subQ6=makeQuery(id+"F25.imprint","INTERSECT",VERTEX,{"derivedFrom":[subQ5,subQ0]});Q296=makeQuery(id+"F25.imprint","IMPRINT",FACE,{"disambiguationData":[TD([[makeQuery(id+"F25.imprint","IMPRINT",EDGE,{"disambiguationData":[TD([[subQ6,-1.0]])],"derivedFrom":subQ5}),-1.0]])]});}
            var Q297;
            {var subQ0=sQuery(id+"F25.wireOp",EDGE,"E247.top");Q297=makeQuery(id+"F25.imprint","IMPRINT",FACE,{"disambiguationData":[TD([[makeQuery(id+"F25.imprint","IMPRINT",EDGE,{"derivedFrom":subQ0}),-1.0]])]});}
            var Q298;
            {var subQ0=sQuery(id+"F25.wireOp",EDGE,"E247.top");Q298=makeQuery(id+"F25.imprint","IMPRINT",FACE,{"disambiguationData":[TD([[makeQuery(id+"F25.imprint","IMPRINT",EDGE,{"derivedFrom":subQ0}),1.0]])]});}
            var Q299;
            {var subQ5=sQuery(id+"F25.wireOp",EDGE,"E248.top");Q299=makeQuery(id+"F25.imprint","IMPRINT",FACE,{"disambiguationData":[TD([[makeQuery(id+"F25.imprint","IMPRINT",EDGE,{"derivedFrom":subQ5}),-1.0]])]});}
            var Q300;
            {var subQ0=sQuery(id+"F25.wireOp",EDGE,"E410.MirrorCS");Q300=makeQuery(id+"F25.imprint","IMPRINT",FACE,{"disambiguationData":[TD([[makeQuery(id+"F25.imprint","IMPRINT",EDGE,{"derivedFrom":subQ0}),1.0]])]});}
            var Q301;
            {var subQ0=sQuery(id+"F25.wireOp",EDGE,"E470.MirrorCS");var subQ1=sQuery(id+"F25.wireOp",EDGE,"E428.MirrorCS");var subQ2=makeQuery(id+"F25.imprint","INTERSECT",VERTEX,{"derivedFrom":[subQ1,subQ0]});Q301=makeQuery(id+"F25.imprint","IMPRINT",FACE,{"disambiguationData":[TD([[makeQuery(id+"F25.imprint","IMPRINT",EDGE,{"disambiguationData":[TD([[subQ2,-1.0]])],"derivedFrom":subQ1}),1.0]])]});}
            var Q302;
            {var subQ0=sQuery(id+"F25.wireOp",EDGE,"E452.MirrorCS");var subQ1=sQuery(id+"F25.wireOp",EDGE,"E428.MirrorCS");var subQ2=makeQuery(id+"F25.imprint","INTERSECT",VERTEX,{"derivedFrom":[subQ1,subQ0]});Q302=makeQuery(id+"F25.imprint","IMPRINT",FACE,{"disambiguationData":[TD([[makeQuery(id+"F25.imprint","IMPRINT",EDGE,{"disambiguationData":[TD([[subQ2,1.0]])],"derivedFrom":subQ1}),1.0]])]});}
            var Q303;
            {var subQ3=sQuery(id+"F25.wireOp",EDGE,"E471.MirrorCS");Q303=makeQuery(id+"F25.imprint","IMPRINT",FACE,{"disambiguationData":[TD([[makeQuery(id+"F25.imprint","IMPRINT",EDGE,{"derivedFrom":subQ3}),1.0]])]});}
            var Q304;
            {var subQ3=sQuery(id+"F25.wireOp",EDGE,"E471.MirrorCS");Q304=makeQuery(id+"F25.imprint","IMPRINT",FACE,{"disambiguationData":[TD([[makeQuery(id+"F25.imprint","IMPRINT",EDGE,{"derivedFrom":subQ3}),-1.0]])]});}
            var Q305;
            {var subQ0=sQuery(id+"F25.wireOp",EDGE,"E460.MirrorCS");var subQ1=sQuery(id+"F25.wireOp",EDGE,"E428.MirrorCS");var subQ2=makeQuery(id+"F25.imprint","INTERSECT",VERTEX,{"derivedFrom":[subQ1,subQ0]});Q305=makeQuery(id+"F25.imprint","IMPRINT",FACE,{"disambiguationData":[TD([[makeQuery(id+"F25.imprint","IMPRINT",EDGE,{"disambiguationData":[TD([[subQ2,1.0]])],"derivedFrom":subQ1}),1.0]])]});}
            var Q306;
            {var subQ0=sQuery(id+"F25.wireOp",EDGE,"E432.MirrorCS");Q306=makeQuery(id+"F25.imprint","IMPRINT",FACE,{"disambiguationData":[TD([[makeQuery(id+"F25.imprint","IMPRINT",EDGE,{"derivedFrom":subQ0}),-1.0]])]});}
            var Q307;
            {var subQ0=sQuery(id+"F25.wireOp",EDGE,"E453.MirrorCS");Q307=makeQuery(id+"F25.imprint","IMPRINT",FACE,{"disambiguationData":[TD([[makeQuery(id+"F25.imprint","IMPRINT",EDGE,{"derivedFrom":subQ0}),-1.0]])]});}
            var Q308;
            {var subQ0=sQuery(id+"F25.wireOp",EDGE,"E452.MirrorCS");var subQ1=sQuery(id+"F25.wireOp",EDGE,"E425.MirrorCS");var subQ2=makeQuery(id+"F25.imprint","INTERSECT",VERTEX,{"derivedFrom":[subQ1,subQ0]});Q308=makeQuery(id+"F25.imprint","IMPRINT",FACE,{"disambiguationData":[TD([[makeQuery(id+"F25.imprint","IMPRINT",EDGE,{"disambiguationData":[TD([[subQ2,1.0]])],"derivedFrom":subQ1}),-1.0]])]});}
            var Q309;
            {var subQ0=sQuery(id+"F25.wireOp",EDGE,"E430.MirrorCS");Q309=makeQuery(id+"F25.imprint","IMPRINT",FACE,{"disambiguationData":[TD([[makeQuery(id+"F25.imprint","IMPRINT",EDGE,{"derivedFrom":subQ0}),1.0]])]});}
            var Q310;
            {var subQ0=sQuery(id+"F25.wireOp",EDGE,"E430.MirrorCS");Q310=makeQuery(id+"F25.imprint","IMPRINT",FACE,{"disambiguationData":[TD([[makeQuery(id+"F25.imprint","IMPRINT",EDGE,{"derivedFrom":subQ0}),-1.0]])]});}
            var Q311;
            {var subQ0=sQuery(id+"F25.wireOp",EDGE,"E442.MirrorCS");var subQ1=sQuery(id+"F25.wireOp",EDGE,"E425.MirrorCS");var subQ2=makeQuery(id+"F25.imprint","INTERSECT",VERTEX,{"derivedFrom":[subQ1,subQ0]});Q311=makeQuery(id+"F25.imprint","IMPRINT",FACE,{"disambiguationData":[TD([[makeQuery(id+"F25.imprint","IMPRINT",EDGE,{"disambiguationData":[TD([[subQ2,-1.0]])],"derivedFrom":subQ1}),-1.0]])]});}
            var Q312;
            {var subQ0=sQuery(id+"F25.wireOp",EDGE,"E464.MirrorCS");var subQ1=sQuery(id+"F25.wireOp",EDGE,"E428.MirrorCS");var subQ2=makeQuery(id+"F25.imprint","INTERSECT",VERTEX,{"derivedFrom":[subQ1,subQ0]});Q312=makeQuery(id+"F25.imprint","IMPRINT",FACE,{"disambiguationData":[TD([[makeQuery(id+"F25.imprint","IMPRINT",EDGE,{"disambiguationData":[TD([[subQ2,1.0]])],"derivedFrom":subQ1}),1.0]])]});}
            var Q313;
            {var subQ0=sQuery(id+"F25.wireOp",EDGE,"E460.MirrorCS");var subQ1=sQuery(id+"F25.wireOp",EDGE,"E428.MirrorCS");var subQ2=makeQuery(id+"F25.imprint","INTERSECT",VERTEX,{"derivedFrom":[subQ1,subQ0]});Q313=makeQuery(id+"F25.imprint","IMPRINT",FACE,{"disambiguationData":[TD([[makeQuery(id+"F25.imprint","IMPRINT",EDGE,{"disambiguationData":[TD([[subQ2,-1.0]])],"derivedFrom":subQ1}),1.0]])]});}
            var Q314;
            {var subQ0=sQuery(id+"F25.wireOp",EDGE,"E460.MirrorCS");var subQ1=sQuery(id+"F25.wireOp",EDGE,"E425.MirrorCS");var subQ2=makeQuery(id+"F25.imprint","INTERSECT",VERTEX,{"derivedFrom":[subQ1,subQ0]});Q314=makeQuery(id+"F25.imprint","IMPRINT",FACE,{"disambiguationData":[TD([[makeQuery(id+"F25.imprint","IMPRINT",EDGE,{"disambiguationData":[TD([[subQ2,-1.0]])],"derivedFrom":subQ1}),-1.0]])]});}
            var Q315;
            {var subQ0=sQuery(id+"F25.wireOp",EDGE,"E464.MirrorCS");var subQ1=sQuery(id+"F25.wireOp",EDGE,"E425.MirrorCS");var subQ2=makeQuery(id+"F25.imprint","INTERSECT",VERTEX,{"derivedFrom":[subQ1,subQ0]});Q315=makeQuery(id+"F25.imprint","IMPRINT",FACE,{"disambiguationData":[TD([[makeQuery(id+"F25.imprint","IMPRINT",EDGE,{"disambiguationData":[TD([[subQ2,1.0]])],"derivedFrom":subQ1}),-1.0]])]});}
            var Q316;
            {var subQ0=sQuery(id+"F25.wireOp",EDGE,"E555.trimOffspring");var subQ5=sQuery(id+"F25.wireOp",EDGE,"E439.MirrorCS");var subQ6=makeQuery(id+"F25.imprint","INTERSECT",VERTEX,{"derivedFrom":[subQ5,subQ0]});Q316=makeQuery(id+"F25.imprint","IMPRINT",FACE,{"disambiguationData":[TD([[makeQuery(id+"F25.imprint","IMPRINT",EDGE,{"disambiguationData":[TD([[subQ6,-1.0]])],"derivedFrom":subQ5}),-1.0]])]});}
            var Q317;
            {var subQ0=sQuery(id+"F25.wireOp",EDGE,"E555.trimOffspring");var subQ1=sQuery(id+"F25.wireOp",EDGE,"E429.MirrorCS");var subQ2=makeQuery(id+"F25.imprint","INTERSECT",VERTEX,{"derivedFrom":[subQ1,subQ0]});Q317=makeQuery(id+"F25.imprint","IMPRINT",FACE,{"disambiguationData":[TD([[makeQuery(id+"F25.imprint","IMPRINT",EDGE,{"disambiguationData":[TD([[subQ2,-1.0]])],"derivedFrom":subQ1}),-1.0]])]});}
            var Q318;
            {var subQ0=sQuery(id+"F25.wireOp",EDGE,"E555.trimOffspring");var subQ1=sQuery(id+"F25.wireOp",EDGE,"E429.MirrorCS");var subQ2=makeQuery(id+"F25.imprint","INTERSECT",VERTEX,{"derivedFrom":[subQ1,subQ0]});Q318=makeQuery(id+"F25.imprint","IMPRINT",FACE,{"disambiguationData":[TD([[makeQuery(id+"F25.imprint","IMPRINT",EDGE,{"disambiguationData":[TD([[subQ2,-1.0]])],"derivedFrom":subQ1}),1.0]])]});}
            var Q319;
            {var subQ0=sQuery(id+"F25.wireOp",EDGE,"E552.trimOffspring");var subQ5=sQuery(id+"F25.wireOp",EDGE,"E439.MirrorCS");var subQ6=makeQuery(id+"F25.imprint","INTERSECT",VERTEX,{"derivedFrom":[subQ5,subQ0]});Q319=makeQuery(id+"F25.imprint","IMPRINT",FACE,{"disambiguationData":[TD([[makeQuery(id+"F25.imprint","IMPRINT",EDGE,{"disambiguationData":[TD([[subQ6,-1.0]])],"derivedFrom":subQ5}),-1.0]])]});}
            var Q320;
            {var subQ0=sQuery(id+"F25.wireOp",EDGE,"E554.trimOffspring");var subQ1=sQuery(id+"F25.wireOp",EDGE,"E429.MirrorCS");var subQ2=makeQuery(id+"F25.imprint","INTERSECT",VERTEX,{"derivedFrom":[subQ1,subQ0]});Q320=makeQuery(id+"F25.imprint","IMPRINT",FACE,{"disambiguationData":[TD([[makeQuery(id+"F25.imprint","IMPRINT",EDGE,{"disambiguationData":[TD([[subQ2,1.0]])],"derivedFrom":subQ1}),-1.0]])]});}
            var Q321;
            {var subQ0=sQuery(id+"F25.wireOp",EDGE,"E545.trimOffspring");var subQ1=sQuery(id+"F25.wireOp",EDGE,"E424.MirrorCS");var subQ2=makeQuery(id+"F25.imprint","INTERSECT",VERTEX,{"derivedFrom":[subQ1,subQ0]});Q321=makeQuery(id+"F25.imprint","IMPRINT",FACE,{"disambiguationData":[TD([[makeQuery(id+"F25.imprint","IMPRINT",EDGE,{"disambiguationData":[TD([[subQ2,1.0]])],"derivedFrom":subQ1}),1.0]])]});}
            var Q322;
            {var subQ0=sQuery(id+"F25.wireOp",EDGE,"E545.trimOffspring");var subQ1=sQuery(id+"F25.wireOp",EDGE,"E429.MirrorCS");var subQ2=makeQuery(id+"F25.imprint","INTERSECT",VERTEX,{"derivedFrom":[subQ1,subQ0]});Q322=makeQuery(id+"F25.imprint","IMPRINT",FACE,{"disambiguationData":[TD([[makeQuery(id+"F25.imprint","IMPRINT",EDGE,{"disambiguationData":[TD([[subQ2,1.0]])],"derivedFrom":subQ1}),-1.0]])]});}
            var Q323;
            {var subQ0=sQuery(id+"F25.wireOp",EDGE,"E545.trimOffspring");var subQ1=sQuery(id+"F25.wireOp",EDGE,"E424.MirrorCS");var subQ2=makeQuery(id+"F25.imprint","INTERSECT",VERTEX,{"derivedFrom":[subQ1,subQ0]});Q323=makeQuery(id+"F25.imprint","IMPRINT",FACE,{"disambiguationData":[TD([[makeQuery(id+"F25.imprint","IMPRINT",EDGE,{"disambiguationData":[TD([[subQ2,-1.0]])],"derivedFrom":subQ1}),1.0]])]});}
            var Q324;
            {var subQ0=sQuery(id+"F25.wireOp",EDGE,"E545.trimOffspring");var subQ1=sQuery(id+"F25.wireOp",EDGE,"E429.MirrorCS");var subQ2=makeQuery(id+"F25.imprint","INTERSECT",VERTEX,{"derivedFrom":[subQ1,subQ0]});Q324=makeQuery(id+"F25.imprint","IMPRINT",FACE,{"disambiguationData":[TD([[makeQuery(id+"F25.imprint","IMPRINT",EDGE,{"disambiguationData":[TD([[subQ2,-1.0]])],"derivedFrom":subQ1}),-1.0]])]});}
            var Q325;
            {var subQ0=sQuery(id+"F25.wireOp",EDGE,"E553.trimOffspring");var subQ1=sQuery(id+"F25.wireOp",EDGE,"E424.MirrorCS");var subQ2=makeQuery(id+"F25.imprint","INTERSECT",VERTEX,{"derivedFrom":[subQ1,subQ0]});Q325=makeQuery(id+"F25.imprint","IMPRINT",FACE,{"disambiguationData":[TD([[makeQuery(id+"F25.imprint","IMPRINT",EDGE,{"disambiguationData":[TD([[subQ2,-1.0]])],"derivedFrom":subQ1}),1.0]])]});}
            var Q326;
            {var subQ3=sQuery(id+"F25.wireOp",EDGE,"E553.trimOffspring");var subQ5=sQuery(id+"F25.wireOp",EDGE,"E439.MirrorCS");var subQ6=makeQuery(id+"F25.imprint","INTERSECT",VERTEX,{"derivedFrom":[subQ5,subQ3]});Q326=makeQuery(id+"F25.imprint","IMPRINT",FACE,{"disambiguationData":[TD([[makeQuery(id+"F25.imprint","IMPRINT",EDGE,{"disambiguationData":[TD([[subQ6,-1.0]])],"derivedFrom":subQ5}),1.0]])]});}
            var Q327;
            {var subQ0=sQuery(id+"F25.wireOp",EDGE,"E460.MirrorCS");var subQ1=sQuery(id+"F25.wireOp",EDGE,"E424.MirrorCS");var subQ2=makeQuery(id+"F25.imprint","INTERSECT",VERTEX,{"derivedFrom":[subQ1,subQ0]});Q327=makeQuery(id+"F25.imprint","IMPRINT",FACE,{"disambiguationData":[TD([[makeQuery(id+"F25.imprint","IMPRINT",EDGE,{"disambiguationData":[TD([[subQ2,-1.0]])],"derivedFrom":subQ1}),1.0]])]});}
            var Q328;
            {var subQ3=sQuery(id+"F25.wireOp",EDGE,"E460.MirrorCS");var subQ5=sQuery(id+"F25.wireOp",EDGE,"E439.MirrorCS");var subQ6=makeQuery(id+"F25.imprint","INTERSECT",VERTEX,{"derivedFrom":[subQ5,subQ3]});Q328=makeQuery(id+"F25.imprint","IMPRINT",FACE,{"disambiguationData":[TD([[makeQuery(id+"F25.imprint","IMPRINT",EDGE,{"disambiguationData":[TD([[subQ6,-1.0]])],"derivedFrom":subQ5}),1.0]])]});}
            var Q329;
            {var subQ0=sQuery(id+"F25.wireOp",EDGE,"E464.MirrorCS");var subQ1=sQuery(id+"F25.wireOp",EDGE,"E424.MirrorCS");var subQ2=makeQuery(id+"F25.imprint","INTERSECT",VERTEX,{"derivedFrom":[subQ1,subQ0]});Q329=makeQuery(id+"F25.imprint","IMPRINT",FACE,{"disambiguationData":[TD([[makeQuery(id+"F25.imprint","IMPRINT",EDGE,{"disambiguationData":[TD([[subQ2,1.0]])],"derivedFrom":subQ1}),1.0]])]});}
            var Q330;
            {var subQ3=sQuery(id+"F25.wireOp",EDGE,"E464.MirrorCS");var subQ5=sQuery(id+"F25.wireOp",EDGE,"E439.MirrorCS");var subQ6=makeQuery(id+"F25.imprint","INTERSECT",VERTEX,{"derivedFrom":[subQ5,subQ3]});Q330=makeQuery(id+"F25.imprint","IMPRINT",FACE,{"disambiguationData":[TD([[makeQuery(id+"F25.imprint","IMPRINT",EDGE,{"disambiguationData":[TD([[subQ6,1.0]])],"derivedFrom":subQ5}),1.0]])]});}
            var Q331;
            {var subQ0=sQuery(id+"F25.wireOp",EDGE,"E555.trimOffspring");var subQ1=sQuery(id+"F25.wireOp",EDGE,"E445.MirrorCS");var subQ2=makeQuery(id+"F25.imprint","INTERSECT",VERTEX,{"derivedFrom":[subQ1,subQ0]});Q331=makeQuery(id+"F25.imprint","IMPRINT",FACE,{"disambiguationData":[TD([[makeQuery(id+"F25.imprint","IMPRINT",EDGE,{"disambiguationData":[TD([[subQ2,-1.0]])],"derivedFrom":subQ1}),1.0]])]});}
            var Q332;
            {var subQ0=sQuery(id+"F25.wireOp",EDGE,"E564.trimOffspring");var subQ1=sQuery(id+"F25.wireOp",EDGE,"E445.MirrorCS");var subQ2=makeQuery(id+"F25.imprint","INTERSECT",VERTEX,{"derivedFrom":[subQ1,subQ0]});Q332=makeQuery(id+"F25.imprint","IMPRINT",FACE,{"disambiguationData":[TD([[makeQuery(id+"F25.imprint","IMPRINT",EDGE,{"disambiguationData":[TD([[subQ2,1.0]])],"derivedFrom":subQ1}),1.0]])]});}
            var Q333;
            {var subQ0=sQuery(id+"F25.wireOp",EDGE,"E547.trimOffspring");var subQ1=sQuery(id+"F25.wireOp",EDGE,"E445.MirrorCS");var subQ2=makeQuery(id+"F25.imprint","INTERSECT",VERTEX,{"derivedFrom":[subQ1,subQ0]});Q333=makeQuery(id+"F25.imprint","IMPRINT",FACE,{"disambiguationData":[TD([[makeQuery(id+"F25.imprint","IMPRINT",EDGE,{"disambiguationData":[TD([[subQ2,1.0]])],"derivedFrom":subQ1}),1.0]])]});}
            var Q334;
            {var subQ3=sQuery(id+"F25.wireOp",EDGE,"E563.trimOffspring");Q334=makeQuery(id+"F25.imprint","IMPRINT",FACE,{"disambiguationData":[TD([[makeQuery(id+"F25.imprint","IMPRINT",EDGE,{"derivedFrom":subQ3}),1.0]])]});}
            var Q335;
            {var subQ3=sQuery(id+"F25.wireOp",EDGE,"E563.trimOffspring");Q335=makeQuery(id+"F25.imprint","IMPRINT",FACE,{"disambiguationData":[TD([[makeQuery(id+"F25.imprint","IMPRINT",EDGE,{"derivedFrom":subQ3}),-1.0]])]});}
            var Q336;
            {var subQ3=sQuery(id+"F25.wireOp",EDGE,"E560.trimOffspring");var subQ5=sQuery(id+"F25.wireOp",EDGE,"E434.MirrorCS");var subQ6=makeQuery(id+"F25.imprint","INTERSECT",VERTEX,{"derivedFrom":[subQ5,subQ3]});Q336=makeQuery(id+"F25.imprint","IMPRINT",FACE,{"disambiguationData":[TD([[makeQuery(id+"F25.imprint","IMPRINT",EDGE,{"disambiguationData":[TD([[subQ6,-1.0]])],"derivedFrom":subQ5}),-1.0]])]});}
            var Q337;
            {var subQ3=sQuery(id+"F25.wireOp",EDGE,"E559.trimOffspring");var subQ5=sQuery(id+"F25.wireOp",EDGE,"E434.MirrorCS");var subQ6=makeQuery(id+"F25.imprint","INTERSECT",VERTEX,{"derivedFrom":[subQ5,subQ3]});Q337=makeQuery(id+"F25.imprint","IMPRINT",FACE,{"disambiguationData":[TD([[makeQuery(id+"F25.imprint","IMPRINT",EDGE,{"disambiguationData":[TD([[subQ6,1.0]])],"derivedFrom":subQ5}),-1.0]])]});}
            var Q338;
            {var subQ0=sQuery(id+"F25.wireOp",EDGE,"E559.trimOffspring");var subQ1=sQuery(id+"F25.wireOp",EDGE,"E443.MirrorCS");var subQ2=makeQuery(id+"F25.imprint","INTERSECT",VERTEX,{"derivedFrom":[subQ1,subQ0]});Q338=makeQuery(id+"F25.imprint","IMPRINT",FACE,{"disambiguationData":[TD([[makeQuery(id+"F25.imprint","IMPRINT",EDGE,{"disambiguationData":[TD([[subQ2,1.0]])],"derivedFrom":subQ1}),-1.0]])]});}
            var Q339;
            {var subQ0=sQuery(id+"F25.wireOp",EDGE,"E559.trimOffspring");var subQ1=sQuery(id+"F25.wireOp",EDGE,"E443.MirrorCS");var subQ2=makeQuery(id+"F25.imprint","INTERSECT",VERTEX,{"derivedFrom":[subQ1,subQ0]});Q339=makeQuery(id+"F25.imprint","IMPRINT",FACE,{"disambiguationData":[TD([[makeQuery(id+"F25.imprint","IMPRINT",EDGE,{"disambiguationData":[TD([[subQ2,1.0]])],"derivedFrom":subQ1}),1.0]])]});}
            var Q340;
            {var subQ0=sQuery(id+"F25.wireOp",EDGE,"E571.trimOffspring");var subQ1=sQuery(id+"F25.wireOp",EDGE,"E559.trimOffspring");var subQ2=makeQuery(id+"F25.imprint","INTERSECT",VERTEX,{"derivedFrom":[subQ1,subQ0]});Q340=makeQuery(id+"F25.imprint","IMPRINT",FACE,{"disambiguationData":[TD([[makeQuery(id+"F25.imprint","IMPRINT",EDGE,{"disambiguationData":[TD([[subQ2,-1.0]])],"derivedFrom":subQ1}),1.0]])]});}
            var Q341;
            {var subQ0=sQuery(id+"F25.wireOp",EDGE,"E583.trimOffspring");var subQ1=sQuery(id+"F25.wireOp",EDGE,"E559.trimOffspring");var subQ2=makeQuery(id+"F25.imprint","INTERSECT",VERTEX,{"derivedFrom":[subQ1,subQ0]});Q341=makeQuery(id+"F25.imprint","IMPRINT",FACE,{"disambiguationData":[TD([[makeQuery(id+"F25.imprint","IMPRINT",EDGE,{"disambiguationData":[TD([[subQ2,1.0]])],"derivedFrom":subQ1}),1.0]])]});}
            var Q342;
            {var subQ0=sQuery(id+"F25.wireOp",EDGE,"E583.trimOffspring");var subQ1=sQuery(id+"F25.wireOp",EDGE,"E560.trimOffspring");var subQ2=makeQuery(id+"F25.imprint","INTERSECT",VERTEX,{"derivedFrom":[subQ1,subQ0]});Q342=makeQuery(id+"F25.imprint","IMPRINT",FACE,{"disambiguationData":[TD([[makeQuery(id+"F25.imprint","IMPRINT",EDGE,{"disambiguationData":[TD([[subQ2,1.0]])],"derivedFrom":subQ1}),-1.0]])]});}
            var Q343;
            {var subQ0=sQuery(id+"F25.wireOp",EDGE,"E583.trimOffspring");var subQ1=sQuery(id+"F25.wireOp",EDGE,"E560.trimOffspring");var subQ2=makeQuery(id+"F25.imprint","INTERSECT",VERTEX,{"derivedFrom":[subQ1,subQ0]});Q343=makeQuery(id+"F25.imprint","IMPRINT",FACE,{"disambiguationData":[TD([[makeQuery(id+"F25.imprint","IMPRINT",EDGE,{"disambiguationData":[TD([[subQ2,1.0]])],"derivedFrom":subQ1}),1.0]])]});}
            var Q344;
            {var subQ0=sQuery(id+"F25.wireOp",EDGE,"E572.trimOffspring");var subQ1=sQuery(id+"F25.wireOp",EDGE,"E568.trimOffspring");var subQ2=makeQuery(id+"F25.imprint","INTERSECT",VERTEX,{"derivedFrom":[subQ1,subQ0]});Q344=makeQuery(id+"F25.imprint","IMPRINT",FACE,{"disambiguationData":[TD([[makeQuery(id+"F25.imprint","IMPRINT",EDGE,{"disambiguationData":[TD([[subQ2,-1.0]])],"derivedFrom":subQ1}),1.0]])]});}
            var Q345;
            {var subQ0=sQuery(id+"F25.wireOp",EDGE,"E583.trimOffspring");var subQ1=sQuery(id+"F25.wireOp",EDGE,"E568.trimOffspring");var subQ2=makeQuery(id+"F25.imprint","INTERSECT",VERTEX,{"derivedFrom":[subQ1,subQ0]});Q345=makeQuery(id+"F25.imprint","IMPRINT",FACE,{"disambiguationData":[TD([[makeQuery(id+"F25.imprint","IMPRINT",EDGE,{"disambiguationData":[TD([[subQ2,-1.0]])],"derivedFrom":subQ1}),1.0]])]});}
            var Q346;
            {var subQ0=sQuery(id+"F25.wireOp",EDGE,"E596.trimOffspring");var subQ1=sQuery(id+"F25.wireOp",EDGE,"E568.trimOffspring");var subQ2=makeQuery(id+"F25.imprint","INTERSECT",VERTEX,{"derivedFrom":[subQ1,subQ0]});Q346=makeQuery(id+"F25.imprint","IMPRINT",FACE,{"disambiguationData":[TD([[makeQuery(id+"F25.imprint","IMPRINT",EDGE,{"disambiguationData":[TD([[subQ2,-1.0]])],"derivedFrom":subQ1}),1.0]])]});}
            var Q347;
            {var subQ0=sQuery(id+"F25.wireOp",EDGE,"E598.trimOffspring");var subQ1=sQuery(id+"F25.wireOp",EDGE,"E568.trimOffspring");var subQ2=makeQuery(id+"F25.imprint","INTERSECT",VERTEX,{"derivedFrom":[subQ1,subQ0]});Q347=makeQuery(id+"F25.imprint","IMPRINT",FACE,{"disambiguationData":[TD([[makeQuery(id+"F25.imprint","IMPRINT",EDGE,{"disambiguationData":[TD([[subQ2,-1.0]])],"derivedFrom":subQ1}),1.0]])]});}
            var Q348;
            {var subQ1=sQuery(id+"F25.wireOp",EDGE,"E481.trimOffspring");var subQ3=sQuery(id+"F25.wireOp",EDGE,"E567.trimOffspring");var subQ4=makeQuery(id+"F25.imprint","INTERSECT",VERTEX,{"derivedFrom":[subQ1,subQ3]});Q348=makeQuery(id+"F25.imprint","IMPRINT",FACE,{"disambiguationData":[TD([[makeQuery(id+"F25.imprint","IMPRINT",EDGE,{"disambiguationData":[TD([[subQ4,1.0]])],"derivedFrom":subQ3}),-1.0]])]});}
            var Q349;
            {var subQ0=sQuery(id+"F25.wireOp",EDGE,"E608.trimOffspring");var subQ1=sQuery(id+"F25.wireOp",EDGE,"E423.MirrorCS");var subQ2=makeQuery(id+"F25.imprint","INTERSECT",VERTEX,{"derivedFrom":[subQ1,subQ0]});Q349=makeQuery(id+"F25.imprint","IMPRINT",FACE,{"disambiguationData":[TD([[makeQuery(id+"F25.imprint","IMPRINT",EDGE,{"disambiguationData":[TD([[subQ2,-1.0]])],"derivedFrom":subQ1}),-1.0]])]});}
            var Q350;
            {var subQ0=sQuery(id+"F25.wireOp",EDGE,"E608.trimOffspring");var subQ1=sQuery(id+"F25.wireOp",EDGE,"E483.trimOffspring");var subQ2=makeQuery(id+"F25.imprint","INTERSECT",VERTEX,{"derivedFrom":[subQ1,subQ0]});Q350=makeQuery(id+"F25.imprint","IMPRINT",FACE,{"disambiguationData":[TD([[makeQuery(id+"F25.imprint","IMPRINT",EDGE,{"disambiguationData":[TD([[subQ2,-1.0]])],"derivedFrom":subQ1}),-1.0]])]});}
            var Q351;
            {var subQ3=sQuery(id+"F25.wireOp",EDGE,"E599.trimOffspring");var subQ5=sQuery(id+"F25.wireOp",EDGE,"E484.trimOffspring");var subQ6=makeQuery(id+"F25.imprint","INTERSECT",VERTEX,{"derivedFrom":[subQ5,subQ3]});Q351=makeQuery(id+"F25.imprint","IMPRINT",FACE,{"disambiguationData":[TD([[makeQuery(id+"F25.imprint","IMPRINT",EDGE,{"disambiguationData":[TD([[subQ6,-1.0]])],"derivedFrom":subQ5}),1.0]])]});}
            var Q352;
            {var subQ0=sQuery(id+"F25.wireOp",EDGE,"E570.trimOffspring");var subQ5=sQuery(id+"F25.wireOp",EDGE,"E484.trimOffspring");var subQ6=makeQuery(id+"F25.imprint","INTERSECT",VERTEX,{"derivedFrom":[subQ5,subQ0]});Q352=makeQuery(id+"F25.imprint","IMPRINT",FACE,{"disambiguationData":[TD([[makeQuery(id+"F25.imprint","IMPRINT",EDGE,{"disambiguationData":[TD([[subQ6,-1.0]])],"derivedFrom":subQ5}),1.0]])]});}
            var Q353;
            {var subQ0=sQuery(id+"F25.wireOp",EDGE,"E565.trimOffspring");var subQ1=sQuery(id+"F25.wireOp",EDGE,"E483.trimOffspring");var subQ2=makeQuery(id+"F25.imprint","INTERSECT",VERTEX,{"derivedFrom":[subQ1,subQ0]});Q353=makeQuery(id+"F25.imprint","IMPRINT",FACE,{"disambiguationData":[TD([[makeQuery(id+"F25.imprint","IMPRINT",EDGE,{"disambiguationData":[TD([[subQ2,1.0]])],"derivedFrom":subQ1}),-1.0]])]});}
            var Q354;
            {var subQ0=sQuery(id+"F25.wireOp",EDGE,"E565.trimOffspring");var subQ5=sQuery(id+"F25.wireOp",EDGE,"E484.trimOffspring");var subQ6=makeQuery(id+"F25.imprint","INTERSECT",VERTEX,{"derivedFrom":[subQ5,subQ0]});Q354=makeQuery(id+"F25.imprint","IMPRINT",FACE,{"disambiguationData":[TD([[makeQuery(id+"F25.imprint","IMPRINT",EDGE,{"disambiguationData":[TD([[subQ6,1.0]])],"derivedFrom":subQ5}),-1.0]])]});}
            var Q355;
            {var subQ0=sQuery(id+"F25.wireOp",EDGE,"E570.trimOffspring");var subQ5=sQuery(id+"F25.wireOp",EDGE,"E484.trimOffspring");var subQ6=makeQuery(id+"F25.imprint","INTERSECT",VERTEX,{"derivedFrom":[subQ5,subQ0]});Q355=makeQuery(id+"F25.imprint","IMPRINT",FACE,{"disambiguationData":[TD([[makeQuery(id+"F25.imprint","IMPRINT",EDGE,{"disambiguationData":[TD([[subQ6,-1.0]])],"derivedFrom":subQ5}),1.0]])]});}
            var Q356;
            {var subQ0=sQuery(id+"F25.wireOp",EDGE,"E565.trimOffspring");var subQ1=sQuery(id+"F25.wireOp",EDGE,"E483.trimOffspring");var subQ2=makeQuery(id+"F25.imprint","INTERSECT",VERTEX,{"derivedFrom":[subQ1,subQ0]});Q356=makeQuery(id+"F25.imprint","IMPRINT",FACE,{"disambiguationData":[TD([[makeQuery(id+"F25.imprint","IMPRINT",EDGE,{"disambiguationData":[TD([[subQ2,1.0]])],"derivedFrom":subQ1}),-1.0]])]});}
            var Q357;
            {var subQ0=sQuery(id+"F25.wireOp",EDGE,"E598.trimOffspring");var subQ1=sQuery(id+"F25.wireOp",EDGE,"E568.trimOffspring");var subQ2=makeQuery(id+"F25.imprint","INTERSECT",VERTEX,{"derivedFrom":[subQ1,subQ0]});Q357=makeQuery(id+"F25.imprint","IMPRINT",FACE,{"disambiguationData":[TD([[makeQuery(id+"F25.imprint","IMPRINT",EDGE,{"disambiguationData":[TD([[subQ2,-1.0]])],"derivedFrom":subQ1}),-1.0]])]});}
            var Q358;
            {var subQ0=sQuery(id+"F25.wireOp",EDGE,"E596.trimOffspring");var subQ1=sQuery(id+"F25.wireOp",EDGE,"E568.trimOffspring");var subQ2=makeQuery(id+"F25.imprint","INTERSECT",VERTEX,{"derivedFrom":[subQ1,subQ0]});Q358=makeQuery(id+"F25.imprint","IMPRINT",FACE,{"disambiguationData":[TD([[makeQuery(id+"F25.imprint","IMPRINT",EDGE,{"disambiguationData":[TD([[subQ2,-1.0]])],"derivedFrom":subQ1}),-1.0]])]});}
            var Q359;
            {var subQ0=sQuery(id+"F25.wireOp",EDGE,"E577.trimOffspring");var subQ1=sQuery(id+"F25.wireOp",EDGE,"E454.MirrorCS");var subQ2=makeQuery(id+"F25.imprint","INTERSECT",VERTEX,{"derivedFrom":[subQ1,subQ0]});Q359=makeQuery(id+"F25.imprint","IMPRINT",FACE,{"disambiguationData":[TD([[makeQuery(id+"F25.imprint","IMPRINT",EDGE,{"disambiguationData":[TD([[subQ2,-1.0]])],"derivedFrom":subQ1}),1.0]])]});}
            var Q360;
            {var subQ0=sQuery(id+"F25.wireOp",EDGE,"E577.trimOffspring");var subQ1=sQuery(id+"F25.wireOp",EDGE,"E456.MirrorCS");var subQ2=makeQuery(id+"F25.imprint","INTERSECT",VERTEX,{"derivedFrom":[subQ1,subQ0]});Q360=makeQuery(id+"F25.imprint","IMPRINT",FACE,{"disambiguationData":[TD([[makeQuery(id+"F25.imprint","IMPRINT",EDGE,{"disambiguationData":[TD([[subQ2,-1.0]])],"derivedFrom":subQ1}),-1.0]])]});}
            var Q361;
            {var subQ0=sQuery(id+"F25.wireOp",EDGE,"E596.trimOffspring");var subQ1=sQuery(id+"F25.wireOp",EDGE,"E582.trimOffspring");var subQ2=makeQuery(id+"F25.imprint","INTERSECT",VERTEX,{"derivedFrom":[subQ1,subQ0]});Q361=makeQuery(id+"F25.imprint","IMPRINT",FACE,{"disambiguationData":[TD([[makeQuery(id+"F25.imprint","IMPRINT",EDGE,{"disambiguationData":[TD([[subQ2,-1.0]])],"derivedFrom":subQ1}),-1.0]])]});}
            var Q362;
            {var subQ0=sQuery(id+"F25.wireOp",EDGE,"E596.trimOffspring");var subQ1=sQuery(id+"F25.wireOp",EDGE,"E576.trimOffspring");var subQ2=makeQuery(id+"F25.imprint","INTERSECT",VERTEX,{"derivedFrom":[subQ1,subQ0]});Q362=makeQuery(id+"F25.imprint","IMPRINT",FACE,{"disambiguationData":[TD([[makeQuery(id+"F25.imprint","IMPRINT",EDGE,{"disambiguationData":[TD([[subQ2,-1.0]])],"derivedFrom":subQ1}),1.0]])]});}
            var Q363;
            {var subQ0=sQuery(id+"F25.wireOp",EDGE,"E598.trimOffspring");var subQ1=sQuery(id+"F25.wireOp",EDGE,"E582.trimOffspring");var subQ2=makeQuery(id+"F25.imprint","INTERSECT",VERTEX,{"derivedFrom":[subQ1,subQ0]});Q363=makeQuery(id+"F25.imprint","IMPRINT",FACE,{"disambiguationData":[TD([[makeQuery(id+"F25.imprint","IMPRINT",EDGE,{"disambiguationData":[TD([[subQ2,-1.0]])],"derivedFrom":subQ1}),-1.0]])]});}
            var Q364;
            {var subQ0=sQuery(id+"F25.wireOp",EDGE,"E597.trimOffspring");var subQ1=sQuery(id+"F25.wireOp",EDGE,"E576.trimOffspring");var subQ2=makeQuery(id+"F25.imprint","INTERSECT",VERTEX,{"derivedFrom":[subQ1,subQ0]});Q364=makeQuery(id+"F25.imprint","IMPRINT",FACE,{"disambiguationData":[TD([[makeQuery(id+"F25.imprint","IMPRINT",EDGE,{"disambiguationData":[TD([[subQ2,1.0]])],"derivedFrom":subQ1}),1.0]])]});}
            var Q365;
            {var subQ0=sQuery(id+"F25.wireOp",EDGE,"E597.trimOffspring");var subQ1=sQuery(id+"F25.wireOp",EDGE,"E576.trimOffspring");var subQ2=makeQuery(id+"F25.imprint","INTERSECT",VERTEX,{"derivedFrom":[subQ1,subQ0]});Q365=makeQuery(id+"F25.imprint","IMPRINT",FACE,{"disambiguationData":[TD([[makeQuery(id+"F25.imprint","IMPRINT",EDGE,{"disambiguationData":[TD([[subQ2,-1.0]])],"derivedFrom":subQ1}),1.0]])]});}
            var Q366;
            {var subQ0=sQuery(id+"F25.wireOp",EDGE,"E582.trimOffspring");var subQ1=sQuery(id+"F25.wireOp",EDGE,"E585.trimOffspring");var subQ2=makeQuery(id+"F25.imprint","INTERSECT",VERTEX,{"derivedFrom":[subQ1,subQ0]});Q366=makeQuery(id+"F25.imprint","IMPRINT",FACE,{"disambiguationData":[TD([[makeQuery(id+"F25.imprint","IMPRINT",EDGE,{"disambiguationData":[TD([[subQ2,-1.0]])],"derivedFrom":subQ1}),-1.0]])]});}
            var Q367;
            {var subQ0=sQuery(id+"F25.wireOp",EDGE,"E582.trimOffspring");var subQ1=sQuery(id+"F25.wireOp",EDGE,"E585.trimOffspring");var subQ2=makeQuery(id+"F25.imprint","INTERSECT",VERTEX,{"derivedFrom":[subQ1,subQ0]});Q367=makeQuery(id+"F25.imprint","IMPRINT",FACE,{"disambiguationData":[TD([[makeQuery(id+"F25.imprint","IMPRINT",EDGE,{"disambiguationData":[TD([[subQ2,-1.0]])],"derivedFrom":subQ1}),1.0]])]});}
            var Q368;
            {var subQ0=sQuery(id+"F25.wireOp",EDGE,"E585.trimOffspring");var subQ1=sQuery(id+"F25.wireOp",EDGE,"E576.trimOffspring");var subQ2=makeQuery(id+"F25.imprint","INTERSECT",VERTEX,{"derivedFrom":[subQ1,subQ0]});Q368=makeQuery(id+"F25.imprint","IMPRINT",FACE,{"disambiguationData":[TD([[makeQuery(id+"F25.imprint","IMPRINT",EDGE,{"disambiguationData":[TD([[subQ2,-1.0]])],"derivedFrom":subQ1}),1.0]])]});}
            var Q369;
            {var subQ0=sQuery(id+"F25.wireOp",EDGE,"E589.trimOffspring");var subQ1=sQuery(id+"F25.wireOp",EDGE,"E576.trimOffspring");var subQ2=makeQuery(id+"F25.imprint","INTERSECT",VERTEX,{"derivedFrom":[subQ1,subQ0]});Q369=makeQuery(id+"F25.imprint","IMPRINT",FACE,{"disambiguationData":[TD([[makeQuery(id+"F25.imprint","IMPRINT",EDGE,{"disambiguationData":[TD([[subQ2,1.0]])],"derivedFrom":subQ1}),1.0]])]});}
            var Q370;
            {var subQ0=sQuery(id+"F25.wireOp",EDGE,"E433.MirrorCS");Q370=makeQuery(id+"F25.imprint","IMPRINT",FACE,{"disambiguationData":[TD([[makeQuery(id+"F25.imprint","IMPRINT",EDGE,{"derivedFrom":subQ0}),1.0]])]});}
            var Q371;
            {var subQ3=sQuery(id+"F25.wireOp",EDGE,"E585.trimOffspring");var subQ5=sQuery(id+"F25.wireOp",EDGE,"E576.trimOffspring");var subQ6=makeQuery(id+"F25.imprint","INTERSECT",VERTEX,{"derivedFrom":[subQ5,subQ3]});Q371=makeQuery(id+"F25.imprint","IMPRINT",FACE,{"disambiguationData":[TD([[makeQuery(id+"F25.imprint","IMPRINT",EDGE,{"disambiguationData":[TD([[subQ6,-1.0]])],"derivedFrom":subQ5}),-1.0]])]});}
            var Q372;
            {var subQ0=sQuery(id+"F25.wireOp",EDGE,"E589.trimOffspring");var subQ1=sQuery(id+"F25.wireOp",EDGE,"E582.trimOffspring");var subQ2=makeQuery(id+"F25.imprint","INTERSECT",VERTEX,{"derivedFrom":[subQ1,subQ0]});Q372=makeQuery(id+"F25.imprint","IMPRINT",FACE,{"disambiguationData":[TD([[makeQuery(id+"F25.imprint","IMPRINT",EDGE,{"disambiguationData":[TD([[subQ2,1.0]])],"derivedFrom":subQ1}),-1.0]])]});}
            var Q373;
            {var subQ0=sQuery(id+"F25.wireOp",EDGE,"E578.trimOffspring");var subQ1=sQuery(id+"F25.wireOp",EDGE,"E454.MirrorCS");var subQ2=makeQuery(id+"F25.imprint","INTERSECT",VERTEX,{"derivedFrom":[subQ1,subQ0]});Q373=makeQuery(id+"F25.imprint","IMPRINT",FACE,{"disambiguationData":[TD([[makeQuery(id+"F25.imprint","IMPRINT",EDGE,{"disambiguationData":[TD([[subQ2,-1.0]])],"derivedFrom":subQ1}),1.0]])]});}
            var Q374;
            {var subQ0=sQuery(id+"F25.wireOp",EDGE,"E574.trimOffspring");var subQ1=sQuery(id+"F25.wireOp",EDGE,"E456.MirrorCS");var subQ2=makeQuery(id+"F25.imprint","INTERSECT",VERTEX,{"derivedFrom":[subQ1,subQ0]});Q374=makeQuery(id+"F25.imprint","IMPRINT",FACE,{"disambiguationData":[TD([[makeQuery(id+"F25.imprint","IMPRINT",EDGE,{"disambiguationData":[TD([[subQ2,1.0]])],"derivedFrom":subQ1}),-1.0]])]});}
            var Q375;
            {var subQ0=sQuery(id+"F25.wireOp",EDGE,"E574.trimOffspring");var subQ1=sQuery(id+"F25.wireOp",EDGE,"E454.MirrorCS");var subQ2=makeQuery(id+"F25.imprint","INTERSECT",VERTEX,{"derivedFrom":[subQ1,subQ0]});Q375=makeQuery(id+"F25.imprint","IMPRINT",FACE,{"disambiguationData":[TD([[makeQuery(id+"F25.imprint","IMPRINT",EDGE,{"disambiguationData":[TD([[subQ2,-1.0]])],"derivedFrom":subQ1}),1.0]])]});}
            var Q376;
            {var subQ0=sQuery(id+"F25.wireOp",EDGE,"E574.trimOffspring");var subQ1=sQuery(id+"F25.wireOp",EDGE,"E456.MirrorCS");var subQ2=makeQuery(id+"F25.imprint","INTERSECT",VERTEX,{"derivedFrom":[subQ1,subQ0]});Q376=makeQuery(id+"F25.imprint","IMPRINT",FACE,{"disambiguationData":[TD([[makeQuery(id+"F25.imprint","IMPRINT",EDGE,{"disambiguationData":[TD([[subQ2,-1.0]])],"derivedFrom":subQ1}),-1.0]])]});}
            var Q377;
            {var subQ0=sQuery(id+"F25.wireOp",EDGE,"E580.trimOffspring");var subQ1=sQuery(id+"F25.wireOp",EDGE,"E454.MirrorCS");var subQ2=makeQuery(id+"F25.imprint","INTERSECT",VERTEX,{"derivedFrom":[subQ1,subQ0]});Q377=makeQuery(id+"F25.imprint","IMPRINT",FACE,{"disambiguationData":[TD([[makeQuery(id+"F25.imprint","IMPRINT",EDGE,{"disambiguationData":[TD([[subQ2,-1.0]])],"derivedFrom":subQ1}),1.0]])]});}
            var Q378;
            {var subQ0=sQuery(id+"F25.wireOp",EDGE,"E580.trimOffspring");var subQ1=sQuery(id+"F25.wireOp",EDGE,"E456.MirrorCS");var subQ2=makeQuery(id+"F25.imprint","INTERSECT",VERTEX,{"derivedFrom":[subQ1,subQ0]});Q378=makeQuery(id+"F25.imprint","IMPRINT",FACE,{"disambiguationData":[TD([[makeQuery(id+"F25.imprint","IMPRINT",EDGE,{"disambiguationData":[TD([[subQ2,-1.0]])],"derivedFrom":subQ1}),-1.0]])]});}
            var Q379;
            {var subQ0=sQuery(id+"F25.wireOp",EDGE,"E579.trimOffspring");var subQ1=sQuery(id+"F25.wireOp",EDGE,"E454.MirrorCS");var subQ2=makeQuery(id+"F25.imprint","INTERSECT",VERTEX,{"derivedFrom":[subQ1,subQ0]});Q379=makeQuery(id+"F25.imprint","IMPRINT",FACE,{"disambiguationData":[TD([[makeQuery(id+"F25.imprint","IMPRINT",EDGE,{"disambiguationData":[TD([[subQ2,-1.0]])],"derivedFrom":subQ1}),1.0]])]});}
            var Q380;
            {var subQ0=sQuery(id+"F25.wireOp",EDGE,"E581.trimOffspring");var subQ1=sQuery(id+"F25.wireOp",EDGE,"E456.MirrorCS");var subQ2=makeQuery(id+"F25.imprint","INTERSECT",VERTEX,{"derivedFrom":[subQ1,subQ0]});Q380=makeQuery(id+"F25.imprint","IMPRINT",FACE,{"disambiguationData":[TD([[makeQuery(id+"F25.imprint","IMPRINT",EDGE,{"disambiguationData":[TD([[subQ2,1.0]])],"derivedFrom":subQ1}),-1.0]])]});}
            var Q381;
            {var subQ0=sQuery(id+"F25.wireOp",EDGE,"E581.trimOffspring");var subQ1=sQuery(id+"F25.wireOp",EDGE,"E454.MirrorCS");var subQ2=makeQuery(id+"F25.imprint","INTERSECT",VERTEX,{"derivedFrom":[subQ1,subQ0]});Q381=makeQuery(id+"F25.imprint","IMPRINT",FACE,{"disambiguationData":[TD([[makeQuery(id+"F25.imprint","IMPRINT",EDGE,{"disambiguationData":[TD([[subQ2,-1.0]])],"derivedFrom":subQ1}),1.0]])]});}
            var Q382;
            {var subQ0=sQuery(id+"F25.wireOp",EDGE,"E581.trimOffspring");var subQ1=sQuery(id+"F25.wireOp",EDGE,"E456.MirrorCS");var subQ2=makeQuery(id+"F25.imprint","INTERSECT",VERTEX,{"derivedFrom":[subQ1,subQ0]});Q382=makeQuery(id+"F25.imprint","IMPRINT",FACE,{"disambiguationData":[TD([[makeQuery(id+"F25.imprint","IMPRINT",EDGE,{"disambiguationData":[TD([[subQ2,-1.0]])],"derivedFrom":subQ1}),-1.0]])]});}
            var Q383;
            {var subQ0=sQuery(id+"F25.wireOp",EDGE,"E585.trimOffspring");var subQ1=sQuery(id+"F25.wireOp",EDGE,"E454.MirrorCS");var subQ2=makeQuery(id+"F25.imprint","INTERSECT",VERTEX,{"derivedFrom":[subQ1,subQ0]});Q383=makeQuery(id+"F25.imprint","IMPRINT",FACE,{"disambiguationData":[TD([[makeQuery(id+"F25.imprint","IMPRINT",EDGE,{"disambiguationData":[TD([[subQ2,-1.0]])],"derivedFrom":subQ1}),1.0]])]});}
            var Q384;
            {var subQ3=sQuery(id+"F25.wireOp",EDGE,"E585.trimOffspring");var subQ5=sQuery(id+"F25.wireOp",EDGE,"E441.MirrorCS");var subQ6=makeQuery(id+"F25.imprint","INTERSECT",VERTEX,{"derivedFrom":[subQ5,subQ3]});Q384=makeQuery(id+"F25.imprint","IMPRINT",FACE,{"disambiguationData":[TD([[makeQuery(id+"F25.imprint","IMPRINT",EDGE,{"disambiguationData":[TD([[subQ6,-1.0]])],"derivedFrom":subQ5}),1.0]])]});}
            var Q385;
            {var subQ0=sQuery(id+"F25.wireOp",EDGE,"E433.MirrorCS");Q385=makeQuery(id+"F25.imprint","IMPRINT",FACE,{"disambiguationData":[TD([[makeQuery(id+"F25.imprint","IMPRINT",EDGE,{"derivedFrom":subQ0}),-1.0]])]});}
            var Q386;
            {var subQ0=sQuery(id+"F25.wireOp",EDGE,"E589.trimOffspring");var subQ1=sQuery(id+"F25.wireOp",EDGE,"E454.MirrorCS");var subQ2=makeQuery(id+"F25.imprint","INTERSECT",VERTEX,{"derivedFrom":[subQ1,subQ0]});Q386=makeQuery(id+"F25.imprint","IMPRINT",FACE,{"disambiguationData":[TD([[makeQuery(id+"F25.imprint","IMPRINT",EDGE,{"disambiguationData":[TD([[subQ2,1.0]])],"derivedFrom":subQ1}),1.0]])]});}
            var Q387;
            {var subQ0=sQuery(id+"F25.wireOp",EDGE,"E608.trimOffspring");var subQ1=sQuery(id+"F25.wireOp",EDGE,"E423.MirrorCS");var subQ2=makeQuery(id+"F25.imprint","INTERSECT",VERTEX,{"derivedFrom":[subQ1,subQ0]});Q387=makeQuery(id+"F25.imprint","IMPRINT",FACE,{"disambiguationData":[TD([[makeQuery(id+"F25.imprint","IMPRINT",EDGE,{"disambiguationData":[TD([[subQ2,-1.0]])],"derivedFrom":subQ1}),1.0]])]});}
            var Q388;
            {var subQ0=sQuery(id+"F25.wireOp",EDGE,"E608.trimOffspring");var subQ1=sQuery(id+"F25.wireOp",EDGE,"E427.MirrorCS");var subQ2=makeQuery(id+"F25.imprint","INTERSECT",VERTEX,{"derivedFrom":[subQ1,subQ0]});Q388=makeQuery(id+"F25.imprint","IMPRINT",FACE,{"disambiguationData":[TD([[makeQuery(id+"F25.imprint","IMPRINT",EDGE,{"disambiguationData":[TD([[subQ2,-1.0]])],"derivedFrom":subQ1}),1.0]])]});}
            var Q389;
            {var subQ0=sQuery(id+"F25.wireOp",EDGE,"E584.trimOffspring");Q389=makeQuery(id+"F25.imprint","IMPRINT",FACE,{"disambiguationData":[TD([[makeQuery(id+"F25.imprint","IMPRINT",EDGE,{"derivedFrom":subQ0}),1.0]])]});}
            var Q390;
            {var subQ3=sQuery(id+"F25.wireOp",EDGE,"E608.trimOffspring");var subQ5=sQuery(id+"F25.wireOp",EDGE,"E448.MirrorCS");var subQ6=makeQuery(id+"F25.imprint","INTERSECT",VERTEX,{"derivedFrom":[subQ5,subQ3]});Q390=makeQuery(id+"F25.imprint","IMPRINT",FACE,{"disambiguationData":[TD([[makeQuery(id+"F25.imprint","IMPRINT",EDGE,{"disambiguationData":[TD([[subQ6,-1.0]])],"derivedFrom":subQ5}),-1.0]])]});}
            var Q391;
            {var subQ0=sQuery(id+"F25.wireOp",EDGE,"E608.trimOffspring");var subQ1=sQuery(id+"F25.wireOp",EDGE,"E431.MirrorCS");var subQ2=makeQuery(id+"F25.imprint","INTERSECT",VERTEX,{"derivedFrom":[subQ1,subQ0]});Q391=makeQuery(id+"F25.imprint","IMPRINT",FACE,{"disambiguationData":[TD([[makeQuery(id+"F25.imprint","IMPRINT",EDGE,{"disambiguationData":[TD([[subQ2,-1.0]])],"derivedFrom":subQ1}),-1.0]])]});}
            var Q392;
            {var subQ0=sQuery(id+"F25.wireOp",EDGE,"E608.trimOffspring");var subQ1=sQuery(id+"F25.wireOp",EDGE,"E431.MirrorCS");var subQ2=makeQuery(id+"F25.imprint","INTERSECT",VERTEX,{"derivedFrom":[subQ1,subQ0]});Q392=makeQuery(id+"F25.imprint","IMPRINT",FACE,{"disambiguationData":[TD([[makeQuery(id+"F25.imprint","IMPRINT",EDGE,{"disambiguationData":[TD([[subQ2,-1.0]])],"derivedFrom":subQ1}),1.0]])]});}
            var Q393;
            {var subQ0=sQuery(id+"F25.wireOp",EDGE,"E608.trimOffspring");var subQ1=sQuery(id+"F25.wireOp",EDGE,"E446.MirrorCS");var subQ2=makeQuery(id+"F25.imprint","INTERSECT",VERTEX,{"derivedFrom":[subQ1,subQ0]});Q393=makeQuery(id+"F25.imprint","IMPRINT",FACE,{"disambiguationData":[TD([[makeQuery(id+"F25.imprint","IMPRINT",EDGE,{"disambiguationData":[TD([[subQ2,-1.0]])],"derivedFrom":subQ1}),1.0]])]});}
            var Q394;
            {var subQ0=sQuery(id+"F25.wireOp",EDGE,"E608.trimOffspring");var subQ1=sQuery(id+"F25.wireOp",EDGE,"E444.MirrorCS");var subQ2=makeQuery(id+"F25.imprint","INTERSECT",VERTEX,{"derivedFrom":[subQ1,subQ0]});Q394=makeQuery(id+"F25.imprint","IMPRINT",FACE,{"disambiguationData":[TD([[makeQuery(id+"F25.imprint","IMPRINT",EDGE,{"disambiguationData":[TD([[subQ2,-1.0]])],"derivedFrom":subQ1}),-1.0]])]});}
            var Q395;
            {var subQ0=sQuery(id+"F25.wireOp",EDGE,"E603.trimOffspring");var subQ1=sQuery(id+"F25.wireOp",EDGE,"E444.MirrorCS");var subQ2=makeQuery(id+"F25.imprint","INTERSECT",VERTEX,{"derivedFrom":[subQ1,subQ0]});Q395=makeQuery(id+"F25.imprint","IMPRINT",FACE,{"disambiguationData":[TD([[makeQuery(id+"F25.imprint","IMPRINT",EDGE,{"disambiguationData":[TD([[subQ2,-1.0]])],"derivedFrom":subQ1}),-1.0]])]});}
            var Q396;
            {var subQ0=sQuery(id+"F25.wireOp",EDGE,"E603.trimOffspring");var subQ1=sQuery(id+"F25.wireOp",EDGE,"E446.MirrorCS");var subQ2=makeQuery(id+"F25.imprint","INTERSECT",VERTEX,{"derivedFrom":[subQ1,subQ0]});Q396=makeQuery(id+"F25.imprint","IMPRINT",FACE,{"disambiguationData":[TD([[makeQuery(id+"F25.imprint","IMPRINT",EDGE,{"disambiguationData":[TD([[subQ2,-1.0]])],"derivedFrom":subQ1}),1.0]])]});}
            var Q397;
            {var subQ0=sQuery(id+"F25.wireOp",EDGE,"E602.trimOffspring");var subQ1=sQuery(id+"F25.wireOp",EDGE,"E446.MirrorCS");var subQ2=makeQuery(id+"F25.imprint","INTERSECT",VERTEX,{"derivedFrom":[subQ1,subQ0]});Q397=makeQuery(id+"F25.imprint","IMPRINT",FACE,{"disambiguationData":[TD([[makeQuery(id+"F25.imprint","IMPRINT",EDGE,{"disambiguationData":[TD([[subQ2,-1.0]])],"derivedFrom":subQ1}),1.0]])]});}
            var Q398;
            {var subQ0=sQuery(id+"F25.wireOp",EDGE,"E601.trimOffspring");var subQ1=sQuery(id+"F25.wireOp",EDGE,"E446.MirrorCS");var subQ2=makeQuery(id+"F25.imprint","INTERSECT",VERTEX,{"derivedFrom":[subQ1,subQ0]});Q398=makeQuery(id+"F25.imprint","IMPRINT",FACE,{"disambiguationData":[TD([[makeQuery(id+"F25.imprint","IMPRINT",EDGE,{"disambiguationData":[TD([[subQ2,-1.0]])],"derivedFrom":subQ1}),1.0]])]});}
            var Q399;
            {var subQ0=sQuery(id+"F25.wireOp",EDGE,"E590.trimOffspring");var subQ1=sQuery(id+"F25.wireOp",EDGE,"E446.MirrorCS");var subQ2=makeQuery(id+"F25.imprint","INTERSECT",VERTEX,{"derivedFrom":[subQ1,subQ0]});Q399=makeQuery(id+"F25.imprint","IMPRINT",FACE,{"disambiguationData":[TD([[makeQuery(id+"F25.imprint","IMPRINT",EDGE,{"disambiguationData":[TD([[subQ2,-1.0]])],"derivedFrom":subQ1}),1.0]])]});}
            var Q400;
            {var subQ0=sQuery(id+"F25.wireOp",EDGE,"E593.trimOffspring");var subQ1=sQuery(id+"F25.wireOp",EDGE,"E446.MirrorCS");var subQ2=makeQuery(id+"F25.imprint","INTERSECT",VERTEX,{"derivedFrom":[subQ1,subQ0]});Q400=makeQuery(id+"F25.imprint","IMPRINT",FACE,{"disambiguationData":[TD([[makeQuery(id+"F25.imprint","IMPRINT",EDGE,{"disambiguationData":[TD([[subQ2,-1.0]])],"derivedFrom":subQ1}),1.0]])]});}
            var Q401;
            {var subQ0=sQuery(id+"F25.wireOp",EDGE,"E591.trimOffspring");var subQ1=sQuery(id+"F25.wireOp",EDGE,"E446.MirrorCS");var subQ2=makeQuery(id+"F25.imprint","INTERSECT",VERTEX,{"derivedFrom":[subQ1,subQ0]});Q401=makeQuery(id+"F25.imprint","IMPRINT",FACE,{"disambiguationData":[TD([[makeQuery(id+"F25.imprint","IMPRINT",EDGE,{"disambiguationData":[TD([[subQ2,1.0]])],"derivedFrom":subQ1}),1.0]])]});}
            var Q402;
            {var subQ0=sQuery(id+"F25.wireOp",EDGE,"E591.trimOffspring");var subQ1=sQuery(id+"F25.wireOp",EDGE,"E444.MirrorCS");var subQ2=makeQuery(id+"F25.imprint","INTERSECT",VERTEX,{"derivedFrom":[subQ1,subQ0]});Q402=makeQuery(id+"F25.imprint","IMPRINT",FACE,{"disambiguationData":[TD([[makeQuery(id+"F25.imprint","IMPRINT",EDGE,{"disambiguationData":[TD([[subQ2,1.0]])],"derivedFrom":subQ1}),-1.0]])]});}
            var Q403;
            {var subQ0=sQuery(id+"F25.wireOp",EDGE,"E591.trimOffspring");var subQ1=sQuery(id+"F25.wireOp",EDGE,"E444.MirrorCS");var subQ2=makeQuery(id+"F25.imprint","INTERSECT",VERTEX,{"derivedFrom":[subQ1,subQ0]});Q403=makeQuery(id+"F25.imprint","IMPRINT",FACE,{"disambiguationData":[TD([[makeQuery(id+"F25.imprint","IMPRINT",EDGE,{"disambiguationData":[TD([[subQ2,1.0]])],"derivedFrom":subQ1}),1.0]])]});}
            var Q404;
            {var subQ0=sQuery(id+"F25.wireOp",EDGE,"E591.trimOffspring");var subQ5=sQuery(id+"F25.wireOp",EDGE,"E427.MirrorCS");var subQ6=makeQuery(id+"F25.imprint","INTERSECT",VERTEX,{"derivedFrom":[subQ5,subQ0]});Q404=makeQuery(id+"F25.imprint","IMPRINT",FACE,{"disambiguationData":[TD([[makeQuery(id+"F25.imprint","IMPRINT",EDGE,{"disambiguationData":[TD([[subQ6,1.0]])],"derivedFrom":subQ5}),-1.0]])]});}
            var Q405;
            {var subQ0=sQuery(id+"F25.wireOp",EDGE,"E593.trimOffspring");var subQ5=sQuery(id+"F25.wireOp",EDGE,"E427.MirrorCS");var subQ7=makeQuery(id+"F25.imprint","INTERSECT",VERTEX,{"derivedFrom":[subQ5,subQ0]});Q405=makeQuery(id+"F25.imprint","IMPRINT",FACE,{"disambiguationData":[TD([[makeQuery(id+"F25.imprint","IMPRINT",EDGE,{"disambiguationData":[TD([[subQ7,-1.0]])],"derivedFrom":subQ5}),-1.0]])]});}
            var Q406;
            {var subQ0=sQuery(id+"F25.wireOp",EDGE,"E590.trimOffspring");var subQ5=sQuery(id+"F25.wireOp",EDGE,"E427.MirrorCS");var subQ6=makeQuery(id+"F25.imprint","INTERSECT",VERTEX,{"derivedFrom":[subQ5,subQ0]});Q406=makeQuery(id+"F25.imprint","IMPRINT",FACE,{"disambiguationData":[TD([[makeQuery(id+"F25.imprint","IMPRINT",EDGE,{"disambiguationData":[TD([[subQ6,-1.0]])],"derivedFrom":subQ5}),-1.0]])]});}
            var Q407;
            {var subQ3=sQuery(id+"F25.wireOp",EDGE,"E567.trimOffspring");var subQ5=sQuery(id+"F25.wireOp",EDGE,"E427.MirrorCS");var subQ6=makeQuery(id+"F25.imprint","INTERSECT",VERTEX,{"derivedFrom":[subQ5,subQ3]});Q407=makeQuery(id+"F25.imprint","IMPRINT",FACE,{"disambiguationData":[TD([[makeQuery(id+"F25.imprint","IMPRINT",EDGE,{"disambiguationData":[TD([[subQ6,-1.0]])],"derivedFrom":subQ5}),-1.0]])]});}
            var Q408;
            {var subQ0=sQuery(id+"F25.wireOp",EDGE,"E594.trimOffspring");var subQ5=sQuery(id+"F25.wireOp",EDGE,"E427.MirrorCS");var subQ6=makeQuery(id+"F25.imprint","INTERSECT",VERTEX,{"derivedFrom":[subQ5,subQ0]});Q408=makeQuery(id+"F25.imprint","IMPRINT",FACE,{"disambiguationData":[TD([[makeQuery(id+"F25.imprint","IMPRINT",EDGE,{"disambiguationData":[TD([[subQ6,-1.0]])],"derivedFrom":subQ5}),-1.0]])]});}
            var Q409;
            {var subQ3=sQuery(id+"F25.wireOp",EDGE,"E599.trimOffspring");var subQ5=sQuery(id+"F25.wireOp",EDGE,"E427.MirrorCS");var subQ6=makeQuery(id+"F25.imprint","INTERSECT",VERTEX,{"derivedFrom":[subQ5,subQ3]});Q409=makeQuery(id+"F25.imprint","IMPRINT",FACE,{"disambiguationData":[TD([[makeQuery(id+"F25.imprint","IMPRINT",EDGE,{"disambiguationData":[TD([[subQ6,-1.0]])],"derivedFrom":subQ5}),-1.0]])]});}
            var Q410;
            {var subQ0=sQuery(id+"F25.wireOp",EDGE,"E599.trimOffspring");var subQ1=sQuery(id+"F25.wireOp",EDGE,"E427.MirrorCS");var subQ2=makeQuery(id+"F25.imprint","INTERSECT",VERTEX,{"derivedFrom":[subQ1,subQ0]});Q410=makeQuery(id+"F25.imprint","IMPRINT",FACE,{"disambiguationData":[TD([[makeQuery(id+"F25.imprint","IMPRINT",EDGE,{"disambiguationData":[TD([[subQ2,-1.0]])],"derivedFrom":subQ1}),1.0]])]});}
            var Q411;
            {var subQ0=sQuery(id+"F25.wireOp",EDGE,"E594.trimOffspring");var subQ1=sQuery(id+"F25.wireOp",EDGE,"E427.MirrorCS");var subQ2=makeQuery(id+"F25.imprint","INTERSECT",VERTEX,{"derivedFrom":[subQ1,subQ0]});Q411=makeQuery(id+"F25.imprint","IMPRINT",FACE,{"disambiguationData":[TD([[makeQuery(id+"F25.imprint","IMPRINT",EDGE,{"disambiguationData":[TD([[subQ2,-1.0]])],"derivedFrom":subQ1}),1.0]])]});}
            var Q412;
            {var subQ0=sQuery(id+"F25.wireOp",EDGE,"E567.trimOffspring");var subQ1=sQuery(id+"F25.wireOp",EDGE,"E427.MirrorCS");var subQ2=makeQuery(id+"F25.imprint","INTERSECT",VERTEX,{"derivedFrom":[subQ1,subQ0]});Q412=makeQuery(id+"F25.imprint","IMPRINT",FACE,{"disambiguationData":[TD([[makeQuery(id+"F25.imprint","IMPRINT",EDGE,{"disambiguationData":[TD([[subQ2,-1.0]])],"derivedFrom":subQ1}),1.0]])]});}
            var Q413;
            {var subQ0=sQuery(id+"F25.wireOp",EDGE,"E590.trimOffspring");var subQ1=sQuery(id+"F25.wireOp",EDGE,"E427.MirrorCS");var subQ2=makeQuery(id+"F25.imprint","INTERSECT",VERTEX,{"derivedFrom":[subQ1,subQ0]});Q413=makeQuery(id+"F25.imprint","IMPRINT",FACE,{"disambiguationData":[TD([[makeQuery(id+"F25.imprint","IMPRINT",EDGE,{"disambiguationData":[TD([[subQ2,-1.0]])],"derivedFrom":subQ1}),1.0]])]});}
            var Q414;
            {var subQ0=sQuery(id+"F25.wireOp",EDGE,"E593.trimOffspring");var subQ1=sQuery(id+"F25.wireOp",EDGE,"E427.MirrorCS");var subQ2=makeQuery(id+"F25.imprint","INTERSECT",VERTEX,{"derivedFrom":[subQ1,subQ0]});Q414=makeQuery(id+"F25.imprint","IMPRINT",FACE,{"disambiguationData":[TD([[makeQuery(id+"F25.imprint","IMPRINT",EDGE,{"disambiguationData":[TD([[subQ2,-1.0]])],"derivedFrom":subQ1}),1.0]])]});}
            var Q415;
            {var subQ0=sQuery(id+"F25.wireOp",EDGE,"E591.trimOffspring");var subQ1=sQuery(id+"F25.wireOp",EDGE,"E427.MirrorCS");var subQ2=makeQuery(id+"F25.imprint","INTERSECT",VERTEX,{"derivedFrom":[subQ1,subQ0]});Q415=makeQuery(id+"F25.imprint","IMPRINT",FACE,{"disambiguationData":[TD([[makeQuery(id+"F25.imprint","IMPRINT",EDGE,{"disambiguationData":[TD([[subQ2,1.0]])],"derivedFrom":subQ1}),1.0]])]});}
            var Q416;
            {var subQ0=sQuery(id+"F25.wireOp",EDGE,"E591.trimOffspring");var subQ1=sQuery(id+"F25.wireOp",EDGE,"E440.MirrorCS");var subQ2=makeQuery(id+"F25.imprint","INTERSECT",VERTEX,{"derivedFrom":[subQ1,subQ0]});Q416=makeQuery(id+"F25.imprint","IMPRINT",FACE,{"disambiguationData":[TD([[makeQuery(id+"F25.imprint","IMPRINT",EDGE,{"disambiguationData":[TD([[subQ2,1.0]])],"derivedFrom":subQ1}),1.0]])]});}
            var Q417;
            {var subQ0=sQuery(id+"F25.wireOp",EDGE,"E591.trimOffspring");var subQ1=sQuery(id+"F25.wireOp",EDGE,"E431.MirrorCS");var subQ2=makeQuery(id+"F25.imprint","INTERSECT",VERTEX,{"derivedFrom":[subQ1,subQ0]});Q417=makeQuery(id+"F25.imprint","IMPRINT",FACE,{"disambiguationData":[TD([[makeQuery(id+"F25.imprint","IMPRINT",EDGE,{"disambiguationData":[TD([[subQ2,1.0]])],"derivedFrom":subQ1}),-1.0]])]});}
            var Q418;
            {var subQ0=sQuery(id+"F25.wireOp",EDGE,"E593.trimOffspring");var subQ1=sQuery(id+"F25.wireOp",EDGE,"E440.MirrorCS");var subQ2=makeQuery(id+"F25.imprint","INTERSECT",VERTEX,{"derivedFrom":[subQ1,subQ0]});Q418=makeQuery(id+"F25.imprint","IMPRINT",FACE,{"disambiguationData":[TD([[makeQuery(id+"F25.imprint","IMPRINT",EDGE,{"disambiguationData":[TD([[subQ2,-1.0]])],"derivedFrom":subQ1}),1.0]])]});}
            var Q419;
            {var subQ0=sQuery(id+"F25.wireOp",EDGE,"E593.trimOffspring");var subQ1=sQuery(id+"F25.wireOp",EDGE,"E431.MirrorCS");var subQ2=makeQuery(id+"F25.imprint","INTERSECT",VERTEX,{"derivedFrom":[subQ1,subQ0]});Q419=makeQuery(id+"F25.imprint","IMPRINT",FACE,{"disambiguationData":[TD([[makeQuery(id+"F25.imprint","IMPRINT",EDGE,{"disambiguationData":[TD([[subQ2,-1.0]])],"derivedFrom":subQ1}),-1.0]])]});}
            var Q420;
            {var subQ0=sQuery(id+"F25.wireOp",EDGE,"E590.trimOffspring");var subQ1=sQuery(id+"F25.wireOp",EDGE,"E440.MirrorCS");var subQ2=makeQuery(id+"F25.imprint","INTERSECT",VERTEX,{"derivedFrom":[subQ1,subQ0]});Q420=makeQuery(id+"F25.imprint","IMPRINT",FACE,{"disambiguationData":[TD([[makeQuery(id+"F25.imprint","IMPRINT",EDGE,{"disambiguationData":[TD([[subQ2,-1.0]])],"derivedFrom":subQ1}),1.0]])]});}
            var Q421;
            {var subQ0=sQuery(id+"F25.wireOp",EDGE,"E590.trimOffspring");var subQ1=sQuery(id+"F25.wireOp",EDGE,"E431.MirrorCS");var subQ2=makeQuery(id+"F25.imprint","INTERSECT",VERTEX,{"derivedFrom":[subQ1,subQ0]});Q421=makeQuery(id+"F25.imprint","IMPRINT",FACE,{"disambiguationData":[TD([[makeQuery(id+"F25.imprint","IMPRINT",EDGE,{"disambiguationData":[TD([[subQ2,-1.0]])],"derivedFrom":subQ1}),-1.0]])]});}
            var Q422;
            {var subQ0=sQuery(id+"F25.wireOp",EDGE,"E601.trimOffspring");var subQ5=sQuery(id+"F25.wireOp",EDGE,"E448.MirrorCS");var subQ6=makeQuery(id+"F25.imprint","INTERSECT",VERTEX,{"derivedFrom":[subQ5,subQ0]});Q422=makeQuery(id+"F25.imprint","IMPRINT",FACE,{"disambiguationData":[TD([[makeQuery(id+"F25.imprint","IMPRINT",EDGE,{"disambiguationData":[TD([[subQ6,-1.0]])],"derivedFrom":subQ5}),-1.0]])]});}
            var Q423;
            {var subQ0=sQuery(id+"F25.wireOp",EDGE,"E601.trimOffspring");var subQ1=sQuery(id+"F25.wireOp",EDGE,"E431.MirrorCS");var subQ2=makeQuery(id+"F25.imprint","INTERSECT",VERTEX,{"derivedFrom":[subQ1,subQ0]});Q423=makeQuery(id+"F25.imprint","IMPRINT",FACE,{"disambiguationData":[TD([[makeQuery(id+"F25.imprint","IMPRINT",EDGE,{"disambiguationData":[TD([[subQ2,-1.0]])],"derivedFrom":subQ1}),-1.0]])]});}
            var Q424;
            {var subQ0=sQuery(id+"F25.wireOp",EDGE,"E602.trimOffspring");var subQ5=sQuery(id+"F25.wireOp",EDGE,"E448.MirrorCS");var subQ6=makeQuery(id+"F25.imprint","INTERSECT",VERTEX,{"derivedFrom":[subQ5,subQ0]});Q424=makeQuery(id+"F25.imprint","IMPRINT",FACE,{"disambiguationData":[TD([[makeQuery(id+"F25.imprint","IMPRINT",EDGE,{"disambiguationData":[TD([[subQ6,-1.0]])],"derivedFrom":subQ5}),-1.0]])]});}
            var Q425;
            {var subQ0=sQuery(id+"F25.wireOp",EDGE,"E602.trimOffspring");var subQ1=sQuery(id+"F25.wireOp",EDGE,"E431.MirrorCS");var subQ2=makeQuery(id+"F25.imprint","INTERSECT",VERTEX,{"derivedFrom":[subQ1,subQ0]});Q425=makeQuery(id+"F25.imprint","IMPRINT",FACE,{"disambiguationData":[TD([[makeQuery(id+"F25.imprint","IMPRINT",EDGE,{"disambiguationData":[TD([[subQ2,-1.0]])],"derivedFrom":subQ1}),-1.0]])]});}
            var Q426;
            {var subQ3=sQuery(id+"F25.wireOp",EDGE,"E603.trimOffspring");var subQ5=sQuery(id+"F25.wireOp",EDGE,"E448.MirrorCS");var subQ7=makeQuery(id+"F25.imprint","INTERSECT",VERTEX,{"derivedFrom":[subQ5,subQ3]});Q426=makeQuery(id+"F25.imprint","IMPRINT",FACE,{"disambiguationData":[TD([[makeQuery(id+"F25.imprint","IMPRINT",EDGE,{"disambiguationData":[TD([[subQ7,-1.0]])],"derivedFrom":subQ5}),-1.0]])]});}
            var Q427;
            {var subQ0=sQuery(id+"F25.wireOp",EDGE,"E603.trimOffspring");var subQ1=sQuery(id+"F25.wireOp",EDGE,"E431.MirrorCS");var subQ2=makeQuery(id+"F25.imprint","INTERSECT",VERTEX,{"derivedFrom":[subQ1,subQ0]});Q427=makeQuery(id+"F25.imprint","IMPRINT",FACE,{"disambiguationData":[TD([[makeQuery(id+"F25.imprint","IMPRINT",EDGE,{"disambiguationData":[TD([[subQ2,-1.0]])],"derivedFrom":subQ1}),-1.0]])]});}
            var Q428;
            {var subQ0=sQuery(id+"F25.wireOp",EDGE,"E595.trimOffspring");var subQ1=sQuery(id+"F25.wireOp",EDGE,"E473.trimOffspring");var subQ2=makeQuery(id+"F25.imprint","INTERSECT",VERTEX,{"derivedFrom":[subQ1,subQ0]});Q428=makeQuery(id+"F25.imprint","IMPRINT",FACE,{"disambiguationData":[TD([[makeQuery(id+"F25.imprint","IMPRINT",EDGE,{"disambiguationData":[TD([[subQ2,-1.0]])],"derivedFrom":subQ1}),1.0]])]});}
            var Q429;
            {var subQ0=sQuery(id+"F25.wireOp",EDGE,"E595.trimOffspring");var subQ1=sQuery(id+"F25.wireOp",EDGE,"E474.trimOffspring");var subQ2=makeQuery(id+"F25.imprint","INTERSECT",VERTEX,{"derivedFrom":[subQ1,subQ0]});Q429=makeQuery(id+"F25.imprint","IMPRINT",FACE,{"disambiguationData":[TD([[makeQuery(id+"F25.imprint","IMPRINT",EDGE,{"disambiguationData":[TD([[subQ2,-1.0]])],"derivedFrom":subQ1}),1.0]])]});}
            var Q430;
            {var subQ0=sQuery(id+"F25.wireOp",EDGE,"E593.trimOffspring");var subQ1=sQuery(id+"F25.wireOp",EDGE,"E474.trimOffspring");var subQ2=makeQuery(id+"F25.imprint","INTERSECT",VERTEX,{"derivedFrom":[subQ1,subQ0]});Q430=makeQuery(id+"F25.imprint","IMPRINT",FACE,{"disambiguationData":[TD([[makeQuery(id+"F25.imprint","IMPRINT",EDGE,{"disambiguationData":[TD([[subQ2,-1.0]])],"derivedFrom":subQ1}),1.0]])]});}
            var Q431;
            {var subQ0=sQuery(id+"F25.wireOp",EDGE,"E590.trimOffspring");var subQ1=sQuery(id+"F25.wireOp",EDGE,"E474.trimOffspring");var subQ2=makeQuery(id+"F25.imprint","INTERSECT",VERTEX,{"derivedFrom":[subQ1,subQ0]});Q431=makeQuery(id+"F25.imprint","IMPRINT",FACE,{"disambiguationData":[TD([[makeQuery(id+"F25.imprint","IMPRINT",EDGE,{"disambiguationData":[TD([[subQ2,-1.0]])],"derivedFrom":subQ1}),1.0]])]});}
            var Q432;
            {var subQ0=sQuery(id+"F25.wireOp",EDGE,"E601.trimOffspring");var subQ1=sQuery(id+"F25.wireOp",EDGE,"E474.trimOffspring");var subQ2=makeQuery(id+"F25.imprint","INTERSECT",VERTEX,{"derivedFrom":[subQ1,subQ0]});Q432=makeQuery(id+"F25.imprint","IMPRINT",FACE,{"disambiguationData":[TD([[makeQuery(id+"F25.imprint","IMPRINT",EDGE,{"disambiguationData":[TD([[subQ2,-1.0]])],"derivedFrom":subQ1}),1.0]])]});}
            var Q433;
            {var subQ0=sQuery(id+"F25.wireOp",EDGE,"E601.trimOffspring");var subQ1=sQuery(id+"F25.wireOp",EDGE,"E475.trimOffspring");var subQ2=makeQuery(id+"F25.imprint","INTERSECT",VERTEX,{"derivedFrom":[subQ1,subQ0]});Q433=makeQuery(id+"F25.imprint","IMPRINT",FACE,{"disambiguationData":[TD([[makeQuery(id+"F25.imprint","IMPRINT",EDGE,{"disambiguationData":[TD([[subQ2,-1.0]])],"derivedFrom":subQ1}),-1.0]])]});}
            var Q434;
            {var subQ3=sQuery(id+"F25.wireOp",EDGE,"E601.trimOffspring");var subQ5=sQuery(id+"F25.wireOp",EDGE,"E475.trimOffspring");var subQ6=makeQuery(id+"F25.imprint","INTERSECT",VERTEX,{"derivedFrom":[subQ5,subQ3]});Q434=makeQuery(id+"F25.imprint","IMPRINT",FACE,{"disambiguationData":[TD([[makeQuery(id+"F25.imprint","IMPRINT",EDGE,{"disambiguationData":[TD([[subQ6,-1.0]])],"derivedFrom":subQ5}),1.0]])]});}
            var Q435;
            {var subQ0=sQuery(id+"F25.wireOp",EDGE,"E590.trimOffspring");var subQ5=sQuery(id+"F25.wireOp",EDGE,"E475.trimOffspring");var subQ6=makeQuery(id+"F25.imprint","INTERSECT",VERTEX,{"derivedFrom":[subQ5,subQ0]});Q435=makeQuery(id+"F25.imprint","IMPRINT",FACE,{"disambiguationData":[TD([[makeQuery(id+"F25.imprint","IMPRINT",EDGE,{"disambiguationData":[TD([[subQ6,-1.0]])],"derivedFrom":subQ5}),1.0]])]});}
            var Q436;
            {var subQ3=sQuery(id+"F25.wireOp",EDGE,"E593.trimOffspring");var subQ5=sQuery(id+"F25.wireOp",EDGE,"E475.trimOffspring");var subQ6=makeQuery(id+"F25.imprint","INTERSECT",VERTEX,{"derivedFrom":[subQ5,subQ3]});Q436=makeQuery(id+"F25.imprint","IMPRINT",FACE,{"disambiguationData":[TD([[makeQuery(id+"F25.imprint","IMPRINT",EDGE,{"disambiguationData":[TD([[subQ6,-1.0]])],"derivedFrom":subQ5}),1.0]])]});}
            var Q437;
            {var subQ0=sQuery(id+"F25.wireOp",EDGE,"E458.MirrorCS");var subQ5=sQuery(id+"F25.wireOp",EDGE,"E477.trimOffspring");var subQ6=makeQuery(id+"F25.imprint","INTERSECT",VERTEX,{"derivedFrom":[subQ0,subQ5]});Q437=makeQuery(id+"F25.imprint","IMPRINT",FACE,{"disambiguationData":[TD([[makeQuery(id+"F25.imprint","IMPRINT",EDGE,{"disambiguationData":[TD([[subQ6,-1.0]])],"derivedFrom":subQ5}),-1.0]])]});}
            var Q438;
            {var subQ0=sQuery(id+"F25.wireOp",EDGE,"E616.trimOffspring");var subQ1=sQuery(id+"F25.wireOp",EDGE,"E458.MirrorCS");var subQ2=makeQuery(id+"F25.imprint","INTERSECT",VERTEX,{"derivedFrom":[subQ1,subQ0]});Q438=makeQuery(id+"F25.imprint","IMPRINT",FACE,{"disambiguationData":[TD([[makeQuery(id+"F25.imprint","IMPRINT",EDGE,{"disambiguationData":[TD([[subQ2,-1.0]])],"derivedFrom":subQ1}),1.0]])]});}
            var Q439;
            {var subQ0=sQuery(id+"F25.wireOp",EDGE,"E595.trimOffspring");var subQ5=sQuery(id+"F25.wireOp",EDGE,"E475.trimOffspring");var subQ6=makeQuery(id+"F25.imprint","INTERSECT",VERTEX,{"derivedFrom":[subQ5,subQ0]});Q439=makeQuery(id+"F25.imprint","IMPRINT",FACE,{"disambiguationData":[TD([[makeQuery(id+"F25.imprint","IMPRINT",EDGE,{"disambiguationData":[TD([[subQ6,-1.0]])],"derivedFrom":subQ5}),1.0]])]});}
            var Q440;
            {var subQ0=sQuery(id+"F25.wireOp",EDGE,"E617.trimOffspring");var subQ1=sQuery(id+"F25.wireOp",EDGE,"E458.MirrorCS");var subQ2=makeQuery(id+"F25.imprint","INTERSECT",VERTEX,{"derivedFrom":[subQ1,subQ0]});Q440=makeQuery(id+"F25.imprint","IMPRINT",FACE,{"disambiguationData":[TD([[makeQuery(id+"F25.imprint","IMPRINT",EDGE,{"disambiguationData":[TD([[subQ2,-1.0]])],"derivedFrom":subQ1}),1.0]])]});}
            var Q441;
            {var subQ0=sQuery(id+"F25.wireOp",EDGE,"E617.trimOffspring");var subQ1=sQuery(id+"F25.wireOp",EDGE,"E419.MirrorCS");var subQ2=makeQuery(id+"F25.imprint","INTERSECT",VERTEX,{"derivedFrom":[subQ1,subQ0]});Q441=makeQuery(id+"F25.imprint","IMPRINT",FACE,{"disambiguationData":[TD([[makeQuery(id+"F25.imprint","IMPRINT",EDGE,{"disambiguationData":[TD([[subQ2,-1.0]])],"derivedFrom":subQ1}),-1.0]])]});}
            var Q442;
            {var subQ0=sQuery(id+"F25.wireOp",EDGE,"E617.trimOffspring");var subQ1=sQuery(id+"F25.wireOp",EDGE,"E417.MirrorCS");var subQ2=makeQuery(id+"F25.imprint","INTERSECT",VERTEX,{"derivedFrom":[subQ1,subQ0]});Q442=makeQuery(id+"F25.imprint","IMPRINT",FACE,{"disambiguationData":[TD([[makeQuery(id+"F25.imprint","IMPRINT",EDGE,{"disambiguationData":[TD([[subQ2,-1.0]])],"derivedFrom":subQ1}),-1.0]])]});}
            var Q443;
            {var subQ0=sQuery(id+"F25.wireOp",EDGE,"E617.trimOffspring");var subQ1=sQuery(id+"F25.wireOp",EDGE,"E417.MirrorCS");var subQ2=makeQuery(id+"F25.imprint","INTERSECT",VERTEX,{"derivedFrom":[subQ1,subQ0]});Q443=makeQuery(id+"F25.imprint","IMPRINT",FACE,{"disambiguationData":[TD([[makeQuery(id+"F25.imprint","IMPRINT",EDGE,{"disambiguationData":[TD([[subQ2,-1.0]])],"derivedFrom":subQ1}),1.0]])]});}
            var Q444;
            {var subQ0=sQuery(id+"F25.wireOp",EDGE,"E617.trimOffspring");var subQ1=sQuery(id+"F25.wireOp",EDGE,"E409.MirrorCS");var subQ2=makeQuery(id+"F25.imprint","INTERSECT",VERTEX,{"derivedFrom":[subQ1,subQ0]});Q444=makeQuery(id+"F25.imprint","IMPRINT",FACE,{"disambiguationData":[TD([[makeQuery(id+"F25.imprint","IMPRINT",EDGE,{"disambiguationData":[TD([[subQ2,-1.0]])],"derivedFrom":subQ1}),-1.0]])]});}
            var Q445;
            {var subQ0=sQuery(id+"F25.wireOp",EDGE,"E473.trimOffspring");var subQ1=sQuery(id+"F25.wireOp",EDGE,"E421.MirrorCS");var subQ2=makeQuery(id+"F25.imprint","INTERSECT",VERTEX,{"derivedFrom":[subQ1,subQ0]});Q445=makeQuery(id+"F25.imprint","IMPRINT",FACE,{"disambiguationData":[TD([[makeQuery(id+"F25.imprint","IMPRINT",EDGE,{"disambiguationData":[TD([[subQ2,-1.0]])],"derivedFrom":subQ1}),1.0]])]});}
            var Q446;
            {var subQ0=sQuery(id+"F25.wireOp",EDGE,"E473.trimOffspring");var subQ1=sQuery(id+"F25.wireOp",EDGE,"E416.MirrorCS");var subQ2=makeQuery(id+"F25.imprint","INTERSECT",VERTEX,{"derivedFrom":[subQ1,subQ0]});Q446=makeQuery(id+"F25.imprint","IMPRINT",FACE,{"disambiguationData":[TD([[makeQuery(id+"F25.imprint","IMPRINT",EDGE,{"disambiguationData":[TD([[subQ2,-1.0]])],"derivedFrom":subQ1}),-1.0]])]});}
            var Q447;
            {var subQ0=sQuery(id+"F25.wireOp",EDGE,"E474.trimOffspring");var subQ1=sQuery(id+"F25.wireOp",EDGE,"E421.MirrorCS");var subQ2=makeQuery(id+"F25.imprint","INTERSECT",VERTEX,{"derivedFrom":[subQ1,subQ0]});Q447=makeQuery(id+"F25.imprint","IMPRINT",FACE,{"disambiguationData":[TD([[makeQuery(id+"F25.imprint","IMPRINT",EDGE,{"disambiguationData":[TD([[subQ2,-1.0]])],"derivedFrom":subQ1}),1.0]])]});}
            var Q448;
            {var subQ0=sQuery(id+"F25.wireOp",EDGE,"E474.trimOffspring");var subQ1=sQuery(id+"F25.wireOp",EDGE,"E416.MirrorCS");var subQ2=makeQuery(id+"F25.imprint","INTERSECT",VERTEX,{"derivedFrom":[subQ1,subQ0]});Q448=makeQuery(id+"F25.imprint","IMPRINT",FACE,{"disambiguationData":[TD([[makeQuery(id+"F25.imprint","IMPRINT",EDGE,{"disambiguationData":[TD([[subQ2,-1.0]])],"derivedFrom":subQ1}),-1.0]])]});}
            var Q449;
            {var subQ0=sQuery(id+"F25.wireOp",EDGE,"E476.trimOffspring");var subQ1=sQuery(id+"F25.wireOp",EDGE,"E421.MirrorCS");var subQ2=makeQuery(id+"F25.imprint","INTERSECT",VERTEX,{"derivedFrom":[subQ1,subQ0]});Q449=makeQuery(id+"F25.imprint","IMPRINT",FACE,{"disambiguationData":[TD([[makeQuery(id+"F25.imprint","IMPRINT",EDGE,{"disambiguationData":[TD([[subQ2,-1.0]])],"derivedFrom":subQ1}),1.0]])]});}
            var Q450;
            {var subQ0=sQuery(id+"F25.wireOp",EDGE,"E476.trimOffspring");var subQ1=sQuery(id+"F25.wireOp",EDGE,"E416.MirrorCS");var subQ2=makeQuery(id+"F25.imprint","INTERSECT",VERTEX,{"derivedFrom":[subQ1,subQ0]});Q450=makeQuery(id+"F25.imprint","IMPRINT",FACE,{"disambiguationData":[TD([[makeQuery(id+"F25.imprint","IMPRINT",EDGE,{"disambiguationData":[TD([[subQ2,-1.0]])],"derivedFrom":subQ1}),-1.0]])]});}
            var Q451;
            {var subQ1=sQuery(id+"F25.wireOp",EDGE,"E421.MirrorCS");var subQ3=sQuery(id+"F25.wireOp",EDGE,"E475.trimOffspring");var subQ4=makeQuery(id+"F25.imprint","INTERSECT",VERTEX,{"derivedFrom":[subQ1,subQ3]});Q451=makeQuery(id+"F25.imprint","IMPRINT",FACE,{"disambiguationData":[TD([[makeQuery(id+"F25.imprint","IMPRINT",EDGE,{"disambiguationData":[TD([[subQ4,1.0]])],"derivedFrom":subQ3}),1.0]])]});}
            var Q452;
            {var subQ1=sQuery(id+"F25.wireOp",EDGE,"E416.MirrorCS");var subQ3=sQuery(id+"F25.wireOp",EDGE,"E475.trimOffspring");var subQ4=makeQuery(id+"F25.imprint","INTERSECT",VERTEX,{"derivedFrom":[subQ1,subQ3]});Q452=makeQuery(id+"F25.imprint","IMPRINT",FACE,{"disambiguationData":[TD([[makeQuery(id+"F25.imprint","IMPRINT",EDGE,{"disambiguationData":[TD([[subQ4,-1.0]])],"derivedFrom":subQ3}),1.0]])]});}
            var Q453;
            {var subQ1=sQuery(id+"F25.wireOp",EDGE,"E417.MirrorCS");var subQ3=sQuery(id+"F25.wireOp",EDGE,"E477.trimOffspring");var subQ4=makeQuery(id+"F25.imprint","INTERSECT",VERTEX,{"derivedFrom":[subQ1,subQ3]});Q453=makeQuery(id+"F25.imprint","IMPRINT",FACE,{"disambiguationData":[TD([[makeQuery(id+"F25.imprint","IMPRINT",EDGE,{"disambiguationData":[TD([[subQ4,-1.0]])],"derivedFrom":subQ3}),-1.0]])]});}
            var Q454;
            {var subQ1=sQuery(id+"F25.wireOp",EDGE,"E417.MirrorCS");var subQ3=sQuery(id+"F25.wireOp",EDGE,"E477.trimOffspring");var subQ4=makeQuery(id+"F25.imprint","INTERSECT",VERTEX,{"derivedFrom":[subQ1,subQ3]});Q454=makeQuery(id+"F25.imprint","IMPRINT",FACE,{"disambiguationData":[TD([[makeQuery(id+"F25.imprint","IMPRINT",EDGE,{"disambiguationData":[TD([[subQ4,1.0]])],"derivedFrom":subQ3}),-1.0]])]});}
            var Q455;
            {var subQ0=sQuery(id+"F25.wireOp",EDGE,"E616.trimOffspring");var subQ1=sQuery(id+"F25.wireOp",EDGE,"E417.MirrorCS");var subQ2=makeQuery(id+"F25.imprint","INTERSECT",VERTEX,{"derivedFrom":[subQ1,subQ0]});Q455=makeQuery(id+"F25.imprint","IMPRINT",FACE,{"disambiguationData":[TD([[makeQuery(id+"F25.imprint","IMPRINT",EDGE,{"disambiguationData":[TD([[subQ2,-1.0]])],"derivedFrom":subQ1}),-1.0]])]});}
            var Q456;
            {var subQ0=sQuery(id+"F25.wireOp",EDGE,"E616.trimOffspring");var subQ1=sQuery(id+"F25.wireOp",EDGE,"E417.MirrorCS");var subQ2=makeQuery(id+"F25.imprint","INTERSECT",VERTEX,{"derivedFrom":[subQ1,subQ0]});Q456=makeQuery(id+"F25.imprint","IMPRINT",FACE,{"disambiguationData":[TD([[makeQuery(id+"F25.imprint","IMPRINT",EDGE,{"disambiguationData":[TD([[subQ2,-1.0]])],"derivedFrom":subQ1}),1.0]])]});}
            var Q457;
            {var subQ0=sQuery(id+"F25.wireOp",EDGE,"E334.MirrorCS");var subQ1=sQuery(id+"F25.wireOp",EDGE,"E324.MirrorCS");var subQ2=makeQuery(id+"F25.imprint","INTERSECT",VERTEX,{"derivedFrom":[subQ1,subQ0]});Q457=makeQuery(id+"F25.imprint","IMPRINT",FACE,{"disambiguationData":[TD([[makeQuery(id+"F25.imprint","IMPRINT",EDGE,{"disambiguationData":[TD([[subQ2,-1.0]])],"derivedFrom":subQ1}),-1.0]])]});}
            var Q458;
            {var subQ0=sQuery(id+"F25.wireOp",EDGE,"E315.MirrorCS");Q458=makeQuery(id+"F25.imprint","IMPRINT",FACE,{"disambiguationData":[TD([[makeQuery(id+"F25.imprint","IMPRINT",EDGE,{"derivedFrom":subQ0}),1.0]])]});}
            var Q459;
            {var subQ5=sQuery(id+"F25.wireOp",EDGE,"E315.MirrorCS");Q459=makeQuery(id+"F25.imprint","IMPRINT",FACE,{"disambiguationData":[TD([[makeQuery(id+"F25.imprint","IMPRINT",EDGE,{"derivedFrom":subQ5}),-1.0]])]});}
            var Q460;
            {var subQ5=sQuery(id+"F25.wireOp",EDGE,"E616.trimOffspring");var subQ6=sQuery(id+"F25.wireOp",EDGE,"E409.MirrorCS");var subQ7=makeQuery(id+"F25.imprint","INTERSECT",VERTEX,{"derivedFrom":[subQ6,subQ5]});Q460=makeQuery(id+"F25.imprint","IMPRINT",FACE,{"disambiguationData":[TD([[makeQuery(id+"F25.imprint","IMPRINT",EDGE,{"disambiguationData":[TD([[subQ7,-1.0]])],"derivedFrom":subQ6}),1.0]])]});}
            var Q461;
            {var subQ4=sQuery(id+"F25.wireOp",EDGE,"E222.right");Q461=makeQuery(id+"F25.imprint","IMPRINT",FACE,{"disambiguationData":[TD([[makeQuery(id+"F25.imprint","IMPRINT",EDGE,{"derivedFrom":subQ4}),1.0]])]});}
            var Q462;
            {var subQ0=sQuery(id+"F25.wireOp",EDGE,"E311.MirrorCS");Q462=makeQuery(id+"F25.imprint","IMPRINT",FACE,{"disambiguationData":[TD([[makeQuery(id+"F25.imprint","IMPRINT",EDGE,{"derivedFrom":subQ0}),1.0]])]});}
            var Q463;
            {var subQ1=sQuery(id+"F25.wireOp",EDGE,"E415.MirrorCS");var subQ3=sQuery(id+"F25.wireOp",EDGE,"E475.trimOffspring");var subQ4=makeQuery(id+"F25.imprint","INTERSECT",VERTEX,{"derivedFrom":[subQ1,subQ3]});Q463=makeQuery(id+"F25.imprint","IMPRINT",FACE,{"disambiguationData":[TD([[makeQuery(id+"F25.imprint","IMPRINT",EDGE,{"disambiguationData":[TD([[subQ4,-1.0]])],"derivedFrom":subQ1}),-1.0]])]});}
            var Q464;
            {var subQ5=sQuery(id+"F25.wireOp",EDGE,"E222.right");Q464=makeQuery(id+"F25.imprint","IMPRINT",FACE,{"disambiguationData":[TD([[makeQuery(id+"F25.imprint","IMPRINT",EDGE,{"derivedFrom":subQ5}),-1.0]])]});}
            var Q465;
            {var subQ1=sQuery(id+"F25.wireOp",EDGE,"E249.right");var subQ3=sQuery(id+"F25.wireOp",EDGE,"E284.trimOffspring");var subQ4=makeQuery(id+"F25.imprint","INTERSECT",VERTEX,{"derivedFrom":[subQ1,subQ3]});Q465=makeQuery(id+"F25.imprint","IMPRINT",FACE,{"disambiguationData":[TD([[makeQuery(id+"F25.imprint","IMPRINT",EDGE,{"disambiguationData":[TD([[subQ4,1.0]])],"derivedFrom":subQ3}),1.0]])]});}
            var Q466;
            {var subQ0=sQuery(id+"F25.wireOp",EDGE,"E476.trimOffspring");var subQ1=sQuery(id+"F25.wireOp",EDGE,"E415.MirrorCS");var subQ2=makeQuery(id+"F25.imprint","INTERSECT",VERTEX,{"derivedFrom":[subQ1,subQ0]});Q466=makeQuery(id+"F25.imprint","IMPRINT",FACE,{"disambiguationData":[TD([[makeQuery(id+"F25.imprint","IMPRINT",EDGE,{"disambiguationData":[TD([[subQ2,-1.0]])],"derivedFrom":subQ1}),-1.0]])]});}
            var Q467;
            {var subQ0=sQuery(id+"F25.wireOp",EDGE,"E474.trimOffspring");var subQ1=sQuery(id+"F25.wireOp",EDGE,"E415.MirrorCS");var subQ2=makeQuery(id+"F25.imprint","INTERSECT",VERTEX,{"derivedFrom":[subQ1,subQ0]});Q467=makeQuery(id+"F25.imprint","IMPRINT",FACE,{"disambiguationData":[TD([[makeQuery(id+"F25.imprint","IMPRINT",EDGE,{"disambiguationData":[TD([[subQ2,-1.0]])],"derivedFrom":subQ1}),-1.0]])]});}
            var Q468;
            {var subQ0=sQuery(id+"F25.wireOp",EDGE,"E473.trimOffspring");var subQ1=sQuery(id+"F25.wireOp",EDGE,"E415.MirrorCS");var subQ2=makeQuery(id+"F25.imprint","INTERSECT",VERTEX,{"derivedFrom":[subQ1,subQ0]});Q468=makeQuery(id+"F25.imprint","IMPRINT",FACE,{"disambiguationData":[TD([[makeQuery(id+"F25.imprint","IMPRINT",EDGE,{"disambiguationData":[TD([[subQ2,-1.0]])],"derivedFrom":subQ1}),-1.0]])]});}
            var Q469;
            {var subQ1=sQuery(id+"F25.wireOp",EDGE,"E250.right");var subQ3=sQuery(id+"F25.wireOp",EDGE,"E284.trimOffspring");var subQ4=makeQuery(id+"F25.imprint","INTERSECT",VERTEX,{"derivedFrom":[subQ1,subQ3]});Q469=makeQuery(id+"F25.imprint","IMPRINT",FACE,{"disambiguationData":[TD([[makeQuery(id+"F25.imprint","IMPRINT",EDGE,{"disambiguationData":[TD([[subQ4,1.0]])],"derivedFrom":subQ3}),1.0]])]});}
            var Q470;
            {var subQ3=sQuery(id+"F25.wireOp",EDGE,"E284.trimOffspring");var subQ5=sQuery(id+"F25.wireOp",EDGE,"E251.right");var subQ7=makeQuery(id+"F25.imprint","INTERSECT",VERTEX,{"derivedFrom":[subQ5,subQ3]});Q470=makeQuery(id+"F25.imprint","IMPRINT",FACE,{"disambiguationData":[TD([[makeQuery(id+"F25.imprint","IMPRINT",EDGE,{"disambiguationData":[TD([[subQ7,-1.0]])],"derivedFrom":subQ3}),1.0]])]});}
            var Q471;
            {var subQ3=sQuery(id+"F25.wireOp",EDGE,"E510.trimOffspring");var subQ5=sQuery(id+"F25.wireOp",EDGE,"E249.right");var subQ6=makeQuery(id+"F25.imprint","INTERSECT",VERTEX,{"derivedFrom":[subQ5,subQ3]});Q471=makeQuery(id+"F25.imprint","IMPRINT",FACE,{"disambiguationData":[TD([[makeQuery(id+"F25.imprint","IMPRINT",EDGE,{"disambiguationData":[TD([[subQ6,-1.0]])],"derivedFrom":subQ5}),-1.0]])]});}
            var Q472;
            {var subQ0=sQuery(id+"F25.wireOp",EDGE,"E335.MirrorCS");var subQ5=sQuery(id+"F25.wireOp",EDGE,"E387.MirrorCS");var subQ6=makeQuery(id+"F25.imprint","INTERSECT",VERTEX,{"derivedFrom":[subQ0,subQ5]});Q472=makeQuery(id+"F25.imprint","IMPRINT",FACE,{"disambiguationData":[TD([[makeQuery(id+"F25.imprint","IMPRINT",EDGE,{"disambiguationData":[TD([[subQ6,1.0]])],"derivedFrom":subQ5}),1.0]])]});}
            var Q473;
            {var subQ0=sQuery(id+"F25.wireOp",EDGE,"E234.right");Q473=makeQuery(id+"F25.imprint","IMPRINT",FACE,{"disambiguationData":[TD([[makeQuery(id+"F25.imprint","IMPRINT",EDGE,{"derivedFrom":subQ0}),1.0]])]});}
            var Q474;
            {var subQ0=sQuery(id+"F25.wireOp",EDGE,"E232.right");Q474=makeQuery(id+"F25.imprint","IMPRINT",FACE,{"disambiguationData":[TD([[makeQuery(id+"F25.imprint","IMPRINT",EDGE,{"derivedFrom":subQ0}),-1.0]])]});}
            var Q475;
            {var subQ5=sQuery(id+"F25.wireOp",EDGE,"E234.right");Q475=makeQuery(id+"F25.imprint","IMPRINT",FACE,{"disambiguationData":[TD([[makeQuery(id+"F25.imprint","IMPRINT",EDGE,{"derivedFrom":subQ5}),-1.0]])]});}
            var Q476;
            {var subQ5=sQuery(id+"F25.wireOp",EDGE,"E232.right");Q476=makeQuery(id+"F25.imprint","IMPRINT",FACE,{"disambiguationData":[TD([[makeQuery(id+"F25.imprint","IMPRINT",EDGE,{"derivedFrom":subQ5}),1.0]])]});}
            var Q477;
            {var subQ0=sQuery(id+"F25.wireOp",EDGE,"E522.trimOffspring");var subQ1=sQuery(id+"F25.wireOp",EDGE,"E249.right");var subQ2=makeQuery(id+"F25.imprint","INTERSECT",VERTEX,{"derivedFrom":[subQ1,subQ0]});Q477=makeQuery(id+"F25.imprint","IMPRINT",FACE,{"disambiguationData":[TD([[makeQuery(id+"F25.imprint","IMPRINT",EDGE,{"disambiguationData":[TD([[subQ2,-1.0]])],"derivedFrom":subQ1}),1.0]])]});}
            var Q478;
            {var subQ0=sQuery(id+"F25.wireOp",EDGE,"E524.trimOffspring");var subQ1=sQuery(id+"F25.wireOp",EDGE,"E249.right");var subQ2=makeQuery(id+"F25.imprint","INTERSECT",VERTEX,{"derivedFrom":[subQ1,subQ0]});Q478=makeQuery(id+"F25.imprint","IMPRINT",FACE,{"disambiguationData":[TD([[makeQuery(id+"F25.imprint","IMPRINT",EDGE,{"disambiguationData":[TD([[subQ2,-1.0]])],"derivedFrom":subQ1}),1.0]])]});}
            var Q479;
            {var subQ0=sQuery(id+"F25.wireOp",EDGE,"E522.trimOffspring");var subQ1=sQuery(id+"F25.wireOp",EDGE,"E250.right");var subQ2=makeQuery(id+"F25.imprint","INTERSECT",VERTEX,{"derivedFrom":[subQ1,subQ0]});Q479=makeQuery(id+"F25.imprint","IMPRINT",FACE,{"disambiguationData":[TD([[makeQuery(id+"F25.imprint","IMPRINT",EDGE,{"disambiguationData":[TD([[subQ2,-1.0]])],"derivedFrom":subQ1}),1.0]])]});}
            var Q480;
            {var subQ0=sQuery(id+"F25.wireOp",EDGE,"E522.trimOffspring");var subQ1=sQuery(id+"F25.wireOp",EDGE,"E250.left");var subQ2=makeQuery(id+"F25.imprint","INTERSECT",VERTEX,{"derivedFrom":[subQ1,subQ0]});Q480=makeQuery(id+"F25.imprint","IMPRINT",FACE,{"disambiguationData":[TD([[makeQuery(id+"F25.imprint","IMPRINT",EDGE,{"disambiguationData":[TD([[subQ2,-1.0]])],"derivedFrom":subQ1}),1.0]])]});}
            var Q481;
            {var subQ0=sQuery(id+"F25.wireOp",EDGE,"E524.trimOffspring");var subQ1=sQuery(id+"F25.wireOp",EDGE,"E250.left");var subQ2=makeQuery(id+"F25.imprint","INTERSECT",VERTEX,{"derivedFrom":[subQ1,subQ0]});Q481=makeQuery(id+"F25.imprint","IMPRINT",FACE,{"disambiguationData":[TD([[makeQuery(id+"F25.imprint","IMPRINT",EDGE,{"disambiguationData":[TD([[subQ2,-1.0]])],"derivedFrom":subQ1}),1.0]])]});}
            var Q482;
            {var subQ0=sQuery(id+"F25.wireOp",EDGE,"E524.trimOffspring");var subQ1=sQuery(id+"F25.wireOp",EDGE,"E250.right");var subQ2=makeQuery(id+"F25.imprint","INTERSECT",VERTEX,{"derivedFrom":[subQ1,subQ0]});Q482=makeQuery(id+"F25.imprint","IMPRINT",FACE,{"disambiguationData":[TD([[makeQuery(id+"F25.imprint","IMPRINT",EDGE,{"disambiguationData":[TD([[subQ2,-1.0]])],"derivedFrom":subQ1}),1.0]])]});}
            var Q483;
            {var subQ0=sQuery(id+"F25.wireOp",EDGE,"E525.trimOffspring");var subQ1=sQuery(id+"F25.wireOp",EDGE,"E250.right");var subQ2=makeQuery(id+"F25.imprint","INTERSECT",VERTEX,{"derivedFrom":[subQ1,subQ0]});Q483=makeQuery(id+"F25.imprint","IMPRINT",FACE,{"disambiguationData":[TD([[makeQuery(id+"F25.imprint","IMPRINT",EDGE,{"disambiguationData":[TD([[subQ2,-1.0]])],"derivedFrom":subQ1}),1.0]])]});}
            var Q484;
            {var subQ0=sQuery(id+"F25.wireOp",EDGE,"E334.MirrorCS");var subQ1=sQuery(id+"F25.wireOp",EDGE,"E324.MirrorCS");var subQ2=makeQuery(id+"F25.imprint","INTERSECT",VERTEX,{"derivedFrom":[subQ1,subQ0]});Q484=makeQuery(id+"F25.imprint","IMPRINT",FACE,{"disambiguationData":[TD([[makeQuery(id+"F25.imprint","IMPRINT",EDGE,{"disambiguationData":[TD([[subQ2,-1.0]])],"derivedFrom":subQ1}),1.0]])]});}
            var Q485;
            {var subQ0=sQuery(id+"F25.wireOp",EDGE,"E365.MirrorCS");var subQ1=sQuery(id+"F25.wireOp",EDGE,"E324.MirrorCS");var subQ2=makeQuery(id+"F25.imprint","INTERSECT",VERTEX,{"derivedFrom":[subQ1,subQ0]});Q485=makeQuery(id+"F25.imprint","IMPRINT",FACE,{"disambiguationData":[TD([[makeQuery(id+"F25.imprint","IMPRINT",EDGE,{"disambiguationData":[TD([[subQ2,-1.0]])],"derivedFrom":subQ1}),1.0]])]});}
            var Q486;
            {var subQ0=sQuery(id+"F25.wireOp",EDGE,"E334.MirrorCS");var subQ1=sQuery(id+"F25.wireOp",EDGE,"E349.MirrorCS");var subQ2=makeQuery(id+"F25.imprint","INTERSECT",VERTEX,{"derivedFrom":[subQ1,subQ0]});Q486=makeQuery(id+"F25.imprint","IMPRINT",FACE,{"disambiguationData":[TD([[makeQuery(id+"F25.imprint","IMPRINT",EDGE,{"disambiguationData":[TD([[subQ2,-1.0]])],"derivedFrom":subQ1}),-1.0]])]});}
            var Q487;
            {var subQ0=sQuery(id+"F25.wireOp",EDGE,"E365.MirrorCS");var subQ1=sQuery(id+"F25.wireOp",EDGE,"E349.MirrorCS");var subQ2=makeQuery(id+"F25.imprint","INTERSECT",VERTEX,{"derivedFrom":[subQ1,subQ0]});Q487=makeQuery(id+"F25.imprint","IMPRINT",FACE,{"disambiguationData":[TD([[makeQuery(id+"F25.imprint","IMPRINT",EDGE,{"disambiguationData":[TD([[subQ2,-1.0]])],"derivedFrom":subQ1}),-1.0]])]});}
            var Q488;
            {var subQ0=sQuery(id+"F25.wireOp",EDGE,"E525.trimOffspring");var subQ1=sQuery(id+"F25.wireOp",EDGE,"E250.left");var subQ2=makeQuery(id+"F25.imprint","INTERSECT",VERTEX,{"derivedFrom":[subQ1,subQ0]});Q488=makeQuery(id+"F25.imprint","IMPRINT",FACE,{"disambiguationData":[TD([[makeQuery(id+"F25.imprint","IMPRINT",EDGE,{"disambiguationData":[TD([[subQ2,-1.0]])],"derivedFrom":subQ1}),1.0]])]});}
            var Q489;
            {var subQ0=sQuery(id+"F25.wireOp",EDGE,"E285.trimOffspring");var subQ1=sQuery(id+"F25.wireOp",EDGE,"E250.left");var subQ2=makeQuery(id+"F25.imprint","INTERSECT",VERTEX,{"derivedFrom":[subQ1,subQ0]});Q489=makeQuery(id+"F25.imprint","IMPRINT",FACE,{"disambiguationData":[TD([[makeQuery(id+"F25.imprint","IMPRINT",EDGE,{"disambiguationData":[TD([[subQ2,-1.0]])],"derivedFrom":subQ1}),1.0]])]});}
            var Q490;
            {var subQ0=sQuery(id+"F25.wireOp",EDGE,"E286.trimOffspring");var subQ1=sQuery(id+"F25.wireOp",EDGE,"E250.left");var subQ2=makeQuery(id+"F25.imprint","INTERSECT",VERTEX,{"derivedFrom":[subQ1,subQ0]});Q490=makeQuery(id+"F25.imprint","IMPRINT",FACE,{"disambiguationData":[TD([[makeQuery(id+"F25.imprint","IMPRINT",EDGE,{"disambiguationData":[TD([[subQ2,-1.0]])],"derivedFrom":subQ1}),1.0]])]});}
            var Q491;
            {var subQ0=sQuery(id+"F25.wireOp",EDGE,"E285.trimOffspring");var subQ1=sQuery(id+"F25.wireOp",EDGE,"E250.right");var subQ2=makeQuery(id+"F25.imprint","INTERSECT",VERTEX,{"derivedFrom":[subQ1,subQ0]});Q491=makeQuery(id+"F25.imprint","IMPRINT",FACE,{"disambiguationData":[TD([[makeQuery(id+"F25.imprint","IMPRINT",EDGE,{"disambiguationData":[TD([[subQ2,-1.0]])],"derivedFrom":subQ1}),1.0]])]});}
            var Q492;
            {var subQ0=sQuery(id+"F25.wireOp",EDGE,"E286.trimOffspring");var subQ1=sQuery(id+"F25.wireOp",EDGE,"E250.right");var subQ2=makeQuery(id+"F25.imprint","INTERSECT",VERTEX,{"derivedFrom":[subQ1,subQ0]});Q492=makeQuery(id+"F25.imprint","IMPRINT",FACE,{"disambiguationData":[TD([[makeQuery(id+"F25.imprint","IMPRINT",EDGE,{"disambiguationData":[TD([[subQ2,-1.0]])],"derivedFrom":subQ1}),1.0]])]});}
            var Q493;
            {var subQ0=sQuery(id+"F25.wireOp",EDGE,"E223.right");Q493=makeQuery(id+"F25.imprint","IMPRINT",FACE,{"disambiguationData":[TD([[makeQuery(id+"F25.imprint","IMPRINT",EDGE,{"derivedFrom":subQ0}),1.0]])]});}
            var Q494;
            {var subQ0=sQuery(id+"F25.wireOp",EDGE,"E224.right");Q494=makeQuery(id+"F25.imprint","IMPRINT",FACE,{"disambiguationData":[TD([[makeQuery(id+"F25.imprint","IMPRINT",EDGE,{"derivedFrom":subQ0}),-1.0]])]});}
            var Q495;
            {var subQ5=sQuery(id+"F25.wireOp",EDGE,"E224.right");Q495=makeQuery(id+"F25.imprint","IMPRINT",FACE,{"disambiguationData":[TD([[makeQuery(id+"F25.imprint","IMPRINT",EDGE,{"derivedFrom":subQ5}),1.0]])]});}
            var Q496;
            {var subQ5=sQuery(id+"F25.wireOp",EDGE,"E223.right");Q496=makeQuery(id+"F25.imprint","IMPRINT",FACE,{"disambiguationData":[TD([[makeQuery(id+"F25.imprint","IMPRINT",EDGE,{"derivedFrom":subQ5}),-1.0]])]});}
            var Q497;
            {var subQ0=sQuery(id+"F25.wireOp",EDGE,"E285.trimOffspring");var subQ1=sQuery(id+"F25.wireOp",EDGE,"E249.right");var subQ2=makeQuery(id+"F25.imprint","INTERSECT",VERTEX,{"derivedFrom":[subQ1,subQ0]});Q497=makeQuery(id+"F25.imprint","IMPRINT",FACE,{"disambiguationData":[TD([[makeQuery(id+"F25.imprint","IMPRINT",EDGE,{"disambiguationData":[TD([[subQ2,-1.0]])],"derivedFrom":subQ1}),1.0]])]});}
            var Q498;
            {var subQ0=sQuery(id+"F25.wireOp",EDGE,"E286.trimOffspring");var subQ1=sQuery(id+"F25.wireOp",EDGE,"E249.right");var subQ2=makeQuery(id+"F25.imprint","INTERSECT",VERTEX,{"derivedFrom":[subQ1,subQ0]});Q498=makeQuery(id+"F25.imprint","IMPRINT",FACE,{"disambiguationData":[TD([[makeQuery(id+"F25.imprint","IMPRINT",EDGE,{"disambiguationData":[TD([[subQ2,-1.0]])],"derivedFrom":subQ1}),1.0]])]});}
            var Q499;
            {var subQ0=sQuery(id+"F25.wireOp",EDGE,"E235.right");Q499=makeQuery(id+"F25.imprint","IMPRINT",FACE,{"disambiguationData":[TD([[makeQuery(id+"F25.imprint","IMPRINT",EDGE,{"derivedFrom":subQ0}),-1.0]])]});}
            var Q500;
            {var subQ0=sQuery(id+"F25.wireOp",EDGE,"E299.MirrorCS");Q500=makeQuery(id+"F25.imprint","IMPRINT",FACE,{"disambiguationData":[TD([[makeQuery(id+"F25.imprint","IMPRINT",EDGE,{"derivedFrom":subQ0}),1.0]])]});}
            var Q501;
            {var subQ0=sQuery(id+"F25.wireOp",EDGE,"E364.MirrorCS");var subQ1=sQuery(id+"F25.wireOp",EDGE,"E332.MirrorCS");var subQ2=makeQuery(id+"F25.imprint","INTERSECT",VERTEX,{"derivedFrom":[subQ1,subQ0]});Q501=makeQuery(id+"F25.imprint","IMPRINT",FACE,{"disambiguationData":[TD([[makeQuery(id+"F25.imprint","IMPRINT",EDGE,{"disambiguationData":[TD([[subQ2,-1.0]])],"derivedFrom":subQ1}),-1.0]])]});}
            var Q502;
            {var subQ0=sQuery(id+"F25.wireOp",EDGE,"E340.MirrorCS");var subQ1=sQuery(id+"F25.wireOp",EDGE,"E364.MirrorCS");var subQ2=makeQuery(id+"F25.imprint","INTERSECT",VERTEX,{"derivedFrom":[subQ1,subQ0]});Q502=makeQuery(id+"F25.imprint","IMPRINT",FACE,{"disambiguationData":[TD([[makeQuery(id+"F25.imprint","IMPRINT",EDGE,{"disambiguationData":[TD([[subQ2,-1.0]])],"derivedFrom":subQ1}),1.0]])]});}
            var Q503;
            {var subQ0=sQuery(id+"F25.wireOp",EDGE,"E364.MirrorCS");var subQ1=sQuery(id+"F25.wireOp",EDGE,"E363.MirrorCS");var subQ2=makeQuery(id+"F25.imprint","INTERSECT",VERTEX,{"derivedFrom":[subQ1,subQ0]});Q503=makeQuery(id+"F25.imprint","IMPRINT",FACE,{"disambiguationData":[TD([[makeQuery(id+"F25.imprint","IMPRINT",EDGE,{"disambiguationData":[TD([[subQ2,-1.0]])],"derivedFrom":subQ1}),1.0]])]});}
            var Q504;
            {var subQ0=sQuery(id+"F25.wireOp",EDGE,"E388.MirrorCS");var subQ1=sQuery(id+"F25.wireOp",EDGE,"E332.MirrorCS");var subQ2=makeQuery(id+"F25.imprint","INTERSECT",VERTEX,{"derivedFrom":[subQ1,subQ0]});Q504=makeQuery(id+"F25.imprint","IMPRINT",FACE,{"disambiguationData":[TD([[makeQuery(id+"F25.imprint","IMPRINT",EDGE,{"disambiguationData":[TD([[subQ2,-1.0]])],"derivedFrom":subQ1}),-1.0]])]});}
            var Q505;
            {var subQ0=sQuery(id+"F25.wireOp",EDGE,"E340.MirrorCS");var subQ1=sQuery(id+"F25.wireOp",EDGE,"E364.MirrorCS");var subQ2=makeQuery(id+"F25.imprint","INTERSECT",VERTEX,{"derivedFrom":[subQ1,subQ0]});Q505=makeQuery(id+"F25.imprint","IMPRINT",FACE,{"disambiguationData":[TD([[makeQuery(id+"F25.imprint","IMPRINT",EDGE,{"disambiguationData":[TD([[subQ2,-1.0]])],"derivedFrom":subQ1}),-1.0]])]});}
            var Q506;
            {var subQ0=sQuery(id+"F25.wireOp",EDGE,"E359.MirrorCS");var subQ1=sQuery(id+"F25.wireOp",EDGE,"E332.MirrorCS");var subQ2=makeQuery(id+"F25.imprint","INTERSECT",VERTEX,{"derivedFrom":[subQ1,subQ0]});Q506=makeQuery(id+"F25.imprint","IMPRINT",FACE,{"disambiguationData":[TD([[makeQuery(id+"F25.imprint","IMPRINT",EDGE,{"disambiguationData":[TD([[subQ2,-1.0]])],"derivedFrom":subQ1}),-1.0]])]});}
            var Q507;
            {var subQ0=sQuery(id+"F25.wireOp",EDGE,"E340.MirrorCS");var subQ1=sQuery(id+"F25.wireOp",EDGE,"E359.MirrorCS");var subQ2=makeQuery(id+"F25.imprint","INTERSECT",VERTEX,{"derivedFrom":[subQ1,subQ0]});Q507=makeQuery(id+"F25.imprint","IMPRINT",FACE,{"disambiguationData":[TD([[makeQuery(id+"F25.imprint","IMPRINT",EDGE,{"disambiguationData":[TD([[subQ2,-1.0]])],"derivedFrom":subQ1}),1.0]])]});}
            var Q508;
            {var subQ0=sQuery(id+"F25.wireOp",EDGE,"E342.MirrorCS");var subQ1=sQuery(id+"F25.wireOp",EDGE,"E332.MirrorCS");var subQ2=makeQuery(id+"F25.imprint","INTERSECT",VERTEX,{"derivedFrom":[subQ1,subQ0]});Q508=makeQuery(id+"F25.imprint","IMPRINT",FACE,{"disambiguationData":[TD([[makeQuery(id+"F25.imprint","IMPRINT",EDGE,{"disambiguationData":[TD([[subQ2,-1.0]])],"derivedFrom":subQ1}),-1.0]])]});}
            var Q509;
            {var subQ0=sQuery(id+"F25.wireOp",EDGE,"E340.MirrorCS");var subQ1=sQuery(id+"F25.wireOp",EDGE,"E342.MirrorCS");var subQ2=makeQuery(id+"F25.imprint","INTERSECT",VERTEX,{"derivedFrom":[subQ1,subQ0]});Q509=makeQuery(id+"F25.imprint","IMPRINT",FACE,{"disambiguationData":[TD([[makeQuery(id+"F25.imprint","IMPRINT",EDGE,{"disambiguationData":[TD([[subQ2,-1.0]])],"derivedFrom":subQ1}),1.0]])]});}
            var Q510;
            {var subQ0=sQuery(id+"F25.wireOp",EDGE,"E332.MirrorCS");var subQ1=sQuery(id+"F25.wireOp",EDGE,"E328.MirrorCS");var subQ2=makeQuery(id+"F25.imprint","INTERSECT",VERTEX,{"derivedFrom":[subQ1,subQ0]});Q510=makeQuery(id+"F25.imprint","IMPRINT",FACE,{"disambiguationData":[TD([[makeQuery(id+"F25.imprint","IMPRINT",EDGE,{"disambiguationData":[TD([[subQ2,-1.0]])],"derivedFrom":subQ1}),1.0]])]});}
            var Q511;
            {var subQ0=sQuery(id+"F25.wireOp",EDGE,"E340.MirrorCS");var subQ1=sQuery(id+"F25.wireOp",EDGE,"E328.MirrorCS");var subQ2=makeQuery(id+"F25.imprint","INTERSECT",VERTEX,{"derivedFrom":[subQ1,subQ0]});Q511=makeQuery(id+"F25.imprint","IMPRINT",FACE,{"disambiguationData":[TD([[makeQuery(id+"F25.imprint","IMPRINT",EDGE,{"disambiguationData":[TD([[subQ2,-1.0]])],"derivedFrom":subQ1}),1.0]])]});}
            var Q512;
            {var subQ0=sQuery(id+"F25.wireOp",EDGE,"E340.MirrorCS");var subQ1=sQuery(id+"F25.wireOp",EDGE,"E328.MirrorCS");var subQ2=makeQuery(id+"F25.imprint","INTERSECT",VERTEX,{"derivedFrom":[subQ1,subQ0]});Q512=makeQuery(id+"F25.imprint","IMPRINT",FACE,{"disambiguationData":[TD([[makeQuery(id+"F25.imprint","IMPRINT",EDGE,{"disambiguationData":[TD([[subQ2,-1.0]])],"derivedFrom":subQ1}),-1.0]])]});}
            var Q513;
            {var subQ0=sQuery(id+"F25.wireOp",EDGE,"E332.MirrorCS");var subQ1=sQuery(id+"F25.wireOp",EDGE,"E328.MirrorCS");var subQ2=makeQuery(id+"F25.imprint","INTERSECT",VERTEX,{"derivedFrom":[subQ1,subQ0]});Q513=makeQuery(id+"F25.imprint","IMPRINT",FACE,{"disambiguationData":[TD([[makeQuery(id+"F25.imprint","IMPRINT",EDGE,{"disambiguationData":[TD([[subQ2,-1.0]])],"derivedFrom":subQ1}),-1.0]])]});}
            var Q514;
            {var subQ0=sQuery(id+"F25.wireOp",EDGE,"E358.MirrorCS");var subQ1=sQuery(id+"F25.wireOp",EDGE,"E332.MirrorCS");var subQ2=makeQuery(id+"F25.imprint","INTERSECT",VERTEX,{"derivedFrom":[subQ1,subQ0]});Q514=makeQuery(id+"F25.imprint","IMPRINT",FACE,{"disambiguationData":[TD([[makeQuery(id+"F25.imprint","IMPRINT",EDGE,{"disambiguationData":[TD([[subQ2,-1.0]])],"derivedFrom":subQ1}),-1.0]])]});}
            var Q515;
            {var subQ0=sQuery(id+"F25.wireOp",EDGE,"E340.MirrorCS");var subQ1=sQuery(id+"F25.wireOp",EDGE,"E358.MirrorCS");var subQ2=makeQuery(id+"F25.imprint","INTERSECT",VERTEX,{"derivedFrom":[subQ1,subQ0]});Q515=makeQuery(id+"F25.imprint","IMPRINT",FACE,{"disambiguationData":[TD([[makeQuery(id+"F25.imprint","IMPRINT",EDGE,{"disambiguationData":[TD([[subQ2,-1.0]])],"derivedFrom":subQ1}),1.0]])]});}
            var Q516;
            {var subQ0=sQuery(id+"F25.wireOp",EDGE,"E364.MirrorCS");var subQ1=sQuery(id+"F25.wireOp",EDGE,"E331.MirrorCS");var subQ2=makeQuery(id+"F25.imprint","INTERSECT",VERTEX,{"derivedFrom":[subQ1,subQ0]});Q516=makeQuery(id+"F25.imprint","IMPRINT",FACE,{"disambiguationData":[TD([[makeQuery(id+"F25.imprint","IMPRINT",EDGE,{"disambiguationData":[TD([[subQ2,-1.0]])],"derivedFrom":subQ1}),1.0]])]});}
            var Q517;
            {var subQ0=sQuery(id+"F25.wireOp",EDGE,"E388.MirrorCS");var subQ1=sQuery(id+"F25.wireOp",EDGE,"E331.MirrorCS");var subQ2=makeQuery(id+"F25.imprint","INTERSECT",VERTEX,{"derivedFrom":[subQ1,subQ0]});Q517=makeQuery(id+"F25.imprint","IMPRINT",FACE,{"disambiguationData":[TD([[makeQuery(id+"F25.imprint","IMPRINT",EDGE,{"disambiguationData":[TD([[subQ2,-1.0]])],"derivedFrom":subQ1}),1.0]])]});}
            var Q518;
            {var subQ0=sQuery(id+"F25.wireOp",EDGE,"E364.MirrorCS");var subQ1=sQuery(id+"F25.wireOp",EDGE,"E331.MirrorCS");var subQ2=makeQuery(id+"F25.imprint","INTERSECT",VERTEX,{"derivedFrom":[subQ1,subQ0]});Q518=makeQuery(id+"F25.imprint","IMPRINT",FACE,{"disambiguationData":[TD([[makeQuery(id+"F25.imprint","IMPRINT",EDGE,{"disambiguationData":[TD([[subQ2,-1.0]])],"derivedFrom":subQ1}),-1.0]])]});}
            var Q519;
            {var subQ0=sQuery(id+"F25.wireOp",EDGE,"E388.MirrorCS");var subQ1=sQuery(id+"F25.wireOp",EDGE,"E331.MirrorCS");var subQ2=makeQuery(id+"F25.imprint","INTERSECT",VERTEX,{"derivedFrom":[subQ1,subQ0]});Q519=makeQuery(id+"F25.imprint","IMPRINT",FACE,{"disambiguationData":[TD([[makeQuery(id+"F25.imprint","IMPRINT",EDGE,{"disambiguationData":[TD([[subQ2,-1.0]])],"derivedFrom":subQ1}),-1.0]])]});}
            var Q520;
            {var subQ0=sQuery(id+"F25.wireOp",EDGE,"E359.MirrorCS");var subQ1=sQuery(id+"F25.wireOp",EDGE,"E331.MirrorCS");var subQ2=makeQuery(id+"F25.imprint","INTERSECT",VERTEX,{"derivedFrom":[subQ1,subQ0]});Q520=makeQuery(id+"F25.imprint","IMPRINT",FACE,{"disambiguationData":[TD([[makeQuery(id+"F25.imprint","IMPRINT",EDGE,{"disambiguationData":[TD([[subQ2,-1.0]])],"derivedFrom":subQ1}),1.0]])]});}
            var Q521;
            {var subQ0=sQuery(id+"F25.wireOp",EDGE,"E363.MirrorCS");var subQ1=sQuery(id+"F25.wireOp",EDGE,"E342.MirrorCS");var subQ2=makeQuery(id+"F25.imprint","INTERSECT",VERTEX,{"derivedFrom":[subQ1,subQ0]});Q521=makeQuery(id+"F25.imprint","IMPRINT",FACE,{"disambiguationData":[TD([[makeQuery(id+"F25.imprint","IMPRINT",EDGE,{"disambiguationData":[TD([[subQ2,-1.0]])],"derivedFrom":subQ1}),1.0]])]});}
            var Q522;
            {var subQ0=sQuery(id+"F25.wireOp",EDGE,"E363.MirrorCS");var subQ1=sQuery(id+"F25.wireOp",EDGE,"E328.MirrorCS");var subQ2=makeQuery(id+"F25.imprint","INTERSECT",VERTEX,{"derivedFrom":[subQ1,subQ0]});Q522=makeQuery(id+"F25.imprint","IMPRINT",FACE,{"disambiguationData":[TD([[makeQuery(id+"F25.imprint","IMPRINT",EDGE,{"disambiguationData":[TD([[subQ2,-1.0]])],"derivedFrom":subQ1}),1.0]])]});}
            var Q523;
            {var subQ0=sQuery(id+"F25.wireOp",EDGE,"E363.MirrorCS");var subQ1=sQuery(id+"F25.wireOp",EDGE,"E328.MirrorCS");var subQ2=makeQuery(id+"F25.imprint","INTERSECT",VERTEX,{"derivedFrom":[subQ1,subQ0]});Q523=makeQuery(id+"F25.imprint","IMPRINT",FACE,{"disambiguationData":[TD([[makeQuery(id+"F25.imprint","IMPRINT",EDGE,{"disambiguationData":[TD([[subQ2,-1.0]])],"derivedFrom":subQ1}),-1.0]])]});}
            var Q524;
            {var subQ0=sQuery(id+"F25.wireOp",EDGE,"E358.MirrorCS");var subQ1=sQuery(id+"F25.wireOp",EDGE,"E331.MirrorCS");var subQ2=makeQuery(id+"F25.imprint","INTERSECT",VERTEX,{"derivedFrom":[subQ1,subQ0]});Q524=makeQuery(id+"F25.imprint","IMPRINT",FACE,{"disambiguationData":[TD([[makeQuery(id+"F25.imprint","IMPRINT",EDGE,{"disambiguationData":[TD([[subQ2,-1.0]])],"derivedFrom":subQ1}),1.0]])]});}
            var Q525;
            {var subQ0=sQuery(id+"F25.wireOp",EDGE,"E359.MirrorCS");var subQ1=sQuery(id+"F25.wireOp",EDGE,"E331.MirrorCS");var subQ2=makeQuery(id+"F25.imprint","INTERSECT",VERTEX,{"derivedFrom":[subQ1,subQ0]});Q525=makeQuery(id+"F25.imprint","IMPRINT",FACE,{"disambiguationData":[TD([[makeQuery(id+"F25.imprint","IMPRINT",EDGE,{"disambiguationData":[TD([[subQ2,-1.0]])],"derivedFrom":subQ1}),-1.0]])]});}
            var Q526;
            {var subQ0=sQuery(id+"F25.wireOp",EDGE,"E331.MirrorCS");var subQ1=sQuery(id+"F25.wireOp",EDGE,"E342.MirrorCS");var subQ2=makeQuery(id+"F25.imprint","INTERSECT",VERTEX,{"derivedFrom":[subQ1,subQ0]});Q526=makeQuery(id+"F25.imprint","IMPRINT",FACE,{"disambiguationData":[TD([[makeQuery(id+"F25.imprint","IMPRINT",EDGE,{"disambiguationData":[TD([[subQ2,-1.0]])],"derivedFrom":subQ1}),1.0]])]});}
            var Q527;
            {var subQ0=sQuery(id+"F25.wireOp",EDGE,"E331.MirrorCS");var subQ1=sQuery(id+"F25.wireOp",EDGE,"E328.MirrorCS");var subQ2=makeQuery(id+"F25.imprint","INTERSECT",VERTEX,{"derivedFrom":[subQ1,subQ0]});Q527=makeQuery(id+"F25.imprint","IMPRINT",FACE,{"disambiguationData":[TD([[makeQuery(id+"F25.imprint","IMPRINT",EDGE,{"disambiguationData":[TD([[subQ2,-1.0]])],"derivedFrom":subQ1}),1.0]])]});}
            var Q528;
            {var subQ0=sQuery(id+"F25.wireOp",EDGE,"E331.MirrorCS");var subQ1=sQuery(id+"F25.wireOp",EDGE,"E328.MirrorCS");var subQ2=makeQuery(id+"F25.imprint","INTERSECT",VERTEX,{"derivedFrom":[subQ1,subQ0]});Q528=makeQuery(id+"F25.imprint","IMPRINT",FACE,{"disambiguationData":[TD([[makeQuery(id+"F25.imprint","IMPRINT",EDGE,{"disambiguationData":[TD([[subQ2,-1.0]])],"derivedFrom":subQ1}),-1.0]])]});}
            var Q529;
            {var subQ0=sQuery(id+"F25.wireOp",EDGE,"E358.MirrorCS");var subQ1=sQuery(id+"F25.wireOp",EDGE,"E331.MirrorCS");var subQ2=makeQuery(id+"F25.imprint","INTERSECT",VERTEX,{"derivedFrom":[subQ1,subQ0]});Q529=makeQuery(id+"F25.imprint","IMPRINT",FACE,{"disambiguationData":[TD([[makeQuery(id+"F25.imprint","IMPRINT",EDGE,{"disambiguationData":[TD([[subQ2,-1.0]])],"derivedFrom":subQ1}),-1.0]])]});}
            var Q530;
            {var subQ0=sQuery(id+"F25.wireOp",EDGE,"E364.MirrorCS");var subQ1=sQuery(id+"F25.wireOp",EDGE,"E329.MirrorCS");var subQ2=makeQuery(id+"F25.imprint","INTERSECT",VERTEX,{"derivedFrom":[subQ1,subQ0]});Q530=makeQuery(id+"F25.imprint","IMPRINT",FACE,{"disambiguationData":[TD([[makeQuery(id+"F25.imprint","IMPRINT",EDGE,{"disambiguationData":[TD([[subQ2,-1.0]])],"derivedFrom":subQ1}),1.0]])]});}
            var Q531;
            {var subQ0=sQuery(id+"F25.wireOp",EDGE,"E364.MirrorCS");var subQ1=sQuery(id+"F25.wireOp",EDGE,"E329.MirrorCS");var subQ2=makeQuery(id+"F25.imprint","INTERSECT",VERTEX,{"derivedFrom":[subQ1,subQ0]});Q531=makeQuery(id+"F25.imprint","IMPRINT",FACE,{"disambiguationData":[TD([[makeQuery(id+"F25.imprint","IMPRINT",EDGE,{"disambiguationData":[TD([[subQ2,-1.0]])],"derivedFrom":subQ1}),-1.0]])]});}
            var Q532;
            {var subQ0=sQuery(id+"F25.wireOp",EDGE,"E364.MirrorCS");var subQ1=sQuery(id+"F25.wireOp",EDGE,"E354.MirrorCS");var subQ2=makeQuery(id+"F25.imprint","INTERSECT",VERTEX,{"derivedFrom":[subQ1,subQ0]});Q532=makeQuery(id+"F25.imprint","IMPRINT",FACE,{"disambiguationData":[TD([[makeQuery(id+"F25.imprint","IMPRINT",EDGE,{"disambiguationData":[TD([[subQ2,-1.0]])],"derivedFrom":subQ1}),1.0]])]});}
            var Q533;
            {var subQ0=sQuery(id+"F25.wireOp",EDGE,"E388.MirrorCS");var subQ1=sQuery(id+"F25.wireOp",EDGE,"E329.MirrorCS");var subQ2=makeQuery(id+"F25.imprint","INTERSECT",VERTEX,{"derivedFrom":[subQ1,subQ0]});Q533=makeQuery(id+"F25.imprint","IMPRINT",FACE,{"disambiguationData":[TD([[makeQuery(id+"F25.imprint","IMPRINT",EDGE,{"disambiguationData":[TD([[subQ2,-1.0]])],"derivedFrom":subQ1}),-1.0]])]});}
            var Q534;
            {var subQ0=sQuery(id+"F25.wireOp",EDGE,"E388.MirrorCS");var subQ1=sQuery(id+"F25.wireOp",EDGE,"E354.MirrorCS");var subQ2=makeQuery(id+"F25.imprint","INTERSECT",VERTEX,{"derivedFrom":[subQ1,subQ0]});Q534=makeQuery(id+"F25.imprint","IMPRINT",FACE,{"disambiguationData":[TD([[makeQuery(id+"F25.imprint","IMPRINT",EDGE,{"disambiguationData":[TD([[subQ2,-1.0]])],"derivedFrom":subQ1}),1.0]])]});}
            var Q535;
            {var subQ0=sQuery(id+"F25.wireOp",EDGE,"E359.MirrorCS");var subQ1=sQuery(id+"F25.wireOp",EDGE,"E329.MirrorCS");var subQ2=makeQuery(id+"F25.imprint","INTERSECT",VERTEX,{"derivedFrom":[subQ1,subQ0]});Q535=makeQuery(id+"F25.imprint","IMPRINT",FACE,{"disambiguationData":[TD([[makeQuery(id+"F25.imprint","IMPRINT",EDGE,{"disambiguationData":[TD([[subQ2,-1.0]])],"derivedFrom":subQ1}),-1.0]])]});}
            var Q536;
            {var subQ0=sQuery(id+"F25.wireOp",EDGE,"E359.MirrorCS");var subQ1=sQuery(id+"F25.wireOp",EDGE,"E354.MirrorCS");var subQ2=makeQuery(id+"F25.imprint","INTERSECT",VERTEX,{"derivedFrom":[subQ1,subQ0]});Q536=makeQuery(id+"F25.imprint","IMPRINT",FACE,{"disambiguationData":[TD([[makeQuery(id+"F25.imprint","IMPRINT",EDGE,{"disambiguationData":[TD([[subQ2,-1.0]])],"derivedFrom":subQ1}),1.0]])]});}
            var Q537;
            {var subQ0=sQuery(id+"F25.wireOp",EDGE,"E342.MirrorCS");var subQ1=sQuery(id+"F25.wireOp",EDGE,"E329.MirrorCS");var subQ2=makeQuery(id+"F25.imprint","INTERSECT",VERTEX,{"derivedFrom":[subQ1,subQ0]});Q537=makeQuery(id+"F25.imprint","IMPRINT",FACE,{"disambiguationData":[TD([[makeQuery(id+"F25.imprint","IMPRINT",EDGE,{"disambiguationData":[TD([[subQ2,-1.0]])],"derivedFrom":subQ1}),-1.0]])]});}
            var Q538;
            {var subQ0=sQuery(id+"F25.wireOp",EDGE,"E345.MirrorCS");var subQ1=sQuery(id+"F25.wireOp",EDGE,"E342.MirrorCS");var subQ2=makeQuery(id+"F25.imprint","INTERSECT",VERTEX,{"derivedFrom":[subQ1,subQ0]});Q538=makeQuery(id+"F25.imprint","IMPRINT",FACE,{"disambiguationData":[TD([[makeQuery(id+"F25.imprint","IMPRINT",EDGE,{"disambiguationData":[TD([[subQ2,-1.0]])],"derivedFrom":subQ1}),1.0]])]});}
            var Q539;
            {var subQ0=sQuery(id+"F25.wireOp",EDGE,"E329.MirrorCS");var subQ1=sQuery(id+"F25.wireOp",EDGE,"E328.MirrorCS");var subQ2=makeQuery(id+"F25.imprint","INTERSECT",VERTEX,{"derivedFrom":[subQ1,subQ0]});Q539=makeQuery(id+"F25.imprint","IMPRINT",FACE,{"disambiguationData":[TD([[makeQuery(id+"F25.imprint","IMPRINT",EDGE,{"disambiguationData":[TD([[subQ2,-1.0]])],"derivedFrom":subQ1}),1.0]])]});}
            var Q540;
            {var subQ0=sQuery(id+"F25.wireOp",EDGE,"E345.MirrorCS");var subQ1=sQuery(id+"F25.wireOp",EDGE,"E328.MirrorCS");var subQ2=makeQuery(id+"F25.imprint","INTERSECT",VERTEX,{"derivedFrom":[subQ1,subQ0]});Q540=makeQuery(id+"F25.imprint","IMPRINT",FACE,{"disambiguationData":[TD([[makeQuery(id+"F25.imprint","IMPRINT",EDGE,{"disambiguationData":[TD([[subQ2,-1.0]])],"derivedFrom":subQ1}),1.0]])]});}
            var Q541;
            {var subQ0=sQuery(id+"F25.wireOp",EDGE,"E329.MirrorCS");var subQ1=sQuery(id+"F25.wireOp",EDGE,"E328.MirrorCS");var subQ2=makeQuery(id+"F25.imprint","INTERSECT",VERTEX,{"derivedFrom":[subQ1,subQ0]});Q541=makeQuery(id+"F25.imprint","IMPRINT",FACE,{"disambiguationData":[TD([[makeQuery(id+"F25.imprint","IMPRINT",EDGE,{"disambiguationData":[TD([[subQ2,-1.0]])],"derivedFrom":subQ1}),-1.0]])]});}
            var Q542;
            {var subQ0=sQuery(id+"F25.wireOp",EDGE,"E345.MirrorCS");var subQ1=sQuery(id+"F25.wireOp",EDGE,"E328.MirrorCS");var subQ2=makeQuery(id+"F25.imprint","INTERSECT",VERTEX,{"derivedFrom":[subQ1,subQ0]});Q542=makeQuery(id+"F25.imprint","IMPRINT",FACE,{"disambiguationData":[TD([[makeQuery(id+"F25.imprint","IMPRINT",EDGE,{"disambiguationData":[TD([[subQ2,-1.0]])],"derivedFrom":subQ1}),-1.0]])]});}
            var Q543;
            {var subQ0=sQuery(id+"F25.wireOp",EDGE,"E358.MirrorCS");var subQ1=sQuery(id+"F25.wireOp",EDGE,"E329.MirrorCS");var subQ2=makeQuery(id+"F25.imprint","INTERSECT",VERTEX,{"derivedFrom":[subQ1,subQ0]});Q543=makeQuery(id+"F25.imprint","IMPRINT",FACE,{"disambiguationData":[TD([[makeQuery(id+"F25.imprint","IMPRINT",EDGE,{"disambiguationData":[TD([[subQ2,-1.0]])],"derivedFrom":subQ1}),-1.0]])]});}
            var Q544;
            {var subQ0=sQuery(id+"F25.wireOp",EDGE,"E358.MirrorCS");var subQ1=sQuery(id+"F25.wireOp",EDGE,"E354.MirrorCS");var subQ2=makeQuery(id+"F25.imprint","INTERSECT",VERTEX,{"derivedFrom":[subQ1,subQ0]});Q544=makeQuery(id+"F25.imprint","IMPRINT",FACE,{"disambiguationData":[TD([[makeQuery(id+"F25.imprint","IMPRINT",EDGE,{"disambiguationData":[TD([[subQ2,-1.0]])],"derivedFrom":subQ1}),1.0]])]});}
            var Q545;
            {var subQ0=sQuery(id+"F25.wireOp",EDGE,"E358.MirrorCS");var subQ1=sQuery(id+"F25.wireOp",EDGE,"E354.MirrorCS");var subQ2=makeQuery(id+"F25.imprint","INTERSECT",VERTEX,{"derivedFrom":[subQ1,subQ0]});Q545=makeQuery(id+"F25.imprint","IMPRINT",FACE,{"disambiguationData":[TD([[makeQuery(id+"F25.imprint","IMPRINT",EDGE,{"disambiguationData":[TD([[subQ2,-1.0]])],"derivedFrom":subQ1}),-1.0]])]});}
            var Q546;
            {var subQ0=sQuery(id+"F25.wireOp",EDGE,"E384.MirrorCS");var subQ1=sQuery(id+"F25.wireOp",EDGE,"E358.MirrorCS");var subQ2=makeQuery(id+"F25.imprint","INTERSECT",VERTEX,{"derivedFrom":[subQ1,subQ0]});Q546=makeQuery(id+"F25.imprint","IMPRINT",FACE,{"disambiguationData":[TD([[makeQuery(id+"F25.imprint","IMPRINT",EDGE,{"disambiguationData":[TD([[subQ2,-1.0]])],"derivedFrom":subQ1}),1.0]])]});}
            var Q547;
            {var subQ0=sQuery(id+"F25.wireOp",EDGE,"E373.MirrorCS");var subQ1=sQuery(id+"F25.wireOp",EDGE,"E342.MirrorCS");var subQ2=makeQuery(id+"F25.imprint","INTERSECT",VERTEX,{"derivedFrom":[subQ1,subQ0]});Q547=makeQuery(id+"F25.imprint","IMPRINT",FACE,{"disambiguationData":[TD([[makeQuery(id+"F25.imprint","IMPRINT",EDGE,{"disambiguationData":[TD([[subQ2,-1.0]])],"derivedFrom":subQ1}),1.0]])]});}
            var Q548;
            {var subQ0=sQuery(id+"F25.wireOp",EDGE,"E344.MirrorCS");var subQ1=sQuery(id+"F25.wireOp",EDGE,"E342.MirrorCS");var subQ2=makeQuery(id+"F25.imprint","INTERSECT",VERTEX,{"derivedFrom":[subQ1,subQ0]});Q548=makeQuery(id+"F25.imprint","IMPRINT",FACE,{"disambiguationData":[TD([[makeQuery(id+"F25.imprint","IMPRINT",EDGE,{"disambiguationData":[TD([[subQ2,-1.0]])],"derivedFrom":subQ1}),1.0]])]});}
            var Q549;
            {var subQ0=sQuery(id+"F25.wireOp",EDGE,"E344.MirrorCS");var subQ1=sQuery(id+"F25.wireOp",EDGE,"E328.MirrorCS");var subQ2=makeQuery(id+"F25.imprint","INTERSECT",VERTEX,{"derivedFrom":[subQ1,subQ0]});Q549=makeQuery(id+"F25.imprint","IMPRINT",FACE,{"disambiguationData":[TD([[makeQuery(id+"F25.imprint","IMPRINT",EDGE,{"disambiguationData":[TD([[subQ2,-1.0]])],"derivedFrom":subQ1}),1.0]])]});}
            var Q550;
            {var subQ0=sQuery(id+"F25.wireOp",EDGE,"E344.MirrorCS");var subQ1=sQuery(id+"F25.wireOp",EDGE,"E328.MirrorCS");var subQ2=makeQuery(id+"F25.imprint","INTERSECT",VERTEX,{"derivedFrom":[subQ1,subQ0]});Q550=makeQuery(id+"F25.imprint","IMPRINT",FACE,{"disambiguationData":[TD([[makeQuery(id+"F25.imprint","IMPRINT",EDGE,{"disambiguationData":[TD([[subQ2,-1.0]])],"derivedFrom":subQ1}),-1.0]])]});}
            var Q551;
            {var subQ0=sQuery(id+"F25.wireOp",EDGE,"E344.MirrorCS");var subQ1=sQuery(id+"F25.wireOp",EDGE,"E358.MirrorCS");var subQ2=makeQuery(id+"F25.imprint","INTERSECT",VERTEX,{"derivedFrom":[subQ1,subQ0]});Q551=makeQuery(id+"F25.imprint","IMPRINT",FACE,{"disambiguationData":[TD([[makeQuery(id+"F25.imprint","IMPRINT",EDGE,{"disambiguationData":[TD([[subQ2,-1.0]])],"derivedFrom":subQ1}),1.0]])]});}
            var Q552;
            {var subQ0=sQuery(id+"F25.wireOp",EDGE,"E378.MirrorCS");var subQ1=sQuery(id+"F25.wireOp",EDGE,"E342.MirrorCS");var subQ2=makeQuery(id+"F25.imprint","INTERSECT",VERTEX,{"derivedFrom":[subQ1,subQ0]});Q552=makeQuery(id+"F25.imprint","IMPRINT",FACE,{"disambiguationData":[TD([[makeQuery(id+"F25.imprint","IMPRINT",EDGE,{"disambiguationData":[TD([[subQ2,-1.0]])],"derivedFrom":subQ1}),1.0]])]});}
            var Q553;
            {var subQ0=sQuery(id+"F25.wireOp",EDGE,"E378.MirrorCS");var subQ1=sQuery(id+"F25.wireOp",EDGE,"E328.MirrorCS");var subQ2=makeQuery(id+"F25.imprint","INTERSECT",VERTEX,{"derivedFrom":[subQ1,subQ0]});Q553=makeQuery(id+"F25.imprint","IMPRINT",FACE,{"disambiguationData":[TD([[makeQuery(id+"F25.imprint","IMPRINT",EDGE,{"disambiguationData":[TD([[subQ2,-1.0]])],"derivedFrom":subQ1}),1.0]])]});}
            var Q554;
            {var subQ0=sQuery(id+"F25.wireOp",EDGE,"E378.MirrorCS");var subQ1=sQuery(id+"F25.wireOp",EDGE,"E328.MirrorCS");var subQ2=makeQuery(id+"F25.imprint","INTERSECT",VERTEX,{"derivedFrom":[subQ1,subQ0]});Q554=makeQuery(id+"F25.imprint","IMPRINT",FACE,{"disambiguationData":[TD([[makeQuery(id+"F25.imprint","IMPRINT",EDGE,{"disambiguationData":[TD([[subQ2,-1.0]])],"derivedFrom":subQ1}),-1.0]])]});}
            var Q555;
            {var subQ0=sQuery(id+"F25.wireOp",EDGE,"E378.MirrorCS");var subQ1=sQuery(id+"F25.wireOp",EDGE,"E358.MirrorCS");var subQ2=makeQuery(id+"F25.imprint","INTERSECT",VERTEX,{"derivedFrom":[subQ1,subQ0]});Q555=makeQuery(id+"F25.imprint","IMPRINT",FACE,{"disambiguationData":[TD([[makeQuery(id+"F25.imprint","IMPRINT",EDGE,{"disambiguationData":[TD([[subQ2,-1.0]])],"derivedFrom":subQ1}),1.0]])]});}
            var Q556;
            {var subQ0=sQuery(id+"F25.wireOp",EDGE,"E348.MirrorCS");var subQ1=sQuery(id+"F25.wireOp",EDGE,"E358.MirrorCS");var subQ2=makeQuery(id+"F25.imprint","INTERSECT",VERTEX,{"derivedFrom":[subQ1,subQ0]});Q556=makeQuery(id+"F25.imprint","IMPRINT",FACE,{"disambiguationData":[TD([[makeQuery(id+"F25.imprint","IMPRINT",EDGE,{"disambiguationData":[TD([[subQ2,-1.0]])],"derivedFrom":subQ1}),1.0]])]});}
            var Q557;
            {var subQ0=sQuery(id+"F25.wireOp",EDGE,"E358.MirrorCS");var subQ1=sQuery(id+"F25.wireOp",EDGE,"E335.MirrorCS");var subQ2=makeQuery(id+"F25.imprint","INTERSECT",VERTEX,{"derivedFrom":[subQ1,subQ0]});Q557=makeQuery(id+"F25.imprint","IMPRINT",FACE,{"disambiguationData":[TD([[makeQuery(id+"F25.imprint","IMPRINT",EDGE,{"disambiguationData":[TD([[subQ2,-1.0]])],"derivedFrom":subQ1}),1.0]])]});}
            var Q558;
            {var subQ0=sQuery(id+"F25.wireOp",EDGE,"E358.MirrorCS");var subQ1=sQuery(id+"F25.wireOp",EDGE,"E335.MirrorCS");var subQ2=makeQuery(id+"F25.imprint","INTERSECT",VERTEX,{"derivedFrom":[subQ1,subQ0]});Q558=makeQuery(id+"F25.imprint","IMPRINT",FACE,{"disambiguationData":[TD([[makeQuery(id+"F25.imprint","IMPRINT",EDGE,{"disambiguationData":[TD([[subQ2,-1.0]])],"derivedFrom":subQ1}),-1.0]])]});}
            var Q559;
            {var subQ0=sQuery(id+"F25.wireOp",EDGE,"E393.MirrorCS");var subQ1=sQuery(id+"F25.wireOp",EDGE,"E335.MirrorCS");var subQ2=makeQuery(id+"F25.imprint","INTERSECT",VERTEX,{"derivedFrom":[subQ1,subQ0]});Q559=makeQuery(id+"F25.imprint","IMPRINT",FACE,{"disambiguationData":[TD([[makeQuery(id+"F25.imprint","IMPRINT",EDGE,{"disambiguationData":[TD([[subQ2,-1.0]])],"derivedFrom":subQ1}),-1.0]])]});}
            var Q560;
            {var subQ0=sQuery(id+"F25.wireOp",EDGE,"E335.MirrorCS");var subQ1=sQuery(id+"F25.wireOp",EDGE,"E326.MirrorCS");var subQ2=makeQuery(id+"F25.imprint","INTERSECT",VERTEX,{"derivedFrom":[subQ1,subQ0]});Q560=makeQuery(id+"F25.imprint","IMPRINT",FACE,{"disambiguationData":[TD([[makeQuery(id+"F25.imprint","IMPRINT",EDGE,{"disambiguationData":[TD([[subQ2,-1.0]])],"derivedFrom":subQ1}),1.0]])]});}
            var Q561;
            {var subQ0=sQuery(id+"F25.wireOp",EDGE,"E394.MirrorCS");var subQ1=sQuery(id+"F25.wireOp",EDGE,"E335.MirrorCS");var subQ2=makeQuery(id+"F25.imprint","INTERSECT",VERTEX,{"derivedFrom":[subQ1,subQ0]});Q561=makeQuery(id+"F25.imprint","IMPRINT",FACE,{"disambiguationData":[TD([[makeQuery(id+"F25.imprint","IMPRINT",EDGE,{"disambiguationData":[TD([[subQ2,-1.0]])],"derivedFrom":subQ1}),-1.0]])]});}
            var Q562;
            {var subQ0=sQuery(id+"F25.wireOp",EDGE,"E360.MirrorCS");var subQ1=sQuery(id+"F25.wireOp",EDGE,"E335.MirrorCS");var subQ2=makeQuery(id+"F25.imprint","INTERSECT",VERTEX,{"derivedFrom":[subQ1,subQ0]});Q562=makeQuery(id+"F25.imprint","IMPRINT",FACE,{"disambiguationData":[TD([[makeQuery(id+"F25.imprint","IMPRINT",EDGE,{"disambiguationData":[TD([[subQ2,-1.0]])],"derivedFrom":subQ1}),-1.0]])]});}
            var Q563;
            {var subQ0=sQuery(id+"F25.wireOp",EDGE,"E336.MirrorCS");var subQ1=sQuery(id+"F25.wireOp",EDGE,"E335.MirrorCS");var subQ2=makeQuery(id+"F25.imprint","INTERSECT",VERTEX,{"derivedFrom":[subQ1,subQ0]});Q563=makeQuery(id+"F25.imprint","IMPRINT",FACE,{"disambiguationData":[TD([[makeQuery(id+"F25.imprint","IMPRINT",EDGE,{"disambiguationData":[TD([[subQ2,-1.0]])],"derivedFrom":subQ1}),-1.0]])]});}
            var Q564;
            {var subQ0=sQuery(id+"F25.wireOp",EDGE,"E383.MirrorCS");var subQ1=sQuery(id+"F25.wireOp",EDGE,"E335.MirrorCS");var subQ2=makeQuery(id+"F25.imprint","INTERSECT",VERTEX,{"derivedFrom":[subQ1,subQ0]});Q564=makeQuery(id+"F25.imprint","IMPRINT",FACE,{"disambiguationData":[TD([[makeQuery(id+"F25.imprint","IMPRINT",EDGE,{"disambiguationData":[TD([[subQ2,-1.0]])],"derivedFrom":subQ1}),-1.0]])]});}
            var Q565;
            {var subQ0=sQuery(id+"F25.wireOp",EDGE,"E350.MirrorCS");var subQ1=sQuery(id+"F25.wireOp",EDGE,"E335.MirrorCS");var subQ2=makeQuery(id+"F25.imprint","INTERSECT",VERTEX,{"derivedFrom":[subQ1,subQ0]});Q565=makeQuery(id+"F25.imprint","IMPRINT",FACE,{"disambiguationData":[TD([[makeQuery(id+"F25.imprint","IMPRINT",EDGE,{"disambiguationData":[TD([[subQ2,-1.0]])],"derivedFrom":subQ1}),-1.0]])]});}
            var Q566;
            {var subQ0=sQuery(id+"F25.wireOp",EDGE,"E383.MirrorCS");var subQ1=sQuery(id+"F25.wireOp",EDGE,"E335.MirrorCS");var subQ2=makeQuery(id+"F25.imprint","INTERSECT",VERTEX,{"derivedFrom":[subQ1,subQ0]});Q566=makeQuery(id+"F25.imprint","IMPRINT",FACE,{"disambiguationData":[TD([[makeQuery(id+"F25.imprint","IMPRINT",EDGE,{"disambiguationData":[TD([[subQ2,-1.0]])],"derivedFrom":subQ1}),1.0]])]});}
            var Q567;
            {var subQ0=sQuery(id+"F25.wireOp",EDGE,"E350.MirrorCS");var subQ1=sQuery(id+"F25.wireOp",EDGE,"E335.MirrorCS");var subQ2=makeQuery(id+"F25.imprint","INTERSECT",VERTEX,{"derivedFrom":[subQ1,subQ0]});Q567=makeQuery(id+"F25.imprint","IMPRINT",FACE,{"disambiguationData":[TD([[makeQuery(id+"F25.imprint","IMPRINT",EDGE,{"disambiguationData":[TD([[subQ2,-1.0]])],"derivedFrom":subQ1}),1.0]])]});}
            var Q568;
            {var subQ0=sQuery(id+"F25.wireOp",EDGE,"E350.MirrorCS");var subQ1=sQuery(id+"F25.wireOp",EDGE,"E344.MirrorCS");var subQ2=makeQuery(id+"F25.imprint","INTERSECT",VERTEX,{"derivedFrom":[subQ1,subQ0]});Q568=makeQuery(id+"F25.imprint","IMPRINT",FACE,{"disambiguationData":[TD([[makeQuery(id+"F25.imprint","IMPRINT",EDGE,{"disambiguationData":[TD([[subQ2,-1.0]])],"derivedFrom":subQ1}),1.0]])]});}
            var Q569;
            {var subQ0=sQuery(id+"F25.wireOp",EDGE,"E383.MirrorCS");var subQ1=sQuery(id+"F25.wireOp",EDGE,"E344.MirrorCS");var subQ2=makeQuery(id+"F25.imprint","INTERSECT",VERTEX,{"derivedFrom":[subQ1,subQ0]});Q569=makeQuery(id+"F25.imprint","IMPRINT",FACE,{"disambiguationData":[TD([[makeQuery(id+"F25.imprint","IMPRINT",EDGE,{"disambiguationData":[TD([[subQ2,-1.0]])],"derivedFrom":subQ1}),1.0]])]});}
            var Q570;
            {var subQ0=sQuery(id+"F25.wireOp",EDGE,"E350.MirrorCS");var subQ1=sQuery(id+"F25.wireOp",EDGE,"E344.MirrorCS");var subQ2=makeQuery(id+"F25.imprint","INTERSECT",VERTEX,{"derivedFrom":[subQ1,subQ0]});Q570=makeQuery(id+"F25.imprint","IMPRINT",FACE,{"disambiguationData":[TD([[makeQuery(id+"F25.imprint","IMPRINT",EDGE,{"disambiguationData":[TD([[subQ2,-1.0]])],"derivedFrom":subQ1}),-1.0]])]});}
            var Q571;
            {var subQ0=sQuery(id+"F25.wireOp",EDGE,"E383.MirrorCS");var subQ1=sQuery(id+"F25.wireOp",EDGE,"E344.MirrorCS");var subQ2=makeQuery(id+"F25.imprint","INTERSECT",VERTEX,{"derivedFrom":[subQ1,subQ0]});Q571=makeQuery(id+"F25.imprint","IMPRINT",FACE,{"disambiguationData":[TD([[makeQuery(id+"F25.imprint","IMPRINT",EDGE,{"disambiguationData":[TD([[subQ2,-1.0]])],"derivedFrom":subQ1}),-1.0]])]});}
            var Q572;
            {var subQ0=sQuery(id+"F25.wireOp",EDGE,"E373.MirrorCS");var subQ1=sQuery(id+"F25.wireOp",EDGE,"E350.MirrorCS");var subQ2=makeQuery(id+"F25.imprint","INTERSECT",VERTEX,{"derivedFrom":[subQ1,subQ0]});Q572=makeQuery(id+"F25.imprint","IMPRINT",FACE,{"disambiguationData":[TD([[makeQuery(id+"F25.imprint","IMPRINT",EDGE,{"disambiguationData":[TD([[subQ2,-1.0]])],"derivedFrom":subQ1}),1.0]])]});}
            var Q573;
            {var subQ0=sQuery(id+"F25.wireOp",EDGE,"E373.MirrorCS");var subQ1=sQuery(id+"F25.wireOp",EDGE,"E350.MirrorCS");var subQ2=makeQuery(id+"F25.imprint","INTERSECT",VERTEX,{"derivedFrom":[subQ1,subQ0]});Q573=makeQuery(id+"F25.imprint","IMPRINT",FACE,{"disambiguationData":[TD([[makeQuery(id+"F25.imprint","IMPRINT",EDGE,{"disambiguationData":[TD([[subQ2,-1.0]])],"derivedFrom":subQ1}),-1.0]])]});}
            var Q574;
            {var subQ0=sQuery(id+"F25.wireOp",EDGE,"E360.MirrorCS");var subQ1=sQuery(id+"F25.wireOp",EDGE,"E335.MirrorCS");var subQ2=makeQuery(id+"F25.imprint","INTERSECT",VERTEX,{"derivedFrom":[subQ1,subQ0]});Q574=makeQuery(id+"F25.imprint","IMPRINT",FACE,{"disambiguationData":[TD([[makeQuery(id+"F25.imprint","IMPRINT",EDGE,{"disambiguationData":[TD([[subQ2,-1.0]])],"derivedFrom":subQ1}),1.0]])]});}
            var Q575;
            {var subQ0=sQuery(id+"F25.wireOp",EDGE,"E394.MirrorCS");var subQ1=sQuery(id+"F25.wireOp",EDGE,"E335.MirrorCS");var subQ2=makeQuery(id+"F25.imprint","INTERSECT",VERTEX,{"derivedFrom":[subQ1,subQ0]});Q575=makeQuery(id+"F25.imprint","IMPRINT",FACE,{"disambiguationData":[TD([[makeQuery(id+"F25.imprint","IMPRINT",EDGE,{"disambiguationData":[TD([[subQ2,-1.0]])],"derivedFrom":subQ1}),1.0]])]});}
            var Q576;
            {var subQ0=sQuery(id+"F25.wireOp",EDGE,"E350.MirrorCS");var subQ1=sQuery(id+"F25.wireOp",EDGE,"E348.MirrorCS");var subQ2=makeQuery(id+"F25.imprint","INTERSECT",VERTEX,{"derivedFrom":[subQ1,subQ0]});Q576=makeQuery(id+"F25.imprint","IMPRINT",FACE,{"disambiguationData":[TD([[makeQuery(id+"F25.imprint","IMPRINT",EDGE,{"disambiguationData":[TD([[subQ2,-1.0]])],"derivedFrom":subQ1}),-1.0]])]});}
            var Q577;
            {var subQ0=sQuery(id+"F25.wireOp",EDGE,"E383.MirrorCS");var subQ1=sQuery(id+"F25.wireOp",EDGE,"E348.MirrorCS");var subQ2=makeQuery(id+"F25.imprint","INTERSECT",VERTEX,{"derivedFrom":[subQ1,subQ0]});Q577=makeQuery(id+"F25.imprint","IMPRINT",FACE,{"disambiguationData":[TD([[makeQuery(id+"F25.imprint","IMPRINT",EDGE,{"disambiguationData":[TD([[subQ2,-1.0]])],"derivedFrom":subQ1}),-1.0]])]});}
            var Q578;
            {var subQ0=sQuery(id+"F25.wireOp",EDGE,"E383.MirrorCS");var subQ1=sQuery(id+"F25.wireOp",EDGE,"E348.MirrorCS");var subQ2=makeQuery(id+"F25.imprint","INTERSECT",VERTEX,{"derivedFrom":[subQ1,subQ0]});Q578=makeQuery(id+"F25.imprint","IMPRINT",FACE,{"disambiguationData":[TD([[makeQuery(id+"F25.imprint","IMPRINT",EDGE,{"disambiguationData":[TD([[subQ2,-1.0]])],"derivedFrom":subQ1}),1.0]])]});}
            var Q579;
            {var subQ0=sQuery(id+"F25.wireOp",EDGE,"E350.MirrorCS");var subQ1=sQuery(id+"F25.wireOp",EDGE,"E348.MirrorCS");var subQ2=makeQuery(id+"F25.imprint","INTERSECT",VERTEX,{"derivedFrom":[subQ1,subQ0]});Q579=makeQuery(id+"F25.imprint","IMPRINT",FACE,{"disambiguationData":[TD([[makeQuery(id+"F25.imprint","IMPRINT",EDGE,{"disambiguationData":[TD([[subQ2,-1.0]])],"derivedFrom":subQ1}),1.0]])]});}
            var Q580;
            {var subQ0=sQuery(id+"F25.wireOp",EDGE,"E310.MirrorCS");Q580=makeQuery(id+"F25.imprint","IMPRINT",FACE,{"disambiguationData":[TD([[makeQuery(id+"F25.imprint","IMPRINT",EDGE,{"derivedFrom":subQ0}),-1.0]])]});}
            var Q581;
            {var subQ0=sQuery(id+"F25.wireOp",EDGE,"E384.MirrorCS");var subQ1=sQuery(id+"F25.wireOp",EDGE,"E351.MirrorCS");var subQ2=makeQuery(id+"F25.imprint","INTERSECT",VERTEX,{"derivedFrom":[subQ1,subQ0]});Q581=makeQuery(id+"F25.imprint","IMPRINT",FACE,{"disambiguationData":[TD([[makeQuery(id+"F25.imprint","IMPRINT",EDGE,{"disambiguationData":[TD([[subQ2,-1.0]])],"derivedFrom":subQ1}),1.0]])]});}
            var Q582;
            {var subQ0=sQuery(id+"F25.wireOp",EDGE,"E384.MirrorCS");var subQ1=sQuery(id+"F25.wireOp",EDGE,"E326.MirrorCS");var subQ2=makeQuery(id+"F25.imprint","INTERSECT",VERTEX,{"derivedFrom":[subQ1,subQ0]});Q582=makeQuery(id+"F25.imprint","IMPRINT",FACE,{"disambiguationData":[TD([[makeQuery(id+"F25.imprint","IMPRINT",EDGE,{"disambiguationData":[TD([[subQ2,-1.0]])],"derivedFrom":subQ1}),-1.0]])]});}
            var Q583;
            {var subQ0=sQuery(id+"F25.wireOp",EDGE,"E344.MirrorCS");var subQ1=sQuery(id+"F25.wireOp",EDGE,"E326.MirrorCS");var subQ2=makeQuery(id+"F25.imprint","INTERSECT",VERTEX,{"derivedFrom":[subQ1,subQ0]});Q583=makeQuery(id+"F25.imprint","IMPRINT",FACE,{"disambiguationData":[TD([[makeQuery(id+"F25.imprint","IMPRINT",EDGE,{"disambiguationData":[TD([[subQ2,-1.0]])],"derivedFrom":subQ1}),-1.0]])]});}
            var Q584;
            {var subQ0=sQuery(id+"F25.wireOp",EDGE,"E373.MirrorCS");var subQ1=sQuery(id+"F25.wireOp",EDGE,"E326.MirrorCS");var subQ2=makeQuery(id+"F25.imprint","INTERSECT",VERTEX,{"derivedFrom":[subQ1,subQ0]});Q584=makeQuery(id+"F25.imprint","IMPRINT",FACE,{"disambiguationData":[TD([[makeQuery(id+"F25.imprint","IMPRINT",EDGE,{"disambiguationData":[TD([[subQ2,-1.0]])],"derivedFrom":subQ1}),-1.0]])]});}
            var Q585;
            {var subQ0=sQuery(id+"F25.wireOp",EDGE,"E378.MirrorCS");var subQ1=sQuery(id+"F25.wireOp",EDGE,"E326.MirrorCS");var subQ2=makeQuery(id+"F25.imprint","INTERSECT",VERTEX,{"derivedFrom":[subQ1,subQ0]});Q585=makeQuery(id+"F25.imprint","IMPRINT",FACE,{"disambiguationData":[TD([[makeQuery(id+"F25.imprint","IMPRINT",EDGE,{"disambiguationData":[TD([[subQ2,-1.0]])],"derivedFrom":subQ1}),-1.0]])]});}
            var Q586;
            {var subQ0=sQuery(id+"F25.wireOp",EDGE,"E348.MirrorCS");var subQ1=sQuery(id+"F25.wireOp",EDGE,"E326.MirrorCS");var subQ2=makeQuery(id+"F25.imprint","INTERSECT",VERTEX,{"derivedFrom":[subQ1,subQ0]});Q586=makeQuery(id+"F25.imprint","IMPRINT",FACE,{"disambiguationData":[TD([[makeQuery(id+"F25.imprint","IMPRINT",EDGE,{"disambiguationData":[TD([[subQ2,-1.0]])],"derivedFrom":subQ1}),-1.0]])]});}
            var Q587;
            {var subQ0=sQuery(id+"F25.wireOp",EDGE,"E369.MirrorCS");var subQ1=sQuery(id+"F25.wireOp",EDGE,"E326.MirrorCS");var subQ2=makeQuery(id+"F25.imprint","INTERSECT",VERTEX,{"derivedFrom":[subQ1,subQ0]});Q587=makeQuery(id+"F25.imprint","IMPRINT",FACE,{"disambiguationData":[TD([[makeQuery(id+"F25.imprint","IMPRINT",EDGE,{"disambiguationData":[TD([[subQ2,-1.0]])],"derivedFrom":subQ1}),-1.0]])]});}
            var Q588;
            {var subQ0=sQuery(id+"F25.wireOp",EDGE,"E335.MirrorCS");var subQ1=sQuery(id+"F25.wireOp",EDGE,"E326.MirrorCS");var subQ2=makeQuery(id+"F25.imprint","INTERSECT",VERTEX,{"derivedFrom":[subQ1,subQ0]});Q588=makeQuery(id+"F25.imprint","IMPRINT",FACE,{"disambiguationData":[TD([[makeQuery(id+"F25.imprint","IMPRINT",EDGE,{"disambiguationData":[TD([[subQ2,-1.0]])],"derivedFrom":subQ1}),-1.0]])]});}
            var Q589;
            {var subQ0=sQuery(id+"F25.wireOp",EDGE,"E394.MirrorCS");var subQ1=sQuery(id+"F25.wireOp",EDGE,"E348.MirrorCS");var subQ2=makeQuery(id+"F25.imprint","INTERSECT",VERTEX,{"derivedFrom":[subQ1,subQ0]});Q589=makeQuery(id+"F25.imprint","IMPRINT",FACE,{"disambiguationData":[TD([[makeQuery(id+"F25.imprint","IMPRINT",EDGE,{"disambiguationData":[TD([[subQ2,-1.0]])],"derivedFrom":subQ1}),-1.0]])]});}
            var Q590;
            {var subQ0=sQuery(id+"F25.wireOp",EDGE,"E348.MirrorCS");var subQ1=sQuery(id+"F25.wireOp",EDGE,"E336.MirrorCS");var subQ2=makeQuery(id+"F25.imprint","INTERSECT",VERTEX,{"derivedFrom":[subQ1,subQ0]});Q590=makeQuery(id+"F25.imprint","IMPRINT",FACE,{"disambiguationData":[TD([[makeQuery(id+"F25.imprint","IMPRINT",EDGE,{"disambiguationData":[TD([[subQ2,-1.0]])],"derivedFrom":subQ1}),-1.0]])]});}
            var Q591;
            {var subQ0=sQuery(id+"F25.wireOp",EDGE,"E378.MirrorCS");var subQ1=sQuery(id+"F25.wireOp",EDGE,"E336.MirrorCS");var subQ2=makeQuery(id+"F25.imprint","INTERSECT",VERTEX,{"derivedFrom":[subQ1,subQ0]});Q591=makeQuery(id+"F25.imprint","IMPRINT",FACE,{"disambiguationData":[TD([[makeQuery(id+"F25.imprint","IMPRINT",EDGE,{"disambiguationData":[TD([[subQ2,-1.0]])],"derivedFrom":subQ1}),-1.0]])]});}
            var Q592;
            {var subQ0=sQuery(id+"F25.wireOp",EDGE,"E394.MirrorCS");var subQ1=sQuery(id+"F25.wireOp",EDGE,"E348.MirrorCS");var subQ2=makeQuery(id+"F25.imprint","INTERSECT",VERTEX,{"derivedFrom":[subQ1,subQ0]});Q592=makeQuery(id+"F25.imprint","IMPRINT",FACE,{"disambiguationData":[TD([[makeQuery(id+"F25.imprint","IMPRINT",EDGE,{"disambiguationData":[TD([[subQ2,-1.0]])],"derivedFrom":subQ1}),1.0]])]});}
            var Q593;
            {var subQ0=sQuery(id+"F25.wireOp",EDGE,"E394.MirrorCS");var subQ1=sQuery(id+"F25.wireOp",EDGE,"E373.MirrorCS");var subQ2=makeQuery(id+"F25.imprint","INTERSECT",VERTEX,{"derivedFrom":[subQ1,subQ0]});Q593=makeQuery(id+"F25.imprint","IMPRINT",FACE,{"disambiguationData":[TD([[makeQuery(id+"F25.imprint","IMPRINT",EDGE,{"disambiguationData":[TD([[subQ2,-1.0]])],"derivedFrom":subQ1}),-1.0]])]});}
            var Q594;
            {var subQ0=sQuery(id+"F25.wireOp",EDGE,"E373.MirrorCS");var subQ1=sQuery(id+"F25.wireOp",EDGE,"E336.MirrorCS");var subQ2=makeQuery(id+"F25.imprint","INTERSECT",VERTEX,{"derivedFrom":[subQ1,subQ0]});Q594=makeQuery(id+"F25.imprint","IMPRINT",FACE,{"disambiguationData":[TD([[makeQuery(id+"F25.imprint","IMPRINT",EDGE,{"disambiguationData":[TD([[subQ2,-1.0]])],"derivedFrom":subQ1}),-1.0]])]});}
            var Q595;
            {var subQ0=sQuery(id+"F25.wireOp",EDGE,"E344.MirrorCS");var subQ1=sQuery(id+"F25.wireOp",EDGE,"E336.MirrorCS");var subQ2=makeQuery(id+"F25.imprint","INTERSECT",VERTEX,{"derivedFrom":[subQ1,subQ0]});Q595=makeQuery(id+"F25.imprint","IMPRINT",FACE,{"disambiguationData":[TD([[makeQuery(id+"F25.imprint","IMPRINT",EDGE,{"disambiguationData":[TD([[subQ2,-1.0]])],"derivedFrom":subQ1}),-1.0]])]});}
            var Q596;
            {var subQ0=sQuery(id+"F25.wireOp",EDGE,"E394.MirrorCS");var subQ1=sQuery(id+"F25.wireOp",EDGE,"E344.MirrorCS");var subQ2=makeQuery(id+"F25.imprint","INTERSECT",VERTEX,{"derivedFrom":[subQ1,subQ0]});Q596=makeQuery(id+"F25.imprint","IMPRINT",FACE,{"disambiguationData":[TD([[makeQuery(id+"F25.imprint","IMPRINT",EDGE,{"disambiguationData":[TD([[subQ2,-1.0]])],"derivedFrom":subQ1}),-1.0]])]});}
            var Q597;
            {var subQ0=sQuery(id+"F25.wireOp",EDGE,"E394.MirrorCS");var subQ1=sQuery(id+"F25.wireOp",EDGE,"E344.MirrorCS");var subQ2=makeQuery(id+"F25.imprint","INTERSECT",VERTEX,{"derivedFrom":[subQ1,subQ0]});Q597=makeQuery(id+"F25.imprint","IMPRINT",FACE,{"disambiguationData":[TD([[makeQuery(id+"F25.imprint","IMPRINT",EDGE,{"disambiguationData":[TD([[subQ2,-1.0]])],"derivedFrom":subQ1}),1.0]])]});}
            var Q598;
            {var subQ0=sQuery(id+"F25.wireOp",EDGE,"E384.MirrorCS");var subQ1=sQuery(id+"F25.wireOp",EDGE,"E336.MirrorCS");var subQ2=makeQuery(id+"F25.imprint","INTERSECT",VERTEX,{"derivedFrom":[subQ1,subQ0]});Q598=makeQuery(id+"F25.imprint","IMPRINT",FACE,{"disambiguationData":[TD([[makeQuery(id+"F25.imprint","IMPRINT",EDGE,{"disambiguationData":[TD([[subQ2,-1.0]])],"derivedFrom":subQ1}),-1.0]])]});}
            var Q599;
            {var subQ0=sQuery(id+"F25.wireOp",EDGE,"E515.trimOffspring");var subQ1=sQuery(id+"F25.wireOp",EDGE,"E264.trimOffspring");var subQ2=makeQuery(id+"F25.imprint","INTERSECT",VERTEX,{"derivedFrom":[subQ1,subQ0]});Q599=makeQuery(id+"F25.imprint","IMPRINT",FACE,{"disambiguationData":[TD([[makeQuery(id+"F25.imprint","IMPRINT",EDGE,{"disambiguationData":[TD([[subQ2,-1.0]])],"derivedFrom":subQ1}),1.0]])]});}
            var Q600;
            {var subQ0=sQuery(id+"F25.wireOp",EDGE,"E578.trimOffspring");var subQ1=sQuery(id+"F25.wireOp",EDGE,"E414.MirrorCS");var subQ2=makeQuery(id+"F25.imprint","INTERSECT",VERTEX,{"derivedFrom":[subQ1,subQ0]});Q600=makeQuery(id+"F25.imprint","IMPRINT",FACE,{"disambiguationData":[TD([[makeQuery(id+"F25.imprint","IMPRINT",EDGE,{"disambiguationData":[TD([[subQ2,-1.0]])],"derivedFrom":subQ1}),1.0]])]});}
            var Q601;
            {var subQ4=sQuery(id+"F25.wireOp",EDGE,"E248.top");Q601=makeQuery(id+"F25.imprint","IMPRINT",FACE,{"disambiguationData":[TD([[makeQuery(id+"F25.imprint","IMPRINT",EDGE,{"derivedFrom":subQ4}),1.0]])]});}
            var Q602;
            {var subQ0=sQuery(id+"F25.wireOp",EDGE,"E519.trimOffspring");var subQ1=sQuery(id+"F25.wireOp",EDGE,"E279.trimOffspring");var subQ2=makeQuery(id+"F25.imprint","INTERSECT",VERTEX,{"derivedFrom":[subQ1,subQ0]});Q602=makeQuery(id+"F25.imprint","IMPRINT",FACE,{"disambiguationData":[TD([[makeQuery(id+"F25.imprint","IMPRINT",EDGE,{"disambiguationData":[TD([[subQ2,-1.0]])],"derivedFrom":subQ1}),-1.0]])]});}
            var Q603;
            {var subQ0=sQuery(id+"F25.wireOp",EDGE,"E519.trimOffspring");var subQ1=sQuery(id+"F25.wireOp",EDGE,"E280.trimOffspring");var subQ2=makeQuery(id+"F25.imprint","INTERSECT",VERTEX,{"derivedFrom":[subQ1,subQ0]});Q603=makeQuery(id+"F25.imprint","IMPRINT",FACE,{"disambiguationData":[TD([[makeQuery(id+"F25.imprint","IMPRINT",EDGE,{"disambiguationData":[TD([[subQ2,-1.0]])],"derivedFrom":subQ1}),1.0]])]});}
            extrude(context, id + "F33", {"entities" : qUnion([Q0, Q1, Q2, Q3, Q4, Q5, Q6, Q7, Q8, Q9, Q10, Q11, Q12, Q13, Q14, Q15, Q16, Q17, Q18, Q19, Q20, Q21, Q22, Q23, Q24, Q25, Q26, Q27, Q28, Q29, Q30, Q31, Q32, Q33, Q34, Q35, Q36, Q37, Q38, Q39, Q40, Q41, Q42, Q43, Q44, Q45, Q46, Q47, Q48, Q49, Q50, Q51, Q52, Q53, Q54, Q55, Q56, Q57, Q58, Q59, Q60, Q61, Q62, Q63, Q64, Q65, Q66, Q67, Q68, Q69, Q70, Q71, Q72, Q73, Q74, Q75, Q76, Q77, Q78, Q79, Q80, Q81, Q82, Q83, Q84, Q85, Q86, Q87, Q88, Q89, Q90, Q91, Q92, Q93, Q94, Q95, Q96, Q97, Q98, Q99, Q100, Q101, Q102, Q103, Q104, Q105, Q106, Q107, Q108, Q109, Q110, Q111, Q112, Q113, Q114, Q115, Q116, Q117, Q118, Q119, Q120, Q121, Q122, Q123, Q124, Q125, Q126, Q127, Q128, Q129, Q130, Q131, Q132, Q133, Q134, Q135, Q136, Q137, Q138, Q139, Q140, Q141, Q142, Q143, Q144, Q145, Q146, Q147, Q148, Q149, Q150, Q151, Q152, Q153, Q154, Q155, Q156, Q157, Q158, Q159, Q160, Q161, Q162, Q163, Q164, Q165, Q166, Q167, Q168, Q169, Q170, Q171, Q172, Q173, Q174, Q175, Q176, Q177, Q178, Q179, Q180, Q181, Q182, Q183, Q184, Q185, Q186, Q187, Q188, Q189, Q190, Q191, Q192, Q193, Q194, Q195, Q196, Q197, Q198, Q199, Q200, Q201, Q202, Q203, Q204, Q205, Q206, Q207, Q208, Q209, Q210, Q211, Q212, Q213, Q214, Q215, Q216, Q217, Q218, Q219, Q220, Q221, Q222, Q223, Q224, Q225, Q226, Q227, Q228, Q229, Q230, Q231, Q232, Q233, Q234, Q235, Q236, Q237, Q238, Q239, Q240, Q241, Q242, Q243, Q244, Q245, Q246, Q247, Q248, Q249, Q250, Q251, Q252, Q253, Q254, Q255, Q256, Q257, Q258, Q259, Q260, Q261, Q262, Q263, Q264, Q265, Q266, Q267, Q268, Q269, Q270, Q271, Q272, Q273, Q274, Q275, Q276, Q277, Q278, Q279, Q280, Q281, Q282, Q283, Q284, Q285, Q286, Q287, Q288, Q289, Q290, Q291, Q292, Q293, Q294, Q295, Q296, Q297, Q298, Q299, Q300, Q301, Q302, Q303, Q304, Q305, Q306, Q307, Q308, Q309, Q310, Q311, Q312, Q313, Q314, Q315, Q316, Q317, Q318, Q319, Q320, Q321, Q322, Q323, Q324, Q325, Q326, Q327, Q328, Q329, Q330, Q331, Q332, Q333, Q334, Q335, Q336, Q337, Q338, Q339, Q340, Q341, Q342, Q343, Q344, Q345, Q346, Q347, Q348, Q349, Q350, Q351, Q352, Q353, Q354, Q355, Q356, Q357, Q358, Q359, Q360, Q361, Q362, Q363, Q364, Q365, Q366, Q367, Q368, Q369, Q370, Q371, Q372, Q373, Q374, Q375, Q376, Q377, Q378, Q379, Q380, Q381, Q382, Q383, Q384, Q385, Q386, Q387, Q388, Q389, Q390, Q391, Q392, Q393, Q394, Q395, Q396, Q397, Q398, Q399, Q400, Q401, Q402, Q403, Q404, Q405, Q406, Q407, Q408, Q409, Q410, Q411, Q412, Q413, Q414, Q415, Q416, Q417, Q418, Q419, Q420, Q421, Q422, Q423, Q424, Q425, Q426, Q427, Q428, Q429, Q430, Q431, Q432, Q433, Q434, Q435, Q436, Q437, Q438, Q439, Q440, Q441, Q442, Q443, Q444, Q445, Q446, Q447, Q448, Q449, Q450, Q451, Q452, Q453, Q454, Q455, Q456, Q457, Q458, Q459, Q460, Q461, Q462, Q463, Q464, Q465, Q466, Q467, Q468, Q469, Q470, Q471, Q472, Q473, Q474, Q475, Q476, Q477, Q478, Q479, Q480, Q481, Q482, Q483, Q484, Q485, Q486, Q487, Q488, Q489, Q490, Q491, Q492, Q493, Q494, Q495, Q496, Q497, Q498, Q499, Q500, Q501, Q502, Q503, Q504, Q505, Q506, Q507, Q508, Q509, Q510, Q511, Q512, Q513, Q514, Q515, Q516, Q517, Q518, Q519, Q520, Q521, Q522, Q523, Q524, Q525, Q526, Q527, Q528, Q529, Q530, Q531, Q532, Q533, Q534, Q535, Q536, Q537, Q538, Q539, Q540, Q541, Q542, Q543, Q544, Q545, Q546, Q547, Q548, Q549, Q550, Q551, Q552, Q553, Q554, Q555, Q556, Q557, Q558, Q559, Q560, Q561, Q562, Q563, Q564, Q565, Q566, Q567, Q568, Q569, Q570, Q571, Q572, Q573, Q574, Q575, Q576, Q577, Q578, Q579, Q580, Q581, Q582, Q583, Q584, Q585, Q586, Q587, Q588, Q589, Q590, Q591, Q592, Q593, Q594, Q595, Q596, Q597, Q598, Q599, Q600, Q601, Q602, Q603]), "operationType" : NewBodyOperationType.REMOVE, "depth" : 25 * mm, "offsetDistance" : 25 * mm});
        }
        {
            var Q0;
            {var subQ0=sQuery(id+"F25.wireOp",EDGE,"E255.trimOffspring");var subQ1=sQuery(id+"F25.wireOp",EDGE,"E234.top");var subQ2=makeQuery(id+"F25.imprint","INTERSECT",VERTEX,{"derivedFrom":[subQ1,subQ0]});Q0=makeQuery(id+"F25.imprint","IMPRINT",FACE,{"disambiguationData":[TD([[makeQuery(id+"F25.imprint","IMPRINT",EDGE,{"disambiguationData":[TD([[subQ2,-1.0]])],"derivedFrom":subQ1}),-1.0]])]});}
            var Q1;
            {var subQ0=sQuery(id+"F25.wireOp",EDGE,"E255.trimOffspring");var subQ1=sQuery(id+"F25.wireOp",EDGE,"E253.bottom");var subQ2=makeQuery(id+"F25.imprint","INTERSECT",VERTEX,{"derivedFrom":[subQ1,subQ0]});Q1=makeQuery(id+"F25.imprint","IMPRINT",FACE,{"disambiguationData":[TD([[makeQuery(id+"F25.imprint","IMPRINT",EDGE,{"disambiguationData":[TD([[subQ2,-1.0]])],"derivedFrom":subQ1}),1.0]])]});}
            var Q2;
            {var subQ0=sQuery(id+"F25.wireOp",EDGE,"E255.trimOffspring");var subQ1=sQuery(id+"F25.wireOp",EDGE,"E252.top");var subQ2=makeQuery(id+"F25.imprint","INTERSECT",VERTEX,{"derivedFrom":[subQ1,subQ0]});Q2=makeQuery(id+"F25.imprint","IMPRINT",FACE,{"disambiguationData":[TD([[makeQuery(id+"F25.imprint","IMPRINT",EDGE,{"disambiguationData":[TD([[subQ2,-1.0]])],"derivedFrom":subQ1}),1.0]])]});}
            var Q3;
            {var subQ0=sQuery(id+"F25.wireOp",EDGE,"E255.trimOffspring");var subQ1=sQuery(id+"F25.wireOp",EDGE,"E235.top");var subQ2=makeQuery(id+"F25.imprint","INTERSECT",VERTEX,{"derivedFrom":[subQ1,subQ0]});Q3=makeQuery(id+"F25.imprint","IMPRINT",FACE,{"disambiguationData":[TD([[makeQuery(id+"F25.imprint","IMPRINT",EDGE,{"disambiguationData":[TD([[subQ2,-1.0]])],"derivedFrom":subQ1}),1.0]])]});}
            var Q4;
            {var subQ0=sQuery(id+"F25.wireOp",EDGE,"E255.trimOffspring");var subQ1=sQuery(id+"F25.wireOp",EDGE,"E235.top");var subQ2=makeQuery(id+"F25.imprint","INTERSECT",VERTEX,{"derivedFrom":[subQ1,subQ0]});Q4=makeQuery(id+"F25.imprint","IMPRINT",FACE,{"disambiguationData":[TD([[makeQuery(id+"F25.imprint","IMPRINT",EDGE,{"disambiguationData":[TD([[subQ2,-1.0]])],"derivedFrom":subQ1}),-1.0]])]});}
            var Q5;
            {var subQ0=sQuery(id+"F25.wireOp",EDGE,"E255.trimOffspring");var subQ1=sQuery(id+"F25.wireOp",EDGE,"E236.bottom");var subQ2=makeQuery(id+"F25.imprint","INTERSECT",VERTEX,{"derivedFrom":[subQ1,subQ0]});Q5=makeQuery(id+"F25.imprint","IMPRINT",FACE,{"disambiguationData":[TD([[makeQuery(id+"F25.imprint","IMPRINT",EDGE,{"disambiguationData":[TD([[subQ2,-1.0]])],"derivedFrom":subQ1}),-1.0]])]});}
            var Q6;
            {var subQ0=sQuery(id+"F25.wireOp",EDGE,"E256.trimOffspring");var subQ1=sQuery(id+"F25.wireOp",EDGE,"E236.bottom");var subQ2=makeQuery(id+"F25.imprint","INTERSECT",VERTEX,{"derivedFrom":[subQ1,subQ0]});Q6=makeQuery(id+"F25.imprint","IMPRINT",FACE,{"disambiguationData":[TD([[makeQuery(id+"F25.imprint","IMPRINT",EDGE,{"disambiguationData":[TD([[subQ2,-1.0]])],"derivedFrom":subQ1}),-1.0]])]});}
            var Q7;
            {var subQ0=sQuery(id+"F25.wireOp",EDGE,"E256.trimOffspring");var subQ1=sQuery(id+"F25.wireOp",EDGE,"E235.top");var subQ2=makeQuery(id+"F25.imprint","INTERSECT",VERTEX,{"derivedFrom":[subQ1,subQ0]});Q7=makeQuery(id+"F25.imprint","IMPRINT",FACE,{"disambiguationData":[TD([[makeQuery(id+"F25.imprint","IMPRINT",EDGE,{"disambiguationData":[TD([[subQ2,-1.0]])],"derivedFrom":subQ1}),-1.0]])]});}
            var Q8;
            {var subQ0=sQuery(id+"F25.wireOp",EDGE,"E256.trimOffspring");var subQ1=sQuery(id+"F25.wireOp",EDGE,"E235.top");var subQ2=makeQuery(id+"F25.imprint","INTERSECT",VERTEX,{"derivedFrom":[subQ1,subQ0]});Q8=makeQuery(id+"F25.imprint","IMPRINT",FACE,{"disambiguationData":[TD([[makeQuery(id+"F25.imprint","IMPRINT",EDGE,{"disambiguationData":[TD([[subQ2,-1.0]])],"derivedFrom":subQ1}),1.0]])]});}
            var Q9;
            {var subQ0=sQuery(id+"F25.wireOp",EDGE,"E254.trimOffspring");var subQ1=sQuery(id+"F25.wireOp",EDGE,"E235.top");var subQ2=makeQuery(id+"F25.imprint","INTERSECT",VERTEX,{"derivedFrom":[subQ1,subQ0]});Q9=makeQuery(id+"F25.imprint","IMPRINT",FACE,{"disambiguationData":[TD([[makeQuery(id+"F25.imprint","IMPRINT",EDGE,{"disambiguationData":[TD([[subQ2,-1.0]])],"derivedFrom":subQ1}),-1.0]])]});}
            var Q10;
            {var subQ0=sQuery(id+"F25.wireOp",EDGE,"E254.trimOffspring");var subQ1=sQuery(id+"F25.wireOp",EDGE,"E236.bottom");var subQ2=makeQuery(id+"F25.imprint","INTERSECT",VERTEX,{"derivedFrom":[subQ1,subQ0]});Q10=makeQuery(id+"F25.imprint","IMPRINT",FACE,{"disambiguationData":[TD([[makeQuery(id+"F25.imprint","IMPRINT",EDGE,{"disambiguationData":[TD([[subQ2,-1.0]])],"derivedFrom":subQ1}),-1.0]])]});}
            var Q11;
            {var subQ0=sQuery(id+"F25.wireOp",EDGE,"E254.trimOffspring");var subQ1=sQuery(id+"F25.wireOp",EDGE,"E252.top");var subQ2=makeQuery(id+"F25.imprint","INTERSECT",VERTEX,{"derivedFrom":[subQ1,subQ0]});Q11=makeQuery(id+"F25.imprint","IMPRINT",FACE,{"disambiguationData":[TD([[makeQuery(id+"F25.imprint","IMPRINT",EDGE,{"disambiguationData":[TD([[subQ2,1.0]])],"derivedFrom":subQ1}),1.0]])]});}
            var Q12;
            {var subQ0=sQuery(id+"F25.wireOp",EDGE,"E254.trimOffspring");var subQ1=sQuery(id+"F25.wireOp",EDGE,"E253.bottom");var subQ2=makeQuery(id+"F25.imprint","INTERSECT",VERTEX,{"derivedFrom":[subQ1,subQ0]});Q12=makeQuery(id+"F25.imprint","IMPRINT",FACE,{"disambiguationData":[TD([[makeQuery(id+"F25.imprint","IMPRINT",EDGE,{"disambiguationData":[TD([[subQ2,1.0]])],"derivedFrom":subQ1}),1.0]])]});}
            var Q13;
            {var subQ0=sQuery(id+"F25.wireOp",EDGE,"E254.trimOffspring");var subQ5=sQuery(id+"F25.wireOp",EDGE,"E253.top");var subQ6=makeQuery(id+"F25.imprint","INTERSECT",VERTEX,{"derivedFrom":[subQ5,subQ0]});Q13=makeQuery(id+"F25.imprint","IMPRINT",FACE,{"disambiguationData":[TD([[makeQuery(id+"F25.imprint","IMPRINT",EDGE,{"disambiguationData":[TD([[subQ6,1.0]])],"derivedFrom":subQ5}),1.0]])]});}
            var Q14;
            {var subQ0=sQuery(id+"F25.wireOp",EDGE,"E254.trimOffspring");var subQ5=sQuery(id+"F25.wireOp",EDGE,"E235.top");var subQ8=makeQuery(id+"F25.imprint","INTERSECT",VERTEX,{"derivedFrom":[subQ5,subQ0]});Q14=makeQuery(id+"F25.imprint","IMPRINT",FACE,{"disambiguationData":[TD([[makeQuery(id+"F25.imprint","IMPRINT",EDGE,{"disambiguationData":[TD([[subQ8,-1.0]])],"derivedFrom":subQ5}),1.0]])]});}
            var Q15;
            {var subQ0=sQuery(id+"F25.wireOp",EDGE,"E257.trimOffspring");var subQ1=sQuery(id+"F25.wireOp",EDGE,"E235.top");var subQ2=makeQuery(id+"F25.imprint","INTERSECT",VERTEX,{"derivedFrom":[subQ1,subQ0]});Q15=makeQuery(id+"F25.imprint","IMPRINT",FACE,{"disambiguationData":[TD([[makeQuery(id+"F25.imprint","IMPRINT",EDGE,{"disambiguationData":[TD([[subQ2,-1.0]])],"derivedFrom":subQ1}),-1.0]])]});}
            var Q16;
            {var subQ0=sQuery(id+"F25.wireOp",EDGE,"E257.trimOffspring");var subQ1=sQuery(id+"F25.wireOp",EDGE,"E236.bottom");var subQ2=makeQuery(id+"F25.imprint","INTERSECT",VERTEX,{"derivedFrom":[subQ1,subQ0]});Q16=makeQuery(id+"F25.imprint","IMPRINT",FACE,{"disambiguationData":[TD([[makeQuery(id+"F25.imprint","IMPRINT",EDGE,{"disambiguationData":[TD([[subQ2,-1.0]])],"derivedFrom":subQ1}),-1.0]])]});}
            var Q17;
            {var subQ0=sQuery(id+"F25.wireOp",EDGE,"E257.trimOffspring");var subQ1=sQuery(id+"F25.wireOp",EDGE,"E235.top");var subQ2=makeQuery(id+"F25.imprint","INTERSECT",VERTEX,{"derivedFrom":[subQ1,subQ0]});Q17=makeQuery(id+"F25.imprint","IMPRINT",FACE,{"disambiguationData":[TD([[makeQuery(id+"F25.imprint","IMPRINT",EDGE,{"disambiguationData":[TD([[subQ2,-1.0]])],"derivedFrom":subQ1}),1.0]])]});}
            var Q18;
            {var subQ0=sQuery(id+"F25.wireOp",EDGE,"E499.trimOffspring");var subQ1=sQuery(id+"F25.wireOp",EDGE,"E257.trimOffspring");var subQ2=makeQuery(id+"F25.imprint","INTERSECT",VERTEX,{"derivedFrom":[subQ1,subQ0]});Q18=makeQuery(id+"F25.imprint","IMPRINT",FACE,{"disambiguationData":[TD([[makeQuery(id+"F25.imprint","IMPRINT",EDGE,{"disambiguationData":[TD([[subQ2,1.0]])],"derivedFrom":subQ1}),-1.0]])]});}
            var Q19;
            {var subQ0=sQuery(id+"F25.wireOp",EDGE,"E499.trimOffspring");var subQ1=sQuery(id+"F25.wireOp",EDGE,"E257.trimOffspring");var subQ2=makeQuery(id+"F25.imprint","INTERSECT",VERTEX,{"derivedFrom":[subQ1,subQ0]});Q19=makeQuery(id+"F25.imprint","IMPRINT",FACE,{"disambiguationData":[TD([[makeQuery(id+"F25.imprint","IMPRINT",EDGE,{"disambiguationData":[TD([[subQ2,-1.0]])],"derivedFrom":subQ1}),-1.0]])]});}
            var Q20;
            {var subQ0=sQuery(id+"F25.wireOp",EDGE,"E275.trimOffspring");var subQ1=sQuery(id+"F25.wireOp",EDGE,"E246.right");var subQ2=makeQuery(id+"F25.imprint","INTERSECT",VERTEX,{"derivedFrom":[subQ1,subQ0]});Q20=makeQuery(id+"F25.imprint","IMPRINT",FACE,{"disambiguationData":[TD([[makeQuery(id+"F25.imprint","IMPRINT",EDGE,{"disambiguationData":[TD([[subQ2,1.0]])],"derivedFrom":subQ1}),-1.0]])]});}
            var Q21;
            {var subQ0=sQuery(id+"F25.wireOp",EDGE,"E275.trimOffspring");var subQ1=sQuery(id+"F25.wireOp",EDGE,"E245.left");var subQ2=makeQuery(id+"F25.imprint","INTERSECT",VERTEX,{"derivedFrom":[subQ1,subQ0]});Q21=makeQuery(id+"F25.imprint","IMPRINT",FACE,{"disambiguationData":[TD([[makeQuery(id+"F25.imprint","IMPRINT",EDGE,{"disambiguationData":[TD([[subQ2,1.0]])],"derivedFrom":subQ1}),-1.0]])]});}
            var Q22;
            {var subQ2=sQuery(id+"F25.wireOp",EDGE,"E244.right");var subQ6=sQuery(id+"F25.wireOp",EDGE,"E275.trimOffspring");var subQ8=makeQuery(id+"F25.imprint","INTERSECT",VERTEX,{"derivedFrom":[subQ2,subQ6]});Q22=makeQuery(id+"F25.imprint","IMPRINT",FACE,{"disambiguationData":[TD([[makeQuery(id+"F25.imprint","IMPRINT",EDGE,{"disambiguationData":[TD([[subQ8,1.0]])],"derivedFrom":subQ2}),-1.0]])]});}
            var Q23;
            {var subQ0=sQuery(id+"F25.wireOp",EDGE,"E275.trimOffspring");var subQ1=sQuery(id+"F25.wireOp",EDGE,"E243.left");var subQ2=makeQuery(id+"F25.imprint","INTERSECT",VERTEX,{"derivedFrom":[subQ1,subQ0]});Q23=makeQuery(id+"F25.imprint","IMPRINT",FACE,{"disambiguationData":[TD([[makeQuery(id+"F25.imprint","IMPRINT",EDGE,{"disambiguationData":[TD([[subQ2,1.0]])],"derivedFrom":subQ1}),-1.0]])]});}
            var Q24;
            {var subQ0=sQuery(id+"F25.wireOp",EDGE,"E271.trimOffspring");var subQ1=sQuery(id+"F25.wireOp",EDGE,"E244.right");var subQ2=makeQuery(id+"F25.imprint","INTERSECT",VERTEX,{"derivedFrom":[subQ1,subQ0]});Q24=makeQuery(id+"F25.imprint","IMPRINT",FACE,{"disambiguationData":[TD([[makeQuery(id+"F25.imprint","IMPRINT",EDGE,{"disambiguationData":[TD([[subQ2,-1.0]])],"derivedFrom":subQ1}),-1.0]])]});}
            var Q25;
            {var subQ0=sQuery(id+"F25.wireOp",EDGE,"E271.trimOffspring");var subQ1=sQuery(id+"F25.wireOp",EDGE,"E246.right");var subQ2=makeQuery(id+"F25.imprint","INTERSECT",VERTEX,{"derivedFrom":[subQ1,subQ0]});Q25=makeQuery(id+"F25.imprint","IMPRINT",FACE,{"disambiguationData":[TD([[makeQuery(id+"F25.imprint","IMPRINT",EDGE,{"disambiguationData":[TD([[subQ2,-1.0]])],"derivedFrom":subQ1}),-1.0]])]});}
            var Q26;
            {var subQ0=sQuery(id+"F25.wireOp",EDGE,"E271.trimOffspring");var subQ1=sQuery(id+"F25.wireOp",EDGE,"E245.right");var subQ2=makeQuery(id+"F25.imprint","INTERSECT",VERTEX,{"derivedFrom":[subQ1,subQ0]});Q26=makeQuery(id+"F25.imprint","IMPRINT",FACE,{"disambiguationData":[TD([[makeQuery(id+"F25.imprint","IMPRINT",EDGE,{"disambiguationData":[TD([[subQ2,-1.0]])],"derivedFrom":subQ1}),-1.0]])]});}
            var Q27;
            {var subQ0=sQuery(id+"F25.wireOp",EDGE,"E271.trimOffspring");var subQ1=sQuery(id+"F25.wireOp",EDGE,"E245.left");var subQ2=makeQuery(id+"F25.imprint","INTERSECT",VERTEX,{"derivedFrom":[subQ1,subQ0]});Q27=makeQuery(id+"F25.imprint","IMPRINT",FACE,{"disambiguationData":[TD([[makeQuery(id+"F25.imprint","IMPRINT",EDGE,{"disambiguationData":[TD([[subQ2,-1.0]])],"derivedFrom":subQ1}),-1.0]])]});}
            var Q28;
            {var subQ0=sQuery(id+"F25.wireOp",EDGE,"E272.trimOffspring");var subQ1=sQuery(id+"F25.wireOp",EDGE,"E246.right");var subQ2=makeQuery(id+"F25.imprint","INTERSECT",VERTEX,{"derivedFrom":[subQ1,subQ0]});Q28=makeQuery(id+"F25.imprint","IMPRINT",FACE,{"disambiguationData":[TD([[makeQuery(id+"F25.imprint","IMPRINT",EDGE,{"disambiguationData":[TD([[subQ2,-1.0]])],"derivedFrom":subQ1}),-1.0]])]});}
            var Q29;
            {var subQ0=sQuery(id+"F25.wireOp",EDGE,"E272.trimOffspring");var subQ1=sQuery(id+"F25.wireOp",EDGE,"E245.left");var subQ2=makeQuery(id+"F25.imprint","INTERSECT",VERTEX,{"derivedFrom":[subQ1,subQ0]});Q29=makeQuery(id+"F25.imprint","IMPRINT",FACE,{"disambiguationData":[TD([[makeQuery(id+"F25.imprint","IMPRINT",EDGE,{"disambiguationData":[TD([[subQ2,-1.0]])],"derivedFrom":subQ1}),-1.0]])]});}
            var Q30;
            {var subQ0=sQuery(id+"F25.wireOp",EDGE,"E273.trimOffspring");var subQ1=sQuery(id+"F25.wireOp",EDGE,"E245.right");var subQ2=makeQuery(id+"F25.imprint","INTERSECT",VERTEX,{"derivedFrom":[subQ1,subQ0]});Q30=makeQuery(id+"F25.imprint","IMPRINT",FACE,{"disambiguationData":[TD([[makeQuery(id+"F25.imprint","IMPRINT",EDGE,{"disambiguationData":[TD([[subQ2,1.0]])],"derivedFrom":subQ1}),-1.0]])]});}
            var Q31;
            {var subQ0=sQuery(id+"F25.wireOp",EDGE,"E272.trimOffspring");var subQ1=sQuery(id+"F25.wireOp",EDGE,"E244.right");var subQ2=makeQuery(id+"F25.imprint","INTERSECT",VERTEX,{"derivedFrom":[subQ1,subQ0]});Q31=makeQuery(id+"F25.imprint","IMPRINT",FACE,{"disambiguationData":[TD([[makeQuery(id+"F25.imprint","IMPRINT",EDGE,{"disambiguationData":[TD([[subQ2,-1.0]])],"derivedFrom":subQ1}),-1.0]])]});}
            var Q32;
            {var subQ0=sQuery(id+"F25.wireOp",EDGE,"E275.trimOffspring");var subQ1=sQuery(id+"F25.wireOp",EDGE,"E243.right");var subQ2=makeQuery(id+"F25.imprint","INTERSECT",VERTEX,{"derivedFrom":[subQ1,subQ0]});Q32=makeQuery(id+"F25.imprint","IMPRINT",FACE,{"disambiguationData":[TD([[makeQuery(id+"F25.imprint","IMPRINT",EDGE,{"disambiguationData":[TD([[subQ2,1.0]])],"derivedFrom":subQ1}),-1.0]])]});}
            var Q33;
            {var subQ0=sQuery(id+"F25.wireOp",EDGE,"E272.trimOffspring");var subQ1=sQuery(id+"F25.wireOp",EDGE,"E243.right");var subQ2=makeQuery(id+"F25.imprint","INTERSECT",VERTEX,{"derivedFrom":[subQ1,subQ0]});Q33=makeQuery(id+"F25.imprint","IMPRINT",FACE,{"disambiguationData":[TD([[makeQuery(id+"F25.imprint","IMPRINT",EDGE,{"disambiguationData":[TD([[subQ2,-1.0]])],"derivedFrom":subQ1}),-1.0]])]});}
            var Q34;
            {var subQ0=sQuery(id+"F25.wireOp",EDGE,"E272.trimOffspring");var subQ1=sQuery(id+"F25.wireOp",EDGE,"E243.left");var subQ2=makeQuery(id+"F25.imprint","INTERSECT",VERTEX,{"derivedFrom":[subQ1,subQ0]});Q34=makeQuery(id+"F25.imprint","IMPRINT",FACE,{"disambiguationData":[TD([[makeQuery(id+"F25.imprint","IMPRINT",EDGE,{"disambiguationData":[TD([[subQ2,-1.0]])],"derivedFrom":subQ1}),-1.0]])]});}
            var Q35;
            {var subQ0=sQuery(id+"F25.wireOp",EDGE,"E271.trimOffspring");var subQ1=sQuery(id+"F25.wireOp",EDGE,"E243.left");var subQ2=makeQuery(id+"F25.imprint","INTERSECT",VERTEX,{"derivedFrom":[subQ1,subQ0]});Q35=makeQuery(id+"F25.imprint","IMPRINT",FACE,{"disambiguationData":[TD([[makeQuery(id+"F25.imprint","IMPRINT",EDGE,{"disambiguationData":[TD([[subQ2,-1.0]])],"derivedFrom":subQ1}),-1.0]])]});}
            var Q36;
            {var subQ0=sQuery(id+"F25.wireOp",EDGE,"E271.trimOffspring");var subQ1=sQuery(id+"F25.wireOp",EDGE,"E243.right");var subQ2=makeQuery(id+"F25.imprint","INTERSECT",VERTEX,{"derivedFrom":[subQ1,subQ0]});Q36=makeQuery(id+"F25.imprint","IMPRINT",FACE,{"disambiguationData":[TD([[makeQuery(id+"F25.imprint","IMPRINT",EDGE,{"disambiguationData":[TD([[subQ2,-1.0]])],"derivedFrom":subQ1}),-1.0]])]});}
            var Q37;
            {var subQ0=sQuery(id+"F25.wireOp",EDGE,"E271.trimOffspring");var subQ1=sQuery(id+"F25.wireOp",EDGE,"E243.right");var subQ2=makeQuery(id+"F25.imprint","INTERSECT",VERTEX,{"derivedFrom":[subQ1,subQ0]});Q37=makeQuery(id+"F25.imprint","IMPRINT",FACE,{"disambiguationData":[TD([[makeQuery(id+"F25.imprint","IMPRINT",EDGE,{"disambiguationData":[TD([[subQ2,1.0]])],"derivedFrom":subQ1}),-1.0]])]});}
            var Q38;
            {var subQ0=sQuery(id+"F25.wireOp",EDGE,"E274.trimOffspring");var subQ1=sQuery(id+"F25.wireOp",EDGE,"E243.right");var subQ2=makeQuery(id+"F25.imprint","INTERSECT",VERTEX,{"derivedFrom":[subQ1,subQ0]});Q38=makeQuery(id+"F25.imprint","IMPRINT",FACE,{"disambiguationData":[TD([[makeQuery(id+"F25.imprint","IMPRINT",EDGE,{"disambiguationData":[TD([[subQ2,-1.0]])],"derivedFrom":subQ1}),-1.0]])]});}
            var Q39;
            {var subQ0=sQuery(id+"F25.wireOp",EDGE,"E274.trimOffspring");var subQ1=sQuery(id+"F25.wireOp",EDGE,"E243.left");var subQ2=makeQuery(id+"F25.imprint","INTERSECT",VERTEX,{"derivedFrom":[subQ1,subQ0]});Q39=makeQuery(id+"F25.imprint","IMPRINT",FACE,{"disambiguationData":[TD([[makeQuery(id+"F25.imprint","IMPRINT",EDGE,{"disambiguationData":[TD([[subQ2,-1.0]])],"derivedFrom":subQ1}),-1.0]])]});}
            var Q40;
            {var subQ0=sQuery(id+"F25.wireOp",EDGE,"E270.trimOffspring");var subQ1=sQuery(id+"F25.wireOp",EDGE,"E243.left");var subQ2=makeQuery(id+"F25.imprint","INTERSECT",VERTEX,{"derivedFrom":[subQ1,subQ0]});Q40=makeQuery(id+"F25.imprint","IMPRINT",FACE,{"disambiguationData":[TD([[makeQuery(id+"F25.imprint","IMPRINT",EDGE,{"disambiguationData":[TD([[subQ2,-1.0]])],"derivedFrom":subQ1}),-1.0]])]});}
            var Q41;
            {var subQ0=sQuery(id+"F25.wireOp",EDGE,"E270.trimOffspring");var subQ1=sQuery(id+"F25.wireOp",EDGE,"E244.right");var subQ2=makeQuery(id+"F25.imprint","INTERSECT",VERTEX,{"derivedFrom":[subQ1,subQ0]});Q41=makeQuery(id+"F25.imprint","IMPRINT",FACE,{"disambiguationData":[TD([[makeQuery(id+"F25.imprint","IMPRINT",EDGE,{"disambiguationData":[TD([[subQ2,-1.0]])],"derivedFrom":subQ1}),-1.0]])]});}
            var Q42;
            {var subQ0=sQuery(id+"F25.wireOp",EDGE,"E274.trimOffspring");var subQ1=sQuery(id+"F25.wireOp",EDGE,"E244.right");var subQ2=makeQuery(id+"F25.imprint","INTERSECT",VERTEX,{"derivedFrom":[subQ1,subQ0]});Q42=makeQuery(id+"F25.imprint","IMPRINT",FACE,{"disambiguationData":[TD([[makeQuery(id+"F25.imprint","IMPRINT",EDGE,{"disambiguationData":[TD([[subQ2,-1.0]])],"derivedFrom":subQ1}),-1.0]])]});}
            var Q43;
            {var subQ0=sQuery(id+"F25.wireOp",EDGE,"E274.trimOffspring");var subQ1=sQuery(id+"F25.wireOp",EDGE,"E245.right");var subQ2=makeQuery(id+"F25.imprint","INTERSECT",VERTEX,{"derivedFrom":[subQ1,subQ0]});Q43=makeQuery(id+"F25.imprint","IMPRINT",FACE,{"disambiguationData":[TD([[makeQuery(id+"F25.imprint","IMPRINT",EDGE,{"disambiguationData":[TD([[subQ2,-1.0]])],"derivedFrom":subQ1}),-1.0]])]});}
            var Q44;
            {var subQ0=sQuery(id+"F25.wireOp",EDGE,"E270.trimOffspring");var subQ1=sQuery(id+"F25.wireOp",EDGE,"E245.right");var subQ2=makeQuery(id+"F25.imprint","INTERSECT",VERTEX,{"derivedFrom":[subQ1,subQ0]});Q44=makeQuery(id+"F25.imprint","IMPRINT",FACE,{"disambiguationData":[TD([[makeQuery(id+"F25.imprint","IMPRINT",EDGE,{"disambiguationData":[TD([[subQ2,-1.0]])],"derivedFrom":subQ1}),-1.0]])]});}
            var Q45;
            {var subQ0=sQuery(id+"F25.wireOp",EDGE,"E270.trimOffspring");var subQ1=sQuery(id+"F25.wireOp",EDGE,"E245.left");var subQ2=makeQuery(id+"F25.imprint","INTERSECT",VERTEX,{"derivedFrom":[subQ1,subQ0]});Q45=makeQuery(id+"F25.imprint","IMPRINT",FACE,{"disambiguationData":[TD([[makeQuery(id+"F25.imprint","IMPRINT",EDGE,{"disambiguationData":[TD([[subQ2,-1.0]])],"derivedFrom":subQ1}),-1.0]])]});}
            var Q46;
            {var subQ0=sQuery(id+"F25.wireOp",EDGE,"E274.trimOffspring");var subQ1=sQuery(id+"F25.wireOp",EDGE,"E245.left");var subQ2=makeQuery(id+"F25.imprint","INTERSECT",VERTEX,{"derivedFrom":[subQ1,subQ0]});Q46=makeQuery(id+"F25.imprint","IMPRINT",FACE,{"disambiguationData":[TD([[makeQuery(id+"F25.imprint","IMPRINT",EDGE,{"disambiguationData":[TD([[subQ2,-1.0]])],"derivedFrom":subQ1}),-1.0]])]});}
            var Q47;
            {var subQ0=sQuery(id+"F25.wireOp",EDGE,"E274.trimOffspring");var subQ1=sQuery(id+"F25.wireOp",EDGE,"E246.right");var subQ2=makeQuery(id+"F25.imprint","INTERSECT",VERTEX,{"derivedFrom":[subQ1,subQ0]});Q47=makeQuery(id+"F25.imprint","IMPRINT",FACE,{"disambiguationData":[TD([[makeQuery(id+"F25.imprint","IMPRINT",EDGE,{"disambiguationData":[TD([[subQ2,-1.0]])],"derivedFrom":subQ1}),-1.0]])]});}
            var Q48;
            {var subQ0=sQuery(id+"F25.wireOp",EDGE,"E270.trimOffspring");var subQ1=sQuery(id+"F25.wireOp",EDGE,"E246.right");var subQ2=makeQuery(id+"F25.imprint","INTERSECT",VERTEX,{"derivedFrom":[subQ1,subQ0]});Q48=makeQuery(id+"F25.imprint","IMPRINT",FACE,{"disambiguationData":[TD([[makeQuery(id+"F25.imprint","IMPRINT",EDGE,{"disambiguationData":[TD([[subQ2,-1.0]])],"derivedFrom":subQ1}),-1.0]])]});}
            var Q49;
            {var subQ0=sQuery(id+"F25.wireOp",EDGE,"E259.trimOffspring");var subQ1=sQuery(id+"F25.wireOp",EDGE,"E236.bottom");var subQ2=makeQuery(id+"F25.imprint","INTERSECT",VERTEX,{"derivedFrom":[subQ1,subQ0]});Q49=makeQuery(id+"F25.imprint","IMPRINT",FACE,{"disambiguationData":[TD([[makeQuery(id+"F25.imprint","IMPRINT",EDGE,{"disambiguationData":[TD([[subQ2,-1.0]])],"derivedFrom":subQ1}),-1.0]])]});}
            var Q50;
            {var subQ0=sQuery(id+"F25.wireOp",EDGE,"E259.trimOffspring");var subQ1=sQuery(id+"F25.wireOp",EDGE,"E235.top");var subQ2=makeQuery(id+"F25.imprint","INTERSECT",VERTEX,{"derivedFrom":[subQ1,subQ0]});Q50=makeQuery(id+"F25.imprint","IMPRINT",FACE,{"disambiguationData":[TD([[makeQuery(id+"F25.imprint","IMPRINT",EDGE,{"disambiguationData":[TD([[subQ2,-1.0]])],"derivedFrom":subQ1}),-1.0]])]});}
            var Q51;
            {var subQ0=sQuery(id+"F25.wireOp",EDGE,"E259.trimOffspring");var subQ1=sQuery(id+"F25.wireOp",EDGE,"E235.top");var subQ2=makeQuery(id+"F25.imprint","INTERSECT",VERTEX,{"derivedFrom":[subQ1,subQ0]});Q51=makeQuery(id+"F25.imprint","IMPRINT",FACE,{"disambiguationData":[TD([[makeQuery(id+"F25.imprint","IMPRINT",EDGE,{"disambiguationData":[TD([[subQ2,-1.0]])],"derivedFrom":subQ1}),1.0]])]});}
            var Q52;
            {var subQ0=sQuery(id+"F25.wireOp",EDGE,"E499.trimOffspring");var subQ1=sQuery(id+"F25.wireOp",EDGE,"E258.trimOffspring");var subQ2=makeQuery(id+"F25.imprint","INTERSECT",VERTEX,{"derivedFrom":[subQ1,subQ0]});Q52=makeQuery(id+"F25.imprint","IMPRINT",FACE,{"disambiguationData":[TD([[makeQuery(id+"F25.imprint","IMPRINT",EDGE,{"disambiguationData":[TD([[subQ2,1.0]])],"derivedFrom":subQ1}),1.0]])]});}
            var Q53;
            {var subQ0=sQuery(id+"F25.wireOp",EDGE,"E499.trimOffspring");var subQ1=sQuery(id+"F25.wireOp",EDGE,"E258.trimOffspring");var subQ2=makeQuery(id+"F25.imprint","INTERSECT",VERTEX,{"derivedFrom":[subQ1,subQ0]});Q53=makeQuery(id+"F25.imprint","IMPRINT",FACE,{"disambiguationData":[TD([[makeQuery(id+"F25.imprint","IMPRINT",EDGE,{"disambiguationData":[TD([[subQ2,-1.0]])],"derivedFrom":subQ1}),1.0]])]});}
            var Q54;
            {var subQ0=sQuery(id+"F25.wireOp",EDGE,"E518.trimOffspring");var subQ1=sQuery(id+"F25.wireOp",EDGE,"E279.trimOffspring");var subQ2=makeQuery(id+"F25.imprint","INTERSECT",VERTEX,{"derivedFrom":[subQ1,subQ0]});Q54=makeQuery(id+"F25.imprint","IMPRINT",FACE,{"disambiguationData":[TD([[makeQuery(id+"F25.imprint","IMPRINT",EDGE,{"disambiguationData":[TD([[subQ2,-1.0]])],"derivedFrom":subQ1}),-1.0]])]});}
            var Q55;
            {var subQ0=sQuery(id+"F25.wireOp",EDGE,"E507.trimOffspring");var subQ1=sQuery(id+"F25.wireOp",EDGE,"E279.trimOffspring");var subQ2=makeQuery(id+"F25.imprint","INTERSECT",VERTEX,{"derivedFrom":[subQ1,subQ0]});Q55=makeQuery(id+"F25.imprint","IMPRINT",FACE,{"disambiguationData":[TD([[makeQuery(id+"F25.imprint","IMPRINT",EDGE,{"disambiguationData":[TD([[subQ2,-1.0]])],"derivedFrom":subQ1}),-1.0]])]});}
            var Q56;
            {var subQ0=sQuery(id+"F25.wireOp",EDGE,"E512.trimOffspring");var subQ1=sQuery(id+"F25.wireOp",EDGE,"E279.trimOffspring");var subQ2=makeQuery(id+"F25.imprint","INTERSECT",VERTEX,{"derivedFrom":[subQ1,subQ0]});Q56=makeQuery(id+"F25.imprint","IMPRINT",FACE,{"disambiguationData":[TD([[makeQuery(id+"F25.imprint","IMPRINT",EDGE,{"disambiguationData":[TD([[subQ2,-1.0]])],"derivedFrom":subQ1}),-1.0]])]});}
            var Q57;
            {var subQ0=sQuery(id+"F25.wireOp",EDGE,"E510.trimOffspring");var subQ1=sQuery(id+"F25.wireOp",EDGE,"E279.trimOffspring");var subQ2=makeQuery(id+"F25.imprint","INTERSECT",VERTEX,{"derivedFrom":[subQ1,subQ0]});Q57=makeQuery(id+"F25.imprint","IMPRINT",FACE,{"disambiguationData":[TD([[makeQuery(id+"F25.imprint","IMPRINT",EDGE,{"disambiguationData":[TD([[subQ2,-1.0]])],"derivedFrom":subQ1}),-1.0]])]});}
            var Q58;
            {var subQ0=sQuery(id+"F25.wireOp",EDGE,"E522.trimOffspring");var subQ1=sQuery(id+"F25.wireOp",EDGE,"E279.trimOffspring");var subQ2=makeQuery(id+"F25.imprint","INTERSECT",VERTEX,{"derivedFrom":[subQ1,subQ0]});Q58=makeQuery(id+"F25.imprint","IMPRINT",FACE,{"disambiguationData":[TD([[makeQuery(id+"F25.imprint","IMPRINT",EDGE,{"disambiguationData":[TD([[subQ2,-1.0]])],"derivedFrom":subQ1}),-1.0]])]});}
            var Q59;
            {var subQ0=sQuery(id+"F25.wireOp",EDGE,"E525.trimOffspring");var subQ1=sQuery(id+"F25.wireOp",EDGE,"E279.trimOffspring");var subQ2=makeQuery(id+"F25.imprint","INTERSECT",VERTEX,{"derivedFrom":[subQ1,subQ0]});Q59=makeQuery(id+"F25.imprint","IMPRINT",FACE,{"disambiguationData":[TD([[makeQuery(id+"F25.imprint","IMPRINT",EDGE,{"disambiguationData":[TD([[subQ2,1.0]])],"derivedFrom":subQ1}),-1.0]])]});}
            var Q60;
            {var subQ0=sQuery(id+"F25.wireOp",EDGE,"E616.trimOffspring");var subQ1=sQuery(id+"F25.wireOp",EDGE,"E409.MirrorCS");var subQ2=makeQuery(id+"F25.imprint","INTERSECT",VERTEX,{"derivedFrom":[subQ1,subQ0]});Q60=makeQuery(id+"F25.imprint","IMPRINT",FACE,{"disambiguationData":[TD([[makeQuery(id+"F25.imprint","IMPRINT",EDGE,{"disambiguationData":[TD([[subQ2,-1.0]])],"derivedFrom":subQ1}),-1.0]])]});}
            var Q61;
            {var subQ1=sQuery(id+"F25.wireOp",EDGE,"E409.MirrorCS");var subQ3=sQuery(id+"F25.wireOp",EDGE,"E477.trimOffspring");var subQ4=makeQuery(id+"F25.imprint","INTERSECT",VERTEX,{"derivedFrom":[subQ1,subQ3]});Q61=makeQuery(id+"F25.imprint","IMPRINT",FACE,{"disambiguationData":[TD([[makeQuery(id+"F25.imprint","IMPRINT",EDGE,{"disambiguationData":[TD([[subQ4,1.0]])],"derivedFrom":subQ3}),-1.0]])]});}
            var Q62;
            {var subQ1=sQuery(id+"F25.wireOp",EDGE,"E415.MirrorCS");var subQ3=sQuery(id+"F25.wireOp",EDGE,"E475.trimOffspring");var subQ4=makeQuery(id+"F25.imprint","INTERSECT",VERTEX,{"derivedFrom":[subQ1,subQ3]});Q62=makeQuery(id+"F25.imprint","IMPRINT",FACE,{"disambiguationData":[TD([[makeQuery(id+"F25.imprint","IMPRINT",EDGE,{"disambiguationData":[TD([[subQ4,1.0]])],"derivedFrom":subQ3}),1.0]])]});}
            var Q63;
            {var subQ0=sQuery(id+"F25.wireOp",EDGE,"E476.trimOffspring");var subQ1=sQuery(id+"F25.wireOp",EDGE,"E415.MirrorCS");var subQ2=makeQuery(id+"F25.imprint","INTERSECT",VERTEX,{"derivedFrom":[subQ1,subQ0]});Q63=makeQuery(id+"F25.imprint","IMPRINT",FACE,{"disambiguationData":[TD([[makeQuery(id+"F25.imprint","IMPRINT",EDGE,{"disambiguationData":[TD([[subQ2,-1.0]])],"derivedFrom":subQ1}),1.0]])]});}
            var Q64;
            {var subQ0=sQuery(id+"F25.wireOp",EDGE,"E474.trimOffspring");var subQ1=sQuery(id+"F25.wireOp",EDGE,"E415.MirrorCS");var subQ2=makeQuery(id+"F25.imprint","INTERSECT",VERTEX,{"derivedFrom":[subQ1,subQ0]});Q64=makeQuery(id+"F25.imprint","IMPRINT",FACE,{"disambiguationData":[TD([[makeQuery(id+"F25.imprint","IMPRINT",EDGE,{"disambiguationData":[TD([[subQ2,-1.0]])],"derivedFrom":subQ1}),1.0]])]});}
            var Q65;
            {var subQ0=sQuery(id+"F25.wireOp",EDGE,"E473.trimOffspring");var subQ1=sQuery(id+"F25.wireOp",EDGE,"E415.MirrorCS");var subQ2=makeQuery(id+"F25.imprint","INTERSECT",VERTEX,{"derivedFrom":[subQ1,subQ0]});Q65=makeQuery(id+"F25.imprint","IMPRINT",FACE,{"disambiguationData":[TD([[makeQuery(id+"F25.imprint","IMPRINT",EDGE,{"disambiguationData":[TD([[subQ2,-1.0]])],"derivedFrom":subQ1}),1.0]])]});}
            var Q66;
            {var subQ0=sQuery(id+"F25.wireOp",EDGE,"E591.trimOffspring");var subQ1=sQuery(id+"F25.wireOp",EDGE,"E440.MirrorCS");var subQ2=makeQuery(id+"F25.imprint","INTERSECT",VERTEX,{"derivedFrom":[subQ1,subQ0]});Q66=makeQuery(id+"F25.imprint","IMPRINT",FACE,{"disambiguationData":[TD([[makeQuery(id+"F25.imprint","IMPRINT",EDGE,{"disambiguationData":[TD([[subQ2,1.0]])],"derivedFrom":subQ1}),-1.0]])]});}
            var Q67;
            {var subQ0=sQuery(id+"F25.wireOp",EDGE,"E593.trimOffspring");var subQ1=sQuery(id+"F25.wireOp",EDGE,"E440.MirrorCS");var subQ2=makeQuery(id+"F25.imprint","INTERSECT",VERTEX,{"derivedFrom":[subQ1,subQ0]});Q67=makeQuery(id+"F25.imprint","IMPRINT",FACE,{"disambiguationData":[TD([[makeQuery(id+"F25.imprint","IMPRINT",EDGE,{"disambiguationData":[TD([[subQ2,-1.0]])],"derivedFrom":subQ1}),-1.0]])]});}
            var Q68;
            {var subQ0=sQuery(id+"F25.wireOp",EDGE,"E590.trimOffspring");var subQ1=sQuery(id+"F25.wireOp",EDGE,"E440.MirrorCS");var subQ2=makeQuery(id+"F25.imprint","INTERSECT",VERTEX,{"derivedFrom":[subQ1,subQ0]});Q68=makeQuery(id+"F25.imprint","IMPRINT",FACE,{"disambiguationData":[TD([[makeQuery(id+"F25.imprint","IMPRINT",EDGE,{"disambiguationData":[TD([[subQ2,-1.0]])],"derivedFrom":subQ1}),-1.0]])]});}
            var Q69;
            {var subQ0=sQuery(id+"F25.wireOp",EDGE,"E567.trimOffspring");var subQ5=sQuery(id+"F25.wireOp",EDGE,"E451.MirrorCS");var subQ6=makeQuery(id+"F25.imprint","INTERSECT",VERTEX,{"derivedFrom":[subQ5,subQ0]});Q69=makeQuery(id+"F25.imprint","IMPRINT",FACE,{"disambiguationData":[TD([[makeQuery(id+"F25.imprint","IMPRINT",EDGE,{"disambiguationData":[TD([[subQ6,-1.0]])],"derivedFrom":subQ5}),1.0]])]});}
            var Q70;
            {var subQ3=sQuery(id+"F25.wireOp",EDGE,"E567.trimOffspring");var subQ5=sQuery(id+"F25.wireOp",EDGE,"E451.MirrorCS");var subQ7=makeQuery(id+"F25.imprint","INTERSECT",VERTEX,{"derivedFrom":[subQ5,subQ3]});Q70=makeQuery(id+"F25.imprint","IMPRINT",FACE,{"disambiguationData":[TD([[makeQuery(id+"F25.imprint","IMPRINT",EDGE,{"disambiguationData":[TD([[subQ7,1.0]])],"derivedFrom":subQ5}),1.0]])]});}
            var Q71;
            {var subQ3=sQuery(id+"F25.wireOp",EDGE,"E584.trimOffspring");Q71=makeQuery(id+"F25.imprint","IMPRINT",FACE,{"disambiguationData":[TD([[makeQuery(id+"F25.imprint","IMPRINT",EDGE,{"derivedFrom":subQ3}),-1.0]])]});}
            var Q72;
            {var subQ0=sQuery(id+"F25.wireOp",EDGE,"E516.trimOffspring");var subQ1=sQuery(id+"F25.wireOp",EDGE,"E264.trimOffspring");var subQ2=makeQuery(id+"F25.imprint","INTERSECT",VERTEX,{"derivedFrom":[subQ1,subQ0]});Q72=makeQuery(id+"F25.imprint","IMPRINT",FACE,{"disambiguationData":[TD([[makeQuery(id+"F25.imprint","IMPRINT",EDGE,{"disambiguationData":[TD([[subQ2,-1.0]])],"derivedFrom":subQ1}),1.0]])]});}
            var Q73;
            {var subQ0=sQuery(id+"F25.wireOp",EDGE,"E532.trimOffspring");var subQ1=sQuery(id+"F25.wireOp",EDGE,"E264.trimOffspring");var subQ2=makeQuery(id+"F25.imprint","INTERSECT",VERTEX,{"derivedFrom":[subQ1,subQ0]});Q73=makeQuery(id+"F25.imprint","IMPRINT",FACE,{"disambiguationData":[TD([[makeQuery(id+"F25.imprint","IMPRINT",EDGE,{"disambiguationData":[TD([[subQ2,-1.0]])],"derivedFrom":subQ1}),1.0]])]});}
            var Q74;
            {var subQ0=sQuery(id+"F25.wireOp",EDGE,"E527.trimOffspring");var subQ1=sQuery(id+"F25.wireOp",EDGE,"E264.trimOffspring");var subQ2=makeQuery(id+"F25.imprint","INTERSECT",VERTEX,{"derivedFrom":[subQ1,subQ0]});Q74=makeQuery(id+"F25.imprint","IMPRINT",FACE,{"disambiguationData":[TD([[makeQuery(id+"F25.imprint","IMPRINT",EDGE,{"disambiguationData":[TD([[subQ2,-1.0]])],"derivedFrom":subQ1}),1.0]])]});}
            var Q75;
            {var subQ0=sQuery(id+"F25.wireOp",EDGE,"E533.trimOffspring");var subQ1=sQuery(id+"F25.wireOp",EDGE,"E264.trimOffspring");var subQ2=makeQuery(id+"F25.imprint","INTERSECT",VERTEX,{"derivedFrom":[subQ1,subQ0]});Q75=makeQuery(id+"F25.imprint","IMPRINT",FACE,{"disambiguationData":[TD([[makeQuery(id+"F25.imprint","IMPRINT",EDGE,{"disambiguationData":[TD([[subQ2,-1.0]])],"derivedFrom":subQ1}),1.0]])]});}
            var Q76;
            {var subQ0=sQuery(id+"F25.wireOp",EDGE,"E538.trimOffspring");var subQ1=sQuery(id+"F25.wireOp",EDGE,"E264.trimOffspring");var subQ2=makeQuery(id+"F25.imprint","INTERSECT",VERTEX,{"derivedFrom":[subQ1,subQ0]});Q76=makeQuery(id+"F25.imprint","IMPRINT",FACE,{"disambiguationData":[TD([[makeQuery(id+"F25.imprint","IMPRINT",EDGE,{"disambiguationData":[TD([[subQ2,-1.0]])],"derivedFrom":subQ1}),1.0]])]});}
            var Q77;
            {var subQ0=sQuery(id+"F25.wireOp",EDGE,"E542.trimOffspring");var subQ1=sQuery(id+"F25.wireOp",EDGE,"E264.trimOffspring");var subQ2=makeQuery(id+"F25.imprint","INTERSECT",VERTEX,{"derivedFrom":[subQ1,subQ0]});Q77=makeQuery(id+"F25.imprint","IMPRINT",FACE,{"disambiguationData":[TD([[makeQuery(id+"F25.imprint","IMPRINT",EDGE,{"disambiguationData":[TD([[subQ2,1.0]])],"derivedFrom":subQ1}),1.0]])]});}
            extrude(context, id + "F34", {"entities" : qUnion([Q0, Q1, Q2, Q3, Q4, Q5, Q6, Q7, Q8, Q9, Q10, Q11, Q12, Q13, Q14, Q15, Q16, Q17, Q18, Q19, Q20, Q21, Q22, Q23, Q24, Q25, Q26, Q27, Q28, Q29, Q30, Q31, Q32, Q33, Q34, Q35, Q36, Q37, Q38, Q39, Q40, Q41, Q42, Q43, Q44, Q45, Q46, Q47, Q48, Q49, Q50, Q51, Q52, Q53, Q54, Q55, Q56, Q57, Q58, Q59, Q60, Q61, Q62, Q63, Q64, Q65, Q66, Q67, Q68, Q69, Q70, Q71, Q72, Q73, Q74, Q75, Q76, Q77]), "operationType" : NewBodyOperationType.REMOVE, "depth" : 19.5 * mm, "offsetDistance" : 25 * mm});
        }
        {
            var Q0;
            Q0=qCreatedBy(id+"F1.planeOp",FACE);
            var sketch = newSketch(context, id + "F35", { "sketchPlane" : qUnion([Q0])});
            skLineSegment(sketch, "E716.bottom", {"start": v(-365, 200) * mm, "end": v(365, 200) * mm});
            skLineSegment(sketch, "E716.top", {"start": v(-365, -200) * mm, "end": v(365, -200) * mm});
            skLineSegment(sketch, "E716.left", {"start": v(-365, 200) * mm, "end": v(-365, -200) * mm});
            skLineSegment(sketch, "E716.right", {"start": v(365, 200) * mm, "end": v(365, -200) * mm});
            skPoint(sketch, "E716.middle", {"position": v(0, 0) * mm});
            skLineSegment(sketch, "E717.bottom", {"start": v(0, 0) * mm, "end": v(-365, 0) * mm});
            skLineSegment(sketch, "E717.top", {"start": v(0, -200) * mm, "end": v(-365, -200) * mm});
            skLineSegment(sketch, "E717.left", {"start": v(0, 0) * mm, "end": v(0, -200) * mm});
            skLineSegment(sketch, "E717.right", {"start": v(-365, 0) * mm, "end": v(-365, -200) * mm});
            skLineSegment(sketch, "E718.top", {"start": v(0, 50) * mm, "end": v(-365, 50) * mm});
            skLineSegment(sketch, "E718.left", {"start": v(0, 0) * mm, "end": v(0, 50) * mm});
            skLineSegment(sketch, "E718.right", {"start": v(-365, 0) * mm, "end": v(-365, 50) * mm});
            skLineSegment(sketch, "E719.bottom", {"start": v(0, 0) * mm, "end": v(-182.5, 0) * mm});
            skLineSegment(sketch, "E719.top", {"start": v(0, -50) * mm, "end": v(-182.5, -50) * mm});
            skLineSegment(sketch, "E719.left", {"start": v(0, 0) * mm, "end": v(0, -50) * mm});
            skLineSegment(sketch, "E719.right", {"start": v(-182.5, 0) * mm, "end": v(-182.5, -50) * mm});
            skPoint(sketch, "E720", {"position": v(-319.37, 0) * mm});
            skPoint(sketch, "E721", {"position": v(-273.75, 0) * mm});
            skPoint(sketch, "E722", {"position": v(-228.12, 0) * mm});
            skPoint(sketch, "E723", {"position": v(-192.5, 0) * mm});
            skPoint(sketch, "E724", {"position": v(-172.5, 0) * mm});
            skPoint(sketch, "E725", {"position": v(-136.88, 0) * mm});
            skPoint(sketch, "E726", {"position": v(-91.25, 0) * mm});
            skPoint(sketch, "E727", {"position": v(-45.62, 0) * mm});
            skPoint(sketch, "E728", {"position": v(-10, 0) * mm});
            skPoint(sketch, "E729", {"position": v(10, 0) * mm});
            skPoint(sketch, "E730", {"position": v(-365, -20) * mm});
            skPoint(sketch, "E731", {"position": v(-365, -40) * mm});
            skPoint(sketch, "E732", {"position": v(-365, -60) * mm});
            skPoint(sketch, "E733", {"position": v(-365, -87.5) * mm});
            skPoint(sketch, "E734", {"position": v(-365, -125) * mm});
            skPoint(sketch, "E735", {"position": v(-365, -162.5) * mm});
            skLineSegment(sketch, "E736.bottom", {"start": v(-365, 0) * mm, "end": v(0, 0) * mm});
            skLineSegment(sketch, "E736.top", {"start": v(-365, -0.5) * mm, "end": v(0, -0.5) * mm});
            skLineSegment(sketch, "E736.left", {"start": v(-365, 0) * mm, "end": v(-365, -0.5) * mm});
            skLineSegment(sketch, "E736.right", {"start": v(0, 0) * mm, "end": v(0, -0.5) * mm});
            skLineSegment(sketch, "E737.bottom", {"start": v(-365, -20) * mm, "end": v(0, -20) * mm});
            skLineSegment(sketch, "E737.top", {"start": v(-365, -20.5) * mm, "end": v(0, -20.5) * mm});
            skLineSegment(sketch, "E737.left", {"start": v(-365, -20) * mm, "end": v(-365, -20.5) * mm});
            skLineSegment(sketch, "E737.right", {"start": v(0, -20) * mm, "end": v(0, -20.5) * mm});
            skLineSegment(sketch, "E738.top", {"start": v(-365, -19.5) * mm, "end": v(0, -19.5) * mm});
            skLineSegment(sketch, "E738.left", {"start": v(-365, -20) * mm, "end": v(-365, -19.5) * mm});
            skLineSegment(sketch, "E738.right", {"start": v(0, -20) * mm, "end": v(0, -19.5) * mm});
            skLineSegment(sketch, "E739.bottom", {"start": v(-365, -40) * mm, "end": v(0, -40) * mm});
            skLineSegment(sketch, "E739.top", {"start": v(-365, -39.5) * mm, "end": v(0, -39.5) * mm});
            skLineSegment(sketch, "E739.left", {"start": v(-365, -40) * mm, "end": v(-365, -39.5) * mm});
            skLineSegment(sketch, "E739.right", {"start": v(0, -40) * mm, "end": v(0, -39.5) * mm});
            skLineSegment(sketch, "E740.top", {"start": v(-365, -40.5) * mm, "end": v(0, -40.5) * mm});
            skLineSegment(sketch, "E740.left", {"start": v(-365, -40) * mm, "end": v(-365, -40.5) * mm});
            skLineSegment(sketch, "E740.right", {"start": v(0, -40) * mm, "end": v(0, -40.5) * mm});
            skLineSegment(sketch, "E741.bottom", {"start": v(-365, -50) * mm, "end": v(0, -50) * mm});
            skLineSegment(sketch, "E741.top", {"start": v(-365, -49.5) * mm, "end": v(0, -49.5) * mm});
            skLineSegment(sketch, "E741.left", {"start": v(-365, -50) * mm, "end": v(-365, -49.5) * mm});
            skLineSegment(sketch, "E741.right", {"start": v(0, -50) * mm, "end": v(0, -49.5) * mm});
            skLineSegment(sketch, "E742.top", {"start": v(-365, -50.5) * mm, "end": v(0, -50.5) * mm});
            skLineSegment(sketch, "E742.left", {"start": v(-365, -50) * mm, "end": v(-365, -50.5) * mm});
            skLineSegment(sketch, "E742.right", {"start": v(0, -50) * mm, "end": v(0, -50.5) * mm});
            skLineSegment(sketch, "E743.bottom", {"start": v(-365, -60) * mm, "end": v(0, -60) * mm});
            skLineSegment(sketch, "E743.top", {"start": v(-365, -59.5) * mm, "end": v(0, -59.5) * mm});
            skLineSegment(sketch, "E743.left", {"start": v(-365, -60) * mm, "end": v(-365, -59.5) * mm});
            skLineSegment(sketch, "E743.right", {"start": v(0, -60) * mm, "end": v(0, -59.5) * mm});
            skLineSegment(sketch, "E744.top", {"start": v(-365, -60.5) * mm, "end": v(0, -60.5) * mm});
            skLineSegment(sketch, "E744.left", {"start": v(-365, -60) * mm, "end": v(-365, -60.5) * mm});
            skLineSegment(sketch, "E744.right", {"start": v(0, -60) * mm, "end": v(0, -60.5) * mm});
            skLineSegment(sketch, "E745.bottom", {"start": v(-365, -87.5) * mm, "end": v(0, -87.5) * mm});
            skLineSegment(sketch, "E745.top", {"start": v(-365, -87) * mm, "end": v(0, -87) * mm});
            skLineSegment(sketch, "E745.left", {"start": v(-365, -87.5) * mm, "end": v(-365, -87) * mm});
            skLineSegment(sketch, "E745.right", {"start": v(0, -87.5) * mm, "end": v(0, -87) * mm});
            skLineSegment(sketch, "E746.top", {"start": v(-365, -88) * mm, "end": v(0, -88) * mm});
            skLineSegment(sketch, "E746.left", {"start": v(-365, -87.5) * mm, "end": v(-365, -88) * mm});
            skLineSegment(sketch, "E746.right", {"start": v(0, -87.5) * mm, "end": v(0, -88) * mm});
            skLineSegment(sketch, "E747.bottom", {"start": v(-365, -125) * mm, "end": v(0, -125) * mm});
            skLineSegment(sketch, "E747.top", {"start": v(-365, -124.5) * mm, "end": v(0, -124.5) * mm});
            skLineSegment(sketch, "E747.left", {"start": v(-365, -125) * mm, "end": v(-365, -124.5) * mm});
            skLineSegment(sketch, "E747.right", {"start": v(0, -125) * mm, "end": v(0, -124.5) * mm});
            skLineSegment(sketch, "E748.top", {"start": v(-365, -125.5) * mm, "end": v(0, -125.5) * mm});
            skLineSegment(sketch, "E748.left", {"start": v(-365, -125) * mm, "end": v(-365, -125.5) * mm});
            skLineSegment(sketch, "E748.right", {"start": v(0, -125) * mm, "end": v(0, -125.5) * mm});
            skLineSegment(sketch, "E749.bottom", {"start": v(-365, -162.5) * mm, "end": v(0, -162.5) * mm});
            skLineSegment(sketch, "E749.top", {"start": v(-365, -162) * mm, "end": v(0, -162) * mm});
            skLineSegment(sketch, "E749.left", {"start": v(-365, -162.5) * mm, "end": v(-365, -162) * mm});
            skLineSegment(sketch, "E749.right", {"start": v(0, -162.5) * mm, "end": v(0, -162) * mm});
            skLineSegment(sketch, "E750.top", {"start": v(-365, -163) * mm, "end": v(0, -163) * mm});
            skLineSegment(sketch, "E750.left", {"start": v(-365, -162.5) * mm, "end": v(-365, -163) * mm});
            skLineSegment(sketch, "E750.right", {"start": v(0, -162.5) * mm, "end": v(0, -163) * mm});
            skLineSegment(sketch, "E751.bottom", {"start": v(-319.37, 0) * mm, "end": v(-319.87, 0) * mm});
            skLineSegment(sketch, "E751.top", {"start": v(-319.37, -200) * mm, "end": v(-319.87, -200) * mm});
            skLineSegment(sketch, "E751.left", {"start": v(-319.37, 0) * mm, "end": v(-319.37, -200) * mm});
            skLineSegment(sketch, "E751.right", {"start": v(-319.87, 0) * mm, "end": v(-319.87, -200) * mm});
            skLineSegment(sketch, "E752.bottom", {"start": v(-319.37, 0) * mm, "end": v(-318.87, 0) * mm});
            skLineSegment(sketch, "E752.top", {"start": v(-319.37, -200) * mm, "end": v(-318.87, -200) * mm});
            skLineSegment(sketch, "E752.right", {"start": v(-318.87, 0) * mm, "end": v(-318.87, -200) * mm});
            skLineSegment(sketch, "E753.bottom", {"start": v(-273.75, 0) * mm, "end": v(-274.25, 0) * mm});
            skLineSegment(sketch, "E753.top", {"start": v(-273.75, -200) * mm, "end": v(-274.25, -200) * mm});
            skLineSegment(sketch, "E753.left", {"start": v(-273.75, 0) * mm, "end": v(-273.75, -200) * mm});
            skLineSegment(sketch, "E753.right", {"start": v(-274.25, 0) * mm, "end": v(-274.25, -200) * mm});
            skLineSegment(sketch, "E754.bottom", {"start": v(-273.75, 0) * mm, "end": v(-273.25, 0) * mm});
            skLineSegment(sketch, "E754.top", {"start": v(-273.75, -200) * mm, "end": v(-273.25, -200) * mm});
            skLineSegment(sketch, "E754.right", {"start": v(-273.25, 0) * mm, "end": v(-273.25, -200) * mm});
            skLineSegment(sketch, "E755.bottom", {"start": v(-228.12, 0) * mm, "end": v(-228.62, 0) * mm});
            skLineSegment(sketch, "E755.top", {"start": v(-228.12, -200) * mm, "end": v(-228.62, -200) * mm});
            skLineSegment(sketch, "E755.left", {"start": v(-228.12, 0) * mm, "end": v(-228.12, -200) * mm});
            skLineSegment(sketch, "E755.right", {"start": v(-228.62, 0) * mm, "end": v(-228.62, -200) * mm});
            skLineSegment(sketch, "E756.bottom", {"start": v(-228.12, 0) * mm, "end": v(-227.62, 0) * mm});
            skLineSegment(sketch, "E756.top", {"start": v(-228.12, -200) * mm, "end": v(-227.62, -200) * mm});
            skLineSegment(sketch, "E756.right", {"start": v(-227.62, 0) * mm, "end": v(-227.62, -200) * mm});
            skLineSegment(sketch, "E757.bottom", {"start": v(-192.5, 0) * mm, "end": v(-193, 0) * mm});
            skLineSegment(sketch, "E757.top", {"start": v(-192.5, -200) * mm, "end": v(-193, -200) * mm});
            skLineSegment(sketch, "E757.left", {"start": v(-192.5, 0) * mm, "end": v(-192.5, -200) * mm});
            skLineSegment(sketch, "E757.right", {"start": v(-193, 0) * mm, "end": v(-193, -200) * mm});
            skLineSegment(sketch, "E758.bottom", {"start": v(-192.5, 0) * mm, "end": v(-192, 0) * mm});
            skLineSegment(sketch, "E758.top", {"start": v(-192.5, -200) * mm, "end": v(-192, -200) * mm});
            skLineSegment(sketch, "E758.right", {"start": v(-192, 0) * mm, "end": v(-192, -200) * mm});
            skLineSegment(sketch, "E759.bottom", {"start": v(-182.5, 0) * mm, "end": v(-183, 0) * mm});
            skLineSegment(sketch, "E759.top", {"start": v(-182.5, -200) * mm, "end": v(-183, -200) * mm});
            skLineSegment(sketch, "E759.left", {"start": v(-182.5, 0) * mm, "end": v(-182.5, -200) * mm});
            skLineSegment(sketch, "E759.right", {"start": v(-183, 0) * mm, "end": v(-183, -200) * mm});
            skLineSegment(sketch, "E760.bottom", {"start": v(-182.5, 0) * mm, "end": v(-182, 0) * mm});
            skLineSegment(sketch, "E760.top", {"start": v(-182.5, -200) * mm, "end": v(-182, -200) * mm});
            skLineSegment(sketch, "E760.right", {"start": v(-182, 0) * mm, "end": v(-182, -200) * mm});
            skLineSegment(sketch, "E761.bottom", {"start": v(-172.5, 0) * mm, "end": v(-173, 0) * mm});
            skLineSegment(sketch, "E761.top", {"start": v(-172.5, -200) * mm, "end": v(-173, -200) * mm});
            skLineSegment(sketch, "E761.left", {"start": v(-172.5, 0) * mm, "end": v(-172.5, -200) * mm});
            skLineSegment(sketch, "E761.right", {"start": v(-173, 0) * mm, "end": v(-173, -200) * mm});
            skLineSegment(sketch, "E762.bottom", {"start": v(-172.5, 0) * mm, "end": v(-172, 0) * mm});
            skLineSegment(sketch, "E762.top", {"start": v(-172.5, -200) * mm, "end": v(-172, -200) * mm});
            skLineSegment(sketch, "E762.right", {"start": v(-172, 0) * mm, "end": v(-172, -200) * mm});
            skLineSegment(sketch, "E763.bottom", {"start": v(-136.88, 0) * mm, "end": v(-137.38, 0) * mm});
            skLineSegment(sketch, "E763.top", {"start": v(-136.87, -200) * mm, "end": v(-137.37, -200) * mm});
            skLineSegment(sketch, "E763.left", {"start": v(-136.88, 0) * mm, "end": v(-136.88, -200) * mm});
            skLineSegment(sketch, "E763.right", {"start": v(-137.38, 0) * mm, "end": v(-137.37, -200) * mm});
            skLineSegment(sketch, "E764.bottom", {"start": v(-136.88, 0) * mm, "end": v(-136.38, 0) * mm});
            skLineSegment(sketch, "E764.top", {"start": v(-136.88, -200) * mm, "end": v(-136.38, -200) * mm});
            skLineSegment(sketch, "E764.right", {"start": v(-136.38, 0) * mm, "end": v(-136.38, -200) * mm});
            skLineSegment(sketch, "E765.bottom", {"start": v(-91.25, 0) * mm, "end": v(-91.75, 0) * mm});
            skLineSegment(sketch, "E765.top", {"start": v(-91.25, -200) * mm, "end": v(-91.75, -200) * mm});
            skLineSegment(sketch, "E765.left", {"start": v(-91.25, 0) * mm, "end": v(-91.25, -200) * mm});
            skLineSegment(sketch, "E765.right", {"start": v(-91.75, 0) * mm, "end": v(-91.75, -200) * mm});
            skLineSegment(sketch, "E766.bottom", {"start": v(-91.25, 0) * mm, "end": v(-90.75, 0) * mm});
            skLineSegment(sketch, "E766.top", {"start": v(-91.25, -200) * mm, "end": v(-90.75, -200) * mm});
            skLineSegment(sketch, "E766.right", {"start": v(-90.75, 0) * mm, "end": v(-90.75, -200) * mm});
            skLineSegment(sketch, "E767.bottom", {"start": v(-45.62, 0) * mm, "end": v(-46.12, 0) * mm});
            skLineSegment(sketch, "E767.top", {"start": v(-45.62, -200) * mm, "end": v(-46.12, -200) * mm});
            skLineSegment(sketch, "E767.left", {"start": v(-45.62, 0) * mm, "end": v(-45.62, -200) * mm});
            skLineSegment(sketch, "E767.right", {"start": v(-46.12, 0) * mm, "end": v(-46.12, -200) * mm});
            skLineSegment(sketch, "E768.bottom", {"start": v(-45.62, 0) * mm, "end": v(-45.12, 0) * mm});
            skLineSegment(sketch, "E768.top", {"start": v(-45.62, -200) * mm, "end": v(-45.12, -200) * mm});
            skLineSegment(sketch, "E768.right", {"start": v(-45.12, 0) * mm, "end": v(-45.12, -200) * mm});
            skLineSegment(sketch, "E769.bottom", {"start": v(0, 0) * mm, "end": v(-0.5, 0) * mm});
            skLineSegment(sketch, "E769.top", {"start": v(0, -200) * mm, "end": v(-0.5, -200) * mm});
            skLineSegment(sketch, "E769.right", {"start": v(-0.5, 0) * mm, "end": v(-0.5, -200) * mm});
            skLineSegment(sketch, "E770.bottom", {"start": v(-10, 0) * mm, "end": v(-9.5, 0) * mm});
            skLineSegment(sketch, "E770.top", {"start": v(-10, -200) * mm, "end": v(-9.5, -200) * mm});
            skLineSegment(sketch, "E770.left", {"start": v(-10, 0) * mm, "end": v(-10, -200) * mm});
            skLineSegment(sketch, "E770.right", {"start": v(-9.5, 0) * mm, "end": v(-9.5, -200) * mm});
            skLineSegment(sketch, "E771.bottom", {"start": v(-10, 0) * mm, "end": v(-10.5, 0) * mm});
            skLineSegment(sketch, "E771.top", {"start": v(-10, -200) * mm, "end": v(-10.5, -200) * mm});
            skLineSegment(sketch, "E771.right", {"start": v(-10.5, 0) * mm, "end": v(-10.5, -200) * mm});
            skLineSegment(sketch, "E772.MirrorCS", {"start": v(365, 0) * mm, "end": v(0, 0) * mm});
            skLineSegment(sketch, "E773.MirrorCS", {"start": v(365, -0.5) * mm, "end": v(0, -0.5) * mm});
            skLineSegment(sketch, "E774.MirrorCS", {"start": v(365, -19.5) * mm, "end": v(0, -19.5) * mm});
            skLineSegment(sketch, "E775.MirrorCS", {"start": v(365, -20) * mm, "end": v(0, -20) * mm});
            skLineSegment(sketch, "E776.MirrorCS", {"start": v(365, -20.5) * mm, "end": v(0, -20.5) * mm});
            skLineSegment(sketch, "E777.MirrorCS", {"start": v(0.5, 0) * mm, "end": v(0.5, -200) * mm});
            skLineSegment(sketch, "E778.MirrorCS", {"start": v(365, -39.5) * mm, "end": v(0, -39.5) * mm});
            skLineSegment(sketch, "E779.MirrorCS", {"start": v(365, -40) * mm, "end": v(0, -40) * mm});
            skLineSegment(sketch, "E780.MirrorCS", {"start": v(365, -40.5) * mm, "end": v(0, -40.5) * mm});
            skLineSegment(sketch, "E781.MirrorCS", {"start": v(365, -49.5) * mm, "end": v(0, -49.5) * mm});
            skLineSegment(sketch, "E782.MirrorCS", {"start": v(0, -50) * mm, "end": v(182.5, -50) * mm});
            skLineSegment(sketch, "E783.MirrorCS", {"start": v(365, -50.5) * mm, "end": v(0, -50.5) * mm});
            skLineSegment(sketch, "E784.MirrorCS", {"start": v(365, -59.5) * mm, "end": v(0, -59.5) * mm});
            skLineSegment(sketch, "E785.MirrorCS", {"start": v(365, -60) * mm, "end": v(0, -60) * mm});
            skLineSegment(sketch, "E786.MirrorCS", {"start": v(365, -60.5) * mm, "end": v(0, -60.5) * mm});
            skLineSegment(sketch, "E787.MirrorCS", {"start": v(365, -87) * mm, "end": v(0, -87) * mm});
            skLineSegment(sketch, "E788.MirrorCS", {"start": v(365, -87.5) * mm, "end": v(0, -87.5) * mm});
            skLineSegment(sketch, "E789.MirrorCS", {"start": v(365, -88) * mm, "end": v(0, -88) * mm});
            skLineSegment(sketch, "E790.MirrorCS", {"start": v(365, -124.5) * mm, "end": v(0, -124.5) * mm});
            skLineSegment(sketch, "E791.MirrorCS", {"start": v(365, -125) * mm, "end": v(0, -125) * mm});
            skLineSegment(sketch, "E792.MirrorCS", {"start": v(365, -125.5) * mm, "end": v(0, -125.5) * mm});
            skLineSegment(sketch, "E793.MirrorCS", {"start": v(365, -162) * mm, "end": v(0, -162) * mm});
            skLineSegment(sketch, "E794.MirrorCS", {"start": v(365, -162.5) * mm, "end": v(0, -162.5) * mm});
            skLineSegment(sketch, "E795.MirrorCS", {"start": v(365, -163) * mm, "end": v(0, -163) * mm});
            skLineSegment(sketch, "E796.MirrorCS", {"start": v(9.5, 0) * mm, "end": v(9.5, -200) * mm});
            skLineSegment(sketch, "E797.MirrorCS", {"start": v(10, 0) * mm, "end": v(10, -200) * mm});
            skLineSegment(sketch, "E798.MirrorCS", {"start": v(10.5, 0) * mm, "end": v(10.5, -200) * mm});
            skLineSegment(sketch, "E799.MirrorCS", {"start": v(45.12, 0) * mm, "end": v(45.12, -200) * mm});
            skLineSegment(sketch, "E800.MirrorCS", {"start": v(45.62, 0) * mm, "end": v(45.62, -200) * mm});
            skLineSegment(sketch, "E801.MirrorCS", {"start": v(46.12, 0) * mm, "end": v(46.12, -200) * mm});
            skLineSegment(sketch, "E802.MirrorCS", {"start": v(90.75, 0) * mm, "end": v(90.75, -200) * mm});
            skLineSegment(sketch, "E803.MirrorCS", {"start": v(91.25, 0) * mm, "end": v(91.25, -200) * mm});
            skLineSegment(sketch, "E804.MirrorCS", {"start": v(91.75, 0) * mm, "end": v(91.75, -200) * mm});
            skLineSegment(sketch, "E805.MirrorCS", {"start": v(136.38, 0) * mm, "end": v(136.38, -200) * mm});
            skLineSegment(sketch, "E806.MirrorCS", {"start": v(136.88, 0) * mm, "end": v(136.88, -200) * mm});
            skLineSegment(sketch, "E807.MirrorCS", {"start": v(137.38, 0) * mm, "end": v(137.37, -200) * mm});
            skLineSegment(sketch, "E808.MirrorCS", {"start": v(172, 0) * mm, "end": v(172, -200) * mm});
            skLineSegment(sketch, "E809.MirrorCS", {"start": v(172.5, 0) * mm, "end": v(172.5, -200) * mm});
            skLineSegment(sketch, "E810.MirrorCS", {"start": v(173, 0) * mm, "end": v(173, -200) * mm});
            skLineSegment(sketch, "E811.MirrorCS", {"start": v(182, 0) * mm, "end": v(182, -200) * mm});
            skLineSegment(sketch, "E812.MirrorCS", {"start": v(183, 0) * mm, "end": v(183, -200) * mm});
            skLineSegment(sketch, "E813.MirrorCS", {"start": v(192, 0) * mm, "end": v(192, -200) * mm});
            skLineSegment(sketch, "E814.MirrorCS", {"start": v(192.5, 0) * mm, "end": v(192.5, -200) * mm});
            skLineSegment(sketch, "E815.MirrorCS", {"start": v(193, 0) * mm, "end": v(193, -200) * mm});
            skLineSegment(sketch, "E816.MirrorCS", {"start": v(319.87, 0) * mm, "end": v(319.87, -200) * mm});
            skLineSegment(sketch, "E817.MirrorCS", {"start": v(319.37, 0) * mm, "end": v(319.37, -200) * mm});
            skLineSegment(sketch, "E818.MirrorCS", {"start": v(318.87, 0) * mm, "end": v(318.87, -200) * mm});
            skLineSegment(sketch, "E819.MirrorCS", {"start": v(274.25, 0) * mm, "end": v(274.25, -200) * mm});
            skLineSegment(sketch, "E820.MirrorCS", {"start": v(273.75, 0) * mm, "end": v(273.75, -200) * mm});
            skLineSegment(sketch, "E821.MirrorCS", {"start": v(273.25, 0) * mm, "end": v(273.25, -200) * mm});
            skLineSegment(sketch, "E822.MirrorCS", {"start": v(228.62, 0) * mm, "end": v(228.62, -200) * mm});
            skLineSegment(sketch, "E823.MirrorCS", {"start": v(228.12, 0) * mm, "end": v(228.12, -200) * mm});
            skLineSegment(sketch, "E824.MirrorCS", {"start": v(227.62, 0) * mm, "end": v(227.62, -200) * mm});
            skLineSegment(sketch, "E825.MirrorCS", {"start": v(-365, 0.5) * mm, "end": v(0, 0.5) * mm});
            skLineSegment(sketch, "E826.MirrorCS", {"start": v(365, 0.5) * mm, "end": v(0, 0.5) * mm});
            skLineSegment(sketch, "E827.MirrorCS", {"start": v(-365, 39.5) * mm, "end": v(0, 39.5) * mm});
            skLineSegment(sketch, "E828.MirrorCS", {"start": v(-365, 40.5) * mm, "end": v(0, 40.5) * mm});
            skLineSegment(sketch, "E829.MirrorCS", {"start": v(-365, 49.5) * mm, "end": v(0, 49.5) * mm});
            skLineSegment(sketch, "E830.MirrorCS", {"start": v(-365, 50.5) * mm, "end": v(0, 50.5) * mm});
            skLineSegment(sketch, "E831.MirrorCS", {"start": v(-365, 59.5) * mm, "end": v(0, 59.5) * mm});
            skLineSegment(sketch, "E832.MirrorCS", {"start": v(-365, 60.5) * mm, "end": v(0, 60.5) * mm});
            skLineSegment(sketch, "E833.MirrorCS", {"start": v(-365, 19.5) * mm, "end": v(0, 19.5) * mm});
            skLineSegment(sketch, "E834.MirrorCS", {"start": v(-365, 20.5) * mm, "end": v(0, 20.5) * mm});
            skLineSegment(sketch, "E835.MirrorCS", {"start": v(-319.87, 0) * mm, "end": v(-319.87, 200) * mm});
            skLineSegment(sketch, "E836.MirrorCS", {"start": v(-318.87, 0) * mm, "end": v(-318.87, 200) * mm});
            skLineSegment(sketch, "E837.MirrorCS", {"start": v(-274.25, 0) * mm, "end": v(-274.25, 200) * mm});
            skLineSegment(sketch, "E838.MirrorCS", {"start": v(-273.25, 0) * mm, "end": v(-273.25, 200) * mm});
            skLineSegment(sketch, "E839.MirrorCS", {"start": v(-228.62, 0) * mm, "end": v(-228.62, 200) * mm});
            skLineSegment(sketch, "E840.MirrorCS", {"start": v(-227.62, 0) * mm, "end": v(-227.62, 200) * mm});
            skLineSegment(sketch, "E841.MirrorCS", {"start": v(-193, 0) * mm, "end": v(-193, 200) * mm});
            skLineSegment(sketch, "E842.MirrorCS", {"start": v(-192, 0) * mm, "end": v(-192, 200) * mm});
            skLineSegment(sketch, "E843.MirrorCS", {"start": v(-183, 0) * mm, "end": v(-183, 200) * mm});
            skLineSegment(sketch, "E844.MirrorCS", {"start": v(-182, 0) * mm, "end": v(-182, 200) * mm});
            skLineSegment(sketch, "E845.MirrorCS", {"start": v(-173, 0) * mm, "end": v(-173, 200) * mm});
            skLineSegment(sketch, "E846.MirrorCS", {"start": v(-172, 0) * mm, "end": v(-172, 200) * mm});
            skLineSegment(sketch, "E847.MirrorCS", {"start": v(-137.38, 0) * mm, "end": v(-137.37, 200) * mm});
            skLineSegment(sketch, "E848.MirrorCS", {"start": v(-136.38, 0) * mm, "end": v(-136.38, 200) * mm});
            skLineSegment(sketch, "E849.MirrorCS", {"start": v(-91.75, 0) * mm, "end": v(-91.75, 200) * mm});
            skLineSegment(sketch, "E850.MirrorCS", {"start": v(-90.75, 0) * mm, "end": v(-90.75, 200) * mm});
            skLineSegment(sketch, "E851.MirrorCS", {"start": v(-46.12, 0) * mm, "end": v(-46.12, 200) * mm});
            skLineSegment(sketch, "E852.MirrorCS", {"start": v(-45.12, 0) * mm, "end": v(-45.12, 200) * mm});
            skLineSegment(sketch, "E853.MirrorCS", {"start": v(-10.5, 0) * mm, "end": v(-10.5, 200) * mm});
            skLineSegment(sketch, "E854.MirrorCS", {"start": v(-9.5, 0) * mm, "end": v(-9.5, 200) * mm});
            skLineSegment(sketch, "E855.MirrorCS", {"start": v(-0.5, 0) * mm, "end": v(-0.5, 200) * mm});
            skLineSegment(sketch, "E856.MirrorCS", {"start": v(0.5, 0) * mm, "end": v(0.5, 200) * mm});
            skLineSegment(sketch, "E857.MirrorCS", {"start": v(9.5, 0) * mm, "end": v(9.5, 200) * mm});
            skLineSegment(sketch, "E858.MirrorCS", {"start": v(10.5, 0) * mm, "end": v(10.5, 200) * mm});
            skLineSegment(sketch, "E859.MirrorCS", {"start": v(365, 19.5) * mm, "end": v(0, 19.5) * mm});
            skLineSegment(sketch, "E860.MirrorCS", {"start": v(365, 20.5) * mm, "end": v(0, 20.5) * mm});
            skLineSegment(sketch, "E861.MirrorCS", {"start": v(365, 39.5) * mm, "end": v(0, 39.5) * mm});
            skLineSegment(sketch, "E862.MirrorCS", {"start": v(365, 40.5) * mm, "end": v(0, 40.5) * mm});
            skLineSegment(sketch, "E863.MirrorCS", {"start": v(365, 49.5) * mm, "end": v(0, 49.5) * mm});
            skLineSegment(sketch, "E864.MirrorCS", {"start": v(365, 50.5) * mm, "end": v(0, 50.5) * mm});
            skLineSegment(sketch, "E865.MirrorCS", {"start": v(365, 59.5) * mm, "end": v(0, 59.5) * mm});
            skLineSegment(sketch, "E866.MirrorCS", {"start": v(365, 60.5) * mm, "end": v(0, 60.5) * mm});
            skSolve(sketch);
        }
        {
            var Q0;
            {var subQ0=sQuery(id+"F35.wireOp",EDGE,"E757.right");var subQ1=sQuery(id+"F35.wireOp",EDGE,"E747.bottom");var subQ2=makeQuery(id+"F35.imprint","INTERSECT",VERTEX,{"derivedFrom":[subQ1,subQ0]});Q0=makeQuery(id+"F35.imprint","IMPRINT",FACE,{"disambiguationData":[TD([[makeQuery(id+"F35.imprint","IMPRINT",EDGE,{"disambiguationData":[TD([[subQ2,-1.0]])],"derivedFrom":subQ1}),-1.0]])]});}
            var Q1;
            {var subQ0=sQuery(id+"F35.wireOp",EDGE,"E757.left");var subQ1=sQuery(id+"F35.wireOp",EDGE,"E747.bottom");var subQ2=makeQuery(id+"F35.imprint","INTERSECT",VERTEX,{"derivedFrom":[subQ1,subQ0]});Q1=makeQuery(id+"F35.imprint","IMPRINT",FACE,{"disambiguationData":[TD([[makeQuery(id+"F35.imprint","IMPRINT",EDGE,{"disambiguationData":[TD([[subQ2,-1.0]])],"derivedFrom":subQ1}),-1.0]])]});}
            var Q2;
            {var subQ0=sQuery(id+"F35.wireOp",EDGE,"E758.right");var subQ1=sQuery(id+"F35.wireOp",EDGE,"E747.bottom");var subQ2=makeQuery(id+"F35.imprint","INTERSECT",VERTEX,{"derivedFrom":[subQ1,subQ0]});Q2=makeQuery(id+"F35.imprint","IMPRINT",FACE,{"disambiguationData":[TD([[makeQuery(id+"F35.imprint","IMPRINT",EDGE,{"disambiguationData":[TD([[subQ2,-1.0]])],"derivedFrom":subQ1}),-1.0]])]});}
            var Q3;
            {var subQ0=sQuery(id+"F35.wireOp",EDGE,"E759.right");var subQ1=sQuery(id+"F35.wireOp",EDGE,"E747.bottom");var subQ2=makeQuery(id+"F35.imprint","INTERSECT",VERTEX,{"derivedFrom":[subQ1,subQ0]});Q3=makeQuery(id+"F35.imprint","IMPRINT",FACE,{"disambiguationData":[TD([[makeQuery(id+"F35.imprint","IMPRINT",EDGE,{"disambiguationData":[TD([[subQ2,-1.0]])],"derivedFrom":subQ1}),-1.0]])]});}
            var Q4;
            {var subQ0=sQuery(id+"F35.wireOp",EDGE,"E759.right");var subQ1=sQuery(id+"F35.wireOp",EDGE,"E748.top");var subQ2=makeQuery(id+"F35.imprint","INTERSECT",VERTEX,{"derivedFrom":[subQ1,subQ0]});Q4=makeQuery(id+"F35.imprint","IMPRINT",FACE,{"disambiguationData":[TD([[makeQuery(id+"F35.imprint","IMPRINT",EDGE,{"disambiguationData":[TD([[subQ2,-1.0]])],"derivedFrom":subQ1}),-1.0]])]});}
            var Q5;
            {var subQ0=sQuery(id+"F35.wireOp",EDGE,"E757.right");var subQ1=sQuery(id+"F35.wireOp",EDGE,"E748.top");var subQ2=makeQuery(id+"F35.imprint","INTERSECT",VERTEX,{"derivedFrom":[subQ1,subQ0]});Q5=makeQuery(id+"F35.imprint","IMPRINT",FACE,{"disambiguationData":[TD([[makeQuery(id+"F35.imprint","IMPRINT",EDGE,{"disambiguationData":[TD([[subQ2,-1.0]])],"derivedFrom":subQ1}),-1.0]])]});}
            var Q6;
            {var subQ0=sQuery(id+"F35.wireOp",EDGE,"E757.left");var subQ1=sQuery(id+"F35.wireOp",EDGE,"E748.top");var subQ2=makeQuery(id+"F35.imprint","INTERSECT",VERTEX,{"derivedFrom":[subQ1,subQ0]});Q6=makeQuery(id+"F35.imprint","IMPRINT",FACE,{"disambiguationData":[TD([[makeQuery(id+"F35.imprint","IMPRINT",EDGE,{"disambiguationData":[TD([[subQ2,-1.0]])],"derivedFrom":subQ1}),-1.0]])]});}
            var Q7;
            {var subQ0=sQuery(id+"F35.wireOp",EDGE,"E758.right");var subQ1=sQuery(id+"F35.wireOp",EDGE,"E748.top");var subQ2=makeQuery(id+"F35.imprint","INTERSECT",VERTEX,{"derivedFrom":[subQ1,subQ0]});Q7=makeQuery(id+"F35.imprint","IMPRINT",FACE,{"disambiguationData":[TD([[makeQuery(id+"F35.imprint","IMPRINT",EDGE,{"disambiguationData":[TD([[subQ2,-1.0]])],"derivedFrom":subQ1}),-1.0]])]});}
            var Q8;
            {var subQ0=sQuery(id+"F35.wireOp",EDGE,"E757.right");var subQ1=sQuery(id+"F35.wireOp",EDGE,"E749.top");var subQ2=makeQuery(id+"F35.imprint","INTERSECT",VERTEX,{"derivedFrom":[subQ1,subQ0]});Q8=makeQuery(id+"F35.imprint","IMPRINT",FACE,{"disambiguationData":[TD([[makeQuery(id+"F35.imprint","IMPRINT",EDGE,{"disambiguationData":[TD([[subQ2,-1.0]])],"derivedFrom":subQ1}),-1.0]])]});}
            var Q9;
            {var subQ0=sQuery(id+"F35.wireOp",EDGE,"E757.left");var subQ1=sQuery(id+"F35.wireOp",EDGE,"E749.top");var subQ2=makeQuery(id+"F35.imprint","INTERSECT",VERTEX,{"derivedFrom":[subQ1,subQ0]});Q9=makeQuery(id+"F35.imprint","IMPRINT",FACE,{"disambiguationData":[TD([[makeQuery(id+"F35.imprint","IMPRINT",EDGE,{"disambiguationData":[TD([[subQ2,-1.0]])],"derivedFrom":subQ1}),-1.0]])]});}
            var Q10;
            {var subQ0=sQuery(id+"F35.wireOp",EDGE,"E758.right");var subQ1=sQuery(id+"F35.wireOp",EDGE,"E749.top");var subQ2=makeQuery(id+"F35.imprint","INTERSECT",VERTEX,{"derivedFrom":[subQ1,subQ0]});Q10=makeQuery(id+"F35.imprint","IMPRINT",FACE,{"disambiguationData":[TD([[makeQuery(id+"F35.imprint","IMPRINT",EDGE,{"disambiguationData":[TD([[subQ2,-1.0]])],"derivedFrom":subQ1}),-1.0]])]});}
            var Q11;
            {var subQ0=sQuery(id+"F35.wireOp",EDGE,"E759.right");var subQ1=sQuery(id+"F35.wireOp",EDGE,"E749.top");var subQ2=makeQuery(id+"F35.imprint","INTERSECT",VERTEX,{"derivedFrom":[subQ1,subQ0]});Q11=makeQuery(id+"F35.imprint","IMPRINT",FACE,{"disambiguationData":[TD([[makeQuery(id+"F35.imprint","IMPRINT",EDGE,{"disambiguationData":[TD([[subQ2,-1.0]])],"derivedFrom":subQ1}),-1.0]])]});}
            var Q12;
            {var subQ0=sQuery(id+"F35.wireOp",EDGE,"E759.left");var subQ1=sQuery(id+"F35.wireOp",EDGE,"E749.top");var subQ2=makeQuery(id+"F35.imprint","INTERSECT",VERTEX,{"derivedFrom":[subQ1,subQ0]});Q12=makeQuery(id+"F35.imprint","IMPRINT",FACE,{"disambiguationData":[TD([[makeQuery(id+"F35.imprint","IMPRINT",EDGE,{"disambiguationData":[TD([[subQ2,-1.0]])],"derivedFrom":subQ1}),-1.0]])]});}
            var Q13;
            {var subQ0=sQuery(id+"F35.wireOp",EDGE,"E759.left");var subQ1=sQuery(id+"F35.wireOp",EDGE,"E748.top");var subQ2=makeQuery(id+"F35.imprint","INTERSECT",VERTEX,{"derivedFrom":[subQ1,subQ0]});Q13=makeQuery(id+"F35.imprint","IMPRINT",FACE,{"disambiguationData":[TD([[makeQuery(id+"F35.imprint","IMPRINT",EDGE,{"disambiguationData":[TD([[subQ2,-1.0]])],"derivedFrom":subQ1}),-1.0]])]});}
            var Q14;
            {var subQ0=sQuery(id+"F35.wireOp",EDGE,"E760.right");var subQ1=sQuery(id+"F35.wireOp",EDGE,"E748.top");var subQ2=makeQuery(id+"F35.imprint","INTERSECT",VERTEX,{"derivedFrom":[subQ1,subQ0]});Q14=makeQuery(id+"F35.imprint","IMPRINT",FACE,{"disambiguationData":[TD([[makeQuery(id+"F35.imprint","IMPRINT",EDGE,{"disambiguationData":[TD([[subQ2,-1.0]])],"derivedFrom":subQ1}),-1.0]])]});}
            var Q15;
            {var subQ0=sQuery(id+"F35.wireOp",EDGE,"E760.right");var subQ1=sQuery(id+"F35.wireOp",EDGE,"E749.top");var subQ2=makeQuery(id+"F35.imprint","INTERSECT",VERTEX,{"derivedFrom":[subQ1,subQ0]});Q15=makeQuery(id+"F35.imprint","IMPRINT",FACE,{"disambiguationData":[TD([[makeQuery(id+"F35.imprint","IMPRINT",EDGE,{"disambiguationData":[TD([[subQ2,-1.0]])],"derivedFrom":subQ1}),-1.0]])]});}
            var Q16;
            {var subQ0=sQuery(id+"F35.wireOp",EDGE,"E760.right");var subQ1=sQuery(id+"F35.wireOp",EDGE,"E747.bottom");var subQ2=makeQuery(id+"F35.imprint","INTERSECT",VERTEX,{"derivedFrom":[subQ1,subQ0]});Q16=makeQuery(id+"F35.imprint","IMPRINT",FACE,{"disambiguationData":[TD([[makeQuery(id+"F35.imprint","IMPRINT",EDGE,{"disambiguationData":[TD([[subQ2,-1.0]])],"derivedFrom":subQ1}),-1.0]])]});}
            var Q17;
            {var subQ0=sQuery(id+"F35.wireOp",EDGE,"E759.left");var subQ1=sQuery(id+"F35.wireOp",EDGE,"E747.bottom");var subQ2=makeQuery(id+"F35.imprint","INTERSECT",VERTEX,{"derivedFrom":[subQ1,subQ0]});Q17=makeQuery(id+"F35.imprint","IMPRINT",FACE,{"disambiguationData":[TD([[makeQuery(id+"F35.imprint","IMPRINT",EDGE,{"disambiguationData":[TD([[subQ2,-1.0]])],"derivedFrom":subQ1}),-1.0]])]});}
            var Q18;
            {var subQ0=sQuery(id+"F35.wireOp",EDGE,"E753.left");var subQ1=sQuery(id+"F35.wireOp",EDGE,"E740.top");var subQ2=makeQuery(id+"F35.imprint","INTERSECT",VERTEX,{"derivedFrom":[subQ1,subQ0]});Q18=makeQuery(id+"F35.imprint","IMPRINT",FACE,{"disambiguationData":[TD([[makeQuery(id+"F35.imprint","IMPRINT",EDGE,{"disambiguationData":[TD([[subQ2,-1.0]])],"derivedFrom":subQ1}),-1.0]])]});}
            var Q19;
            {var subQ0=sQuery(id+"F35.wireOp",EDGE,"E754.right");var subQ1=sQuery(id+"F35.wireOp",EDGE,"E740.top");var subQ2=makeQuery(id+"F35.imprint","INTERSECT",VERTEX,{"derivedFrom":[subQ1,subQ0]});Q19=makeQuery(id+"F35.imprint","IMPRINT",FACE,{"disambiguationData":[TD([[makeQuery(id+"F35.imprint","IMPRINT",EDGE,{"disambiguationData":[TD([[subQ2,-1.0]])],"derivedFrom":subQ1}),-1.0]])]});}
            var Q20;
            {var subQ0=sQuery(id+"F35.wireOp",EDGE,"E753.left");var subQ1=sQuery(id+"F35.wireOp",EDGE,"E741.top");var subQ2=makeQuery(id+"F35.imprint","INTERSECT",VERTEX,{"derivedFrom":[subQ1,subQ0]});Q20=makeQuery(id+"F35.imprint","IMPRINT",FACE,{"disambiguationData":[TD([[makeQuery(id+"F35.imprint","IMPRINT",EDGE,{"disambiguationData":[TD([[subQ2,-1.0]])],"derivedFrom":subQ1}),-1.0]])]});}
            var Q21;
            {var subQ0=sQuery(id+"F35.wireOp",EDGE,"E753.left");var subQ1=sQuery(id+"F35.wireOp",EDGE,"E741.bottom");var subQ2=makeQuery(id+"F35.imprint","INTERSECT",VERTEX,{"derivedFrom":[subQ1,subQ0]});Q21=makeQuery(id+"F35.imprint","IMPRINT",FACE,{"disambiguationData":[TD([[makeQuery(id+"F35.imprint","IMPRINT",EDGE,{"disambiguationData":[TD([[subQ2,-1.0]])],"derivedFrom":subQ1}),-1.0]])]});}
            var Q22;
            {var subQ0=sQuery(id+"F35.wireOp",EDGE,"E754.right");var subQ1=sQuery(id+"F35.wireOp",EDGE,"E741.top");var subQ2=makeQuery(id+"F35.imprint","INTERSECT",VERTEX,{"derivedFrom":[subQ1,subQ0]});Q22=makeQuery(id+"F35.imprint","IMPRINT",FACE,{"disambiguationData":[TD([[makeQuery(id+"F35.imprint","IMPRINT",EDGE,{"disambiguationData":[TD([[subQ2,-1.0]])],"derivedFrom":subQ1}),-1.0]])]});}
            var Q23;
            {var subQ0=sQuery(id+"F35.wireOp",EDGE,"E754.right");var subQ1=sQuery(id+"F35.wireOp",EDGE,"E741.bottom");var subQ2=makeQuery(id+"F35.imprint","INTERSECT",VERTEX,{"derivedFrom":[subQ1,subQ0]});Q23=makeQuery(id+"F35.imprint","IMPRINT",FACE,{"disambiguationData":[TD([[makeQuery(id+"F35.imprint","IMPRINT",EDGE,{"disambiguationData":[TD([[subQ2,-1.0]])],"derivedFrom":subQ1}),-1.0]])]});}
            var Q24;
            {var subQ0=sQuery(id+"F35.wireOp",EDGE,"E753.left");var subQ1=sQuery(id+"F35.wireOp",EDGE,"E742.top");var subQ2=makeQuery(id+"F35.imprint","INTERSECT",VERTEX,{"derivedFrom":[subQ1,subQ0]});Q24=makeQuery(id+"F35.imprint","IMPRINT",FACE,{"disambiguationData":[TD([[makeQuery(id+"F35.imprint","IMPRINT",EDGE,{"disambiguationData":[TD([[subQ2,-1.0]])],"derivedFrom":subQ1}),-1.0]])]});}
            var Q25;
            {var subQ0=sQuery(id+"F35.wireOp",EDGE,"E754.right");var subQ1=sQuery(id+"F35.wireOp",EDGE,"E742.top");var subQ2=makeQuery(id+"F35.imprint","INTERSECT",VERTEX,{"derivedFrom":[subQ1,subQ0]});Q25=makeQuery(id+"F35.imprint","IMPRINT",FACE,{"disambiguationData":[TD([[makeQuery(id+"F35.imprint","IMPRINT",EDGE,{"disambiguationData":[TD([[subQ2,-1.0]])],"derivedFrom":subQ1}),-1.0]])]});}
            var Q26;
            {var subQ0=sQuery(id+"F35.wireOp",EDGE,"E753.left");var subQ1=sQuery(id+"F35.wireOp",EDGE,"E743.top");var subQ2=makeQuery(id+"F35.imprint","INTERSECT",VERTEX,{"derivedFrom":[subQ1,subQ0]});Q26=makeQuery(id+"F35.imprint","IMPRINT",FACE,{"disambiguationData":[TD([[makeQuery(id+"F35.imprint","IMPRINT",EDGE,{"disambiguationData":[TD([[subQ2,-1.0]])],"derivedFrom":subQ1}),-1.0]])]});}
            var Q27;
            {var subQ0=sQuery(id+"F35.wireOp",EDGE,"E753.left");var subQ1=sQuery(id+"F35.wireOp",EDGE,"E743.bottom");var subQ2=makeQuery(id+"F35.imprint","INTERSECT",VERTEX,{"derivedFrom":[subQ1,subQ0]});Q27=makeQuery(id+"F35.imprint","IMPRINT",FACE,{"disambiguationData":[TD([[makeQuery(id+"F35.imprint","IMPRINT",EDGE,{"disambiguationData":[TD([[subQ2,-1.0]])],"derivedFrom":subQ1}),-1.0]])]});}
            var Q28;
            {var subQ0=sQuery(id+"F35.wireOp",EDGE,"E754.right");var subQ1=sQuery(id+"F35.wireOp",EDGE,"E743.top");var subQ2=makeQuery(id+"F35.imprint","INTERSECT",VERTEX,{"derivedFrom":[subQ1,subQ0]});Q28=makeQuery(id+"F35.imprint","IMPRINT",FACE,{"disambiguationData":[TD([[makeQuery(id+"F35.imprint","IMPRINT",EDGE,{"disambiguationData":[TD([[subQ2,-1.0]])],"derivedFrom":subQ1}),-1.0]])]});}
            var Q29;
            {var subQ0=sQuery(id+"F35.wireOp",EDGE,"E754.right");var subQ1=sQuery(id+"F35.wireOp",EDGE,"E743.bottom");var subQ2=makeQuery(id+"F35.imprint","INTERSECT",VERTEX,{"derivedFrom":[subQ1,subQ0]});Q29=makeQuery(id+"F35.imprint","IMPRINT",FACE,{"disambiguationData":[TD([[makeQuery(id+"F35.imprint","IMPRINT",EDGE,{"disambiguationData":[TD([[subQ2,-1.0]])],"derivedFrom":subQ1}),-1.0]])]});}
            var Q30;
            {var subQ0=sQuery(id+"F35.wireOp",EDGE,"E755.right");var subQ1=sQuery(id+"F35.wireOp",EDGE,"E740.top");var subQ2=makeQuery(id+"F35.imprint","INTERSECT",VERTEX,{"derivedFrom":[subQ1,subQ0]});Q30=makeQuery(id+"F35.imprint","IMPRINT",FACE,{"disambiguationData":[TD([[makeQuery(id+"F35.imprint","IMPRINT",EDGE,{"disambiguationData":[TD([[subQ2,-1.0]])],"derivedFrom":subQ1}),-1.0]])]});}
            var Q31;
            {var subQ0=sQuery(id+"F35.wireOp",EDGE,"E755.right");var subQ1=sQuery(id+"F35.wireOp",EDGE,"E741.top");var subQ2=makeQuery(id+"F35.imprint","INTERSECT",VERTEX,{"derivedFrom":[subQ1,subQ0]});Q31=makeQuery(id+"F35.imprint","IMPRINT",FACE,{"disambiguationData":[TD([[makeQuery(id+"F35.imprint","IMPRINT",EDGE,{"disambiguationData":[TD([[subQ2,-1.0]])],"derivedFrom":subQ1}),-1.0]])]});}
            var Q32;
            {var subQ0=sQuery(id+"F35.wireOp",EDGE,"E755.right");var subQ1=sQuery(id+"F35.wireOp",EDGE,"E741.bottom");var subQ2=makeQuery(id+"F35.imprint","INTERSECT",VERTEX,{"derivedFrom":[subQ1,subQ0]});Q32=makeQuery(id+"F35.imprint","IMPRINT",FACE,{"disambiguationData":[TD([[makeQuery(id+"F35.imprint","IMPRINT",EDGE,{"disambiguationData":[TD([[subQ2,-1.0]])],"derivedFrom":subQ1}),-1.0]])]});}
            var Q33;
            {var subQ0=sQuery(id+"F35.wireOp",EDGE,"E755.right");var subQ1=sQuery(id+"F35.wireOp",EDGE,"E742.top");var subQ2=makeQuery(id+"F35.imprint","INTERSECT",VERTEX,{"derivedFrom":[subQ1,subQ0]});Q33=makeQuery(id+"F35.imprint","IMPRINT",FACE,{"disambiguationData":[TD([[makeQuery(id+"F35.imprint","IMPRINT",EDGE,{"disambiguationData":[TD([[subQ2,-1.0]])],"derivedFrom":subQ1}),-1.0]])]});}
            var Q34;
            {var subQ0=sQuery(id+"F35.wireOp",EDGE,"E755.right");var subQ1=sQuery(id+"F35.wireOp",EDGE,"E743.top");var subQ2=makeQuery(id+"F35.imprint","INTERSECT",VERTEX,{"derivedFrom":[subQ1,subQ0]});Q34=makeQuery(id+"F35.imprint","IMPRINT",FACE,{"disambiguationData":[TD([[makeQuery(id+"F35.imprint","IMPRINT",EDGE,{"disambiguationData":[TD([[subQ2,-1.0]])],"derivedFrom":subQ1}),-1.0]])]});}
            var Q35;
            {var subQ0=sQuery(id+"F35.wireOp",EDGE,"E755.right");var subQ1=sQuery(id+"F35.wireOp",EDGE,"E743.bottom");var subQ2=makeQuery(id+"F35.imprint","INTERSECT",VERTEX,{"derivedFrom":[subQ1,subQ0]});Q35=makeQuery(id+"F35.imprint","IMPRINT",FACE,{"disambiguationData":[TD([[makeQuery(id+"F35.imprint","IMPRINT",EDGE,{"disambiguationData":[TD([[subQ2,-1.0]])],"derivedFrom":subQ1}),-1.0]])]});}
            var Q36;
            {var subQ0=sQuery(id+"F35.wireOp",EDGE,"E753.right");var subQ1=sQuery(id+"F35.wireOp",EDGE,"E740.top");var subQ2=makeQuery(id+"F35.imprint","INTERSECT",VERTEX,{"derivedFrom":[subQ1,subQ0]});Q36=makeQuery(id+"F35.imprint","IMPRINT",FACE,{"disambiguationData":[TD([[makeQuery(id+"F35.imprint","IMPRINT",EDGE,{"disambiguationData":[TD([[subQ2,-1.0]])],"derivedFrom":subQ1}),-1.0]])]});}
            var Q37;
            {var subQ0=sQuery(id+"F35.wireOp",EDGE,"E753.right");var subQ1=sQuery(id+"F35.wireOp",EDGE,"E741.top");var subQ2=makeQuery(id+"F35.imprint","INTERSECT",VERTEX,{"derivedFrom":[subQ1,subQ0]});Q37=makeQuery(id+"F35.imprint","IMPRINT",FACE,{"disambiguationData":[TD([[makeQuery(id+"F35.imprint","IMPRINT",EDGE,{"disambiguationData":[TD([[subQ2,-1.0]])],"derivedFrom":subQ1}),-1.0]])]});}
            var Q38;
            {var subQ0=sQuery(id+"F35.wireOp",EDGE,"E753.right");var subQ1=sQuery(id+"F35.wireOp",EDGE,"E741.bottom");var subQ2=makeQuery(id+"F35.imprint","INTERSECT",VERTEX,{"derivedFrom":[subQ1,subQ0]});Q38=makeQuery(id+"F35.imprint","IMPRINT",FACE,{"disambiguationData":[TD([[makeQuery(id+"F35.imprint","IMPRINT",EDGE,{"disambiguationData":[TD([[subQ2,-1.0]])],"derivedFrom":subQ1}),-1.0]])]});}
            var Q39;
            {var subQ0=sQuery(id+"F35.wireOp",EDGE,"E753.right");var subQ1=sQuery(id+"F35.wireOp",EDGE,"E742.top");var subQ2=makeQuery(id+"F35.imprint","INTERSECT",VERTEX,{"derivedFrom":[subQ1,subQ0]});Q39=makeQuery(id+"F35.imprint","IMPRINT",FACE,{"disambiguationData":[TD([[makeQuery(id+"F35.imprint","IMPRINT",EDGE,{"disambiguationData":[TD([[subQ2,-1.0]])],"derivedFrom":subQ1}),-1.0]])]});}
            var Q40;
            {var subQ0=sQuery(id+"F35.wireOp",EDGE,"E753.right");var subQ1=sQuery(id+"F35.wireOp",EDGE,"E743.top");var subQ2=makeQuery(id+"F35.imprint","INTERSECT",VERTEX,{"derivedFrom":[subQ1,subQ0]});Q40=makeQuery(id+"F35.imprint","IMPRINT",FACE,{"disambiguationData":[TD([[makeQuery(id+"F35.imprint","IMPRINT",EDGE,{"disambiguationData":[TD([[subQ2,-1.0]])],"derivedFrom":subQ1}),-1.0]])]});}
            var Q41;
            {var subQ0=sQuery(id+"F35.wireOp",EDGE,"E753.right");var subQ1=sQuery(id+"F35.wireOp",EDGE,"E743.bottom");var subQ2=makeQuery(id+"F35.imprint","INTERSECT",VERTEX,{"derivedFrom":[subQ1,subQ0]});Q41=makeQuery(id+"F35.imprint","IMPRINT",FACE,{"disambiguationData":[TD([[makeQuery(id+"F35.imprint","IMPRINT",EDGE,{"disambiguationData":[TD([[subQ2,-1.0]])],"derivedFrom":subQ1}),-1.0]])]});}
            var Q42;
            {var subQ0=sQuery(id+"F35.wireOp",EDGE,"E757.right");var subQ1=sQuery(id+"F35.wireOp",EDGE,"E747.top");var subQ2=makeQuery(id+"F35.imprint","INTERSECT",VERTEX,{"derivedFrom":[subQ1,subQ0]});Q42=makeQuery(id+"F35.imprint","IMPRINT",FACE,{"disambiguationData":[TD([[makeQuery(id+"F35.imprint","IMPRINT",EDGE,{"disambiguationData":[TD([[subQ2,-1.0]])],"derivedFrom":subQ1}),-1.0]])]});}
            var Q43;
            {var subQ0=sQuery(id+"F35.wireOp",EDGE,"E757.left");var subQ1=sQuery(id+"F35.wireOp",EDGE,"E747.top");var subQ2=makeQuery(id+"F35.imprint","INTERSECT",VERTEX,{"derivedFrom":[subQ1,subQ0]});Q43=makeQuery(id+"F35.imprint","IMPRINT",FACE,{"disambiguationData":[TD([[makeQuery(id+"F35.imprint","IMPRINT",EDGE,{"disambiguationData":[TD([[subQ2,-1.0]])],"derivedFrom":subQ1}),-1.0]])]});}
            var Q44;
            {var subQ0=sQuery(id+"F35.wireOp",EDGE,"E758.right");var subQ1=sQuery(id+"F35.wireOp",EDGE,"E747.top");var subQ2=makeQuery(id+"F35.imprint","INTERSECT",VERTEX,{"derivedFrom":[subQ1,subQ0]});Q44=makeQuery(id+"F35.imprint","IMPRINT",FACE,{"disambiguationData":[TD([[makeQuery(id+"F35.imprint","IMPRINT",EDGE,{"disambiguationData":[TD([[subQ2,-1.0]])],"derivedFrom":subQ1}),-1.0]])]});}
            var Q45;
            {var subQ0=sQuery(id+"F35.wireOp",EDGE,"E759.right");var subQ1=sQuery(id+"F35.wireOp",EDGE,"E747.top");var subQ2=makeQuery(id+"F35.imprint","INTERSECT",VERTEX,{"derivedFrom":[subQ1,subQ0]});Q45=makeQuery(id+"F35.imprint","IMPRINT",FACE,{"disambiguationData":[TD([[makeQuery(id+"F35.imprint","IMPRINT",EDGE,{"disambiguationData":[TD([[subQ2,-1.0]])],"derivedFrom":subQ1}),-1.0]])]});}
            var Q46;
            {var subQ0=sQuery(id+"F35.wireOp",EDGE,"E759.left");var subQ1=sQuery(id+"F35.wireOp",EDGE,"E747.top");var subQ2=makeQuery(id+"F35.imprint","INTERSECT",VERTEX,{"derivedFrom":[subQ1,subQ0]});Q46=makeQuery(id+"F35.imprint","IMPRINT",FACE,{"disambiguationData":[TD([[makeQuery(id+"F35.imprint","IMPRINT",EDGE,{"disambiguationData":[TD([[subQ2,-1.0]])],"derivedFrom":subQ1}),-1.0]])]});}
            var Q47;
            {var subQ0=sQuery(id+"F35.wireOp",EDGE,"E760.right");var subQ1=sQuery(id+"F35.wireOp",EDGE,"E747.top");var subQ2=makeQuery(id+"F35.imprint","INTERSECT",VERTEX,{"derivedFrom":[subQ1,subQ0]});Q47=makeQuery(id+"F35.imprint","IMPRINT",FACE,{"disambiguationData":[TD([[makeQuery(id+"F35.imprint","IMPRINT",EDGE,{"disambiguationData":[TD([[subQ2,-1.0]])],"derivedFrom":subQ1}),-1.0]])]});}
            var Q48;
            {var subQ0=sQuery(id+"F35.wireOp",EDGE,"E757.right");var subQ1=sQuery(id+"F35.wireOp",EDGE,"E749.bottom");var subQ2=makeQuery(id+"F35.imprint","INTERSECT",VERTEX,{"derivedFrom":[subQ1,subQ0]});Q48=makeQuery(id+"F35.imprint","IMPRINT",FACE,{"disambiguationData":[TD([[makeQuery(id+"F35.imprint","IMPRINT",EDGE,{"disambiguationData":[TD([[subQ2,-1.0]])],"derivedFrom":subQ1}),-1.0]])]});}
            var Q49;
            {var subQ0=sQuery(id+"F35.wireOp",EDGE,"E757.left");var subQ1=sQuery(id+"F35.wireOp",EDGE,"E749.bottom");var subQ2=makeQuery(id+"F35.imprint","INTERSECT",VERTEX,{"derivedFrom":[subQ1,subQ0]});Q49=makeQuery(id+"F35.imprint","IMPRINT",FACE,{"disambiguationData":[TD([[makeQuery(id+"F35.imprint","IMPRINT",EDGE,{"disambiguationData":[TD([[subQ2,-1.0]])],"derivedFrom":subQ1}),-1.0]])]});}
            var Q50;
            {var subQ0=sQuery(id+"F35.wireOp",EDGE,"E758.right");var subQ1=sQuery(id+"F35.wireOp",EDGE,"E749.bottom");var subQ2=makeQuery(id+"F35.imprint","INTERSECT",VERTEX,{"derivedFrom":[subQ1,subQ0]});Q50=makeQuery(id+"F35.imprint","IMPRINT",FACE,{"disambiguationData":[TD([[makeQuery(id+"F35.imprint","IMPRINT",EDGE,{"disambiguationData":[TD([[subQ2,-1.0]])],"derivedFrom":subQ1}),-1.0]])]});}
            var Q51;
            {var subQ0=sQuery(id+"F35.wireOp",EDGE,"E759.right");var subQ1=sQuery(id+"F35.wireOp",EDGE,"E749.bottom");var subQ2=makeQuery(id+"F35.imprint","INTERSECT",VERTEX,{"derivedFrom":[subQ1,subQ0]});Q51=makeQuery(id+"F35.imprint","IMPRINT",FACE,{"disambiguationData":[TD([[makeQuery(id+"F35.imprint","IMPRINT",EDGE,{"disambiguationData":[TD([[subQ2,-1.0]])],"derivedFrom":subQ1}),-1.0]])]});}
            var Q52;
            {var subQ0=sQuery(id+"F35.wireOp",EDGE,"E759.left");var subQ1=sQuery(id+"F35.wireOp",EDGE,"E749.bottom");var subQ2=makeQuery(id+"F35.imprint","INTERSECT",VERTEX,{"derivedFrom":[subQ1,subQ0]});Q52=makeQuery(id+"F35.imprint","IMPRINT",FACE,{"disambiguationData":[TD([[makeQuery(id+"F35.imprint","IMPRINT",EDGE,{"disambiguationData":[TD([[subQ2,-1.0]])],"derivedFrom":subQ1}),-1.0]])]});}
            var Q53;
            {var subQ0=sQuery(id+"F35.wireOp",EDGE,"E760.right");var subQ1=sQuery(id+"F35.wireOp",EDGE,"E749.bottom");var subQ2=makeQuery(id+"F35.imprint","INTERSECT",VERTEX,{"derivedFrom":[subQ1,subQ0]});Q53=makeQuery(id+"F35.imprint","IMPRINT",FACE,{"disambiguationData":[TD([[makeQuery(id+"F35.imprint","IMPRINT",EDGE,{"disambiguationData":[TD([[subQ2,-1.0]])],"derivedFrom":subQ1}),-1.0]])]});}
            var Q54;
            {var subQ0=sQuery(id+"F35.wireOp",EDGE,"E755.left");var subQ1=sQuery(id+"F35.wireOp",EDGE,"E743.bottom");var subQ2=makeQuery(id+"F35.imprint","INTERSECT",VERTEX,{"derivedFrom":[subQ1,subQ0]});Q54=makeQuery(id+"F35.imprint","IMPRINT",FACE,{"disambiguationData":[TD([[makeQuery(id+"F35.imprint","IMPRINT",EDGE,{"disambiguationData":[TD([[subQ2,-1.0]])],"derivedFrom":subQ1}),-1.0]])]});}
            var Q55;
            {var subQ0=sQuery(id+"F35.wireOp",EDGE,"E755.left");var subQ1=sQuery(id+"F35.wireOp",EDGE,"E743.top");var subQ2=makeQuery(id+"F35.imprint","INTERSECT",VERTEX,{"derivedFrom":[subQ1,subQ0]});Q55=makeQuery(id+"F35.imprint","IMPRINT",FACE,{"disambiguationData":[TD([[makeQuery(id+"F35.imprint","IMPRINT",EDGE,{"disambiguationData":[TD([[subQ2,-1.0]])],"derivedFrom":subQ1}),-1.0]])]});}
            var Q56;
            {var subQ0=sQuery(id+"F35.wireOp",EDGE,"E755.left");var subQ1=sQuery(id+"F35.wireOp",EDGE,"E742.top");var subQ2=makeQuery(id+"F35.imprint","INTERSECT",VERTEX,{"derivedFrom":[subQ1,subQ0]});Q56=makeQuery(id+"F35.imprint","IMPRINT",FACE,{"disambiguationData":[TD([[makeQuery(id+"F35.imprint","IMPRINT",EDGE,{"disambiguationData":[TD([[subQ2,-1.0]])],"derivedFrom":subQ1}),-1.0]])]});}
            var Q57;
            {var subQ0=sQuery(id+"F35.wireOp",EDGE,"E755.left");var subQ1=sQuery(id+"F35.wireOp",EDGE,"E741.bottom");var subQ2=makeQuery(id+"F35.imprint","INTERSECT",VERTEX,{"derivedFrom":[subQ1,subQ0]});Q57=makeQuery(id+"F35.imprint","IMPRINT",FACE,{"disambiguationData":[TD([[makeQuery(id+"F35.imprint","IMPRINT",EDGE,{"disambiguationData":[TD([[subQ2,-1.0]])],"derivedFrom":subQ1}),-1.0]])]});}
            var Q58;
            {var subQ0=sQuery(id+"F35.wireOp",EDGE,"E755.left");var subQ1=sQuery(id+"F35.wireOp",EDGE,"E741.top");var subQ2=makeQuery(id+"F35.imprint","INTERSECT",VERTEX,{"derivedFrom":[subQ1,subQ0]});Q58=makeQuery(id+"F35.imprint","IMPRINT",FACE,{"disambiguationData":[TD([[makeQuery(id+"F35.imprint","IMPRINT",EDGE,{"disambiguationData":[TD([[subQ2,-1.0]])],"derivedFrom":subQ1}),-1.0]])]});}
            var Q59;
            {var subQ0=sQuery(id+"F35.wireOp",EDGE,"E755.left");var subQ1=sQuery(id+"F35.wireOp",EDGE,"E740.top");var subQ2=makeQuery(id+"F35.imprint","INTERSECT",VERTEX,{"derivedFrom":[subQ1,subQ0]});Q59=makeQuery(id+"F35.imprint","IMPRINT",FACE,{"disambiguationData":[TD([[makeQuery(id+"F35.imprint","IMPRINT",EDGE,{"disambiguationData":[TD([[subQ2,-1.0]])],"derivedFrom":subQ1}),-1.0]])]});}
            var Q60;
            {var subQ0=sQuery(id+"F35.wireOp",EDGE,"E850.MirrorCS");var subQ1=sQuery(id+"F35.wireOp",EDGE,"E830.MirrorCS");var subQ2=makeQuery(id+"F35.imprint","INTERSECT",VERTEX,{"derivedFrom":[subQ1,subQ0]});Q60=makeQuery(id+"F35.imprint","IMPRINT",FACE,{"disambiguationData":[TD([[makeQuery(id+"F35.imprint","IMPRINT",EDGE,{"disambiguationData":[TD([[subQ2,-1.0]])],"derivedFrom":subQ1}),1.0]])]});}
            var Q61;
            {var subQ0=sQuery(id+"F35.wireOp",EDGE,"E851.MirrorCS");var subQ1=sQuery(id+"F35.wireOp",EDGE,"E718.top");var subQ2=makeQuery(id+"F35.imprint","INTERSECT",VERTEX,{"derivedFrom":[subQ1,subQ0]});Q61=makeQuery(id+"F35.imprint","IMPRINT",FACE,{"disambiguationData":[TD([[makeQuery(id+"F35.imprint","IMPRINT",EDGE,{"disambiguationData":[TD([[subQ2,-1.0]])],"derivedFrom":subQ1}),-1.0]])]});}
            var Q62;
            {var subQ0=sQuery(id+"F35.wireOp",EDGE,"E851.MirrorCS");var subQ1=sQuery(id+"F35.wireOp",EDGE,"E718.top");var subQ2=makeQuery(id+"F35.imprint","INTERSECT",VERTEX,{"derivedFrom":[subQ1,subQ0]});Q62=makeQuery(id+"F35.imprint","IMPRINT",FACE,{"disambiguationData":[TD([[makeQuery(id+"F35.imprint","IMPRINT",EDGE,{"disambiguationData":[TD([[subQ2,-1.0]])],"derivedFrom":subQ1}),1.0]])]});}
            var Q63;
            {var subQ0=sQuery(id+"F35.wireOp",EDGE,"E850.MirrorCS");var subQ1=sQuery(id+"F35.wireOp",EDGE,"E828.MirrorCS");var subQ2=makeQuery(id+"F35.imprint","INTERSECT",VERTEX,{"derivedFrom":[subQ1,subQ0]});Q63=makeQuery(id+"F35.imprint","IMPRINT",FACE,{"disambiguationData":[TD([[makeQuery(id+"F35.imprint","IMPRINT",EDGE,{"disambiguationData":[TD([[subQ2,-1.0]])],"derivedFrom":subQ1}),1.0]])]});}
            var Q64;
            {var subQ0=sQuery(id+"F35.wireOp",EDGE,"E850.MirrorCS");var subQ1=sQuery(id+"F35.wireOp",EDGE,"E827.MirrorCS");var subQ2=makeQuery(id+"F35.imprint","INTERSECT",VERTEX,{"derivedFrom":[subQ1,subQ0]});Q64=makeQuery(id+"F35.imprint","IMPRINT",FACE,{"disambiguationData":[TD([[makeQuery(id+"F35.imprint","IMPRINT",EDGE,{"disambiguationData":[TD([[subQ2,-1.0]])],"derivedFrom":subQ1}),1.0]])]});}
            var Q65;
            {var subQ0=sQuery(id+"F35.wireOp",EDGE,"E770.left");var subQ1=sQuery(id+"F35.wireOp",EDGE,"E736.top");var subQ2=makeQuery(id+"F35.imprint","INTERSECT",VERTEX,{"derivedFrom":[subQ1,subQ0]});Q65=makeQuery(id+"F35.imprint","IMPRINT",FACE,{"disambiguationData":[TD([[makeQuery(id+"F35.imprint","IMPRINT",EDGE,{"disambiguationData":[TD([[subQ2,-1.0]])],"derivedFrom":subQ1}),-1.0]])]});}
            var Q66;
            {var subQ1=sQuery(id+"F35.wireOp",EDGE,"E736.top");var subQ3=sQuery(id+"F35.wireOp",EDGE,"E769.right");var subQ4=makeQuery(id+"F35.imprint","INTERSECT",VERTEX,{"derivedFrom":[subQ1,subQ3]});Q66=makeQuery(id+"F35.imprint","IMPRINT",FACE,{"disambiguationData":[TD([[makeQuery(id+"F35.imprint","IMPRINT",EDGE,{"disambiguationData":[TD([[subQ4,-1.0]])],"derivedFrom":subQ3}),1.0]])]});}
            var Q67;
            {var subQ0=sQuery(id+"F35.wireOp",EDGE,"E770.right");var subQ1=sQuery(id+"F35.wireOp",EDGE,"E736.top");var subQ2=makeQuery(id+"F35.imprint","INTERSECT",VERTEX,{"derivedFrom":[subQ1,subQ0]});Q67=makeQuery(id+"F35.imprint","IMPRINT",FACE,{"disambiguationData":[TD([[makeQuery(id+"F35.imprint","IMPRINT",EDGE,{"disambiguationData":[TD([[subQ2,-1.0]])],"derivedFrom":subQ1}),-1.0]])]});}
            var Q68;
            {var subQ0=sQuery(id+"F35.wireOp",EDGE,"E771.right");var subQ1=sQuery(id+"F35.wireOp",EDGE,"E736.top");var subQ2=makeQuery(id+"F35.imprint","INTERSECT",VERTEX,{"derivedFrom":[subQ1,subQ0]});Q68=makeQuery(id+"F35.imprint","IMPRINT",FACE,{"disambiguationData":[TD([[makeQuery(id+"F35.imprint","IMPRINT",EDGE,{"disambiguationData":[TD([[subQ2,-1.0]])],"derivedFrom":subQ1}),-1.0]])]});}
            var Q69;
            {var subQ0=sQuery(id+"F35.wireOp",EDGE,"E773.MirrorCS");var subQ5=sQuery(id+"F35.wireOp",EDGE,"E777.MirrorCS");var subQ6=makeQuery(id+"F35.imprint","INTERSECT",VERTEX,{"derivedFrom":[subQ0,subQ5]});Q69=makeQuery(id+"F35.imprint","IMPRINT",FACE,{"disambiguationData":[TD([[makeQuery(id+"F35.imprint","IMPRINT",EDGE,{"disambiguationData":[TD([[subQ6,-1.0]])],"derivedFrom":subQ5}),-1.0]])]});}
            var Q70;
            {var subQ0=sQuery(id+"F35.wireOp",EDGE,"E796.MirrorCS");var subQ1=sQuery(id+"F35.wireOp",EDGE,"E773.MirrorCS");var subQ2=makeQuery(id+"F35.imprint","INTERSECT",VERTEX,{"derivedFrom":[subQ1,subQ0]});Q70=makeQuery(id+"F35.imprint","IMPRINT",FACE,{"disambiguationData":[TD([[makeQuery(id+"F35.imprint","IMPRINT",EDGE,{"disambiguationData":[TD([[subQ2,-1.0]])],"derivedFrom":subQ1}),1.0]])]});}
            var Q71;
            {var subQ0=sQuery(id+"F35.wireOp",EDGE,"E764.right");var subQ1=sQuery(id+"F35.wireOp",EDGE,"E742.top");var subQ2=makeQuery(id+"F35.imprint","INTERSECT",VERTEX,{"derivedFrom":[subQ1,subQ0]});Q71=makeQuery(id+"F35.imprint","IMPRINT",FACE,{"disambiguationData":[TD([[makeQuery(id+"F35.imprint","IMPRINT",EDGE,{"disambiguationData":[TD([[subQ2,-1.0]])],"derivedFrom":subQ1}),-1.0]])]});}
            var Q72;
            {var subQ0=sQuery(id+"F35.wireOp",EDGE,"E764.right");var subQ1=sQuery(id+"F35.wireOp",EDGE,"E741.bottom");var subQ2=makeQuery(id+"F35.imprint","INTERSECT",VERTEX,{"derivedFrom":[subQ1,subQ0]});Q72=makeQuery(id+"F35.imprint","IMPRINT",FACE,{"disambiguationData":[TD([[makeQuery(id+"F35.imprint","IMPRINT",EDGE,{"disambiguationData":[TD([[subQ2,-1.0]])],"derivedFrom":subQ1}),-1.0]])]});}
            var Q73;
            {var subQ0=sQuery(id+"F35.wireOp",EDGE,"E764.right");var subQ1=sQuery(id+"F35.wireOp",EDGE,"E741.top");var subQ2=makeQuery(id+"F35.imprint","INTERSECT",VERTEX,{"derivedFrom":[subQ1,subQ0]});Q73=makeQuery(id+"F35.imprint","IMPRINT",FACE,{"disambiguationData":[TD([[makeQuery(id+"F35.imprint","IMPRINT",EDGE,{"disambiguationData":[TD([[subQ2,-1.0]])],"derivedFrom":subQ1}),-1.0]])]});}
            var Q74;
            {var subQ0=sQuery(id+"F35.wireOp",EDGE,"E764.right");var subQ1=sQuery(id+"F35.wireOp",EDGE,"E740.top");var subQ2=makeQuery(id+"F35.imprint","INTERSECT",VERTEX,{"derivedFrom":[subQ1,subQ0]});Q74=makeQuery(id+"F35.imprint","IMPRINT",FACE,{"disambiguationData":[TD([[makeQuery(id+"F35.imprint","IMPRINT",EDGE,{"disambiguationData":[TD([[subQ2,-1.0]])],"derivedFrom":subQ1}),-1.0]])]});}
            var Q75;
            {var subQ0=sQuery(id+"F35.wireOp",EDGE,"E764.right");var subQ1=sQuery(id+"F35.wireOp",EDGE,"E739.bottom");var subQ2=makeQuery(id+"F35.imprint","INTERSECT",VERTEX,{"derivedFrom":[subQ1,subQ0]});Q75=makeQuery(id+"F35.imprint","IMPRINT",FACE,{"disambiguationData":[TD([[makeQuery(id+"F35.imprint","IMPRINT",EDGE,{"disambiguationData":[TD([[subQ2,-1.0]])],"derivedFrom":subQ1}),-1.0]])]});}
            var Q76;
            {var subQ0=sQuery(id+"F35.wireOp",EDGE,"E764.right");var subQ1=sQuery(id+"F35.wireOp",EDGE,"E739.top");var subQ2=makeQuery(id+"F35.imprint","INTERSECT",VERTEX,{"derivedFrom":[subQ1,subQ0]});Q76=makeQuery(id+"F35.imprint","IMPRINT",FACE,{"disambiguationData":[TD([[makeQuery(id+"F35.imprint","IMPRINT",EDGE,{"disambiguationData":[TD([[subQ2,-1.0]])],"derivedFrom":subQ1}),-1.0]])]});}
            var Q77;
            {var subQ0=sQuery(id+"F35.wireOp",EDGE,"E842.MirrorCS");var subQ1=sQuery(id+"F35.wireOp",EDGE,"E825.MirrorCS");var subQ2=makeQuery(id+"F35.imprint","INTERSECT",VERTEX,{"derivedFrom":[subQ1,subQ0]});Q77=makeQuery(id+"F35.imprint","IMPRINT",FACE,{"disambiguationData":[TD([[makeQuery(id+"F35.imprint","IMPRINT",EDGE,{"disambiguationData":[TD([[subQ2,-1.0]])],"derivedFrom":subQ1}),1.0]])]});}
            var Q78;
            {var subQ0=sQuery(id+"F35.wireOp",EDGE,"E843.MirrorCS");var subQ1=sQuery(id+"F35.wireOp",EDGE,"E825.MirrorCS");var subQ2=makeQuery(id+"F35.imprint","INTERSECT",VERTEX,{"derivedFrom":[subQ1,subQ0]});Q78=makeQuery(id+"F35.imprint","IMPRINT",FACE,{"disambiguationData":[TD([[makeQuery(id+"F35.imprint","IMPRINT",EDGE,{"disambiguationData":[TD([[subQ2,-1.0]])],"derivedFrom":subQ1}),1.0]])]});}
            var Q79;
            {var subQ0=sQuery(id+"F35.wireOp",EDGE,"E844.MirrorCS");var subQ1=sQuery(id+"F35.wireOp",EDGE,"E825.MirrorCS");var subQ2=makeQuery(id+"F35.imprint","INTERSECT",VERTEX,{"derivedFrom":[subQ1,subQ0]});Q79=makeQuery(id+"F35.imprint","IMPRINT",FACE,{"disambiguationData":[TD([[makeQuery(id+"F35.imprint","IMPRINT",EDGE,{"disambiguationData":[TD([[subQ2,-1.0]])],"derivedFrom":subQ1}),1.0]])]});}
            var Q80;
            {var subQ0=sQuery(id+"F35.wireOp",EDGE,"E845.MirrorCS");var subQ1=sQuery(id+"F35.wireOp",EDGE,"E825.MirrorCS");var subQ2=makeQuery(id+"F35.imprint","INTERSECT",VERTEX,{"derivedFrom":[subQ1,subQ0]});Q80=makeQuery(id+"F35.imprint","IMPRINT",FACE,{"disambiguationData":[TD([[makeQuery(id+"F35.imprint","IMPRINT",EDGE,{"disambiguationData":[TD([[subQ2,-1.0]])],"derivedFrom":subQ1}),1.0]])]});}
            extrude(context, id + "F36", {"entities" : qUnion([Q0, Q1, Q2, Q3, Q4, Q5, Q6, Q7, Q8, Q9, Q10, Q11, Q12, Q13, Q14, Q15, Q16, Q17, Q18, Q19, Q20, Q21, Q22, Q23, Q24, Q25, Q26, Q27, Q28, Q29, Q30, Q31, Q32, Q33, Q34, Q35, Q36, Q37, Q38, Q39, Q40, Q41, Q42, Q43, Q44, Q45, Q46, Q47, Q48, Q49, Q50, Q51, Q52, Q53, Q54, Q55, Q56, Q57, Q58, Q59, Q60, Q61, Q62, Q63, Q64, Q65, Q66, Q67, Q68, Q69, Q70, Q71, Q72, Q73, Q74, Q75, Q76, Q77, Q78, Q79, Q80]), "operationType" : NewBodyOperationType.REMOVE, "oppositeDirection" : true, "depth" : 1.5 * mm, "offsetDistance" : 25 * mm});
        }
        {
            var Q0;
            Q0=makeQuery(id+"F33.boolean.opBoolean","SPLIT",BODY,{"disambiguationData":[OD(0.0)],"derivedFrom":makeQuery(id+"F5.opExtrude","SWEPT_BODY",BODY,{"disambiguationData":[OSD([sQuery(id+"F2.wireOp",EDGE,"E74.top"),sQuery(id+"F2.wireOp",EDGE,"E75"),sQuery(id+"F2.wireOp",EDGE,"E76"),sQuery(id+"F2.wireOp",EDGE,"E77"),sQuery(id+"F2.wireOp",EDGE,"E89"),sQuery(id+"F2.wireOp",EDGE,"E90.trimOffspring"),sQuery(id+"F2.wireOp",EDGE,"E91"),sQuery(id+"F2.wireOp",EDGE,"E97.MirrorCS"),sQuery(id+"F2.wireOp",EDGE,"E98.MirrorCS"),sQuery(id+"F2.wireOp",EDGE,"E99.MirrorCS"),sQuery(id+"F2.wireOp",EDGE,"E100.MirrorCS"),sQuery(id+"F2.wireOp",EDGE,"E102.MirrorCS"),sQuery(id+"F2.wireOp",EDGE,"E103.MirrorCS"),sQuery(id+"F2.wireOp",EDGE,"E107.MirrorCS"),sQuery(id+"F2.wireOp",EDGE,"E108.MirrorCS"),sQuery(id+"F2.wireOp",EDGE,"E109.MirrorCS"),sQuery(id+"F2.wireOp",EDGE,"E110.MirrorCS"),sQuery(id+"F2.wireOp",EDGE,"E111.MirrorCS"),sQuery(id+"F2.wireOp",EDGE,"E115.MirrorCS"),sQuery(id+"F2.wireOp",EDGE,"E117.MirrorCS"),sQuery(id+"F2.wireOp",EDGE,"E121.MirrorCS"),sQuery(id+"F2.wireOp",EDGE,"E122.MirrorCS"),sQuery(id+"F2.wireOp",EDGE,"E123.MirrorCS"),sQuery(id+"F2.wireOp",EDGE,"E124.MirrorCS"),sQuery(id+"F2.wireOp",EDGE,"E126.MirrorCS"),sQuery(id+"F2.wireOp",EDGE,"E127.MirrorCS"),sQuery(id+"F2.wireOp",EDGE,"E128.MirrorCS"),sQuery(id+"F2.wireOp",EDGE,"E129.MirrorCS")])]})});
            var Q1;
            Q1=makeQuery(id+"F33.boolean.opBoolean","SPLIT",BODY,{"disambiguationData":[OD(5.0)],"derivedFrom":makeQuery(id+"F5.opExtrude","SWEPT_BODY",BODY,{"disambiguationData":[OSD([sQuery(id+"F2.wireOp",EDGE,"E74.top"),sQuery(id+"F2.wireOp",EDGE,"E75"),sQuery(id+"F2.wireOp",EDGE,"E76"),sQuery(id+"F2.wireOp",EDGE,"E77"),sQuery(id+"F2.wireOp",EDGE,"E89"),sQuery(id+"F2.wireOp",EDGE,"E90.trimOffspring"),sQuery(id+"F2.wireOp",EDGE,"E91"),sQuery(id+"F2.wireOp",EDGE,"E97.MirrorCS"),sQuery(id+"F2.wireOp",EDGE,"E98.MirrorCS"),sQuery(id+"F2.wireOp",EDGE,"E99.MirrorCS"),sQuery(id+"F2.wireOp",EDGE,"E100.MirrorCS"),sQuery(id+"F2.wireOp",EDGE,"E102.MirrorCS"),sQuery(id+"F2.wireOp",EDGE,"E103.MirrorCS"),sQuery(id+"F2.wireOp",EDGE,"E107.MirrorCS"),sQuery(id+"F2.wireOp",EDGE,"E108.MirrorCS"),sQuery(id+"F2.wireOp",EDGE,"E109.MirrorCS"),sQuery(id+"F2.wireOp",EDGE,"E110.MirrorCS"),sQuery(id+"F2.wireOp",EDGE,"E111.MirrorCS"),sQuery(id+"F2.wireOp",EDGE,"E115.MirrorCS"),sQuery(id+"F2.wireOp",EDGE,"E117.MirrorCS"),sQuery(id+"F2.wireOp",EDGE,"E121.MirrorCS"),sQuery(id+"F2.wireOp",EDGE,"E122.MirrorCS"),sQuery(id+"F2.wireOp",EDGE,"E123.MirrorCS"),sQuery(id+"F2.wireOp",EDGE,"E124.MirrorCS"),sQuery(id+"F2.wireOp",EDGE,"E126.MirrorCS"),sQuery(id+"F2.wireOp",EDGE,"E127.MirrorCS"),sQuery(id+"F2.wireOp",EDGE,"E128.MirrorCS"),sQuery(id+"F2.wireOp",EDGE,"E129.MirrorCS")])]})});
            var Q2;
            Q2=makeQuery(id+"F33.boolean.opBoolean","SPLIT",BODY,{"disambiguationData":[OD(4.0)],"derivedFrom":makeQuery(id+"F5.opExtrude","SWEPT_BODY",BODY,{"disambiguationData":[OSD([sQuery(id+"F2.wireOp",EDGE,"E74.top"),sQuery(id+"F2.wireOp",EDGE,"E75"),sQuery(id+"F2.wireOp",EDGE,"E76"),sQuery(id+"F2.wireOp",EDGE,"E77"),sQuery(id+"F2.wireOp",EDGE,"E89"),sQuery(id+"F2.wireOp",EDGE,"E90.trimOffspring"),sQuery(id+"F2.wireOp",EDGE,"E91"),sQuery(id+"F2.wireOp",EDGE,"E97.MirrorCS"),sQuery(id+"F2.wireOp",EDGE,"E98.MirrorCS"),sQuery(id+"F2.wireOp",EDGE,"E99.MirrorCS"),sQuery(id+"F2.wireOp",EDGE,"E100.MirrorCS"),sQuery(id+"F2.wireOp",EDGE,"E102.MirrorCS"),sQuery(id+"F2.wireOp",EDGE,"E103.MirrorCS"),sQuery(id+"F2.wireOp",EDGE,"E107.MirrorCS"),sQuery(id+"F2.wireOp",EDGE,"E108.MirrorCS"),sQuery(id+"F2.wireOp",EDGE,"E109.MirrorCS"),sQuery(id+"F2.wireOp",EDGE,"E110.MirrorCS"),sQuery(id+"F2.wireOp",EDGE,"E111.MirrorCS"),sQuery(id+"F2.wireOp",EDGE,"E115.MirrorCS"),sQuery(id+"F2.wireOp",EDGE,"E117.MirrorCS"),sQuery(id+"F2.wireOp",EDGE,"E121.MirrorCS"),sQuery(id+"F2.wireOp",EDGE,"E122.MirrorCS"),sQuery(id+"F2.wireOp",EDGE,"E123.MirrorCS"),sQuery(id+"F2.wireOp",EDGE,"E124.MirrorCS"),sQuery(id+"F2.wireOp",EDGE,"E126.MirrorCS"),sQuery(id+"F2.wireOp",EDGE,"E127.MirrorCS"),sQuery(id+"F2.wireOp",EDGE,"E128.MirrorCS"),sQuery(id+"F2.wireOp",EDGE,"E129.MirrorCS")])]})});
            var Q3;
            Q3=makeQuery(id+"F33.boolean.opBoolean","SPLIT",BODY,{"disambiguationData":[OD(3.0)],"derivedFrom":makeQuery(id+"F5.opExtrude","SWEPT_BODY",BODY,{"disambiguationData":[OSD([sQuery(id+"F2.wireOp",EDGE,"E74.top"),sQuery(id+"F2.wireOp",EDGE,"E75"),sQuery(id+"F2.wireOp",EDGE,"E76"),sQuery(id+"F2.wireOp",EDGE,"E77"),sQuery(id+"F2.wireOp",EDGE,"E89"),sQuery(id+"F2.wireOp",EDGE,"E90.trimOffspring"),sQuery(id+"F2.wireOp",EDGE,"E91"),sQuery(id+"F2.wireOp",EDGE,"E97.MirrorCS"),sQuery(id+"F2.wireOp",EDGE,"E98.MirrorCS"),sQuery(id+"F2.wireOp",EDGE,"E99.MirrorCS"),sQuery(id+"F2.wireOp",EDGE,"E100.MirrorCS"),sQuery(id+"F2.wireOp",EDGE,"E102.MirrorCS"),sQuery(id+"F2.wireOp",EDGE,"E103.MirrorCS"),sQuery(id+"F2.wireOp",EDGE,"E107.MirrorCS"),sQuery(id+"F2.wireOp",EDGE,"E108.MirrorCS"),sQuery(id+"F2.wireOp",EDGE,"E109.MirrorCS"),sQuery(id+"F2.wireOp",EDGE,"E110.MirrorCS"),sQuery(id+"F2.wireOp",EDGE,"E111.MirrorCS"),sQuery(id+"F2.wireOp",EDGE,"E115.MirrorCS"),sQuery(id+"F2.wireOp",EDGE,"E117.MirrorCS"),sQuery(id+"F2.wireOp",EDGE,"E121.MirrorCS"),sQuery(id+"F2.wireOp",EDGE,"E122.MirrorCS"),sQuery(id+"F2.wireOp",EDGE,"E123.MirrorCS"),sQuery(id+"F2.wireOp",EDGE,"E124.MirrorCS"),sQuery(id+"F2.wireOp",EDGE,"E126.MirrorCS"),sQuery(id+"F2.wireOp",EDGE,"E127.MirrorCS"),sQuery(id+"F2.wireOp",EDGE,"E128.MirrorCS"),sQuery(id+"F2.wireOp",EDGE,"E129.MirrorCS")])]})});
            var Q4;
            Q4=makeQuery(id+"F33.boolean.opBoolean","SPLIT",BODY,{"disambiguationData":[OD(2.0)],"derivedFrom":makeQuery(id+"F5.opExtrude","SWEPT_BODY",BODY,{"disambiguationData":[OSD([sQuery(id+"F2.wireOp",EDGE,"E74.top"),sQuery(id+"F2.wireOp",EDGE,"E75"),sQuery(id+"F2.wireOp",EDGE,"E76"),sQuery(id+"F2.wireOp",EDGE,"E77"),sQuery(id+"F2.wireOp",EDGE,"E89"),sQuery(id+"F2.wireOp",EDGE,"E90.trimOffspring"),sQuery(id+"F2.wireOp",EDGE,"E91"),sQuery(id+"F2.wireOp",EDGE,"E97.MirrorCS"),sQuery(id+"F2.wireOp",EDGE,"E98.MirrorCS"),sQuery(id+"F2.wireOp",EDGE,"E99.MirrorCS"),sQuery(id+"F2.wireOp",EDGE,"E100.MirrorCS"),sQuery(id+"F2.wireOp",EDGE,"E102.MirrorCS"),sQuery(id+"F2.wireOp",EDGE,"E103.MirrorCS"),sQuery(id+"F2.wireOp",EDGE,"E107.MirrorCS"),sQuery(id+"F2.wireOp",EDGE,"E108.MirrorCS"),sQuery(id+"F2.wireOp",EDGE,"E109.MirrorCS"),sQuery(id+"F2.wireOp",EDGE,"E110.MirrorCS"),sQuery(id+"F2.wireOp",EDGE,"E111.MirrorCS"),sQuery(id+"F2.wireOp",EDGE,"E115.MirrorCS"),sQuery(id+"F2.wireOp",EDGE,"E117.MirrorCS"),sQuery(id+"F2.wireOp",EDGE,"E121.MirrorCS"),sQuery(id+"F2.wireOp",EDGE,"E122.MirrorCS"),sQuery(id+"F2.wireOp",EDGE,"E123.MirrorCS"),sQuery(id+"F2.wireOp",EDGE,"E124.MirrorCS"),sQuery(id+"F2.wireOp",EDGE,"E126.MirrorCS"),sQuery(id+"F2.wireOp",EDGE,"E127.MirrorCS"),sQuery(id+"F2.wireOp",EDGE,"E128.MirrorCS"),sQuery(id+"F2.wireOp",EDGE,"E129.MirrorCS")])]})});
            deleteBodies(context, id + "F37", {"entities" : qUnion([Q0, Q1, Q2, Q3, Q4])});
        }
    });
